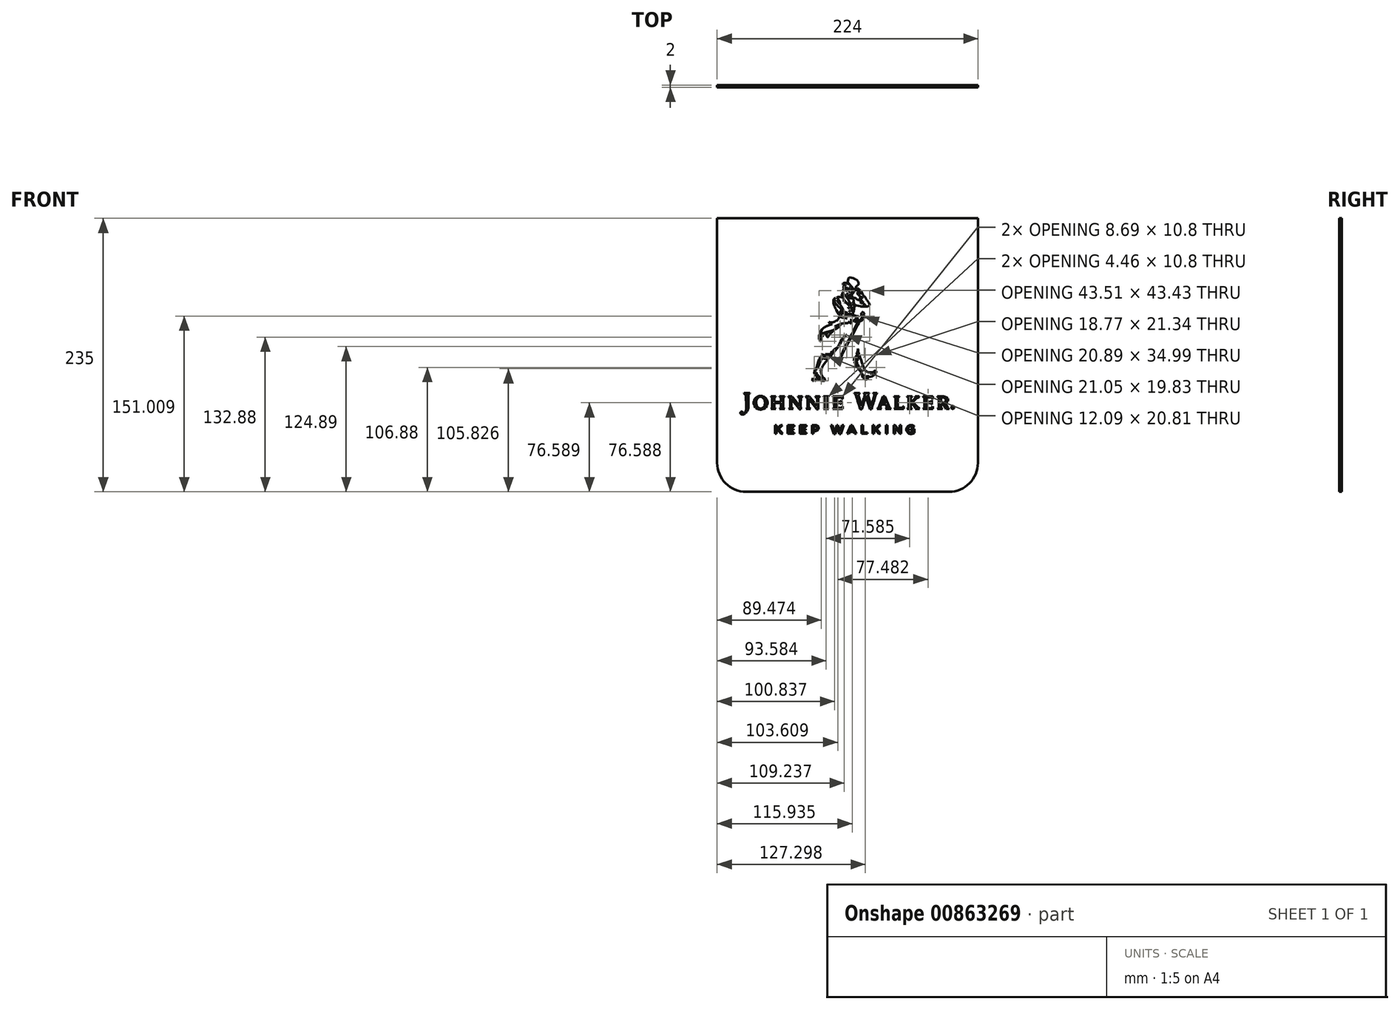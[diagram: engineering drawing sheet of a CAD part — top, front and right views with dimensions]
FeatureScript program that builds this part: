
annotation { "Feature Type Name" : "Feature", "Feature Type Description" : "" }
export const myFeature = defineFeature(function(context is Context, id is Id, definition is map)
    precondition{}
    {
        {
            var Q0;
            Q0=qCreatedBy(makeId("Front.planeOp"),FACE);
            var sketch = newSketch(context, id + "F0", { "sketchPlane" : qUnion([Q0])});
            skLineSegment(sketch, "E0", {"start": v(0.13, 0) * mm, "end": v(-86.87, 0) * mm});
            skLineSegment(sketch, "E1", {"start": v(0.13, 0) * mm, "end": v(87.13, 0) * mm});
            skLineSegment(sketch, "E2", {"start": v(0.13, 235) * mm, "end": v(-111.87, 235) * mm});
            skLineSegment(sketch, "E3", {"start": v(-111.87, 235) * mm, "end": v(-111.87, 25) * mm});
            skLineSegment(sketch, "E4", {"start": v(0.13, 235) * mm, "end": v(112.13, 235) * mm});
            skLineSegment(sketch, "E5", {"start": v(112.13, 235) * mm, "end": v(112.13, 25) * mm});
            skArc(sketch, "E6", {"start": v(-111.87, 25) * mm, "mid": v(-104.54, 7.32) * mm, "end": v(-86.87, 0) * mm});
            skArc(sketch, "E7", {"start": v(87.13, 0) * mm, "mid": v(104.81, 7.32) * mm, "end": v(112.13, 25) * mm});
            skSolve(sketch);
        }
        {
            var Q0;
            Q0=qCreatedBy(makeId("Front.planeOp"),FACE);
            var sketch = newSketch(context, id + "F1", { "sketchPlane" : qUnion([Q0])});
            skLineSegment(sketch, "E8", {"start": v(-58.86, 54.13) * mm, "end": v(-55.76, 57.34) * mm});
            skLineSegment(sketch, "E9", {"start": v(-55.76, 57.34) * mm, "end": v(-57.37, 57.34) * mm});
            skLineSegment(sketch, "E10", {"start": v(-57.37, 57.34) * mm, "end": v(-60.91, 53.59) * mm});
            skLineSegment(sketch, "E11", {"start": v(-60.91, 53.59) * mm, "end": v(-60.91, 57.34) * mm});
            skLineSegment(sketch, "E12", {"start": v(-60.91, 57.34) * mm, "end": v(-62.22, 57.34) * mm});
            skLineSegment(sketch, "E13", {"start": v(-62.22, 57.34) * mm, "end": v(-62.22, 49.88) * mm});
            skLineSegment(sketch, "E14", {"start": v(-62.22, 49.88) * mm, "end": v(-60.91, 49.88) * mm});
            skLineSegment(sketch, "E15", {"start": v(-60.91, 49.88) * mm, "end": v(-60.91, 52.04) * mm});
            skLineSegment(sketch, "E16", {"start": v(-60.91, 52.04) * mm, "end": v(-59.75, 53.24) * mm});
            skLineSegment(sketch, "E17", {"start": v(-59.75, 53.24) * mm, "end": v(-57.2, 49.88) * mm});
            skLineSegment(sketch, "E18", {"start": v(-57.2, 49.88) * mm, "end": v(-55.62, 49.88) * mm});
            skLineSegment(sketch, "E19", {"start": v(-55.62, 49.88) * mm, "end": v(-58.86, 54.13) * mm});
            skLineSegment(sketch, "E20", {"start": v(-45.72, 57.34) * mm, "end": v(-51.25, 57.34) * mm});
            skLineSegment(sketch, "E21", {"start": v(-51.25, 57.34) * mm, "end": v(-51.25, 49.88) * mm});
            skLineSegment(sketch, "E22", {"start": v(-51.25, 49.88) * mm, "end": v(-45.67, 49.88) * mm});
            skLineSegment(sketch, "E23", {"start": v(-45.67, 49.88) * mm, "end": v(-45.67, 51.05) * mm});
            skLineSegment(sketch, "E24", {"start": v(-45.67, 51.05) * mm, "end": v(-49.94, 51.05) * mm});
            skLineSegment(sketch, "E25", {"start": v(-49.94, 51.05) * mm, "end": v(-49.94, 53.06) * mm});
            skLineSegment(sketch, "E26", {"start": v(-49.94, 53.06) * mm, "end": v(-46.2, 53.06) * mm});
            skLineSegment(sketch, "E27", {"start": v(-46.2, 53.06) * mm, "end": v(-46.2, 54.23) * mm});
            skLineSegment(sketch, "E28", {"start": v(-46.2, 54.23) * mm, "end": v(-49.94, 54.23) * mm});
            skLineSegment(sketch, "E29", {"start": v(-49.94, 54.23) * mm, "end": v(-49.94, 56.17) * mm});
            skLineSegment(sketch, "E30", {"start": v(-49.94, 56.17) * mm, "end": v(-45.72, 56.17) * mm});
            skLineSegment(sketch, "E31", {"start": v(-45.72, 56.17) * mm, "end": v(-45.72, 57.34) * mm});
            skLineSegment(sketch, "E32", {"start": v(-35.3, 57.34) * mm, "end": v(-40.82, 57.34) * mm});
            skLineSegment(sketch, "E33", {"start": v(-40.82, 57.34) * mm, "end": v(-40.82, 49.88) * mm});
            skLineSegment(sketch, "E34", {"start": v(-40.82, 49.88) * mm, "end": v(-35.24, 49.88) * mm});
            skLineSegment(sketch, "E35", {"start": v(-35.24, 49.88) * mm, "end": v(-35.24, 51.05) * mm});
            skLineSegment(sketch, "E36", {"start": v(-35.24, 51.05) * mm, "end": v(-39.52, 51.05) * mm});
            skLineSegment(sketch, "E37", {"start": v(-39.52, 51.05) * mm, "end": v(-39.52, 53.06) * mm});
            skLineSegment(sketch, "E38", {"start": v(-39.52, 53.06) * mm, "end": v(-35.77, 53.06) * mm});
            skLineSegment(sketch, "E39", {"start": v(-35.77, 53.06) * mm, "end": v(-35.77, 54.23) * mm});
            skLineSegment(sketch, "E40", {"start": v(-35.77, 54.23) * mm, "end": v(-39.52, 54.23) * mm});
            skLineSegment(sketch, "E41", {"start": v(-39.52, 54.23) * mm, "end": v(-39.52, 56.17) * mm});
            skLineSegment(sketch, "E42", {"start": v(-39.52, 56.17) * mm, "end": v(-35.3, 56.17) * mm});
            skLineSegment(sketch, "E43", {"start": v(-35.3, 56.17) * mm, "end": v(-35.3, 57.34) * mm});
            skLineSegment(sketch, "E44", {"start": v(-24.63, 54.83) * mm, "end": v(-24.63, 55.1) * mm});
            skLineSegment(sketch, "E45", {"start": v(-24.63, 55.1) * mm, "end": v(-24.83, 55.87) * mm});
            skLineSegment(sketch, "E46", {"start": v(-24.83, 55.87) * mm, "end": v(-25.4, 56.66) * mm});
            skLineSegment(sketch, "E47", {"start": v(-25.4, 56.66) * mm, "end": v(-26.28, 57.16) * mm});
            skLineSegment(sketch, "E48", {"start": v(-26.28, 57.16) * mm, "end": v(-27.17, 57.34) * mm});
            skLineSegment(sketch, "E49", {"start": v(-27.17, 57.34) * mm, "end": v(-27.46, 57.34) * mm});
            skLineSegment(sketch, "E50", {"start": v(-27.46, 57.34) * mm, "end": v(-30.4, 57.34) * mm});
            skLineSegment(sketch, "E51", {"start": v(-30.4, 57.34) * mm, "end": v(-30.4, 49.88) * mm});
            skLineSegment(sketch, "E52", {"start": v(-30.4, 49.88) * mm, "end": v(-29.09, 49.88) * mm});
            skLineSegment(sketch, "E53", {"start": v(-29.09, 49.88) * mm, "end": v(-29.09, 52.28) * mm});
            skLineSegment(sketch, "E54", {"start": v(-29.09, 52.28) * mm, "end": v(-27.6, 52.28) * mm});
            skLineSegment(sketch, "E55", {"start": v(-27.6, 52.28) * mm, "end": v(-27.32, 52.28) * mm});
            skLineSegment(sketch, "E56", {"start": v(-27.32, 52.28) * mm, "end": v(-26.45, 52.44) * mm});
            skLineSegment(sketch, "E57", {"start": v(-26.45, 52.44) * mm, "end": v(-25.5, 52.93) * mm});
            skLineSegment(sketch, "E58", {"start": v(-25.5, 52.93) * mm, "end": v(-24.86, 53.73) * mm});
            skLineSegment(sketch, "E59", {"start": v(-24.86, 53.73) * mm, "end": v(-24.63, 54.56) * mm});
            skLineSegment(sketch, "E60", {"start": v(-24.63, 54.56) * mm, "end": v(-24.63, 54.83) * mm});
            skLineSegment(sketch, "E61", {"start": v(-25.96, 54.8) * mm, "end": v(-25.96, 54.67) * mm});
            skLineSegment(sketch, "E62", {"start": v(-25.96, 54.67) * mm, "end": v(-26.07, 54.26) * mm});
            skLineSegment(sketch, "E63", {"start": v(-26.07, 54.26) * mm, "end": v(-26.39, 53.83) * mm});
            skLineSegment(sketch, "E64", {"start": v(-26.39, 53.83) * mm, "end": v(-26.9, 53.56) * mm});
            skLineSegment(sketch, "E65", {"start": v(-26.9, 53.56) * mm, "end": v(-27.4, 53.46) * mm});
            skLineSegment(sketch, "E66", {"start": v(-27.4, 53.46) * mm, "end": v(-27.57, 53.46) * mm});
            skLineSegment(sketch, "E67", {"start": v(-27.57, 53.46) * mm, "end": v(-29.09, 53.46) * mm});
            skLineSegment(sketch, "E68", {"start": v(-29.09, 53.46) * mm, "end": v(-29.09, 56.14) * mm});
            skLineSegment(sketch, "E69", {"start": v(-29.09, 56.14) * mm, "end": v(-27.57, 56.14) * mm});
            skLineSegment(sketch, "E70", {"start": v(-27.57, 56.14) * mm, "end": v(-27.4, 56.14) * mm});
            skLineSegment(sketch, "E71", {"start": v(-27.4, 56.14) * mm, "end": v(-26.9, 56.06) * mm});
            skLineSegment(sketch, "E72", {"start": v(-26.9, 56.06) * mm, "end": v(-26.4, 55.8) * mm});
            skLineSegment(sketch, "E73", {"start": v(-26.4, 55.8) * mm, "end": v(-26.07, 55.39) * mm});
            skLineSegment(sketch, "E74", {"start": v(-26.07, 55.39) * mm, "end": v(-25.96, 54.95) * mm});
            skLineSegment(sketch, "E75", {"start": v(-25.96, 54.95) * mm, "end": v(-25.96, 54.8) * mm});
            skLineSegment(sketch, "E76", {"start": v(-11.08, 51.8) * mm, "end": v(-12.86, 57.34) * mm});
            skLineSegment(sketch, "E77", {"start": v(-12.86, 57.34) * mm, "end": v(-14.27, 57.34) * mm});
            skLineSegment(sketch, "E78", {"start": v(-14.27, 57.34) * mm, "end": v(-11.68, 49.83) * mm});
            skLineSegment(sketch, "E79", {"start": v(-11.68, 49.83) * mm, "end": v(-10.55, 49.83) * mm});
            skLineSegment(sketch, "E80", {"start": v(-10.55, 49.83) * mm, "end": v(-8.71, 55.18) * mm});
            skLineSegment(sketch, "E81", {"start": v(-8.71, 55.18) * mm, "end": v(-6.88, 49.83) * mm});
            skLineSegment(sketch, "E82", {"start": v(-6.88, 49.83) * mm, "end": v(-5.75, 49.83) * mm});
            skLineSegment(sketch, "E83", {"start": v(-5.75, 49.83) * mm, "end": v(-3.15, 57.34) * mm});
            skLineSegment(sketch, "E84", {"start": v(-3.15, 57.34) * mm, "end": v(-4.53, 57.34) * mm});
            skLineSegment(sketch, "E85", {"start": v(-4.53, 57.34) * mm, "end": v(-6.3, 51.8) * mm});
            skLineSegment(sketch, "E86", {"start": v(-6.3, 51.8) * mm, "end": v(-8.14, 57.36) * mm});
            skLineSegment(sketch, "E87", {"start": v(-8.14, 57.36) * mm, "end": v(-9.25, 57.36) * mm});
            skLineSegment(sketch, "E88", {"start": v(-9.25, 57.36) * mm, "end": v(-11.08, 51.8) * mm});
            skLineSegment(sketch, "E89", {"start": v(4.31, 57.39) * mm, "end": v(3.1, 57.39) * mm});
            skLineSegment(sketch, "E90", {"start": v(3.1, 57.39) * mm, "end": v(-0.18, 49.88) * mm});
            skLineSegment(sketch, "E91", {"start": v(-0.18, 49.88) * mm, "end": v(1.16, 49.88) * mm});
            skLineSegment(sketch, "E92", {"start": v(1.16, 49.88) * mm, "end": v(1.93, 51.68) * mm});
            skLineSegment(sketch, "E93", {"start": v(1.93, 51.68) * mm, "end": v(5.46, 51.68) * mm});
            skLineSegment(sketch, "E94", {"start": v(5.46, 51.68) * mm, "end": v(6.2, 49.88) * mm});
            skLineSegment(sketch, "E95", {"start": v(6.2, 49.88) * mm, "end": v(7.6, 49.88) * mm});
            skLineSegment(sketch, "E96", {"start": v(7.6, 49.88) * mm, "end": v(4.31, 57.39) * mm});
            skLineSegment(sketch, "E97", {"start": v(4.97, 52.84) * mm, "end": v(2.4, 52.84) * mm});
            skLineSegment(sketch, "E98", {"start": v(2.4, 52.84) * mm, "end": v(3.69, 55.82) * mm});
            skLineSegment(sketch, "E99", {"start": v(3.69, 55.82) * mm, "end": v(4.97, 52.84) * mm});
            skLineSegment(sketch, "E100", {"start": v(12.05, 49.88) * mm, "end": v(17.28, 49.88) * mm});
            skLineSegment(sketch, "E101", {"start": v(17.28, 49.88) * mm, "end": v(17.28, 51.07) * mm});
            skLineSegment(sketch, "E102", {"start": v(17.28, 51.07) * mm, "end": v(13.36, 51.07) * mm});
            skLineSegment(sketch, "E103", {"start": v(13.36, 51.07) * mm, "end": v(13.36, 57.34) * mm});
            skLineSegment(sketch, "E104", {"start": v(13.36, 57.34) * mm, "end": v(12.05, 57.34) * mm});
            skLineSegment(sketch, "E105", {"start": v(12.05, 57.34) * mm, "end": v(12.05, 49.88) * mm});
            skLineSegment(sketch, "E106", {"start": v(25.13, 54.13) * mm, "end": v(28.23, 57.34) * mm});
            skLineSegment(sketch, "E107", {"start": v(28.23, 57.34) * mm, "end": v(26.63, 57.34) * mm});
            skLineSegment(sketch, "E108", {"start": v(26.63, 57.34) * mm, "end": v(23.08, 53.59) * mm});
            skLineSegment(sketch, "E109", {"start": v(23.08, 53.59) * mm, "end": v(23.08, 57.34) * mm});
            skLineSegment(sketch, "E110", {"start": v(23.08, 57.34) * mm, "end": v(21.77, 57.34) * mm});
            skLineSegment(sketch, "E111", {"start": v(21.77, 57.34) * mm, "end": v(21.77, 49.88) * mm});
            skLineSegment(sketch, "E112", {"start": v(21.77, 49.88) * mm, "end": v(23.08, 49.88) * mm});
            skLineSegment(sketch, "E113", {"start": v(23.08, 49.88) * mm, "end": v(23.08, 52.04) * mm});
            skLineSegment(sketch, "E114", {"start": v(23.08, 52.04) * mm, "end": v(24.24, 53.24) * mm});
            skLineSegment(sketch, "E115", {"start": v(24.24, 53.24) * mm, "end": v(26.79, 49.88) * mm});
            skLineSegment(sketch, "E116", {"start": v(26.79, 49.88) * mm, "end": v(28.37, 49.88) * mm});
            skLineSegment(sketch, "E117", {"start": v(28.37, 49.88) * mm, "end": v(25.13, 54.13) * mm});
            skLineSegment(sketch, "E118", {"start": v(33, 49.88) * mm, "end": v(34.31, 49.88) * mm});
            skLineSegment(sketch, "E119", {"start": v(34.31, 49.88) * mm, "end": v(34.31, 57.34) * mm});
            skLineSegment(sketch, "E120", {"start": v(34.31, 57.34) * mm, "end": v(33, 57.34) * mm});
            skLineSegment(sketch, "E121", {"start": v(33, 57.34) * mm, "end": v(33, 49.88) * mm});
            skLineSegment(sketch, "E122", {"start": v(44.97, 52.18) * mm, "end": v(40.98, 57.34) * mm});
            skLineSegment(sketch, "E123", {"start": v(40.98, 57.34) * mm, "end": v(39.76, 57.34) * mm});
            skLineSegment(sketch, "E124", {"start": v(39.76, 57.34) * mm, "end": v(39.76, 49.88) * mm});
            skLineSegment(sketch, "E125", {"start": v(39.76, 49.88) * mm, "end": v(41.05, 49.88) * mm});
            skLineSegment(sketch, "E126", {"start": v(41.05, 49.88) * mm, "end": v(41.05, 55.18) * mm});
            skLineSegment(sketch, "E127", {"start": v(41.05, 55.18) * mm, "end": v(45.16, 49.88) * mm});
            skLineSegment(sketch, "E128", {"start": v(45.16, 49.88) * mm, "end": v(46.26, 49.88) * mm});
            skLineSegment(sketch, "E129", {"start": v(46.26, 49.88) * mm, "end": v(46.26, 57.34) * mm});
            skLineSegment(sketch, "E130", {"start": v(46.26, 57.34) * mm, "end": v(44.97, 57.34) * mm});
            skLineSegment(sketch, "E131", {"start": v(44.97, 57.34) * mm, "end": v(44.97, 52.18) * mm});
            skLineSegment(sketch, "E132", {"start": v(57.65, 50.91) * mm, "end": v(57.65, 54.05) * mm});
            skLineSegment(sketch, "E133", {"start": v(57.65, 54.05) * mm, "end": v(54.48, 54.05) * mm});
            skLineSegment(sketch, "E134", {"start": v(54.48, 54.05) * mm, "end": v(54.48, 52.9) * mm});
            skLineSegment(sketch, "E135", {"start": v(54.48, 52.9) * mm, "end": v(56.39, 52.9) * mm});
            skLineSegment(sketch, "E136", {"start": v(56.39, 52.9) * mm, "end": v(56.39, 51.51) * mm});
            skLineSegment(sketch, "E137", {"start": v(56.39, 51.51) * mm, "end": v(56.27, 51.43) * mm});
            skLineSegment(sketch, "E138", {"start": v(56.27, 51.43) * mm, "end": v(55.58, 51.1) * mm});
            skLineSegment(sketch, "E139", {"start": v(55.58, 51.1) * mm, "end": v(54.83, 50.95) * mm});
            skLineSegment(sketch, "E140", {"start": v(54.83, 50.95) * mm, "end": v(54.59, 50.95) * mm});
            skLineSegment(sketch, "E141", {"start": v(54.59, 50.95) * mm, "end": v(54.33, 50.95) * mm});
            skLineSegment(sketch, "E142", {"start": v(54.33, 50.95) * mm, "end": v(53.55, 51.15) * mm});
            skLineSegment(sketch, "E143", {"start": v(53.55, 51.15) * mm, "end": v(52.75, 51.7) * mm});
            skLineSegment(sketch, "E144", {"start": v(52.75, 51.7) * mm, "end": v(52.23, 52.55) * mm});
            skLineSegment(sketch, "E145", {"start": v(52.23, 52.55) * mm, "end": v(52.05, 53.35) * mm});
            skLineSegment(sketch, "E146", {"start": v(52.05, 53.35) * mm, "end": v(52.05, 53.62) * mm});
            skLineSegment(sketch, "E147", {"start": v(52.05, 53.62) * mm, "end": v(52.05, 53.88) * mm});
            skLineSegment(sketch, "E148", {"start": v(52.05, 53.88) * mm, "end": v(52.23, 54.64) * mm});
            skLineSegment(sketch, "E149", {"start": v(52.23, 54.64) * mm, "end": v(52.74, 55.49) * mm});
            skLineSegment(sketch, "E150", {"start": v(52.74, 55.49) * mm, "end": v(53.5, 56.05) * mm});
            skLineSegment(sketch, "E151", {"start": v(53.5, 56.05) * mm, "end": v(54.23, 56.26) * mm});
            skLineSegment(sketch, "E152", {"start": v(54.23, 56.26) * mm, "end": v(54.47, 56.26) * mm});
            skLineSegment(sketch, "E153", {"start": v(54.47, 56.26) * mm, "end": v(54.76, 56.26) * mm});
            skLineSegment(sketch, "E154", {"start": v(54.76, 56.26) * mm, "end": v(55.65, 56.05) * mm});
            skLineSegment(sketch, "E155", {"start": v(55.65, 56.05) * mm, "end": v(56.41, 55.59) * mm});
            skLineSegment(sketch, "E156", {"start": v(56.41, 55.59) * mm, "end": v(56.56, 55.46) * mm});
            skLineSegment(sketch, "E157", {"start": v(56.56, 55.46) * mm, "end": v(57.38, 56.46) * mm});
            skLineSegment(sketch, "E158", {"start": v(57.38, 56.46) * mm, "end": v(57.2, 56.62) * mm});
            skLineSegment(sketch, "E159", {"start": v(57.2, 56.62) * mm, "end": v(56.15, 57.2) * mm});
            skLineSegment(sketch, "E160", {"start": v(56.15, 57.2) * mm, "end": v(54.93, 57.47) * mm});
            skLineSegment(sketch, "E161", {"start": v(54.93, 57.47) * mm, "end": v(54.52, 57.47) * mm});
            skLineSegment(sketch, "E162", {"start": v(54.52, 57.47) * mm, "end": v(54.13, 57.47) * mm});
            skLineSegment(sketch, "E163", {"start": v(54.13, 57.47) * mm, "end": v(52.97, 57.16) * mm});
            skLineSegment(sketch, "E164", {"start": v(52.97, 57.16) * mm, "end": v(51.76, 56.32) * mm});
            skLineSegment(sketch, "E165", {"start": v(51.76, 56.32) * mm, "end": v(50.96, 55.09) * mm});
            skLineSegment(sketch, "E166", {"start": v(50.96, 55.09) * mm, "end": v(50.68, 53.97) * mm});
            skLineSegment(sketch, "E167", {"start": v(50.68, 53.97) * mm, "end": v(50.68, 53.6) * mm});
            skLineSegment(sketch, "E168", {"start": v(50.68, 53.6) * mm, "end": v(50.68, 53.22) * mm});
            skLineSegment(sketch, "E169", {"start": v(50.68, 53.22) * mm, "end": v(50.95, 52.08) * mm});
            skLineSegment(sketch, "E170", {"start": v(50.95, 52.08) * mm, "end": v(51.73, 50.86) * mm});
            skLineSegment(sketch, "E171", {"start": v(51.73, 50.86) * mm, "end": v(52.95, 50.05) * mm});
            skLineSegment(sketch, "E172", {"start": v(52.95, 50.05) * mm, "end": v(54.14, 49.76) * mm});
            skLineSegment(sketch, "E173", {"start": v(54.14, 49.76) * mm, "end": v(54.54, 49.76) * mm});
            skLineSegment(sketch, "E174", {"start": v(54.54, 49.76) * mm, "end": v(54.99, 49.76) * mm});
            skLineSegment(sketch, "E175", {"start": v(54.99, 49.76) * mm, "end": v(56.32, 50.1) * mm});
            skLineSegment(sketch, "E176", {"start": v(56.32, 50.1) * mm, "end": v(57.47, 50.76) * mm});
            skLineSegment(sketch, "E177", {"start": v(57.47, 50.76) * mm, "end": v(57.65, 50.91) * mm});
            skLineSegment(sketch, "E178", {"start": v(-27.51, 81.88) * mm, "end": v(-26.05, 80.76) * mm});
            skLineSegment(sketch, "E179", {"start": v(-26.05, 80.76) * mm, "end": v(-26.05, 80.5) * mm});
            skLineSegment(sketch, "E180", {"start": v(-26.05, 80.5) * mm, "end": v(-26, 77.76) * mm});
            skLineSegment(sketch, "E181", {"start": v(-26, 77.76) * mm, "end": v(-26, 77.46) * mm});
            skLineSegment(sketch, "E182", {"start": v(-26, 77.46) * mm, "end": v(-26, 77.16) * mm});
            skLineSegment(sketch, "E183", {"start": v(-26, 77.16) * mm, "end": v(-25.98, 74.54) * mm});
            skLineSegment(sketch, "E184", {"start": v(-25.98, 74.54) * mm, "end": v(-25.98, 73.67) * mm});
            skLineSegment(sketch, "E185", {"start": v(-25.98, 73.67) * mm, "end": v(-26.2, 73.96) * mm});
            skLineSegment(sketch, "E186", {"start": v(-26.2, 73.96) * mm, "end": v(-27.25, 75.3) * mm});
            skLineSegment(sketch, "E187", {"start": v(-27.25, 75.3) * mm, "end": v(-28.21, 76.5) * mm});
            skLineSegment(sketch, "E188", {"start": v(-28.21, 76.5) * mm, "end": v(-28.4, 76.74) * mm});
            skLineSegment(sketch, "E189", {"start": v(-28.4, 76.74) * mm, "end": v(-28.57, 76.96) * mm});
            skLineSegment(sketch, "E190", {"start": v(-28.57, 76.96) * mm, "end": v(-30.17, 78.96) * mm});
            skLineSegment(sketch, "E191", {"start": v(-30.17, 78.96) * mm, "end": v(-30.3, 79.12) * mm});
            skLineSegment(sketch, "E192", {"start": v(-30.3, 79.12) * mm, "end": v(-30.45, 79.3) * mm});
            skLineSegment(sketch, "E193", {"start": v(-30.45, 79.3) * mm, "end": v(-31.63, 80.77) * mm});
            skLineSegment(sketch, "E194", {"start": v(-31.63, 80.77) * mm, "end": v(-31.72, 80.9) * mm});
            skLineSegment(sketch, "E195", {"start": v(-31.72, 80.9) * mm, "end": v(-31.82, 81) * mm});
            skLineSegment(sketch, "E196", {"start": v(-31.82, 81) * mm, "end": v(-32.2, 81.51) * mm});
            skLineSegment(sketch, "E197", {"start": v(-32.2, 81.51) * mm, "end": v(-32.48, 81.93) * mm});
            skLineSegment(sketch, "E198", {"start": v(-32.48, 81.93) * mm, "end": v(-32.52, 82) * mm});
            skLineSegment(sketch, "E199", {"start": v(-32.52, 82) * mm, "end": v(-35.74, 82) * mm});
            skLineSegment(sketch, "E200", {"start": v(-35.74, 82) * mm, "end": v(-35.74, 81.88) * mm});
            skLineSegment(sketch, "E201", {"start": v(-35.74, 81.88) * mm, "end": v(-34.22, 80.8) * mm});
            skLineSegment(sketch, "E202", {"start": v(-34.22, 80.8) * mm, "end": v(-34.2, 79.93) * mm});
            skLineSegment(sketch, "E203", {"start": v(-34.2, 79.93) * mm, "end": v(-34.14, 76.09) * mm});
            skLineSegment(sketch, "E204", {"start": v(-34.14, 76.09) * mm, "end": v(-34.2, 72.88) * mm});
            skLineSegment(sketch, "E205", {"start": v(-34.2, 72.88) * mm, "end": v(-34.22, 72.34) * mm});
            skLineSegment(sketch, "E206", {"start": v(-34.22, 72.34) * mm, "end": v(-35.49, 71.3) * mm});
            skLineSegment(sketch, "E207", {"start": v(-35.49, 71.3) * mm, "end": v(-35.49, 71.15) * mm});
            skLineSegment(sketch, "E208", {"start": v(-35.49, 71.15) * mm, "end": v(-31.79, 71.15) * mm});
            skLineSegment(sketch, "E209", {"start": v(-31.79, 71.15) * mm, "end": v(-31.79, 71.3) * mm});
            skLineSegment(sketch, "E210", {"start": v(-31.79, 71.3) * mm, "end": v(-33.18, 72.34) * mm});
            skLineSegment(sketch, "E211", {"start": v(-33.18, 72.34) * mm, "end": v(-33.18, 72.34) * mm});
            skLineSegment(sketch, "E212", {"start": v(-33.18, 72.34) * mm, "end": v(-33.2, 72.97) * mm});
            skLineSegment(sketch, "E213", {"start": v(-33.2, 72.97) * mm, "end": v(-33.3, 78.1) * mm});
            skLineSegment(sketch, "E214", {"start": v(-33.3, 78.1) * mm, "end": v(-33.3, 79.8) * mm});
            skLineSegment(sketch, "E215", {"start": v(-33.3, 79.8) * mm, "end": v(-26.91, 71.77) * mm});
            skLineSegment(sketch, "E216", {"start": v(-26.91, 71.77) * mm, "end": v(-26.9, 71.74) * mm});
            skLineSegment(sketch, "E217", {"start": v(-26.9, 71.74) * mm, "end": v(-26.65, 71.44) * mm});
            skLineSegment(sketch, "E218", {"start": v(-26.65, 71.44) * mm, "end": v(-26.62, 71.4) * mm});
            skLineSegment(sketch, "E219", {"start": v(-26.62, 71.4) * mm, "end": v(-26.6, 71.38) * mm});
            skLineSegment(sketch, "E220", {"start": v(-26.6, 71.38) * mm, "end": v(-26.47, 71.16) * mm});
            skLineSegment(sketch, "E221", {"start": v(-26.47, 71.16) * mm, "end": v(-26.47, 71.1) * mm});
            skLineSegment(sketch, "E222", {"start": v(-26.47, 71.1) * mm, "end": v(-25, 71.1) * mm});
            skLineSegment(sketch, "E223", {"start": v(-25, 71.1) * mm, "end": v(-25.01, 71.44) * mm});
            skLineSegment(sketch, "E224", {"start": v(-25.01, 71.44) * mm, "end": v(-25.13, 74.54) * mm});
            skLineSegment(sketch, "E225", {"start": v(-25.13, 74.54) * mm, "end": v(-25.13, 75.58) * mm});
            skLineSegment(sketch, "E226", {"start": v(-25.13, 75.58) * mm, "end": v(-25.14, 75.97) * mm});
            skLineSegment(sketch, "E227", {"start": v(-25.14, 75.97) * mm, "end": v(-25.09, 80.3) * mm});
            skLineSegment(sketch, "E228", {"start": v(-25.09, 80.3) * mm, "end": v(-25.07, 80.76) * mm});
            skLineSegment(sketch, "E229", {"start": v(-25.07, 80.76) * mm, "end": v(-23.8, 81.88) * mm});
            skLineSegment(sketch, "E230", {"start": v(-23.8, 81.88) * mm, "end": v(-23.8, 82) * mm});
            skLineSegment(sketch, "E231", {"start": v(-23.8, 82) * mm, "end": v(-27.51, 82) * mm});
            skLineSegment(sketch, "E232", {"start": v(-27.51, 82) * mm, "end": v(-27.51, 81.88) * mm});
            skLineSegment(sketch, "E233", {"start": v(-17.36, 81) * mm, "end": v(-16.11, 81.88) * mm});
            skLineSegment(sketch, "E234", {"start": v(-16.11, 81.88) * mm, "end": v(-16.11, 81.99) * mm});
            skLineSegment(sketch, "E235", {"start": v(-16.11, 81.99) * mm, "end": v(-20.47, 81.99) * mm});
            skLineSegment(sketch, "E236", {"start": v(-20.47, 81.99) * mm, "end": v(-20.47, 81.88) * mm});
            skLineSegment(sketch, "E237", {"start": v(-20.47, 81.88) * mm, "end": v(-19.22, 81) * mm});
            skLineSegment(sketch, "E238", {"start": v(-19.22, 81) * mm, "end": v(-19.22, 80.28) * mm});
            skLineSegment(sketch, "E239", {"start": v(-19.22, 80.28) * mm, "end": v(-19.22, 72.97) * mm});
            skLineSegment(sketch, "E240", {"start": v(-19.22, 72.97) * mm, "end": v(-19.22, 72.23) * mm});
            skLineSegment(sketch, "E241", {"start": v(-19.22, 72.23) * mm, "end": v(-20.51, 71.32) * mm});
            skLineSegment(sketch, "E242", {"start": v(-20.51, 71.32) * mm, "end": v(-20.51, 71.19) * mm});
            skLineSegment(sketch, "E243", {"start": v(-20.51, 71.19) * mm, "end": v(-16.06, 71.19) * mm});
            skLineSegment(sketch, "E244", {"start": v(-16.06, 71.19) * mm, "end": v(-16.06, 71.32) * mm});
            skLineSegment(sketch, "E245", {"start": v(-16.06, 71.32) * mm, "end": v(-17.36, 72.23) * mm});
            skLineSegment(sketch, "E246", {"start": v(-17.36, 72.23) * mm, "end": v(-17.37, 72.93) * mm});
            skLineSegment(sketch, "E247", {"start": v(-17.37, 72.93) * mm, "end": v(-17.37, 80.24) * mm});
            skLineSegment(sketch, "E248", {"start": v(-17.37, 80.24) * mm, "end": v(-17.36, 81) * mm});
            skLineSegment(sketch, "E249", {"start": v(-5.1, 72.11) * mm, "end": v(-5.49, 72.1) * mm});
            skLineSegment(sketch, "E250", {"start": v(-5.49, 72.1) * mm, "end": v(-9.16, 72.1) * mm});
            skLineSegment(sketch, "E251", {"start": v(-9.16, 72.1) * mm, "end": v(-9.51, 72.11) * mm});
            skLineSegment(sketch, "E252", {"start": v(-9.51, 72.11) * mm, "end": v(-9.52, 72.47) * mm});
            skLineSegment(sketch, "E253", {"start": v(-9.52, 72.47) * mm, "end": v(-9.52, 76.02) * mm});
            skLineSegment(sketch, "E254", {"start": v(-9.52, 76.02) * mm, "end": v(-9.51, 76.37) * mm});
            skLineSegment(sketch, "E255", {"start": v(-9.51, 76.37) * mm, "end": v(-9.3, 76.38) * mm});
            skLineSegment(sketch, "E256", {"start": v(-9.3, 76.38) * mm, "end": v(-8.05, 76.4) * mm});
            skLineSegment(sketch, "E257", {"start": v(-8.05, 76.4) * mm, "end": v(-6.6, 76.4) * mm});
            skLineSegment(sketch, "E258", {"start": v(-6.6, 76.4) * mm, "end": v(-6.12, 76.4) * mm});
            skLineSegment(sketch, "E259", {"start": v(-6.12, 76.4) * mm, "end": v(-5.28, 75.17) * mm});
            skLineSegment(sketch, "E260", {"start": v(-5.28, 75.17) * mm, "end": v(-5.16, 75.17) * mm});
            skLineSegment(sketch, "E261", {"start": v(-5.16, 75.17) * mm, "end": v(-5.16, 78.51) * mm});
            skLineSegment(sketch, "E262", {"start": v(-5.16, 78.51) * mm, "end": v(-5.28, 78.51) * mm});
            skLineSegment(sketch, "E263", {"start": v(-5.28, 78.51) * mm, "end": v(-6.12, 77.25) * mm});
            skLineSegment(sketch, "E264", {"start": v(-6.12, 77.25) * mm, "end": v(-6.7, 77.25) * mm});
            skLineSegment(sketch, "E265", {"start": v(-6.7, 77.25) * mm, "end": v(-8.41, 77.27) * mm});
            skLineSegment(sketch, "E266", {"start": v(-8.41, 77.27) * mm, "end": v(-9.45, 77.3) * mm});
            skLineSegment(sketch, "E267", {"start": v(-9.45, 77.3) * mm, "end": v(-9.54, 77.3) * mm});
            skLineSegment(sketch, "E268", {"start": v(-9.54, 77.3) * mm, "end": v(-9.54, 77.45) * mm});
            skLineSegment(sketch, "E269", {"start": v(-9.54, 77.45) * mm, "end": v(-9.58, 78.72) * mm});
            skLineSegment(sketch, "E270", {"start": v(-9.58, 78.72) * mm, "end": v(-9.58, 79.14) * mm});
            skLineSegment(sketch, "E271", {"start": v(-9.58, 79.14) * mm, "end": v(-9.58, 79.62) * mm});
            skLineSegment(sketch, "E272", {"start": v(-9.58, 79.62) * mm, "end": v(-9.56, 80.88) * mm});
            skLineSegment(sketch, "E273", {"start": v(-9.56, 80.88) * mm, "end": v(-9.55, 81.04) * mm});
            skLineSegment(sketch, "E274", {"start": v(-9.55, 81.04) * mm, "end": v(-9.39, 81.06) * mm});
            skLineSegment(sketch, "E275", {"start": v(-9.39, 81.06) * mm, "end": v(-7.92, 81.1) * mm});
            skLineSegment(sketch, "E276", {"start": v(-7.92, 81.1) * mm, "end": v(-7.43, 81.1) * mm});
            skLineSegment(sketch, "E277", {"start": v(-7.43, 81.1) * mm, "end": v(-6.87, 81.1) * mm});
            skLineSegment(sketch, "E278", {"start": v(-6.87, 81.1) * mm, "end": v(-5.6, 81.1) * mm});
            skLineSegment(sketch, "E279", {"start": v(-5.6, 81.1) * mm, "end": v(-5.16, 81.1) * mm});
            skLineSegment(sketch, "E280", {"start": v(-5.16, 81.1) * mm, "end": v(-4.26, 79.85) * mm});
            skLineSegment(sketch, "E281", {"start": v(-4.26, 79.85) * mm, "end": v(-4.14, 79.85) * mm});
            skLineSegment(sketch, "E282", {"start": v(-4.14, 79.85) * mm, "end": v(-4.14, 82) * mm});
            skLineSegment(sketch, "E283", {"start": v(-4.14, 82) * mm, "end": v(-12.6, 82) * mm});
            skLineSegment(sketch, "E284", {"start": v(-12.6, 82) * mm, "end": v(-12.6, 81.88) * mm});
            skLineSegment(sketch, "E285", {"start": v(-12.6, 81.88) * mm, "end": v(-11.37, 81) * mm});
            skLineSegment(sketch, "E286", {"start": v(-11.37, 81) * mm, "end": v(-11.37, 80.37) * mm});
            skLineSegment(sketch, "E287", {"start": v(-11.37, 80.37) * mm, "end": v(-11.35, 76.92) * mm});
            skLineSegment(sketch, "E288", {"start": v(-11.35, 76.92) * mm, "end": v(-11.37, 73.06) * mm});
            skLineSegment(sketch, "E289", {"start": v(-11.37, 73.06) * mm, "end": v(-11.37, 72.23) * mm});
            skLineSegment(sketch, "E290", {"start": v(-11.37, 72.23) * mm, "end": v(-12.6, 71.33) * mm});
            skLineSegment(sketch, "E291", {"start": v(-12.6, 71.33) * mm, "end": v(-12.6, 71.19) * mm});
            skLineSegment(sketch, "E292", {"start": v(-12.6, 71.19) * mm, "end": v(-3.92, 71.19) * mm});
            skLineSegment(sketch, "E293", {"start": v(-3.92, 71.19) * mm, "end": v(-3.92, 73.58) * mm});
            skLineSegment(sketch, "E294", {"start": v(-3.92, 73.58) * mm, "end": v(-4.04, 73.58) * mm});
            skLineSegment(sketch, "E295", {"start": v(-4.04, 73.58) * mm, "end": v(-5.1, 72.11) * mm});
            skLineSegment(sketch, "E296", {"start": v(-42.45, 81.88) * mm, "end": v(-41.02, 80.76) * mm});
            skLineSegment(sketch, "E297", {"start": v(-41.02, 80.76) * mm, "end": v(-41.01, 80.5) * mm});
            skLineSegment(sketch, "E298", {"start": v(-41.01, 80.5) * mm, "end": v(-40.98, 77.76) * mm});
            skLineSegment(sketch, "E299", {"start": v(-40.98, 77.76) * mm, "end": v(-40.97, 77.46) * mm});
            skLineSegment(sketch, "E300", {"start": v(-40.97, 77.46) * mm, "end": v(-40.97, 77.16) * mm});
            skLineSegment(sketch, "E301", {"start": v(-40.97, 77.16) * mm, "end": v(-40.95, 74.54) * mm});
            skLineSegment(sketch, "E302", {"start": v(-40.95, 74.54) * mm, "end": v(-40.95, 73.67) * mm});
            skLineSegment(sketch, "E303", {"start": v(-40.95, 73.67) * mm, "end": v(-41.17, 73.96) * mm});
            skLineSegment(sketch, "E304", {"start": v(-41.17, 73.96) * mm, "end": v(-43.15, 76.5) * mm});
            skLineSegment(sketch, "E305", {"start": v(-43.15, 76.5) * mm, "end": v(-43.33, 76.74) * mm});
            skLineSegment(sketch, "E306", {"start": v(-43.33, 76.74) * mm, "end": v(-43.52, 76.96) * mm});
            skLineSegment(sketch, "E307", {"start": v(-43.52, 76.96) * mm, "end": v(-45.14, 78.96) * mm});
            skLineSegment(sketch, "E308", {"start": v(-45.14, 78.96) * mm, "end": v(-45.28, 79.12) * mm});
            skLineSegment(sketch, "E309", {"start": v(-45.28, 79.12) * mm, "end": v(-45.42, 79.3) * mm});
            skLineSegment(sketch, "E310", {"start": v(-45.42, 79.3) * mm, "end": v(-46.58, 80.77) * mm});
            skLineSegment(sketch, "E311", {"start": v(-46.58, 80.77) * mm, "end": v(-46.67, 80.9) * mm});
            skLineSegment(sketch, "E312", {"start": v(-46.67, 80.9) * mm, "end": v(-46.77, 81) * mm});
            skLineSegment(sketch, "E313", {"start": v(-46.77, 81) * mm, "end": v(-47.15, 81.51) * mm});
            skLineSegment(sketch, "E314", {"start": v(-47.15, 81.51) * mm, "end": v(-47.43, 81.93) * mm});
            skLineSegment(sketch, "E315", {"start": v(-47.43, 81.93) * mm, "end": v(-47.47, 82) * mm});
            skLineSegment(sketch, "E316", {"start": v(-47.47, 82) * mm, "end": v(-50.68, 82) * mm});
            skLineSegment(sketch, "E317", {"start": v(-50.68, 82) * mm, "end": v(-50.68, 81.88) * mm});
            skLineSegment(sketch, "E318", {"start": v(-50.68, 81.88) * mm, "end": v(-49.18, 80.8) * mm});
            skLineSegment(sketch, "E319", {"start": v(-49.18, 80.8) * mm, "end": v(-49.15, 79.93) * mm});
            skLineSegment(sketch, "E320", {"start": v(-49.15, 79.93) * mm, "end": v(-49.1, 76.09) * mm});
            skLineSegment(sketch, "E321", {"start": v(-49.1, 76.09) * mm, "end": v(-49.15, 72.88) * mm});
            skLineSegment(sketch, "E322", {"start": v(-49.15, 72.88) * mm, "end": v(-49.18, 72.34) * mm});
            skLineSegment(sketch, "E323", {"start": v(-49.18, 72.34) * mm, "end": v(-50.43, 71.3) * mm});
            skLineSegment(sketch, "E324", {"start": v(-50.43, 71.3) * mm, "end": v(-50.43, 71.15) * mm});
            skLineSegment(sketch, "E325", {"start": v(-50.43, 71.15) * mm, "end": v(-46.74, 71.15) * mm});
            skLineSegment(sketch, "E326", {"start": v(-46.74, 71.15) * mm, "end": v(-46.74, 71.3) * mm});
            skLineSegment(sketch, "E327", {"start": v(-46.74, 71.3) * mm, "end": v(-48.13, 72.34) * mm});
            skLineSegment(sketch, "E328", {"start": v(-48.13, 72.34) * mm, "end": v(-48.12, 72.34) * mm});
            skLineSegment(sketch, "E329", {"start": v(-48.12, 72.34) * mm, "end": v(-48.15, 72.97) * mm});
            skLineSegment(sketch, "E330", {"start": v(-48.15, 72.97) * mm, "end": v(-48.26, 78.1) * mm});
            skLineSegment(sketch, "E331", {"start": v(-48.26, 78.1) * mm, "end": v(-48.26, 79.8) * mm});
            skLineSegment(sketch, "E332", {"start": v(-48.26, 79.8) * mm, "end": v(-41.86, 71.77) * mm});
            skLineSegment(sketch, "E333", {"start": v(-41.86, 71.77) * mm, "end": v(-41.83, 71.74) * mm});
            skLineSegment(sketch, "E334", {"start": v(-41.83, 71.74) * mm, "end": v(-41.6, 71.44) * mm});
            skLineSegment(sketch, "E335", {"start": v(-41.6, 71.44) * mm, "end": v(-41.57, 71.4) * mm});
            skLineSegment(sketch, "E336", {"start": v(-41.57, 71.4) * mm, "end": v(-41.55, 71.38) * mm});
            skLineSegment(sketch, "E337", {"start": v(-41.55, 71.38) * mm, "end": v(-41.42, 71.16) * mm});
            skLineSegment(sketch, "E338", {"start": v(-41.42, 71.16) * mm, "end": v(-41.42, 71.1) * mm});
            skLineSegment(sketch, "E339", {"start": v(-41.42, 71.1) * mm, "end": v(-39.95, 71.1) * mm});
            skLineSegment(sketch, "E340", {"start": v(-39.95, 71.1) * mm, "end": v(-39.97, 71.44) * mm});
            skLineSegment(sketch, "E341", {"start": v(-39.97, 71.44) * mm, "end": v(-40.1, 74.54) * mm});
            skLineSegment(sketch, "E342", {"start": v(-40.1, 74.54) * mm, "end": v(-40.1, 75.58) * mm});
            skLineSegment(sketch, "E343", {"start": v(-40.1, 75.58) * mm, "end": v(-40.1, 75.97) * mm});
            skLineSegment(sketch, "E344", {"start": v(-40.1, 75.97) * mm, "end": v(-40.04, 80.3) * mm});
            skLineSegment(sketch, "E345", {"start": v(-40.04, 80.3) * mm, "end": v(-40.02, 80.76) * mm});
            skLineSegment(sketch, "E346", {"start": v(-40.02, 80.76) * mm, "end": v(-38.76, 81.88) * mm});
            skLineSegment(sketch, "E347", {"start": v(-38.76, 81.88) * mm, "end": v(-38.76, 82) * mm});
            skLineSegment(sketch, "E348", {"start": v(-38.76, 82) * mm, "end": v(-42.45, 82) * mm});
            skLineSegment(sketch, "E349", {"start": v(-42.45, 82) * mm, "end": v(-42.45, 81.88) * mm});
            skLineSegment(sketch, "E350", {"start": v(22.12, 84.65) * mm, "end": v(22.17, 84.62) * mm});
            skLineSegment(sketch, "E351", {"start": v(22.17, 84.62) * mm, "end": v(22.7, 84.26) * mm});
            skLineSegment(sketch, "E352", {"start": v(22.7, 84.26) * mm, "end": v(22.75, 84.23) * mm});
            skLineSegment(sketch, "E353", {"start": v(22.75, 84.23) * mm, "end": v(22.8, 84.2) * mm});
            skLineSegment(sketch, "E354", {"start": v(22.8, 84.2) * mm, "end": v(23.3, 83.82) * mm});
            skLineSegment(sketch, "E355", {"start": v(23.3, 83.82) * mm, "end": v(23.35, 83.78) * mm});
            skLineSegment(sketch, "E356", {"start": v(23.35, 83.78) * mm, "end": v(23.25, 83.42) * mm});
            skLineSegment(sketch, "E357", {"start": v(23.25, 83.42) * mm, "end": v(22.34, 80.21) * mm});
            skLineSegment(sketch, "E358", {"start": v(22.34, 80.21) * mm, "end": v(22.26, 79.92) * mm});
            skLineSegment(sketch, "E359", {"start": v(22.26, 79.92) * mm, "end": v(22.18, 79.63) * mm});
            skLineSegment(sketch, "E360", {"start": v(22.18, 79.63) * mm, "end": v(21.46, 77.16) * mm});
            skLineSegment(sketch, "E361", {"start": v(21.46, 77.16) * mm, "end": v(21.4, 76.94) * mm});
            skLineSegment(sketch, "E362", {"start": v(21.4, 76.94) * mm, "end": v(21.33, 76.74) * mm});
            skLineSegment(sketch, "E363", {"start": v(21.33, 76.74) * mm, "end": v(20.84, 75.02) * mm});
            skLineSegment(sketch, "E364", {"start": v(20.84, 75.02) * mm, "end": v(20.8, 74.88) * mm});
            skLineSegment(sketch, "E365", {"start": v(20.8, 74.88) * mm, "end": v(20.77, 74.75) * mm});
            skLineSegment(sketch, "E366", {"start": v(20.77, 74.75) * mm, "end": v(20.63, 74.2) * mm});
            skLineSegment(sketch, "E367", {"start": v(20.63, 74.2) * mm, "end": v(20.54, 73.83) * mm});
            skLineSegment(sketch, "E368", {"start": v(20.54, 73.83) * mm, "end": v(20.53, 73.78) * mm});
            skLineSegment(sketch, "E369", {"start": v(20.53, 73.78) * mm, "end": v(17.53, 83.66) * mm});
            skLineSegment(sketch, "E370", {"start": v(17.53, 83.66) * mm, "end": v(17.58, 83.71) * mm});
            skLineSegment(sketch, "E371", {"start": v(17.58, 83.71) * mm, "end": v(18.07, 84.19) * mm});
            skLineSegment(sketch, "E372", {"start": v(18.07, 84.19) * mm, "end": v(18.12, 84.23) * mm});
            skLineSegment(sketch, "E373", {"start": v(18.12, 84.23) * mm, "end": v(18.17, 84.27) * mm});
            skLineSegment(sketch, "E374", {"start": v(18.17, 84.27) * mm, "end": v(18.64, 84.62) * mm});
            skLineSegment(sketch, "E375", {"start": v(18.64, 84.62) * mm, "end": v(18.68, 84.65) * mm});
            skLineSegment(sketch, "E376", {"start": v(18.68, 84.65) * mm, "end": v(18.68, 84.77) * mm});
            skLineSegment(sketch, "E377", {"start": v(18.68, 84.77) * mm, "end": v(13.9, 84.77) * mm});
            skLineSegment(sketch, "E378", {"start": v(13.9, 84.77) * mm, "end": v(13.9, 84.63) * mm});
            skLineSegment(sketch, "E379", {"start": v(13.9, 84.63) * mm, "end": v(15.1, 83.7) * mm});
            skLineSegment(sketch, "E380", {"start": v(15.1, 83.7) * mm, "end": v(15.02, 83.45) * mm});
            skLineSegment(sketch, "E381", {"start": v(15.02, 83.45) * mm, "end": v(14.26, 80.97) * mm});
            skLineSegment(sketch, "E382", {"start": v(14.26, 80.97) * mm, "end": v(14.2, 80.73) * mm});
            skLineSegment(sketch, "E383", {"start": v(14.2, 80.73) * mm, "end": v(14.12, 80.5) * mm});
            skLineSegment(sketch, "E384", {"start": v(14.12, 80.5) * mm, "end": v(13.48, 78.33) * mm});
            skLineSegment(sketch, "E385", {"start": v(13.48, 78.33) * mm, "end": v(13.42, 78.13) * mm});
            skLineSegment(sketch, "E386", {"start": v(13.42, 78.13) * mm, "end": v(13.36, 77.93) * mm});
            skLineSegment(sketch, "E387", {"start": v(13.36, 77.93) * mm, "end": v(12.8, 76.03) * mm});
            skLineSegment(sketch, "E388", {"start": v(12.8, 76.03) * mm, "end": v(12.76, 75.85) * mm});
            skLineSegment(sketch, "E389", {"start": v(12.76, 75.85) * mm, "end": v(12.7, 75.68) * mm});
            skLineSegment(sketch, "E390", {"start": v(12.7, 75.68) * mm, "end": v(12.23, 74) * mm});
            skLineSegment(sketch, "E391", {"start": v(12.23, 74) * mm, "end": v(12.19, 73.83) * mm});
            skLineSegment(sketch, "E392", {"start": v(12.19, 73.83) * mm, "end": v(9.36, 83.69) * mm});
            skLineSegment(sketch, "E393", {"start": v(9.36, 83.69) * mm, "end": v(10.52, 84.65) * mm});
            skLineSegment(sketch, "E394", {"start": v(10.52, 84.65) * mm, "end": v(10.52, 84.77) * mm});
            skLineSegment(sketch, "E395", {"start": v(10.52, 84.77) * mm, "end": v(5.92, 84.77) * mm});
            skLineSegment(sketch, "E396", {"start": v(5.92, 84.77) * mm, "end": v(5.92, 84.65) * mm});
            skLineSegment(sketch, "E397", {"start": v(5.92, 84.65) * mm, "end": v(5.97, 84.61) * mm});
            skLineSegment(sketch, "E398", {"start": v(5.97, 84.61) * mm, "end": v(6.39, 84.27) * mm});
            skLineSegment(sketch, "E399", {"start": v(6.39, 84.27) * mm, "end": v(6.42, 84.24) * mm});
            skLineSegment(sketch, "E400", {"start": v(6.42, 84.24) * mm, "end": v(6.45, 84.22) * mm});
            skLineSegment(sketch, "E401", {"start": v(6.45, 84.22) * mm, "end": v(6.73, 84) * mm});
            skLineSegment(sketch, "E402", {"start": v(6.73, 84) * mm, "end": v(6.75, 83.97) * mm});
            skLineSegment(sketch, "E403", {"start": v(6.75, 83.97) * mm, "end": v(6.77, 83.95) * mm});
            skLineSegment(sketch, "E404", {"start": v(6.77, 83.95) * mm, "end": v(6.94, 83.77) * mm});
            skLineSegment(sketch, "E405", {"start": v(6.94, 83.77) * mm, "end": v(6.95, 83.76) * mm});
            skLineSegment(sketch, "E406", {"start": v(6.95, 83.76) * mm, "end": v(6.96, 83.74) * mm});
            skLineSegment(sketch, "E407", {"start": v(6.96, 83.74) * mm, "end": v(7.06, 83.55) * mm});
            skLineSegment(sketch, "E408", {"start": v(7.06, 83.55) * mm, "end": v(7.06, 83.53) * mm});
            skLineSegment(sketch, "E409", {"start": v(7.06, 83.53) * mm, "end": v(7.1, 83.41) * mm});
            skLineSegment(sketch, "E410", {"start": v(7.1, 83.41) * mm, "end": v(7.33, 82.68) * mm});
            skLineSegment(sketch, "E411", {"start": v(7.33, 82.68) * mm, "end": v(7.63, 81.76) * mm});
            skLineSegment(sketch, "E412", {"start": v(7.63, 81.76) * mm, "end": v(7.7, 81.55) * mm});
            skLineSegment(sketch, "E413", {"start": v(7.7, 81.55) * mm, "end": v(7.77, 81.33) * mm});
            skLineSegment(sketch, "E414", {"start": v(7.77, 81.33) * mm, "end": v(8.57, 78.85) * mm});
            skLineSegment(sketch, "E415", {"start": v(8.57, 78.85) * mm, "end": v(8.66, 78.57) * mm});
            skLineSegment(sketch, "E416", {"start": v(8.66, 78.57) * mm, "end": v(8.75, 78.3) * mm});
            skLineSegment(sketch, "E417", {"start": v(8.75, 78.3) * mm, "end": v(9.73, 75.3) * mm});
            skLineSegment(sketch, "E418", {"start": v(9.73, 75.3) * mm, "end": v(9.84, 74.97) * mm});
            skLineSegment(sketch, "E419", {"start": v(9.84, 74.97) * mm, "end": v(9.94, 74.65) * mm});
            skLineSegment(sketch, "E420", {"start": v(9.94, 74.65) * mm, "end": v(10.97, 71.27) * mm});
            skLineSegment(sketch, "E421", {"start": v(10.97, 71.27) * mm, "end": v(11.08, 70.91) * mm});
            skLineSegment(sketch, "E422", {"start": v(11.08, 70.91) * mm, "end": v(12.6, 70.91) * mm});
            skLineSegment(sketch, "E423", {"start": v(12.6, 70.91) * mm, "end": v(12.59, 70.93) * mm});
            skLineSegment(sketch, "E424", {"start": v(12.59, 70.93) * mm, "end": v(12.57, 71.03) * mm});
            skLineSegment(sketch, "E425", {"start": v(12.57, 71.03) * mm, "end": v(12.57, 71.06) * mm});
            skLineSegment(sketch, "E426", {"start": v(12.57, 71.06) * mm, "end": v(12.57, 71.13) * mm});
            skLineSegment(sketch, "E427", {"start": v(12.57, 71.13) * mm, "end": v(12.6, 71.31) * mm});
            skLineSegment(sketch, "E428", {"start": v(12.6, 71.31) * mm, "end": v(12.6, 71.33) * mm});
            skLineSegment(sketch, "E429", {"start": v(12.6, 71.33) * mm, "end": v(12.6, 71.35) * mm});
            skLineSegment(sketch, "E430", {"start": v(12.6, 71.35) * mm, "end": v(12.66, 71.59) * mm});
            skLineSegment(sketch, "E431", {"start": v(12.66, 71.59) * mm, "end": v(12.67, 71.6) * mm});
            skLineSegment(sketch, "E432", {"start": v(12.67, 71.6) * mm, "end": v(12.68, 71.63) * mm});
            skLineSegment(sketch, "E433", {"start": v(12.68, 71.63) * mm, "end": v(12.75, 71.84) * mm});
            skLineSegment(sketch, "E434", {"start": v(12.75, 71.84) * mm, "end": v(12.76, 71.86) * mm});
            skLineSegment(sketch, "E435", {"start": v(12.76, 71.86) * mm, "end": v(12.79, 71.98) * mm});
            skLineSegment(sketch, "E436", {"start": v(12.79, 71.98) * mm, "end": v(13.13, 73.27) * mm});
            skLineSegment(sketch, "E437", {"start": v(13.13, 73.27) * mm, "end": v(13.17, 73.4) * mm});
            skLineSegment(sketch, "E438", {"start": v(13.17, 73.4) * mm, "end": v(13.2, 73.55) * mm});
            skLineSegment(sketch, "E439", {"start": v(13.2, 73.55) * mm, "end": v(13.6, 75.01) * mm});
            skLineSegment(sketch, "E440", {"start": v(13.6, 75.01) * mm, "end": v(13.65, 75.16) * mm});
            skLineSegment(sketch, "E441", {"start": v(13.65, 75.16) * mm, "end": v(13.69, 75.31) * mm});
            skLineSegment(sketch, "E442", {"start": v(13.69, 75.31) * mm, "end": v(14.13, 76.88) * mm});
            skLineSegment(sketch, "E443", {"start": v(14.13, 76.88) * mm, "end": v(14.17, 77.04) * mm});
            skLineSegment(sketch, "E444", {"start": v(14.17, 77.04) * mm, "end": v(14.22, 77.2) * mm});
            skLineSegment(sketch, "E445", {"start": v(14.22, 77.2) * mm, "end": v(14.67, 78.78) * mm});
            skLineSegment(sketch, "E446", {"start": v(14.67, 78.78) * mm, "end": v(14.72, 78.94) * mm});
            skLineSegment(sketch, "E447", {"start": v(14.72, 78.94) * mm, "end": v(14.76, 79.1) * mm});
            skLineSegment(sketch, "E448", {"start": v(14.76, 79.1) * mm, "end": v(15.2, 80.59) * mm});
            skLineSegment(sketch, "E449", {"start": v(15.2, 80.59) * mm, "end": v(15.24, 80.73) * mm});
            skLineSegment(sketch, "E450", {"start": v(15.24, 80.73) * mm, "end": v(15.28, 80.89) * mm});
            skLineSegment(sketch, "E451", {"start": v(15.28, 80.89) * mm, "end": v(15.69, 82.25) * mm});
            skLineSegment(sketch, "E452", {"start": v(15.69, 82.25) * mm, "end": v(15.72, 82.37) * mm});
            skLineSegment(sketch, "E453", {"start": v(15.72, 82.37) * mm, "end": v(19.31, 70.91) * mm});
            skLineSegment(sketch, "E454", {"start": v(19.31, 70.91) * mm, "end": v(20.76, 70.91) * mm});
            skLineSegment(sketch, "E455", {"start": v(20.76, 70.91) * mm, "end": v(20.78, 70.97) * mm});
            skLineSegment(sketch, "E456", {"start": v(20.78, 70.97) * mm, "end": v(20.9, 71.44) * mm});
            skLineSegment(sketch, "E457", {"start": v(20.9, 71.44) * mm, "end": v(21.08, 72.13) * mm});
            skLineSegment(sketch, "E458", {"start": v(21.08, 72.13) * mm, "end": v(21.13, 72.3) * mm});
            skLineSegment(sketch, "E459", {"start": v(21.13, 72.3) * mm, "end": v(21.17, 72.47) * mm});
            skLineSegment(sketch, "E460", {"start": v(21.17, 72.47) * mm, "end": v(21.46, 73.45) * mm});
            skLineSegment(sketch, "E461", {"start": v(21.46, 73.45) * mm, "end": v(21.81, 74.64) * mm});
            skLineSegment(sketch, "E462", {"start": v(21.81, 74.64) * mm, "end": v(21.9, 74.9) * mm});
            skLineSegment(sketch, "E463", {"start": v(21.9, 74.9) * mm, "end": v(21.98, 75.17) * mm});
            skLineSegment(sketch, "E464", {"start": v(21.98, 75.17) * mm, "end": v(22.42, 76.65) * mm});
            skLineSegment(sketch, "E465", {"start": v(22.42, 76.65) * mm, "end": v(22.93, 78.32) * mm});
            skLineSegment(sketch, "E466", {"start": v(22.93, 78.32) * mm, "end": v(23.04, 78.68) * mm});
            skLineSegment(sketch, "E467", {"start": v(23.04, 78.68) * mm, "end": v(23.15, 79.04) * mm});
            skLineSegment(sketch, "E468", {"start": v(23.15, 79.04) * mm, "end": v(23.73, 81.02) * mm});
            skLineSegment(sketch, "E469", {"start": v(23.73, 81.02) * mm, "end": v(24.36, 83.17) * mm});
            skLineSegment(sketch, "E470", {"start": v(24.36, 83.17) * mm, "end": v(24.5, 83.62) * mm});
            skLineSegment(sketch, "E471", {"start": v(24.5, 83.62) * mm, "end": v(24.57, 83.7) * mm});
            skLineSegment(sketch, "E472", {"start": v(24.57, 83.7) * mm, "end": v(25.2, 84.28) * mm});
            skLineSegment(sketch, "E473", {"start": v(25.2, 84.28) * mm, "end": v(25.25, 84.32) * mm});
            skLineSegment(sketch, "E474", {"start": v(25.25, 84.32) * mm, "end": v(25.3, 84.36) * mm});
            skLineSegment(sketch, "E475", {"start": v(25.3, 84.36) * mm, "end": v(25.62, 84.66) * mm});
            skLineSegment(sketch, "E476", {"start": v(25.62, 84.66) * mm, "end": v(25.64, 84.67) * mm});
            skLineSegment(sketch, "E477", {"start": v(25.64, 84.67) * mm, "end": v(25.64, 84.77) * mm});
            skLineSegment(sketch, "E478", {"start": v(25.64, 84.77) * mm, "end": v(22.12, 84.77) * mm});
            skLineSegment(sketch, "E479", {"start": v(22.12, 84.77) * mm, "end": v(22.12, 84.65) * mm});
            skLineSegment(sketch, "E480", {"start": v(-88.79, 84.72) * mm, "end": v(-87.13, 83.69) * mm});
            skLineSegment(sketch, "E481", {"start": v(-87.13, 83.69) * mm, "end": v(-87.02, 72.08) * mm});
            skLineSegment(sketch, "E482", {"start": v(-87.02, 72.08) * mm, "end": v(-87.02, 71.77) * mm});
            skLineSegment(sketch, "E483", {"start": v(-87.02, 71.77) * mm, "end": v(-87.04, 70.93) * mm});
            skLineSegment(sketch, "E484", {"start": v(-87.04, 70.93) * mm, "end": v(-87.04, 70.84) * mm});
            skLineSegment(sketch, "E485", {"start": v(-87.04, 70.84) * mm, "end": v(-87.05, 70.76) * mm});
            skLineSegment(sketch, "E486", {"start": v(-87.05, 70.76) * mm, "end": v(-87.13, 69.94) * mm});
            skLineSegment(sketch, "E487", {"start": v(-87.13, 69.94) * mm, "end": v(-87.14, 69.87) * mm});
            skLineSegment(sketch, "E488", {"start": v(-87.14, 69.87) * mm, "end": v(-87.16, 69.8) * mm});
            skLineSegment(sketch, "E489", {"start": v(-87.16, 69.8) * mm, "end": v(-87.38, 69.1) * mm});
            skLineSegment(sketch, "E490", {"start": v(-87.38, 69.1) * mm, "end": v(-87.4, 69.04) * mm});
            skLineSegment(sketch, "E491", {"start": v(-87.4, 69.04) * mm, "end": v(-87.44, 68.98) * mm});
            skLineSegment(sketch, "E492", {"start": v(-87.44, 68.98) * mm, "end": v(-87.85, 68.36) * mm});
            skLineSegment(sketch, "E493", {"start": v(-87.85, 68.36) * mm, "end": v(-87.9, 68.3) * mm});
            skLineSegment(sketch, "E494", {"start": v(-87.9, 68.3) * mm, "end": v(-87.96, 68.23) * mm});
            skLineSegment(sketch, "E495", {"start": v(-87.96, 68.23) * mm, "end": v(-88.74, 67.61) * mm});
            skLineSegment(sketch, "E496", {"start": v(-88.74, 67.61) * mm, "end": v(-88.83, 67.57) * mm});
            skLineSegment(sketch, "E497", {"start": v(-88.83, 67.57) * mm, "end": v(-88.92, 67.52) * mm});
            skLineSegment(sketch, "E498", {"start": v(-88.92, 67.52) * mm, "end": v(-89.9, 67.32) * mm});
            skLineSegment(sketch, "E499", {"start": v(-89.9, 67.32) * mm, "end": v(-90, 67.32) * mm});
            skLineSegment(sketch, "E500", {"start": v(-90, 67.32) * mm, "end": v(-90, 67.33) * mm});
            skLineSegment(sketch, "E501", {"start": v(-90, 67.33) * mm, "end": v(-89.9, 67.48) * mm});
            skLineSegment(sketch, "E502", {"start": v(-89.9, 67.48) * mm, "end": v(-89.89, 67.5) * mm});
            skLineSegment(sketch, "E503", {"start": v(-89.89, 67.5) * mm, "end": v(-89.88, 67.5) * mm});
            skLineSegment(sketch, "E504", {"start": v(-89.88, 67.5) * mm, "end": v(-89.8, 67.68) * mm});
            skLineSegment(sketch, "E505", {"start": v(-89.8, 67.68) * mm, "end": v(-89.8, 67.7) * mm});
            skLineSegment(sketch, "E506", {"start": v(-89.8, 67.7) * mm, "end": v(-89.8, 67.72) * mm});
            skLineSegment(sketch, "E507", {"start": v(-89.8, 67.72) * mm, "end": v(-89.77, 67.93) * mm});
            skLineSegment(sketch, "E508", {"start": v(-89.77, 67.93) * mm, "end": v(-89.77, 68) * mm});
            skLineSegment(sketch, "E509", {"start": v(-89.77, 68) * mm, "end": v(-89.77, 68.08) * mm});
            skLineSegment(sketch, "E510", {"start": v(-89.77, 68.08) * mm, "end": v(-89.83, 68.3) * mm});
            skLineSegment(sketch, "E511", {"start": v(-89.83, 68.3) * mm, "end": v(-89.85, 68.32) * mm});
            skLineSegment(sketch, "E512", {"start": v(-89.85, 68.32) * mm, "end": v(-89.86, 68.35) * mm});
            skLineSegment(sketch, "E513", {"start": v(-89.86, 68.35) * mm, "end": v(-90.04, 68.63) * mm});
            skLineSegment(sketch, "E514", {"start": v(-90.04, 68.63) * mm, "end": v(-90.06, 68.66) * mm});
            skLineSegment(sketch, "E515", {"start": v(-90.06, 68.66) * mm, "end": v(-90.1, 68.68) * mm});
            skLineSegment(sketch, "E516", {"start": v(-90.1, 68.68) * mm, "end": v(-90.37, 68.86) * mm});
            skLineSegment(sketch, "E517", {"start": v(-90.37, 68.86) * mm, "end": v(-90.4, 68.87) * mm});
            skLineSegment(sketch, "E518", {"start": v(-90.4, 68.87) * mm, "end": v(-90.43, 68.89) * mm});
            skLineSegment(sketch, "E519", {"start": v(-90.43, 68.89) * mm, "end": v(-90.7, 68.97) * mm});
            skLineSegment(sketch, "E520", {"start": v(-90.7, 68.97) * mm, "end": v(-90.8, 68.97) * mm});
            skLineSegment(sketch, "E521", {"start": v(-90.8, 68.97) * mm, "end": v(-90.9, 68.97) * mm});
            skLineSegment(sketch, "E522", {"start": v(-90.9, 68.97) * mm, "end": v(-91.17, 68.9) * mm});
            skLineSegment(sketch, "E523", {"start": v(-91.17, 68.9) * mm, "end": v(-91.2, 68.88) * mm});
            skLineSegment(sketch, "E524", {"start": v(-91.2, 68.88) * mm, "end": v(-91.24, 68.87) * mm});
            skLineSegment(sketch, "E525", {"start": v(-91.24, 68.87) * mm, "end": v(-91.52, 68.68) * mm});
            skLineSegment(sketch, "E526", {"start": v(-91.52, 68.68) * mm, "end": v(-91.55, 68.66) * mm});
            skLineSegment(sketch, "E527", {"start": v(-91.55, 68.66) * mm, "end": v(-91.57, 68.64) * mm});
            skLineSegment(sketch, "E528", {"start": v(-91.57, 68.64) * mm, "end": v(-91.77, 68.34) * mm});
            skLineSegment(sketch, "E529", {"start": v(-91.77, 68.34) * mm, "end": v(-91.79, 68.3) * mm});
            skLineSegment(sketch, "E530", {"start": v(-91.79, 68.3) * mm, "end": v(-91.8, 68.28) * mm});
            skLineSegment(sketch, "E531", {"start": v(-91.8, 68.28) * mm, "end": v(-91.9, 67.98) * mm});
            skLineSegment(sketch, "E532", {"start": v(-91.9, 67.98) * mm, "end": v(-91.9, 67.87) * mm});
            skLineSegment(sketch, "E533", {"start": v(-91.9, 67.87) * mm, "end": v(-91.9, 67.72) * mm});
            skLineSegment(sketch, "E534", {"start": v(-91.9, 67.72) * mm, "end": v(-91.74, 67.3) * mm});
            skLineSegment(sketch, "E535", {"start": v(-91.74, 67.3) * mm, "end": v(-91.71, 67.26) * mm});
            skLineSegment(sketch, "E536", {"start": v(-91.71, 67.26) * mm, "end": v(-91.69, 67.2) * mm});
            skLineSegment(sketch, "E537", {"start": v(-91.69, 67.2) * mm, "end": v(-91.32, 66.86) * mm});
            skLineSegment(sketch, "E538", {"start": v(-91.32, 66.86) * mm, "end": v(-91.28, 66.83) * mm});
            skLineSegment(sketch, "E539", {"start": v(-91.28, 66.83) * mm, "end": v(-91.23, 66.8) * mm});
            skLineSegment(sketch, "E540", {"start": v(-91.23, 66.8) * mm, "end": v(-90.75, 66.6) * mm});
            skLineSegment(sketch, "E541", {"start": v(-90.75, 66.6) * mm, "end": v(-90.7, 66.59) * mm});
            skLineSegment(sketch, "E542", {"start": v(-90.7, 66.59) * mm, "end": v(-90.64, 66.57) * mm});
            skLineSegment(sketch, "E543", {"start": v(-90.64, 66.57) * mm, "end": v(-90.22, 66.5) * mm});
            skLineSegment(sketch, "E544", {"start": v(-90.22, 66.5) * mm, "end": v(-90.08, 66.5) * mm});
            skLineSegment(sketch, "E545", {"start": v(-90.08, 66.5) * mm, "end": v(-89.78, 66.5) * mm});
            skLineSegment(sketch, "E546", {"start": v(-89.78, 66.5) * mm, "end": v(-88.96, 66.67) * mm});
            skLineSegment(sketch, "E547", {"start": v(-88.96, 66.67) * mm, "end": v(-88.87, 66.7) * mm});
            skLineSegment(sketch, "E548", {"start": v(-88.87, 66.7) * mm, "end": v(-88.77, 66.74) * mm});
            skLineSegment(sketch, "E549", {"start": v(-88.77, 66.74) * mm, "end": v(-87.88, 67.2) * mm});
            skLineSegment(sketch, "E550", {"start": v(-87.88, 67.2) * mm, "end": v(-87.8, 67.26) * mm});
            skLineSegment(sketch, "E551", {"start": v(-87.8, 67.26) * mm, "end": v(-87.7, 67.32) * mm});
            skLineSegment(sketch, "E552", {"start": v(-87.7, 67.32) * mm, "end": v(-86.93, 68.03) * mm});
            skLineSegment(sketch, "E553", {"start": v(-86.93, 68.03) * mm, "end": v(-86.86, 68.11) * mm});
            skLineSegment(sketch, "E554", {"start": v(-86.86, 68.11) * mm, "end": v(-86.79, 68.2) * mm});
            skLineSegment(sketch, "E555", {"start": v(-86.79, 68.2) * mm, "end": v(-86.18, 69.13) * mm});
            skLineSegment(sketch, "E556", {"start": v(-86.18, 69.13) * mm, "end": v(-86.13, 69.23) * mm});
            skLineSegment(sketch, "E557", {"start": v(-86.13, 69.23) * mm, "end": v(-86.08, 69.32) * mm});
            skLineSegment(sketch, "E558", {"start": v(-86.08, 69.32) * mm, "end": v(-85.66, 70.15) * mm});
            skLineSegment(sketch, "E559", {"start": v(-85.66, 70.15) * mm, "end": v(-85.62, 70.23) * mm});
            skLineSegment(sketch, "E560", {"start": v(-85.62, 70.23) * mm, "end": v(-85.58, 70.31) * mm});
            skLineSegment(sketch, "E561", {"start": v(-85.58, 70.31) * mm, "end": v(-85.25, 71.18) * mm});
            skLineSegment(sketch, "E562", {"start": v(-85.25, 71.18) * mm, "end": v(-85.23, 71.28) * mm});
            skLineSegment(sketch, "E563", {"start": v(-85.23, 71.28) * mm, "end": v(-85.2, 71.38) * mm});
            skLineSegment(sketch, "E564", {"start": v(-85.2, 71.38) * mm, "end": v(-85, 72.38) * mm});
            skLineSegment(sketch, "E565", {"start": v(-85, 72.38) * mm, "end": v(-84.98, 72.48) * mm});
            skLineSegment(sketch, "E566", {"start": v(-84.98, 72.48) * mm, "end": v(-84.96, 72.6) * mm});
            skLineSegment(sketch, "E567", {"start": v(-84.96, 72.6) * mm, "end": v(-84.9, 73.85) * mm});
            skLineSegment(sketch, "E568", {"start": v(-84.9, 73.85) * mm, "end": v(-84.91, 73.99) * mm});
            skLineSegment(sketch, "E569", {"start": v(-84.91, 73.99) * mm, "end": v(-84.91, 74.14) * mm});
            skLineSegment(sketch, "E570", {"start": v(-84.91, 74.14) * mm, "end": v(-84.94, 75.64) * mm});
            skLineSegment(sketch, "E571", {"start": v(-84.94, 75.64) * mm, "end": v(-84.95, 75.8) * mm});
            skLineSegment(sketch, "E572", {"start": v(-84.95, 75.8) * mm, "end": v(-84.95, 75.96) * mm});
            skLineSegment(sketch, "E573", {"start": v(-84.95, 75.96) * mm, "end": v(-84.97, 77.71) * mm});
            skLineSegment(sketch, "E574", {"start": v(-84.97, 77.71) * mm, "end": v(-84.98, 77.9) * mm});
            skLineSegment(sketch, "E575", {"start": v(-84.98, 77.9) * mm, "end": v(-84.98, 78.1) * mm});
            skLineSegment(sketch, "E576", {"start": v(-84.98, 78.1) * mm, "end": v(-85.01, 80.26) * mm});
            skLineSegment(sketch, "E577", {"start": v(-85.01, 80.26) * mm, "end": v(-85.01, 80.5) * mm});
            skLineSegment(sketch, "E578", {"start": v(-85.01, 80.5) * mm, "end": v(-85.02, 80.74) * mm});
            skLineSegment(sketch, "E579", {"start": v(-85.02, 80.74) * mm, "end": v(-85.03, 83.05) * mm});
            skLineSegment(sketch, "E580", {"start": v(-85.03, 83.05) * mm, "end": v(-85.03, 83.82) * mm});
            skLineSegment(sketch, "E581", {"start": v(-85.03, 83.82) * mm, "end": v(-83.65, 84.72) * mm});
            skLineSegment(sketch, "E582", {"start": v(-83.65, 84.72) * mm, "end": v(-83.65, 84.84) * mm});
            skLineSegment(sketch, "E583", {"start": v(-83.65, 84.84) * mm, "end": v(-88.79, 84.84) * mm});
            skLineSegment(sketch, "E584", {"start": v(-88.79, 84.84) * mm, "end": v(-88.79, 84.72) * mm});
            skLineSegment(sketch, "E585", {"start": v(-69.46, 79.59) * mm, "end": v(-69.53, 79.7) * mm});
            skLineSegment(sketch, "E586", {"start": v(-69.53, 79.7) * mm, "end": v(-70.34, 80.67) * mm});
            skLineSegment(sketch, "E587", {"start": v(-70.34, 80.67) * mm, "end": v(-70.43, 80.75) * mm});
            skLineSegment(sketch, "E588", {"start": v(-70.43, 80.75) * mm, "end": v(-70.52, 80.85) * mm});
            skLineSegment(sketch, "E589", {"start": v(-70.52, 80.85) * mm, "end": v(-71.51, 81.62) * mm});
            skLineSegment(sketch, "E590", {"start": v(-71.51, 81.62) * mm, "end": v(-71.62, 81.68) * mm});
            skLineSegment(sketch, "E591", {"start": v(-71.62, 81.68) * mm, "end": v(-71.73, 81.75) * mm});
            skLineSegment(sketch, "E592", {"start": v(-71.73, 81.75) * mm, "end": v(-72.85, 82.22) * mm});
            skLineSegment(sketch, "E593", {"start": v(-72.85, 82.22) * mm, "end": v(-72.97, 82.25) * mm});
            skLineSegment(sketch, "E594", {"start": v(-72.97, 82.25) * mm, "end": v(-73.09, 82.29) * mm});
            skLineSegment(sketch, "E595", {"start": v(-73.09, 82.29) * mm, "end": v(-74.08, 82.45) * mm});
            skLineSegment(sketch, "E596", {"start": v(-74.08, 82.45) * mm, "end": v(-74.4, 82.45) * mm});
            skLineSegment(sketch, "E597", {"start": v(-74.4, 82.45) * mm, "end": v(-74.72, 82.45) * mm});
            skLineSegment(sketch, "E598", {"start": v(-74.72, 82.45) * mm, "end": v(-75.66, 82.34) * mm});
            skLineSegment(sketch, "E599", {"start": v(-75.66, 82.34) * mm, "end": v(-76.63, 82.07) * mm});
            skLineSegment(sketch, "E600", {"start": v(-76.63, 82.07) * mm, "end": v(-76.8, 82) * mm});
            skLineSegment(sketch, "E601", {"start": v(-76.8, 82) * mm, "end": v(-77, 81.92) * mm});
            skLineSegment(sketch, "E602", {"start": v(-77, 81.92) * mm, "end": v(-78.58, 80.87) * mm});
            skLineSegment(sketch, "E603", {"start": v(-78.58, 80.87) * mm, "end": v(-78.71, 80.73) * mm});
            skLineSegment(sketch, "E604", {"start": v(-78.71, 80.73) * mm, "end": v(-78.85, 80.6) * mm});
            skLineSegment(sketch, "E605", {"start": v(-78.85, 80.6) * mm, "end": v(-79.45, 79.87) * mm});
            skLineSegment(sketch, "E606", {"start": v(-79.45, 79.87) * mm, "end": v(-79.92, 79.05) * mm});
            skLineSegment(sketch, "E607", {"start": v(-79.92, 79.05) * mm, "end": v(-80, 78.87) * mm});
            skLineSegment(sketch, "E608", {"start": v(-80, 78.87) * mm, "end": v(-80.07, 78.7) * mm});
            skLineSegment(sketch, "E609", {"start": v(-80.07, 78.7) * mm, "end": v(-80.45, 77.1) * mm});
            skLineSegment(sketch, "E610", {"start": v(-80.45, 77.1) * mm, "end": v(-80.45, 76.58) * mm});
            skLineSegment(sketch, "E611", {"start": v(-80.45, 76.58) * mm, "end": v(-80.45, 76.02) * mm});
            skLineSegment(sketch, "E612", {"start": v(-80.45, 76.02) * mm, "end": v(-80.06, 74.5) * mm});
            skLineSegment(sketch, "E613", {"start": v(-80.06, 74.5) * mm, "end": v(-79.98, 74.33) * mm});
            skLineSegment(sketch, "E614", {"start": v(-79.98, 74.33) * mm, "end": v(-79.9, 74.15) * mm});
            skLineSegment(sketch, "E615", {"start": v(-79.9, 74.15) * mm, "end": v(-78.83, 72.62) * mm});
            skLineSegment(sketch, "E616", {"start": v(-78.83, 72.62) * mm, "end": v(-78.7, 72.48) * mm});
            skLineSegment(sketch, "E617", {"start": v(-78.7, 72.48) * mm, "end": v(-78.56, 72.35) * mm});
            skLineSegment(sketch, "E618", {"start": v(-78.56, 72.35) * mm, "end": v(-76.98, 71.28) * mm});
            skLineSegment(sketch, "E619", {"start": v(-76.98, 71.28) * mm, "end": v(-76.8, 71.2) * mm});
            skLineSegment(sketch, "E620", {"start": v(-76.8, 71.2) * mm, "end": v(-76.62, 71.11) * mm});
            skLineSegment(sketch, "E621", {"start": v(-76.62, 71.11) * mm, "end": v(-75.68, 70.85) * mm});
            skLineSegment(sketch, "E622", {"start": v(-75.68, 70.85) * mm, "end": v(-74.77, 70.76) * mm});
            skLineSegment(sketch, "E623", {"start": v(-74.77, 70.76) * mm, "end": v(-74.47, 70.76) * mm});
            skLineSegment(sketch, "E624", {"start": v(-74.47, 70.76) * mm, "end": v(-74.17, 70.76) * mm});
            skLineSegment(sketch, "E625", {"start": v(-74.17, 70.76) * mm, "end": v(-73.27, 70.85) * mm});
            skLineSegment(sketch, "E626", {"start": v(-73.27, 70.85) * mm, "end": v(-72.33, 71.12) * mm});
            skLineSegment(sketch, "E627", {"start": v(-72.33, 71.12) * mm, "end": v(-72.15, 71.22) * mm});
            skLineSegment(sketch, "E628", {"start": v(-72.15, 71.22) * mm, "end": v(-71.97, 71.3) * mm});
            skLineSegment(sketch, "E629", {"start": v(-71.97, 71.3) * mm, "end": v(-70.43, 72.36) * mm});
            skLineSegment(sketch, "E630", {"start": v(-70.43, 72.36) * mm, "end": v(-70.3, 72.5) * mm});
            skLineSegment(sketch, "E631", {"start": v(-70.3, 72.5) * mm, "end": v(-70.17, 72.64) * mm});
            skLineSegment(sketch, "E632", {"start": v(-70.17, 72.64) * mm, "end": v(-69.13, 74.18) * mm});
            skLineSegment(sketch, "E633", {"start": v(-69.13, 74.18) * mm, "end": v(-69.05, 74.35) * mm});
            skLineSegment(sketch, "E634", {"start": v(-69.05, 74.35) * mm, "end": v(-68.98, 74.53) * mm});
            skLineSegment(sketch, "E635", {"start": v(-68.98, 74.53) * mm, "end": v(-68.61, 76.07) * mm});
            skLineSegment(sketch, "E636", {"start": v(-68.61, 76.07) * mm, "end": v(-68.61, 76.58) * mm});
            skLineSegment(sketch, "E637", {"start": v(-68.61, 76.58) * mm, "end": v(-68.61, 76.98) * mm});
            skLineSegment(sketch, "E638", {"start": v(-68.61, 76.98) * mm, "end": v(-68.8, 78.06) * mm});
            skLineSegment(sketch, "E639", {"start": v(-68.8, 78.06) * mm, "end": v(-68.83, 78.19) * mm});
            skLineSegment(sketch, "E640", {"start": v(-68.83, 78.19) * mm, "end": v(-68.87, 78.31) * mm});
            skLineSegment(sketch, "E641", {"start": v(-68.87, 78.31) * mm, "end": v(-69.4, 79.49) * mm});
            skLineSegment(sketch, "E642", {"start": v(-69.4, 79.49) * mm, "end": v(-69.46, 79.59) * mm});
            skLineSegment(sketch, "E643", {"start": v(-71.06, 74.4) * mm, "end": v(-71.12, 74.24) * mm});
            skLineSegment(sketch, "E644", {"start": v(-71.12, 74.24) * mm, "end": v(-71.82, 72.94) * mm});
            skLineSegment(sketch, "E645", {"start": v(-71.82, 72.94) * mm, "end": v(-71.9, 72.83) * mm});
            skLineSegment(sketch, "E646", {"start": v(-71.9, 72.83) * mm, "end": v(-72, 72.73) * mm});
            skLineSegment(sketch, "E647", {"start": v(-72, 72.73) * mm, "end": v(-73, 71.9) * mm});
            skLineSegment(sketch, "E648", {"start": v(-73, 71.9) * mm, "end": v(-73.11, 71.83) * mm});
            skLineSegment(sketch, "E649", {"start": v(-73.11, 71.83) * mm, "end": v(-73.22, 71.78) * mm});
            skLineSegment(sketch, "E650", {"start": v(-73.22, 71.78) * mm, "end": v(-74.2, 71.52) * mm});
            skLineSegment(sketch, "E651", {"start": v(-74.2, 71.52) * mm, "end": v(-74.51, 71.52) * mm});
            skLineSegment(sketch, "E652", {"start": v(-74.51, 71.52) * mm, "end": v(-74.89, 71.52) * mm});
            skLineSegment(sketch, "E653", {"start": v(-74.89, 71.52) * mm, "end": v(-75.9, 71.8) * mm});
            skLineSegment(sketch, "E654", {"start": v(-75.9, 71.8) * mm, "end": v(-76.01, 71.86) * mm});
            skLineSegment(sketch, "E655", {"start": v(-76.01, 71.86) * mm, "end": v(-76.13, 71.92) * mm});
            skLineSegment(sketch, "E656", {"start": v(-76.13, 71.92) * mm, "end": v(-77.17, 72.76) * mm});
            skLineSegment(sketch, "E657", {"start": v(-77.17, 72.76) * mm, "end": v(-77.26, 72.87) * mm});
            skLineSegment(sketch, "E658", {"start": v(-77.26, 72.87) * mm, "end": v(-77.35, 72.97) * mm});
            skLineSegment(sketch, "E659", {"start": v(-77.35, 72.97) * mm, "end": v(-78.07, 74.3) * mm});
            skLineSegment(sketch, "E660", {"start": v(-78.07, 74.3) * mm, "end": v(-78.12, 74.46) * mm});
            skLineSegment(sketch, "E661", {"start": v(-78.12, 74.46) * mm, "end": v(-78.17, 74.62) * mm});
            skLineSegment(sketch, "E662", {"start": v(-78.17, 74.62) * mm, "end": v(-78.43, 76.09) * mm});
            skLineSegment(sketch, "E663", {"start": v(-78.43, 76.09) * mm, "end": v(-78.43, 76.58) * mm});
            skLineSegment(sketch, "E664", {"start": v(-78.43, 76.58) * mm, "end": v(-78.43, 77.08) * mm});
            skLineSegment(sketch, "E665", {"start": v(-78.43, 77.08) * mm, "end": v(-78.22, 78.43) * mm});
            skLineSegment(sketch, "E666", {"start": v(-78.22, 78.43) * mm, "end": v(-78.17, 78.59) * mm});
            skLineSegment(sketch, "E667", {"start": v(-78.17, 78.59) * mm, "end": v(-78.13, 78.74) * mm});
            skLineSegment(sketch, "E668", {"start": v(-78.13, 78.74) * mm, "end": v(-77.5, 80.05) * mm});
            skLineSegment(sketch, "E669", {"start": v(-77.5, 80.05) * mm, "end": v(-77.42, 80.16) * mm});
            skLineSegment(sketch, "E670", {"start": v(-77.42, 80.16) * mm, "end": v(-77.34, 80.27) * mm});
            skLineSegment(sketch, "E671", {"start": v(-77.34, 80.27) * mm, "end": v(-76.33, 81.17) * mm});
            skLineSegment(sketch, "E672", {"start": v(-76.33, 81.17) * mm, "end": v(-76.22, 81.23) * mm});
            skLineSegment(sketch, "E673", {"start": v(-76.22, 81.23) * mm, "end": v(-76.1, 81.3) * mm});
            skLineSegment(sketch, "E674", {"start": v(-76.1, 81.3) * mm, "end": v(-74.98, 81.62) * mm});
            skLineSegment(sketch, "E675", {"start": v(-74.98, 81.62) * mm, "end": v(-74.6, 81.62) * mm});
            skLineSegment(sketch, "E676", {"start": v(-74.6, 81.62) * mm, "end": v(-74.2, 81.62) * mm});
            skLineSegment(sketch, "E677", {"start": v(-74.2, 81.62) * mm, "end": v(-73.1, 81.3) * mm});
            skLineSegment(sketch, "E678", {"start": v(-73.1, 81.3) * mm, "end": v(-72.98, 81.23) * mm});
            skLineSegment(sketch, "E679", {"start": v(-72.98, 81.23) * mm, "end": v(-72.86, 81.17) * mm});
            skLineSegment(sketch, "E680", {"start": v(-72.86, 81.17) * mm, "end": v(-71.85, 80.28) * mm});
            skLineSegment(sketch, "E681", {"start": v(-71.85, 80.28) * mm, "end": v(-71.76, 80.17) * mm});
            skLineSegment(sketch, "E682", {"start": v(-71.76, 80.17) * mm, "end": v(-71.68, 80.06) * mm});
            skLineSegment(sketch, "E683", {"start": v(-71.68, 80.06) * mm, "end": v(-71.05, 78.74) * mm});
            skLineSegment(sketch, "E684", {"start": v(-71.05, 78.74) * mm, "end": v(-71, 78.59) * mm});
            skLineSegment(sketch, "E685", {"start": v(-71, 78.59) * mm, "end": v(-70.96, 78.44) * mm});
            skLineSegment(sketch, "E686", {"start": v(-70.96, 78.44) * mm, "end": v(-70.74, 77.04) * mm});
            skLineSegment(sketch, "E687", {"start": v(-70.74, 77.04) * mm, "end": v(-70.74, 76.58) * mm});
            skLineSegment(sketch, "E688", {"start": v(-70.74, 76.58) * mm, "end": v(-70.74, 76.03) * mm});
            skLineSegment(sketch, "E689", {"start": v(-70.74, 76.03) * mm, "end": v(-71, 74.56) * mm});
            skLineSegment(sketch, "E690", {"start": v(-71, 74.56) * mm, "end": v(-71.06, 74.4) * mm});
            skLineSegment(sketch, "E691", {"start": v(-58.23, 81.88) * mm, "end": v(-56.98, 81) * mm});
            skLineSegment(sketch, "E692", {"start": v(-56.98, 81) * mm, "end": v(-56.98, 77.31) * mm});
            skLineSegment(sketch, "E693", {"start": v(-56.98, 77.31) * mm, "end": v(-57.47, 77.3) * mm});
            skLineSegment(sketch, "E694", {"start": v(-57.47, 77.3) * mm, "end": v(-62.24, 77.3) * mm});
            skLineSegment(sketch, "E695", {"start": v(-62.24, 77.3) * mm, "end": v(-62.72, 77.31) * mm});
            skLineSegment(sketch, "E696", {"start": v(-62.72, 77.31) * mm, "end": v(-62.72, 81) * mm});
            skLineSegment(sketch, "E697", {"start": v(-62.72, 81) * mm, "end": v(-61.47, 81.88) * mm});
            skLineSegment(sketch, "E698", {"start": v(-61.47, 81.88) * mm, "end": v(-61.47, 82) * mm});
            skLineSegment(sketch, "E699", {"start": v(-61.47, 82) * mm, "end": v(-65.79, 82) * mm});
            skLineSegment(sketch, "E700", {"start": v(-65.79, 82) * mm, "end": v(-65.79, 81.88) * mm});
            skLineSegment(sketch, "E701", {"start": v(-65.79, 81.88) * mm, "end": v(-64.58, 81) * mm});
            skLineSegment(sketch, "E702", {"start": v(-64.58, 81) * mm, "end": v(-64.58, 72.23) * mm});
            skLineSegment(sketch, "E703", {"start": v(-64.58, 72.23) * mm, "end": v(-65.79, 71.32) * mm});
            skLineSegment(sketch, "E704", {"start": v(-65.79, 71.32) * mm, "end": v(-65.79, 71.19) * mm});
            skLineSegment(sketch, "E705", {"start": v(-65.79, 71.19) * mm, "end": v(-61.47, 71.19) * mm});
            skLineSegment(sketch, "E706", {"start": v(-61.47, 71.19) * mm, "end": v(-61.47, 71.32) * mm});
            skLineSegment(sketch, "E707", {"start": v(-61.47, 71.32) * mm, "end": v(-62.72, 72.23) * mm});
            skLineSegment(sketch, "E708", {"start": v(-62.72, 72.23) * mm, "end": v(-62.72, 76.43) * mm});
            skLineSegment(sketch, "E709", {"start": v(-62.72, 76.43) * mm, "end": v(-62.24, 76.44) * mm});
            skLineSegment(sketch, "E710", {"start": v(-62.24, 76.44) * mm, "end": v(-57.47, 76.44) * mm});
            skLineSegment(sketch, "E711", {"start": v(-57.47, 76.44) * mm, "end": v(-56.98, 76.43) * mm});
            skLineSegment(sketch, "E712", {"start": v(-56.98, 76.43) * mm, "end": v(-56.98, 72.23) * mm});
            skLineSegment(sketch, "E713", {"start": v(-56.98, 72.23) * mm, "end": v(-58.23, 71.32) * mm});
            skLineSegment(sketch, "E714", {"start": v(-58.23, 71.32) * mm, "end": v(-58.23, 71.19) * mm});
            skLineSegment(sketch, "E715", {"start": v(-58.23, 71.19) * mm, "end": v(-53.91, 71.19) * mm});
            skLineSegment(sketch, "E716", {"start": v(-53.91, 71.19) * mm, "end": v(-53.91, 71.32) * mm});
            skLineSegment(sketch, "E717", {"start": v(-53.91, 71.32) * mm, "end": v(-55.13, 72.23) * mm});
            skLineSegment(sketch, "E718", {"start": v(-55.13, 72.23) * mm, "end": v(-55.14, 72.91) * mm});
            skLineSegment(sketch, "E719", {"start": v(-55.14, 72.91) * mm, "end": v(-55.14, 80.22) * mm});
            skLineSegment(sketch, "E720", {"start": v(-55.14, 80.22) * mm, "end": v(-55.13, 81) * mm});
            skLineSegment(sketch, "E721", {"start": v(-55.13, 81) * mm, "end": v(-53.91, 81.88) * mm});
            skLineSegment(sketch, "E722", {"start": v(-53.91, 81.88) * mm, "end": v(-53.91, 82) * mm});
            skLineSegment(sketch, "E723", {"start": v(-53.91, 82) * mm, "end": v(-58.23, 82) * mm});
            skLineSegment(sketch, "E724", {"start": v(-58.23, 82) * mm, "end": v(-58.23, 81.88) * mm});
            skLineSegment(sketch, "E725", {"start": v(32.2, 82.16) * mm, "end": v(30.65, 82.16) * mm});
            skLineSegment(sketch, "E726", {"start": v(30.65, 82.16) * mm, "end": v(26.9, 72.3) * mm});
            skLineSegment(sketch, "E727", {"start": v(26.9, 72.3) * mm, "end": v(25.64, 71.26) * mm});
            skLineSegment(sketch, "E728", {"start": v(25.64, 71.26) * mm, "end": v(25.64, 71.12) * mm});
            skLineSegment(sketch, "E729", {"start": v(25.64, 71.12) * mm, "end": v(29.3, 71.12) * mm});
            skLineSegment(sketch, "E730", {"start": v(29.3, 71.12) * mm, "end": v(29.3, 71.26) * mm});
            skLineSegment(sketch, "E731", {"start": v(29.3, 71.26) * mm, "end": v(27.92, 72.3) * mm});
            skLineSegment(sketch, "E732", {"start": v(27.92, 72.3) * mm, "end": v(28.96, 75.15) * mm});
            skLineSegment(sketch, "E733", {"start": v(28.96, 75.15) * mm, "end": v(29.32, 75.16) * mm});
            skLineSegment(sketch, "E734", {"start": v(29.32, 75.16) * mm, "end": v(32.7, 75.16) * mm});
            skLineSegment(sketch, "E735", {"start": v(32.7, 75.16) * mm, "end": v(33.02, 75.15) * mm});
            skLineSegment(sketch, "E736", {"start": v(33.02, 75.15) * mm, "end": v(34.14, 72.3) * mm});
            skLineSegment(sketch, "E737", {"start": v(34.14, 72.3) * mm, "end": v(32.75, 71.26) * mm});
            skLineSegment(sketch, "E738", {"start": v(32.75, 71.26) * mm, "end": v(32.75, 71.12) * mm});
            skLineSegment(sketch, "E739", {"start": v(32.75, 71.12) * mm, "end": v(37.5, 71.12) * mm});
            skLineSegment(sketch, "E740", {"start": v(37.5, 71.12) * mm, "end": v(37.5, 71.26) * mm});
            skLineSegment(sketch, "E741", {"start": v(37.5, 71.26) * mm, "end": v(36.25, 72.34) * mm});
            skLineSegment(sketch, "E742", {"start": v(36.25, 72.34) * mm, "end": v(32.2, 82.16) * mm});
            skLineSegment(sketch, "E743", {"start": v(29.28, 75.96) * mm, "end": v(30.94, 80.54) * mm});
            skLineSegment(sketch, "E744", {"start": v(30.94, 80.54) * mm, "end": v(32.71, 75.96) * mm});
            skLineSegment(sketch, "E745", {"start": v(32.71, 75.96) * mm, "end": v(29.28, 75.96) * mm});
            skLineSegment(sketch, "E746", {"start": v(72.4, 72.05) * mm, "end": v(72, 72.03) * mm});
            skLineSegment(sketch, "E747", {"start": v(72, 72.03) * mm, "end": v(68.31, 72.03) * mm});
            skLineSegment(sketch, "E748", {"start": v(68.31, 72.03) * mm, "end": v(67.97, 72.05) * mm});
            skLineSegment(sketch, "E749", {"start": v(67.97, 72.05) * mm, "end": v(67.96, 72.4) * mm});
            skLineSegment(sketch, "E750", {"start": v(67.96, 72.4) * mm, "end": v(67.96, 75.95) * mm});
            skLineSegment(sketch, "E751", {"start": v(67.96, 75.95) * mm, "end": v(67.97, 76.3) * mm});
            skLineSegment(sketch, "E752", {"start": v(67.97, 76.3) * mm, "end": v(68.17, 76.3) * mm});
            skLineSegment(sketch, "E753", {"start": v(68.17, 76.3) * mm, "end": v(69.41, 76.33) * mm});
            skLineSegment(sketch, "E754", {"start": v(69.41, 76.33) * mm, "end": v(70.89, 76.34) * mm});
            skLineSegment(sketch, "E755", {"start": v(70.89, 76.34) * mm, "end": v(71.38, 76.34) * mm});
            skLineSegment(sketch, "E756", {"start": v(71.38, 76.34) * mm, "end": v(72.22, 75.1) * mm});
            skLineSegment(sketch, "E757", {"start": v(72.22, 75.1) * mm, "end": v(72.34, 75.1) * mm});
            skLineSegment(sketch, "E758", {"start": v(72.34, 75.1) * mm, "end": v(72.34, 78.44) * mm});
            skLineSegment(sketch, "E759", {"start": v(72.34, 78.44) * mm, "end": v(72.22, 78.44) * mm});
            skLineSegment(sketch, "E760", {"start": v(72.22, 78.44) * mm, "end": v(71.38, 77.19) * mm});
            skLineSegment(sketch, "E761", {"start": v(71.38, 77.19) * mm, "end": v(70.8, 77.19) * mm});
            skLineSegment(sketch, "E762", {"start": v(70.8, 77.19) * mm, "end": v(69.07, 77.2) * mm});
            skLineSegment(sketch, "E763", {"start": v(69.07, 77.2) * mm, "end": v(68.03, 77.22) * mm});
            skLineSegment(sketch, "E764", {"start": v(68.03, 77.22) * mm, "end": v(67.94, 77.23) * mm});
            skLineSegment(sketch, "E765", {"start": v(67.94, 77.23) * mm, "end": v(67.94, 77.38) * mm});
            skLineSegment(sketch, "E766", {"start": v(67.94, 77.38) * mm, "end": v(67.91, 78.65) * mm});
            skLineSegment(sketch, "E767", {"start": v(67.91, 78.65) * mm, "end": v(67.91, 79.07) * mm});
            skLineSegment(sketch, "E768", {"start": v(67.91, 79.07) * mm, "end": v(67.9, 79.23) * mm});
            skLineSegment(sketch, "E769", {"start": v(67.9, 79.23) * mm, "end": v(67.92, 80.81) * mm});
            skLineSegment(sketch, "E770", {"start": v(67.92, 80.81) * mm, "end": v(67.93, 80.98) * mm});
            skLineSegment(sketch, "E771", {"start": v(67.93, 80.98) * mm, "end": v(68.1, 81) * mm});
            skLineSegment(sketch, "E772", {"start": v(68.1, 81) * mm, "end": v(69.54, 81.04) * mm});
            skLineSegment(sketch, "E773", {"start": v(69.54, 81.04) * mm, "end": v(70.03, 81.04) * mm});
            skLineSegment(sketch, "E774", {"start": v(70.03, 81.04) * mm, "end": v(70.6, 81.04) * mm});
            skLineSegment(sketch, "E775", {"start": v(70.6, 81.04) * mm, "end": v(71.9, 81.03) * mm});
            skLineSegment(sketch, "E776", {"start": v(71.9, 81.03) * mm, "end": v(72.34, 81.03) * mm});
            skLineSegment(sketch, "E777", {"start": v(72.34, 81.03) * mm, "end": v(73.23, 79.78) * mm});
            skLineSegment(sketch, "E778", {"start": v(73.23, 79.78) * mm, "end": v(73.34, 79.78) * mm});
            skLineSegment(sketch, "E779", {"start": v(73.34, 79.78) * mm, "end": v(73.34, 81.92) * mm});
            skLineSegment(sketch, "E780", {"start": v(73.34, 81.92) * mm, "end": v(64.87, 81.92) * mm});
            skLineSegment(sketch, "E781", {"start": v(64.87, 81.92) * mm, "end": v(64.87, 81.81) * mm});
            skLineSegment(sketch, "E782", {"start": v(64.87, 81.81) * mm, "end": v(66.1, 80.93) * mm});
            skLineSegment(sketch, "E783", {"start": v(66.1, 80.93) * mm, "end": v(66.1, 80.3) * mm});
            skLineSegment(sketch, "E784", {"start": v(66.1, 80.3) * mm, "end": v(66.13, 76.86) * mm});
            skLineSegment(sketch, "E785", {"start": v(66.13, 76.86) * mm, "end": v(66.1, 73) * mm});
            skLineSegment(sketch, "E786", {"start": v(66.1, 73) * mm, "end": v(66.1, 72.16) * mm});
            skLineSegment(sketch, "E787", {"start": v(66.1, 72.16) * mm, "end": v(64.87, 71.26) * mm});
            skLineSegment(sketch, "E788", {"start": v(64.87, 71.26) * mm, "end": v(64.87, 71.12) * mm});
            skLineSegment(sketch, "E789", {"start": v(64.87, 71.12) * mm, "end": v(73.57, 71.12) * mm});
            skLineSegment(sketch, "E790", {"start": v(73.57, 71.12) * mm, "end": v(73.57, 73.52) * mm});
            skLineSegment(sketch, "E791", {"start": v(73.57, 73.52) * mm, "end": v(73.44, 73.52) * mm});
            skLineSegment(sketch, "E792", {"start": v(73.44, 73.52) * mm, "end": v(72.4, 72.05) * mm});
            skLineSegment(sketch, "E793", {"start": v(87.18, 71.44) * mm, "end": v(87.16, 71.46) * mm});
            skLineSegment(sketch, "E794", {"start": v(87.16, 71.46) * mm, "end": v(86.89, 71.73) * mm});
            skLineSegment(sketch, "E795", {"start": v(86.89, 71.73) * mm, "end": v(86.86, 71.75) * mm});
            skLineSegment(sketch, "E796", {"start": v(86.86, 71.75) * mm, "end": v(86.83, 71.79) * mm});
            skLineSegment(sketch, "E797", {"start": v(86.83, 71.79) * mm, "end": v(86.56, 72.15) * mm});
            skLineSegment(sketch, "E798", {"start": v(86.56, 72.15) * mm, "end": v(86.54, 72.18) * mm});
            skLineSegment(sketch, "E799", {"start": v(86.54, 72.18) * mm, "end": v(86.5, 72.2) * mm});
            skLineSegment(sketch, "E800", {"start": v(86.5, 72.2) * mm, "end": v(86.29, 72.48) * mm});
            skLineSegment(sketch, "E801", {"start": v(86.29, 72.48) * mm, "end": v(86.27, 72.5) * mm});
            skLineSegment(sketch, "E802", {"start": v(86.27, 72.5) * mm, "end": v(84.57, 75.15) * mm});
            skLineSegment(sketch, "E803", {"start": v(84.57, 75.15) * mm, "end": v(84.52, 75.23) * mm});
            skLineSegment(sketch, "E804", {"start": v(84.52, 75.23) * mm, "end": v(84, 75.83) * mm});
            skLineSegment(sketch, "E805", {"start": v(84, 75.83) * mm, "end": v(83.94, 75.88) * mm});
            skLineSegment(sketch, "E806", {"start": v(83.94, 75.88) * mm, "end": v(83.88, 75.92) * mm});
            skLineSegment(sketch, "E807", {"start": v(83.88, 75.92) * mm, "end": v(83.12, 76.17) * mm});
            skLineSegment(sketch, "E808", {"start": v(83.12, 76.17) * mm, "end": v(83.03, 76.18) * mm});
            skLineSegment(sketch, "E809", {"start": v(83.03, 76.18) * mm, "end": v(83.15, 76.18) * mm});
            skLineSegment(sketch, "E810", {"start": v(83.15, 76.18) * mm, "end": v(84.33, 76.4) * mm});
            skLineSegment(sketch, "E811", {"start": v(84.33, 76.4) * mm, "end": v(84.44, 76.43) * mm});
            skLineSegment(sketch, "E812", {"start": v(84.44, 76.43) * mm, "end": v(84.55, 76.47) * mm});
            skLineSegment(sketch, "E813", {"start": v(84.55, 76.47) * mm, "end": v(85.48, 76.96) * mm});
            skLineSegment(sketch, "E814", {"start": v(85.48, 76.96) * mm, "end": v(85.56, 77.02) * mm});
            skLineSegment(sketch, "E815", {"start": v(85.56, 77.02) * mm, "end": v(85.64, 77.08) * mm});
            skLineSegment(sketch, "E816", {"start": v(85.64, 77.08) * mm, "end": v(86.25, 77.8) * mm});
            skLineSegment(sketch, "E817", {"start": v(86.25, 77.8) * mm, "end": v(86.3, 77.88) * mm});
            skLineSegment(sketch, "E818", {"start": v(86.3, 77.88) * mm, "end": v(86.34, 77.97) * mm});
            skLineSegment(sketch, "E819", {"start": v(86.34, 77.97) * mm, "end": v(86.57, 78.74) * mm});
            skLineSegment(sketch, "E820", {"start": v(86.57, 78.74) * mm, "end": v(86.57, 79) * mm});
            skLineSegment(sketch, "E821", {"start": v(86.57, 79) * mm, "end": v(86.57, 79.29) * mm});
            skLineSegment(sketch, "E822", {"start": v(86.57, 79.29) * mm, "end": v(86.3, 80.07) * mm});
            skLineSegment(sketch, "E823", {"start": v(86.3, 80.07) * mm, "end": v(86.26, 80.16) * mm});
            skLineSegment(sketch, "E824", {"start": v(86.26, 80.16) * mm, "end": v(86.2, 80.25) * mm});
            skLineSegment(sketch, "E825", {"start": v(86.2, 80.25) * mm, "end": v(85.48, 81.04) * mm});
            skLineSegment(sketch, "E826", {"start": v(85.48, 81.04) * mm, "end": v(85.4, 81.1) * mm});
            skLineSegment(sketch, "E827", {"start": v(85.4, 81.1) * mm, "end": v(85.3, 81.18) * mm});
            skLineSegment(sketch, "E828", {"start": v(85.3, 81.18) * mm, "end": v(84.17, 81.68) * mm});
            skLineSegment(sketch, "E829", {"start": v(84.17, 81.68) * mm, "end": v(84.04, 81.71) * mm});
            skLineSegment(sketch, "E830", {"start": v(84.04, 81.71) * mm, "end": v(83.9, 81.75) * mm});
            skLineSegment(sketch, "E831", {"start": v(83.9, 81.75) * mm, "end": v(82.7, 81.92) * mm});
            skLineSegment(sketch, "E832", {"start": v(82.7, 81.92) * mm, "end": v(82.29, 81.92) * mm});
            skLineSegment(sketch, "E833", {"start": v(82.29, 81.92) * mm, "end": v(77.26, 81.92) * mm});
            skLineSegment(sketch, "E834", {"start": v(77.26, 81.92) * mm, "end": v(77.26, 81.81) * mm});
            skLineSegment(sketch, "E835", {"start": v(77.26, 81.81) * mm, "end": v(78.48, 80.9) * mm});
            skLineSegment(sketch, "E836", {"start": v(78.48, 80.9) * mm, "end": v(78.48, 72.16) * mm});
            skLineSegment(sketch, "E837", {"start": v(78.48, 72.16) * mm, "end": v(77.19, 71.26) * mm});
            skLineSegment(sketch, "E838", {"start": v(77.19, 71.26) * mm, "end": v(77.19, 71.12) * mm});
            skLineSegment(sketch, "E839", {"start": v(77.19, 71.12) * mm, "end": v(81.6, 71.12) * mm});
            skLineSegment(sketch, "E840", {"start": v(81.6, 71.12) * mm, "end": v(81.6, 71.26) * mm});
            skLineSegment(sketch, "E841", {"start": v(81.6, 71.26) * mm, "end": v(80.4, 72.1) * mm});
            skLineSegment(sketch, "E842", {"start": v(80.4, 72.1) * mm, "end": v(80.35, 75.81) * mm});
            skLineSegment(sketch, "E843", {"start": v(80.35, 75.81) * mm, "end": v(80.41, 75.82) * mm});
            skLineSegment(sketch, "E844", {"start": v(80.41, 75.82) * mm, "end": v(80.9, 75.85) * mm});
            skLineSegment(sketch, "E845", {"start": v(80.9, 75.85) * mm, "end": v(81.06, 75.85) * mm});
            skLineSegment(sketch, "E846", {"start": v(81.06, 75.85) * mm, "end": v(81.52, 75.85) * mm});
            skLineSegment(sketch, "E847", {"start": v(81.52, 75.85) * mm, "end": v(81.66, 75.85) * mm});
            skLineSegment(sketch, "E848", {"start": v(81.66, 75.85) * mm, "end": v(82.03, 75.77) * mm});
            skLineSegment(sketch, "E849", {"start": v(82.03, 75.77) * mm, "end": v(82.06, 75.75) * mm});
            skLineSegment(sketch, "E850", {"start": v(82.06, 75.75) * mm, "end": v(82.09, 75.74) * mm});
            skLineSegment(sketch, "E851", {"start": v(82.09, 75.74) * mm, "end": v(82.4, 75.43) * mm});
            skLineSegment(sketch, "E852", {"start": v(82.4, 75.43) * mm, "end": v(82.43, 75.38) * mm});
            skLineSegment(sketch, "E853", {"start": v(82.43, 75.38) * mm, "end": v(84.96, 71.12) * mm});
            skLineSegment(sketch, "E854", {"start": v(84.96, 71.12) * mm, "end": v(87.42, 71.12) * mm});
            skLineSegment(sketch, "E855", {"start": v(87.42, 71.12) * mm, "end": v(87.42, 71.26) * mm});
            skLineSegment(sketch, "E856", {"start": v(87.42, 71.26) * mm, "end": v(87.4, 71.27) * mm});
            skLineSegment(sketch, "E857", {"start": v(87.4, 71.27) * mm, "end": v(87.2, 71.41) * mm});
            skLineSegment(sketch, "E858", {"start": v(87.2, 71.41) * mm, "end": v(87.18, 71.44) * mm});
            skLineSegment(sketch, "E859", {"start": v(81.58, 76.6) * mm, "end": v(81, 76.6) * mm});
            skLineSegment(sketch, "E860", {"start": v(81, 76.6) * mm, "end": v(80.97, 76.6) * mm});
            skLineSegment(sketch, "E861", {"start": v(80.97, 76.6) * mm, "end": v(80.73, 76.6) * mm});
            skLineSegment(sketch, "E862", {"start": v(80.73, 76.6) * mm, "end": v(80.66, 76.6) * mm});
            skLineSegment(sketch, "E863", {"start": v(80.66, 76.6) * mm, "end": v(80.58, 76.6) * mm});
            skLineSegment(sketch, "E864", {"start": v(80.58, 76.6) * mm, "end": v(80.38, 76.62) * mm});
            skLineSegment(sketch, "E865", {"start": v(80.38, 76.62) * mm, "end": v(80.36, 76.62) * mm});
            skLineSegment(sketch, "E866", {"start": v(80.36, 76.62) * mm, "end": v(80.38, 81.07) * mm});
            skLineSegment(sketch, "E867", {"start": v(80.38, 81.07) * mm, "end": v(80.5, 81.07) * mm});
            skLineSegment(sketch, "E868", {"start": v(80.5, 81.07) * mm, "end": v(80.82, 81.1) * mm});
            skLineSegment(sketch, "E869", {"start": v(80.82, 81.1) * mm, "end": v(80.86, 81.1) * mm});
            skLineSegment(sketch, "E870", {"start": v(80.86, 81.1) * mm, "end": v(80.9, 81.1) * mm});
            skLineSegment(sketch, "E871", {"start": v(80.9, 81.1) * mm, "end": v(81.32, 81.1) * mm});
            skLineSegment(sketch, "E872", {"start": v(81.32, 81.1) * mm, "end": v(81.37, 81.1) * mm});
            skLineSegment(sketch, "E873", {"start": v(81.37, 81.1) * mm, "end": v(81.4, 81.11) * mm});
            skLineSegment(sketch, "E874", {"start": v(81.4, 81.11) * mm, "end": v(81.69, 81.13) * mm});
            skLineSegment(sketch, "E875", {"start": v(81.69, 81.13) * mm, "end": v(81.78, 81.13) * mm});
            skLineSegment(sketch, "E876", {"start": v(81.78, 81.13) * mm, "end": v(82.06, 81.13) * mm});
            skLineSegment(sketch, "E877", {"start": v(82.06, 81.13) * mm, "end": v(82.15, 81.13) * mm});
            skLineSegment(sketch, "E878", {"start": v(82.15, 81.13) * mm, "end": v(82.97, 80.98) * mm});
            skLineSegment(sketch, "E879", {"start": v(82.97, 80.98) * mm, "end": v(83.04, 80.96) * mm});
            skLineSegment(sketch, "E880", {"start": v(83.04, 80.96) * mm, "end": v(83.12, 80.93) * mm});
            skLineSegment(sketch, "E881", {"start": v(83.12, 80.93) * mm, "end": v(83.75, 80.51) * mm});
            skLineSegment(sketch, "E882", {"start": v(83.75, 80.51) * mm, "end": v(83.8, 80.46) * mm});
            skLineSegment(sketch, "E883", {"start": v(83.8, 80.46) * mm, "end": v(83.85, 80.41) * mm});
            skLineSegment(sketch, "E884", {"start": v(83.85, 80.41) * mm, "end": v(84.24, 79.84) * mm});
            skLineSegment(sketch, "E885", {"start": v(84.24, 79.84) * mm, "end": v(84.27, 79.78) * mm});
            skLineSegment(sketch, "E886", {"start": v(84.27, 79.78) * mm, "end": v(84.3, 79.71) * mm});
            skLineSegment(sketch, "E887", {"start": v(84.3, 79.71) * mm, "end": v(84.43, 79.14) * mm});
            skLineSegment(sketch, "E888", {"start": v(84.43, 79.14) * mm, "end": v(84.43, 78.94) * mm});
            skLineSegment(sketch, "E889", {"start": v(84.43, 78.94) * mm, "end": v(84.43, 78.7) * mm});
            skLineSegment(sketch, "E890", {"start": v(84.43, 78.7) * mm, "end": v(84.25, 77.94) * mm});
            skLineSegment(sketch, "E891", {"start": v(84.25, 77.94) * mm, "end": v(83.82, 77.3) * mm});
            skLineSegment(sketch, "E892", {"start": v(83.82, 77.3) * mm, "end": v(83.7, 77.2) * mm});
            skLineSegment(sketch, "E893", {"start": v(83.7, 77.2) * mm, "end": v(83.57, 77.1) * mm});
            skLineSegment(sketch, "E894", {"start": v(83.57, 77.1) * mm, "end": v(82.8, 76.75) * mm});
            skLineSegment(sketch, "E895", {"start": v(82.8, 76.75) * mm, "end": v(81.88, 76.6) * mm});
            skLineSegment(sketch, "E896", {"start": v(81.88, 76.6) * mm, "end": v(81.58, 76.6) * mm});
            skLineSegment(sketch, "E897", {"start": v(56.22, 77.38) * mm, "end": v(56.46, 77.6) * mm});
            skLineSegment(sketch, "E898", {"start": v(56.46, 77.6) * mm, "end": v(57.53, 78.61) * mm});
            skLineSegment(sketch, "E899", {"start": v(57.53, 78.61) * mm, "end": v(58.46, 79.48) * mm});
            skLineSegment(sketch, "E900", {"start": v(58.46, 79.48) * mm, "end": v(58.63, 79.63) * mm});
            skLineSegment(sketch, "E901", {"start": v(58.63, 79.63) * mm, "end": v(58.8, 79.78) * mm});
            skLineSegment(sketch, "E902", {"start": v(58.8, 79.78) * mm, "end": v(59.5, 80.4) * mm});
            skLineSegment(sketch, "E903", {"start": v(59.5, 80.4) * mm, "end": v(60.03, 80.88) * mm});
            skLineSegment(sketch, "E904", {"start": v(60.03, 80.88) * mm, "end": v(60.12, 80.96) * mm});
            skLineSegment(sketch, "E905", {"start": v(60.12, 80.96) * mm, "end": v(61.75, 81.81) * mm});
            skLineSegment(sketch, "E906", {"start": v(61.75, 81.81) * mm, "end": v(61.75, 81.92) * mm});
            skLineSegment(sketch, "E907", {"start": v(61.75, 81.92) * mm, "end": v(58.12, 81.92) * mm});
            skLineSegment(sketch, "E908", {"start": v(58.12, 81.92) * mm, "end": v(58.12, 81.81) * mm});
            skLineSegment(sketch, "E909", {"start": v(58.12, 81.81) * mm, "end": v(58.67, 80.97) * mm});
            skLineSegment(sketch, "E910", {"start": v(58.67, 80.97) * mm, "end": v(58.58, 80.87) * mm});
            skLineSegment(sketch, "E911", {"start": v(58.58, 80.87) * mm, "end": v(57.61, 79.9) * mm});
            skLineSegment(sketch, "E912", {"start": v(57.61, 79.9) * mm, "end": v(57.52, 79.8) * mm});
            skLineSegment(sketch, "E913", {"start": v(57.52, 79.8) * mm, "end": v(57.42, 79.71) * mm});
            skLineSegment(sketch, "E914", {"start": v(57.42, 79.71) * mm, "end": v(56.45, 78.8) * mm});
            skLineSegment(sketch, "E915", {"start": v(56.45, 78.8) * mm, "end": v(56.35, 78.72) * mm});
            skLineSegment(sketch, "E916", {"start": v(56.35, 78.72) * mm, "end": v(56.26, 78.63) * mm});
            skLineSegment(sketch, "E917", {"start": v(56.26, 78.63) * mm, "end": v(55.35, 77.79) * mm});
            skLineSegment(sketch, "E918", {"start": v(55.35, 77.79) * mm, "end": v(55.26, 77.7) * mm});
            skLineSegment(sketch, "E919", {"start": v(55.26, 77.7) * mm, "end": v(55.17, 77.63) * mm});
            skLineSegment(sketch, "E920", {"start": v(55.17, 77.63) * mm, "end": v(54.33, 76.9) * mm});
            skLineSegment(sketch, "E921", {"start": v(54.33, 76.9) * mm, "end": v(54.24, 76.84) * mm});
            skLineSegment(sketch, "E922", {"start": v(54.24, 76.84) * mm, "end": v(54.56, 76.52) * mm});
            skLineSegment(sketch, "E923", {"start": v(54.56, 76.52) * mm, "end": v(56.26, 74.72) * mm});
            skLineSegment(sketch, "E924", {"start": v(56.26, 74.72) * mm, "end": v(58.17, 72.59) * mm});
            skLineSegment(sketch, "E925", {"start": v(58.17, 72.59) * mm, "end": v(58.59, 72.1) * mm});
            skLineSegment(sketch, "E926", {"start": v(58.59, 72.1) * mm, "end": v(58.12, 71.26) * mm});
            skLineSegment(sketch, "E927", {"start": v(58.12, 71.26) * mm, "end": v(58.12, 71.12) * mm});
            skLineSegment(sketch, "E928", {"start": v(58.12, 71.12) * mm, "end": v(62.05, 71.12) * mm});
            skLineSegment(sketch, "E929", {"start": v(62.05, 71.12) * mm, "end": v(62.05, 71.26) * mm});
            skLineSegment(sketch, "E930", {"start": v(62.05, 71.26) * mm, "end": v(61.2, 72.1) * mm});
            skLineSegment(sketch, "E931", {"start": v(61.2, 72.1) * mm, "end": v(60.8, 72.53) * mm});
            skLineSegment(sketch, "E932", {"start": v(60.8, 72.53) * mm, "end": v(59.59, 73.79) * mm});
            skLineSegment(sketch, "E933", {"start": v(59.59, 73.79) * mm, "end": v(58.22, 75.22) * mm});
            skLineSegment(sketch, "E934", {"start": v(58.22, 75.22) * mm, "end": v(57.1, 76.42) * mm});
            skLineSegment(sketch, "E935", {"start": v(57.1, 76.42) * mm, "end": v(56.44, 77.14) * mm});
            skLineSegment(sketch, "E936", {"start": v(56.44, 77.14) * mm, "end": v(56.22, 77.38) * mm});
            skLineSegment(sketch, "E937", {"start": v(54.24, 80.93) * mm, "end": v(55.5, 81.81) * mm});
            skLineSegment(sketch, "E938", {"start": v(55.5, 81.81) * mm, "end": v(55.5, 81.92) * mm});
            skLineSegment(sketch, "E939", {"start": v(55.5, 81.92) * mm, "end": v(51.12, 81.92) * mm});
            skLineSegment(sketch, "E940", {"start": v(51.12, 81.92) * mm, "end": v(51.12, 81.81) * mm});
            skLineSegment(sketch, "E941", {"start": v(51.12, 81.81) * mm, "end": v(52.36, 80.93) * mm});
            skLineSegment(sketch, "E942", {"start": v(52.36, 80.93) * mm, "end": v(52.36, 80.2) * mm});
            skLineSegment(sketch, "E943", {"start": v(52.36, 80.2) * mm, "end": v(52.36, 72.9) * mm});
            skLineSegment(sketch, "E944", {"start": v(52.36, 72.9) * mm, "end": v(52.36, 72.16) * mm});
            skLineSegment(sketch, "E945", {"start": v(52.36, 72.16) * mm, "end": v(51.07, 71.26) * mm});
            skLineSegment(sketch, "E946", {"start": v(51.07, 71.26) * mm, "end": v(51.07, 71.12) * mm});
            skLineSegment(sketch, "E947", {"start": v(51.07, 71.12) * mm, "end": v(55.53, 71.12) * mm});
            skLineSegment(sketch, "E948", {"start": v(55.53, 71.12) * mm, "end": v(55.53, 71.26) * mm});
            skLineSegment(sketch, "E949", {"start": v(55.53, 71.26) * mm, "end": v(54.24, 72.16) * mm});
            skLineSegment(sketch, "E950", {"start": v(54.24, 72.16) * mm, "end": v(54.24, 72.9) * mm});
            skLineSegment(sketch, "E951", {"start": v(54.24, 72.9) * mm, "end": v(54.24, 80.21) * mm});
            skLineSegment(sketch, "E952", {"start": v(54.24, 80.21) * mm, "end": v(54.24, 80.93) * mm});
            skLineSegment(sketch, "E953", {"start": v(47.18, 72.1) * mm, "end": v(45.04, 72.1) * mm});
            skLineSegment(sketch, "E954", {"start": v(45.04, 72.1) * mm, "end": v(44.57, 72.1) * mm});
            skLineSegment(sketch, "E955", {"start": v(44.57, 72.1) * mm, "end": v(43.54, 72.1) * mm});
            skLineSegment(sketch, "E956", {"start": v(43.54, 72.1) * mm, "end": v(43.2, 72.1) * mm});
            skLineSegment(sketch, "E957", {"start": v(43.2, 72.1) * mm, "end": v(43.18, 72.85) * mm});
            skLineSegment(sketch, "E958", {"start": v(43.18, 72.85) * mm, "end": v(43.18, 80.2) * mm});
            skLineSegment(sketch, "E959", {"start": v(43.18, 80.2) * mm, "end": v(43.2, 80.93) * mm});
            skLineSegment(sketch, "E960", {"start": v(43.2, 80.93) * mm, "end": v(44.56, 81.8) * mm});
            skLineSegment(sketch, "E961", {"start": v(44.56, 81.8) * mm, "end": v(44.56, 81.91) * mm});
            skLineSegment(sketch, "E962", {"start": v(44.56, 81.91) * mm, "end": v(40.06, 81.91) * mm});
            skLineSegment(sketch, "E963", {"start": v(40.06, 81.91) * mm, "end": v(40.06, 81.8) * mm});
            skLineSegment(sketch, "E964", {"start": v(40.06, 81.8) * mm, "end": v(41.3, 80.93) * mm});
            skLineSegment(sketch, "E965", {"start": v(41.3, 80.93) * mm, "end": v(41.3, 80.2) * mm});
            skLineSegment(sketch, "E966", {"start": v(41.3, 80.2) * mm, "end": v(41.3, 72.9) * mm});
            skLineSegment(sketch, "E967", {"start": v(41.3, 72.9) * mm, "end": v(41.3, 72.16) * mm});
            skLineSegment(sketch, "E968", {"start": v(41.3, 72.16) * mm, "end": v(40.06, 71.26) * mm});
            skLineSegment(sketch, "E969", {"start": v(40.06, 71.26) * mm, "end": v(40.06, 71.12) * mm});
            skLineSegment(sketch, "E970", {"start": v(40.06, 71.12) * mm, "end": v(48.34, 71.12) * mm});
            skLineSegment(sketch, "E971", {"start": v(48.34, 71.12) * mm, "end": v(48.34, 73.53) * mm});
            skLineSegment(sketch, "E972", {"start": v(48.34, 73.53) * mm, "end": v(48.19, 73.53) * mm});
            skLineSegment(sketch, "E973", {"start": v(48.19, 73.53) * mm, "end": v(47.18, 72.1) * mm});
            skLineSegment(sketch, "E974", {"start": v(91.9, 72.54) * mm, "end": v(91.9, 72.68) * mm});
            skLineSegment(sketch, "E975", {"start": v(91.9, 72.68) * mm, "end": v(91.78, 73.1) * mm});
            skLineSegment(sketch, "E976", {"start": v(91.78, 73.1) * mm, "end": v(91.48, 73.54) * mm});
            skLineSegment(sketch, "E977", {"start": v(91.48, 73.54) * mm, "end": v(91.03, 73.85) * mm});
            skLineSegment(sketch, "E978", {"start": v(91.03, 73.85) * mm, "end": v(90.6, 73.96) * mm});
            skLineSegment(sketch, "E979", {"start": v(90.6, 73.96) * mm, "end": v(90.47, 73.96) * mm});
            skLineSegment(sketch, "E980", {"start": v(90.47, 73.96) * mm, "end": v(90.33, 73.96) * mm});
            skLineSegment(sketch, "E981", {"start": v(90.33, 73.96) * mm, "end": v(89.9, 73.85) * mm});
            skLineSegment(sketch, "E982", {"start": v(89.9, 73.85) * mm, "end": v(89.46, 73.54) * mm});
            skLineSegment(sketch, "E983", {"start": v(89.46, 73.54) * mm, "end": v(89.15, 73.09) * mm});
            skLineSegment(sketch, "E984", {"start": v(89.15, 73.09) * mm, "end": v(89.04, 72.67) * mm});
            skLineSegment(sketch, "E985", {"start": v(89.04, 72.67) * mm, "end": v(89.04, 72.53) * mm});
            skLineSegment(sketch, "E986", {"start": v(89.04, 72.53) * mm, "end": v(89.04, 72.4) * mm});
            skLineSegment(sketch, "E987", {"start": v(89.04, 72.4) * mm, "end": v(89.15, 71.98) * mm});
            skLineSegment(sketch, "E988", {"start": v(89.15, 71.98) * mm, "end": v(89.45, 71.53) * mm});
            skLineSegment(sketch, "E989", {"start": v(89.45, 71.53) * mm, "end": v(89.9, 71.22) * mm});
            skLineSegment(sketch, "E990", {"start": v(89.9, 71.22) * mm, "end": v(90.32, 71.11) * mm});
            skLineSegment(sketch, "E991", {"start": v(90.32, 71.11) * mm, "end": v(90.46, 71.11) * mm});
            skLineSegment(sketch, "E992", {"start": v(90.46, 71.11) * mm, "end": v(90.6, 71.11) * mm});
            skLineSegment(sketch, "E993", {"start": v(90.6, 71.11) * mm, "end": v(91.02, 71.23) * mm});
            skLineSegment(sketch, "E994", {"start": v(91.02, 71.23) * mm, "end": v(91.48, 71.54) * mm});
            skLineSegment(sketch, "E995", {"start": v(91.48, 71.54) * mm, "end": v(91.78, 71.99) * mm});
            skLineSegment(sketch, "E996", {"start": v(91.78, 71.99) * mm, "end": v(91.9, 72.4) * mm});
            skLineSegment(sketch, "E997", {"start": v(91.9, 72.4) * mm, "end": v(91.9, 72.54) * mm});
            skLineSegment(sketch, "E998", {"start": v(91.73, 72.54) * mm, "end": v(91.73, 72.42) * mm});
            skLineSegment(sketch, "E999", {"start": v(91.73, 72.42) * mm, "end": v(91.63, 72.05) * mm});
            skLineSegment(sketch, "E1000", {"start": v(91.63, 72.05) * mm, "end": v(91.36, 71.64) * mm});
            skLineSegment(sketch, "E1001", {"start": v(91.36, 71.64) * mm, "end": v(90.96, 71.37) * mm});
            skLineSegment(sketch, "E1002", {"start": v(90.96, 71.37) * mm, "end": v(90.59, 71.27) * mm});
            skLineSegment(sketch, "E1003", {"start": v(90.59, 71.27) * mm, "end": v(90.46, 71.27) * mm});
            skLineSegment(sketch, "E1004", {"start": v(90.46, 71.27) * mm, "end": v(90.34, 71.27) * mm});
            skLineSegment(sketch, "E1005", {"start": v(90.34, 71.27) * mm, "end": v(89.96, 71.37) * mm});
            skLineSegment(sketch, "E1006", {"start": v(89.96, 71.37) * mm, "end": v(89.57, 71.64) * mm});
            skLineSegment(sketch, "E1007", {"start": v(89.57, 71.64) * mm, "end": v(89.3, 72.04) * mm});
            skLineSegment(sketch, "E1008", {"start": v(89.3, 72.04) * mm, "end": v(89.2, 72.41) * mm});
            skLineSegment(sketch, "E1009", {"start": v(89.2, 72.41) * mm, "end": v(89.2, 72.53) * mm});
            skLineSegment(sketch, "E1010", {"start": v(89.2, 72.53) * mm, "end": v(89.2, 72.66) * mm});
            skLineSegment(sketch, "E1011", {"start": v(89.2, 72.66) * mm, "end": v(89.3, 73.03) * mm});
            skLineSegment(sketch, "E1012", {"start": v(89.3, 73.03) * mm, "end": v(89.57, 73.43) * mm});
            skLineSegment(sketch, "E1013", {"start": v(89.57, 73.43) * mm, "end": v(89.97, 73.7) * mm});
            skLineSegment(sketch, "E1014", {"start": v(89.97, 73.7) * mm, "end": v(90.34, 73.8) * mm});
            skLineSegment(sketch, "E1015", {"start": v(90.34, 73.8) * mm, "end": v(90.47, 73.8) * mm});
            skLineSegment(sketch, "E1016", {"start": v(90.47, 73.8) * mm, "end": v(90.6, 73.8) * mm});
            skLineSegment(sketch, "E1017", {"start": v(90.6, 73.8) * mm, "end": v(90.97, 73.7) * mm});
            skLineSegment(sketch, "E1018", {"start": v(90.97, 73.7) * mm, "end": v(91.37, 73.44) * mm});
            skLineSegment(sketch, "E1019", {"start": v(91.37, 73.44) * mm, "end": v(91.63, 73.04) * mm});
            skLineSegment(sketch, "E1020", {"start": v(91.63, 73.04) * mm, "end": v(91.73, 72.67) * mm});
            skLineSegment(sketch, "E1021", {"start": v(91.73, 72.67) * mm, "end": v(91.73, 72.54) * mm});
            skLineSegment(sketch, "E1022", {"start": v(91.15, 72.84) * mm, "end": v(91.15, 72.93) * mm});
            skLineSegment(sketch, "E1023", {"start": v(91.15, 72.93) * mm, "end": v(90.99, 73.2) * mm});
            skLineSegment(sketch, "E1024", {"start": v(90.99, 73.2) * mm, "end": v(90.66, 73.34) * mm});
            skLineSegment(sketch, "E1025", {"start": v(90.66, 73.34) * mm, "end": v(90.55, 73.34) * mm});
            skLineSegment(sketch, "E1026", {"start": v(90.55, 73.34) * mm, "end": v(89.88, 73.34) * mm});
            skLineSegment(sketch, "E1027", {"start": v(89.88, 73.34) * mm, "end": v(89.88, 71.82) * mm});
            skLineSegment(sketch, "E1028", {"start": v(89.88, 71.82) * mm, "end": v(90.21, 71.82) * mm});
            skLineSegment(sketch, "E1029", {"start": v(90.21, 71.82) * mm, "end": v(90.21, 72.3) * mm});
            skLineSegment(sketch, "E1030", {"start": v(90.21, 72.3) * mm, "end": v(90.48, 72.3) * mm});
            skLineSegment(sketch, "E1031", {"start": v(90.48, 72.3) * mm, "end": v(90.8, 71.82) * mm});
            skLineSegment(sketch, "E1032", {"start": v(90.8, 71.82) * mm, "end": v(91.2, 71.82) * mm});
            skLineSegment(sketch, "E1033", {"start": v(91.2, 71.82) * mm, "end": v(90.82, 72.36) * mm});
            skLineSegment(sketch, "E1034", {"start": v(90.82, 72.36) * mm, "end": v(90.87, 72.38) * mm});
            skLineSegment(sketch, "E1035", {"start": v(90.87, 72.38) * mm, "end": v(91.15, 72.72) * mm});
            skLineSegment(sketch, "E1036", {"start": v(91.15, 72.72) * mm, "end": v(91.15, 72.84) * mm});
            skLineSegment(sketch, "E1037", {"start": v(90.8, 72.82) * mm, "end": v(90.8, 72.76) * mm});
            skLineSegment(sketch, "E1038", {"start": v(90.8, 72.76) * mm, "end": v(90.61, 72.6) * mm});
            skLineSegment(sketch, "E1039", {"start": v(90.61, 72.6) * mm, "end": v(90.55, 72.6) * mm});
            skLineSegment(sketch, "E1040", {"start": v(90.55, 72.6) * mm, "end": v(90.21, 72.6) * mm});
            skLineSegment(sketch, "E1041", {"start": v(90.21, 72.6) * mm, "end": v(90.21, 73.04) * mm});
            skLineSegment(sketch, "E1042", {"start": v(90.21, 73.04) * mm, "end": v(90.54, 73.04) * mm});
            skLineSegment(sketch, "E1043", {"start": v(90.54, 73.04) * mm, "end": v(90.6, 73.04) * mm});
            skLineSegment(sketch, "E1044", {"start": v(90.6, 73.04) * mm, "end": v(90.8, 72.87) * mm});
            skLineSegment(sketch, "E1045", {"start": v(90.8, 72.87) * mm, "end": v(90.8, 72.82) * mm});
            skLineSegment(sketch, "E1046", {"start": v(62.65, 51.28) * mm, "end": v(62.65, 51.41) * mm});
            skLineSegment(sketch, "E1047", {"start": v(62.65, 51.41) * mm, "end": v(62.54, 51.83) * mm});
            skLineSegment(sketch, "E1048", {"start": v(62.54, 51.83) * mm, "end": v(62.24, 52.28) * mm});
            skLineSegment(sketch, "E1049", {"start": v(62.24, 52.28) * mm, "end": v(61.78, 52.58) * mm});
            skLineSegment(sketch, "E1050", {"start": v(61.78, 52.58) * mm, "end": v(61.36, 52.7) * mm});
            skLineSegment(sketch, "E1051", {"start": v(61.36, 52.7) * mm, "end": v(61.23, 52.7) * mm});
            skLineSegment(sketch, "E1052", {"start": v(61.23, 52.7) * mm, "end": v(61.08, 52.7) * mm});
            skLineSegment(sketch, "E1053", {"start": v(61.08, 52.7) * mm, "end": v(60.66, 52.58) * mm});
            skLineSegment(sketch, "E1054", {"start": v(60.66, 52.58) * mm, "end": v(60.21, 52.27) * mm});
            skLineSegment(sketch, "E1055", {"start": v(60.21, 52.27) * mm, "end": v(59.9, 51.82) * mm});
            skLineSegment(sketch, "E1056", {"start": v(59.9, 51.82) * mm, "end": v(59.8, 51.4) * mm});
            skLineSegment(sketch, "E1057", {"start": v(59.8, 51.4) * mm, "end": v(59.8, 51.27) * mm});
            skLineSegment(sketch, "E1058", {"start": v(59.8, 51.27) * mm, "end": v(59.8, 51.13) * mm});
            skLineSegment(sketch, "E1059", {"start": v(59.8, 51.13) * mm, "end": v(59.9, 50.72) * mm});
            skLineSegment(sketch, "E1060", {"start": v(59.9, 50.72) * mm, "end": v(60.2, 50.27) * mm});
            skLineSegment(sketch, "E1061", {"start": v(60.2, 50.27) * mm, "end": v(60.66, 49.96) * mm});
            skLineSegment(sketch, "E1062", {"start": v(60.66, 49.96) * mm, "end": v(61.08, 49.85) * mm});
            skLineSegment(sketch, "E1063", {"start": v(61.08, 49.85) * mm, "end": v(61.22, 49.85) * mm});
            skLineSegment(sketch, "E1064", {"start": v(61.22, 49.85) * mm, "end": v(61.36, 49.85) * mm});
            skLineSegment(sketch, "E1065", {"start": v(61.36, 49.85) * mm, "end": v(61.78, 49.96) * mm});
            skLineSegment(sketch, "E1066", {"start": v(61.78, 49.96) * mm, "end": v(62.23, 50.27) * mm});
            skLineSegment(sketch, "E1067", {"start": v(62.23, 50.27) * mm, "end": v(62.54, 50.72) * mm});
            skLineSegment(sketch, "E1068", {"start": v(62.54, 50.72) * mm, "end": v(62.65, 51.14) * mm});
            skLineSegment(sketch, "E1069", {"start": v(62.65, 51.14) * mm, "end": v(62.65, 51.28) * mm});
            skLineSegment(sketch, "E1070", {"start": v(62.48, 51.28) * mm, "end": v(62.48, 51.15) * mm});
            skLineSegment(sketch, "E1071", {"start": v(62.48, 51.15) * mm, "end": v(62.38, 50.78) * mm});
            skLineSegment(sketch, "E1072", {"start": v(62.38, 50.78) * mm, "end": v(62.12, 50.38) * mm});
            skLineSegment(sketch, "E1073", {"start": v(62.12, 50.38) * mm, "end": v(61.72, 50.1) * mm});
            skLineSegment(sketch, "E1074", {"start": v(61.72, 50.1) * mm, "end": v(61.34, 50) * mm});
            skLineSegment(sketch, "E1075", {"start": v(61.34, 50) * mm, "end": v(61.22, 50) * mm});
            skLineSegment(sketch, "E1076", {"start": v(61.22, 50) * mm, "end": v(61.1, 50) * mm});
            skLineSegment(sketch, "E1077", {"start": v(61.1, 50) * mm, "end": v(60.72, 50.1) * mm});
            skLineSegment(sketch, "E1078", {"start": v(60.72, 50.1) * mm, "end": v(60.32, 50.37) * mm});
            skLineSegment(sketch, "E1079", {"start": v(60.32, 50.37) * mm, "end": v(60.06, 50.78) * mm});
            skLineSegment(sketch, "E1080", {"start": v(60.06, 50.78) * mm, "end": v(59.96, 51.15) * mm});
            skLineSegment(sketch, "E1081", {"start": v(59.96, 51.15) * mm, "end": v(59.96, 51.27) * mm});
            skLineSegment(sketch, "E1082", {"start": v(59.96, 51.27) * mm, "end": v(59.96, 51.4) * mm});
            skLineSegment(sketch, "E1083", {"start": v(59.96, 51.4) * mm, "end": v(60.06, 51.76) * mm});
            skLineSegment(sketch, "E1084", {"start": v(60.06, 51.76) * mm, "end": v(60.32, 52.17) * mm});
            skLineSegment(sketch, "E1085", {"start": v(60.32, 52.17) * mm, "end": v(60.72, 52.44) * mm});
            skLineSegment(sketch, "E1086", {"start": v(60.72, 52.44) * mm, "end": v(61.1, 52.54) * mm});
            skLineSegment(sketch, "E1087", {"start": v(61.1, 52.54) * mm, "end": v(61.23, 52.54) * mm});
            skLineSegment(sketch, "E1088", {"start": v(61.23, 52.54) * mm, "end": v(61.35, 52.54) * mm});
            skLineSegment(sketch, "E1089", {"start": v(61.35, 52.54) * mm, "end": v(61.72, 52.44) * mm});
            skLineSegment(sketch, "E1090", {"start": v(61.72, 52.44) * mm, "end": v(62.12, 52.17) * mm});
            skLineSegment(sketch, "E1091", {"start": v(62.12, 52.17) * mm, "end": v(62.38, 51.77) * mm});
            skLineSegment(sketch, "E1092", {"start": v(62.38, 51.77) * mm, "end": v(62.48, 51.4) * mm});
            skLineSegment(sketch, "E1093", {"start": v(62.48, 51.4) * mm, "end": v(62.48, 51.28) * mm});
            skLineSegment(sketch, "E1094", {"start": v(61.9, 51.57) * mm, "end": v(61.9, 51.66) * mm});
            skLineSegment(sketch, "E1095", {"start": v(61.9, 51.66) * mm, "end": v(61.74, 51.94) * mm});
            skLineSegment(sketch, "E1096", {"start": v(61.74, 51.94) * mm, "end": v(61.42, 52.07) * mm});
            skLineSegment(sketch, "E1097", {"start": v(61.42, 52.07) * mm, "end": v(61.3, 52.07) * mm});
            skLineSegment(sketch, "E1098", {"start": v(61.3, 52.07) * mm, "end": v(60.64, 52.07) * mm});
            skLineSegment(sketch, "E1099", {"start": v(60.64, 52.07) * mm, "end": v(60.64, 50.56) * mm});
            skLineSegment(sketch, "E1100", {"start": v(60.64, 50.56) * mm, "end": v(60.97, 50.56) * mm});
            skLineSegment(sketch, "E1101", {"start": v(60.97, 50.56) * mm, "end": v(60.97, 51.04) * mm});
            skLineSegment(sketch, "E1102", {"start": v(60.97, 51.04) * mm, "end": v(61.23, 51.04) * mm});
            skLineSegment(sketch, "E1103", {"start": v(61.23, 51.04) * mm, "end": v(61.56, 50.56) * mm});
            skLineSegment(sketch, "E1104", {"start": v(61.56, 50.56) * mm, "end": v(61.95, 50.56) * mm});
            skLineSegment(sketch, "E1105", {"start": v(61.95, 50.56) * mm, "end": v(61.58, 51.1) * mm});
            skLineSegment(sketch, "E1106", {"start": v(61.58, 51.1) * mm, "end": v(61.62, 51.12) * mm});
            skLineSegment(sketch, "E1107", {"start": v(61.62, 51.12) * mm, "end": v(61.9, 51.46) * mm});
            skLineSegment(sketch, "E1108", {"start": v(61.9, 51.46) * mm, "end": v(61.9, 51.57) * mm});
            skLineSegment(sketch, "E1109", {"start": v(61.56, 51.55) * mm, "end": v(61.56, 51.5) * mm});
            skLineSegment(sketch, "E1110", {"start": v(61.56, 51.5) * mm, "end": v(61.37, 51.33) * mm});
            skLineSegment(sketch, "E1111", {"start": v(61.37, 51.33) * mm, "end": v(61.3, 51.33) * mm});
            skLineSegment(sketch, "E1112", {"start": v(61.3, 51.33) * mm, "end": v(60.97, 51.33) * mm});
            skLineSegment(sketch, "E1113", {"start": v(60.97, 51.33) * mm, "end": v(60.97, 51.78) * mm});
            skLineSegment(sketch, "E1114", {"start": v(60.97, 51.78) * mm, "end": v(61.3, 51.78) * mm});
            skLineSegment(sketch, "E1115", {"start": v(61.3, 51.78) * mm, "end": v(61.36, 51.78) * mm});
            skLineSegment(sketch, "E1116", {"start": v(61.36, 51.78) * mm, "end": v(61.56, 51.6) * mm});
            skLineSegment(sketch, "E1117", {"start": v(61.56, 51.6) * mm, "end": v(61.56, 51.55) * mm});
            skLineSegment(sketch, "E1118", {"start": v(-29.92, 96.85) * mm, "end": v(-29.92, 95.42) * mm});
            skLineSegment(sketch, "E1119", {"start": v(-29.92, 95.42) * mm, "end": v(-30.18, 95.42) * mm});
            skLineSegment(sketch, "E1120", {"start": v(-30.18, 95.42) * mm, "end": v(-30.18, 96.85) * mm});
            skLineSegment(sketch, "E1121", {"start": v(-30.18, 96.85) * mm, "end": v(-30.8, 96.85) * mm});
            skLineSegment(sketch, "E1122", {"start": v(-30.8, 96.85) * mm, "end": v(-30.8, 97.06) * mm});
            skLineSegment(sketch, "E1123", {"start": v(-30.8, 97.06) * mm, "end": v(-29.31, 97.06) * mm});
            skLineSegment(sketch, "E1124", {"start": v(-29.31, 97.06) * mm, "end": v(-29.31, 96.85) * mm});
            skLineSegment(sketch, "E1125", {"start": v(-29.31, 96.85) * mm, "end": v(-29.92, 96.85) * mm});
            skLineSegment(sketch, "E1126", {"start": v(-27.42, 95.42) * mm, "end": v(-27.42, 96.58) * mm});
            skLineSegment(sketch, "E1127", {"start": v(-27.42, 96.58) * mm, "end": v(-28.07, 95.6) * mm});
            skLineSegment(sketch, "E1128", {"start": v(-28.07, 95.6) * mm, "end": v(-28.72, 96.58) * mm});
            skLineSegment(sketch, "E1129", {"start": v(-28.72, 96.58) * mm, "end": v(-28.72, 95.42) * mm});
            skLineSegment(sketch, "E1130", {"start": v(-28.72, 95.42) * mm, "end": v(-29, 95.42) * mm});
            skLineSegment(sketch, "E1131", {"start": v(-29, 95.42) * mm, "end": v(-29, 97.06) * mm});
            skLineSegment(sketch, "E1132", {"start": v(-29, 97.06) * mm, "end": v(-28.72, 97.06) * mm});
            skLineSegment(sketch, "E1133", {"start": v(-28.72, 97.06) * mm, "end": v(-28.07, 96.05) * mm});
            skLineSegment(sketch, "E1134", {"start": v(-28.07, 96.05) * mm, "end": v(-27.42, 97.06) * mm});
            skLineSegment(sketch, "E1135", {"start": v(-27.42, 97.06) * mm, "end": v(-27.16, 97.06) * mm});
            skLineSegment(sketch, "E1136", {"start": v(-27.16, 97.06) * mm, "end": v(-27.16, 95.42) * mm});
            skLineSegment(sketch, "E1137", {"start": v(-27.16, 95.42) * mm, "end": v(-27.42, 95.42) * mm});
            skLineSegment(sketch, "E1138", {"start": v(8.48, 149.61) * mm, "end": v(8.42, 149.6) * mm});
            skLineSegment(sketch, "E1139", {"start": v(8.42, 149.6) * mm, "end": v(8.17, 149.45) * mm});
            skLineSegment(sketch, "E1140", {"start": v(8.17, 149.45) * mm, "end": v(8.09, 149.28) * mm});
            skLineSegment(sketch, "E1141", {"start": v(8.09, 149.28) * mm, "end": v(8.1, 149.24) * mm});
            skLineSegment(sketch, "E1142", {"start": v(8.1, 149.24) * mm, "end": v(8.13, 149.21) * mm});
            skLineSegment(sketch, "E1143", {"start": v(8.13, 149.21) * mm, "end": v(8.37, 149.16) * mm});
            skLineSegment(sketch, "E1144", {"start": v(8.37, 149.16) * mm, "end": v(8.8, 149.28) * mm});
            skLineSegment(sketch, "E1145", {"start": v(8.8, 149.28) * mm, "end": v(8.91, 149.33) * mm});
            skLineSegment(sketch, "E1146", {"start": v(8.91, 149.33) * mm, "end": v(9.03, 149.39) * mm});
            skLineSegment(sketch, "E1147", {"start": v(9.03, 149.39) * mm, "end": v(9.4, 149.63) * mm});
            skLineSegment(sketch, "E1148", {"start": v(9.4, 149.63) * mm, "end": v(9.38, 149.76) * mm});
            skLineSegment(sketch, "E1149", {"start": v(9.38, 149.76) * mm, "end": v(9.37, 149.76) * mm});
            skLineSegment(sketch, "E1150", {"start": v(9.37, 149.76) * mm, "end": v(9.02, 149.72) * mm});
            skLineSegment(sketch, "E1151", {"start": v(9.02, 149.72) * mm, "end": v(8.54, 149.64) * mm});
            skLineSegment(sketch, "E1152", {"start": v(8.54, 149.64) * mm, "end": v(8.48, 149.61) * mm});
            skLineSegment(sketch, "E1153", {"start": v(-14.67, 137.43) * mm, "end": v(-15, 137.37) * mm});
            skLineSegment(sketch, "E1154", {"start": v(-15, 137.37) * mm, "end": v(-16.1, 137.19) * mm});
            skLineSegment(sketch, "E1155", {"start": v(-16.1, 137.19) * mm, "end": v(-16.62, 137.05) * mm});
            skLineSegment(sketch, "E1156", {"start": v(-16.62, 137.05) * mm, "end": v(-16.65, 137.02) * mm});
            skLineSegment(sketch, "E1157", {"start": v(-16.65, 137.02) * mm, "end": v(-16.84, 136.86) * mm});
            skLineSegment(sketch, "E1158", {"start": v(-16.84, 136.86) * mm, "end": v(-17.31, 136.3) * mm});
            skLineSegment(sketch, "E1159", {"start": v(-17.31, 136.3) * mm, "end": v(-17.71, 135.62) * mm});
            skLineSegment(sketch, "E1160", {"start": v(-17.71, 135.62) * mm, "end": v(-17.88, 134.98) * mm});
            skLineSegment(sketch, "E1161", {"start": v(-17.88, 134.98) * mm, "end": v(-17.88, 134.39) * mm});
            skLineSegment(sketch, "E1162", {"start": v(-17.88, 134.39) * mm, "end": v(-17.74, 133.87) * mm});
            skLineSegment(sketch, "E1163", {"start": v(-17.74, 133.87) * mm, "end": v(-17.52, 133.43) * mm});
            skLineSegment(sketch, "E1164", {"start": v(-17.52, 133.43) * mm, "end": v(-17.24, 133.08) * mm});
            skLineSegment(sketch, "E1165", {"start": v(-17.24, 133.08) * mm, "end": v(-17.04, 132.9) * mm});
            skLineSegment(sketch, "E1166", {"start": v(-17.04, 132.9) * mm, "end": v(-16.97, 132.85) * mm});
            skLineSegment(sketch, "E1167", {"start": v(-16.97, 132.85) * mm, "end": v(-16.94, 132.83) * mm});
            skLineSegment(sketch, "E1168", {"start": v(-16.94, 132.83) * mm, "end": v(-16.83, 132.78) * mm});
            skLineSegment(sketch, "E1169", {"start": v(-16.83, 132.78) * mm, "end": v(-16.74, 132.8) * mm});
            skLineSegment(sketch, "E1170", {"start": v(-16.74, 132.8) * mm, "end": v(-16.66, 132.93) * mm});
            skLineSegment(sketch, "E1171", {"start": v(-16.66, 132.93) * mm, "end": v(-16.55, 133.17) * mm});
            skLineSegment(sketch, "E1172", {"start": v(-16.55, 133.17) * mm, "end": v(-16.36, 133.54) * mm});
            skLineSegment(sketch, "E1173", {"start": v(-16.36, 133.54) * mm, "end": v(-16.05, 134.07) * mm});
            skLineSegment(sketch, "E1174", {"start": v(-16.05, 134.07) * mm, "end": v(-15.58, 134.77) * mm});
            skLineSegment(sketch, "E1175", {"start": v(-15.58, 134.77) * mm, "end": v(-15.08, 135.44) * mm});
            skLineSegment(sketch, "E1176", {"start": v(-15.08, 135.44) * mm, "end": v(-14.9, 135.66) * mm});
            skLineSegment(sketch, "E1177", {"start": v(-14.9, 135.66) * mm, "end": v(-14.76, 135.84) * mm});
            skLineSegment(sketch, "E1178", {"start": v(-14.76, 135.84) * mm, "end": v(-14.24, 136.34) * mm});
            skLineSegment(sketch, "E1179", {"start": v(-14.24, 136.34) * mm, "end": v(-13.47, 136.98) * mm});
            skLineSegment(sketch, "E1180", {"start": v(-13.47, 136.98) * mm, "end": v(-12.77, 137.49) * mm});
            skLineSegment(sketch, "E1181", {"start": v(-12.77, 137.49) * mm, "end": v(-12.43, 137.73) * mm});
            skLineSegment(sketch, "E1182", {"start": v(-12.43, 137.73) * mm, "end": v(-12.36, 137.8) * mm});
            skLineSegment(sketch, "E1183", {"start": v(-12.36, 137.8) * mm, "end": v(-12.49, 137.83) * mm});
            skLineSegment(sketch, "E1184", {"start": v(-12.49, 137.83) * mm, "end": v(-13.03, 137.74) * mm});
            skLineSegment(sketch, "E1185", {"start": v(-13.03, 137.74) * mm, "end": v(-13.82, 137.59) * mm});
            skLineSegment(sketch, "E1186", {"start": v(-13.82, 137.59) * mm, "end": v(-14.46, 137.46) * mm});
            skLineSegment(sketch, "E1187", {"start": v(-14.46, 137.46) * mm, "end": v(-14.67, 137.43) * mm});
            skLineSegment(sketch, "E1188", {"start": v(4.13, 162.5) * mm, "end": v(4.16, 162.42) * mm});
            skLineSegment(sketch, "E1189", {"start": v(4.16, 162.42) * mm, "end": v(4.26, 162.14) * mm});
            skLineSegment(sketch, "E1190", {"start": v(4.26, 162.14) * mm, "end": v(4.3, 162.04) * mm});
            skLineSegment(sketch, "E1191", {"start": v(4.3, 162.04) * mm, "end": v(4.37, 162.02) * mm});
            skLineSegment(sketch, "E1192", {"start": v(4.37, 162.02) * mm, "end": v(4.53, 162.03) * mm});
            skLineSegment(sketch, "E1193", {"start": v(4.53, 162.03) * mm, "end": v(4.7, 162.13) * mm});
            skLineSegment(sketch, "E1194", {"start": v(4.7, 162.13) * mm, "end": v(4.8, 162.33) * mm});
            skLineSegment(sketch, "E1195", {"start": v(4.8, 162.33) * mm, "end": v(4.82, 162.4) * mm});
            skLineSegment(sketch, "E1196", {"start": v(4.82, 162.4) * mm, "end": v(4.83, 162.46) * mm});
            skLineSegment(sketch, "E1197", {"start": v(4.83, 162.46) * mm, "end": v(4.73, 162.68) * mm});
            skLineSegment(sketch, "E1198", {"start": v(4.73, 162.68) * mm, "end": v(4.46, 162.77) * mm});
            skLineSegment(sketch, "E1199", {"start": v(4.46, 162.77) * mm, "end": v(4.2, 162.7) * mm});
            skLineSegment(sketch, "E1200", {"start": v(4.2, 162.7) * mm, "end": v(4.12, 162.54) * mm});
            skLineSegment(sketch, "E1201", {"start": v(4.12, 162.54) * mm, "end": v(4.13, 162.5) * mm});
            skLineSegment(sketch, "E1202", {"start": v(5.21, 160.85) * mm, "end": v(5.22, 160.9) * mm});
            skLineSegment(sketch, "E1203", {"start": v(5.22, 160.9) * mm, "end": v(5.11, 161.1) * mm});
            skLineSegment(sketch, "E1204", {"start": v(5.11, 161.1) * mm, "end": v(4.88, 161.14) * mm});
            skLineSegment(sketch, "E1205", {"start": v(4.88, 161.14) * mm, "end": v(4.66, 161.05) * mm});
            skLineSegment(sketch, "E1206", {"start": v(4.66, 161.05) * mm, "end": v(4.6, 160.89) * mm});
            skLineSegment(sketch, "E1207", {"start": v(4.6, 160.89) * mm, "end": v(4.63, 160.85) * mm});
            skLineSegment(sketch, "E1208", {"start": v(4.63, 160.85) * mm, "end": v(4.66, 160.78) * mm});
            skLineSegment(sketch, "E1209", {"start": v(4.66, 160.78) * mm, "end": v(4.71, 160.46) * mm});
            skLineSegment(sketch, "E1210", {"start": v(4.71, 160.46) * mm, "end": v(4.7, 160.28) * mm});
            skLineSegment(sketch, "E1211", {"start": v(4.7, 160.28) * mm, "end": v(4.95, 160.38) * mm});
            skLineSegment(sketch, "E1212", {"start": v(4.95, 160.38) * mm, "end": v(5.2, 160.73) * mm});
            skLineSegment(sketch, "E1213", {"start": v(5.2, 160.73) * mm, "end": v(5.21, 160.85) * mm});
            skLineSegment(sketch, "E1214", {"start": v(11.64, 146.86) * mm, "end": v(11.73, 146.92) * mm});
            skLineSegment(sketch, "E1215", {"start": v(11.73, 146.92) * mm, "end": v(12.08, 147.1) * mm});
            skLineSegment(sketch, "E1216", {"start": v(12.08, 147.1) * mm, "end": v(12.34, 147.25) * mm});
            skLineSegment(sketch, "E1217", {"start": v(12.34, 147.25) * mm, "end": v(12.4, 147.3) * mm});
            skLineSegment(sketch, "E1218", {"start": v(12.4, 147.3) * mm, "end": v(12.44, 147.31) * mm});
            skLineSegment(sketch, "E1219", {"start": v(12.44, 147.31) * mm, "end": v(12.63, 147.52) * mm});
            skLineSegment(sketch, "E1220", {"start": v(12.63, 147.52) * mm, "end": v(12.72, 147.75) * mm});
            skLineSegment(sketch, "E1221", {"start": v(12.72, 147.75) * mm, "end": v(12.72, 147.8) * mm});
            skLineSegment(sketch, "E1222", {"start": v(12.72, 147.8) * mm, "end": v(12.71, 147.84) * mm});
            skLineSegment(sketch, "E1223", {"start": v(12.71, 147.84) * mm, "end": v(12.78, 147.97) * mm});
            skLineSegment(sketch, "E1224", {"start": v(12.78, 147.97) * mm, "end": v(12.98, 148.07) * mm});
            skLineSegment(sketch, "E1225", {"start": v(12.98, 148.07) * mm, "end": v(13.04, 148.1) * mm});
            skLineSegment(sketch, "E1226", {"start": v(13.04, 148.1) * mm, "end": v(13.1, 148.12) * mm});
            skLineSegment(sketch, "E1227", {"start": v(13.1, 148.12) * mm, "end": v(13.28, 148.26) * mm});
            skLineSegment(sketch, "E1228", {"start": v(13.28, 148.26) * mm, "end": v(13.38, 148.43) * mm});
            skLineSegment(sketch, "E1229", {"start": v(13.38, 148.43) * mm, "end": v(13.4, 148.48) * mm});
            skLineSegment(sketch, "E1230", {"start": v(13.4, 148.48) * mm, "end": v(13.41, 148.52) * mm});
            skLineSegment(sketch, "E1231", {"start": v(13.41, 148.52) * mm, "end": v(13.52, 148.8) * mm});
            skLineSegment(sketch, "E1232", {"start": v(13.52, 148.8) * mm, "end": v(13.59, 148.88) * mm});
            skLineSegment(sketch, "E1233", {"start": v(13.59, 148.88) * mm, "end": v(13.8, 148.98) * mm});
            skLineSegment(sketch, "E1234", {"start": v(13.8, 148.98) * mm, "end": v(13.87, 149) * mm});
            skLineSegment(sketch, "E1235", {"start": v(13.87, 149) * mm, "end": v(13.94, 149) * mm});
            skLineSegment(sketch, "E1236", {"start": v(13.94, 149) * mm, "end": v(14.3, 149.12) * mm});
            skLineSegment(sketch, "E1237", {"start": v(14.3, 149.12) * mm, "end": v(14.5, 149.4) * mm});
            skLineSegment(sketch, "E1238", {"start": v(14.5, 149.4) * mm, "end": v(14.5, 149.5) * mm});
            skLineSegment(sketch, "E1239", {"start": v(14.5, 149.5) * mm, "end": v(14.5, 149.58) * mm});
            skLineSegment(sketch, "E1240", {"start": v(14.5, 149.58) * mm, "end": v(14.44, 149.85) * mm});
            skLineSegment(sketch, "E1241", {"start": v(14.44, 149.85) * mm, "end": v(14.38, 150.06) * mm});
            skLineSegment(sketch, "E1242", {"start": v(14.38, 150.06) * mm, "end": v(14.37, 150.08) * mm});
            skLineSegment(sketch, "E1243", {"start": v(14.37, 150.08) * mm, "end": v(14.35, 150.08) * mm});
            skLineSegment(sketch, "E1244", {"start": v(14.35, 150.08) * mm, "end": v(14.33, 150.06) * mm});
            skLineSegment(sketch, "E1245", {"start": v(14.33, 150.06) * mm, "end": v(14.15, 149.93) * mm});
            skLineSegment(sketch, "E1246", {"start": v(14.15, 149.93) * mm, "end": v(13.84, 149.9) * mm});
            skLineSegment(sketch, "E1247", {"start": v(13.84, 149.9) * mm, "end": v(13.76, 149.93) * mm});
            skLineSegment(sketch, "E1248", {"start": v(13.76, 149.93) * mm, "end": v(13.64, 149.97) * mm});
            skLineSegment(sketch, "E1249", {"start": v(13.64, 149.97) * mm, "end": v(13.2, 150.17) * mm});
            skLineSegment(sketch, "E1250", {"start": v(13.2, 150.17) * mm, "end": v(12.9, 150.31) * mm});
            skLineSegment(sketch, "E1251", {"start": v(12.9, 150.31) * mm, "end": v(12.85, 150.33) * mm});
            skLineSegment(sketch, "E1252", {"start": v(12.85, 150.33) * mm, "end": v(12.78, 150.35) * mm});
            skLineSegment(sketch, "E1253", {"start": v(12.78, 150.35) * mm, "end": v(12.51, 150.38) * mm});
            skLineSegment(sketch, "E1254", {"start": v(12.51, 150.38) * mm, "end": v(12.43, 150.2) * mm});
            skLineSegment(sketch, "E1255", {"start": v(12.43, 150.2) * mm, "end": v(12.45, 150.17) * mm});
            skLineSegment(sketch, "E1256", {"start": v(12.45, 150.17) * mm, "end": v(12.48, 150.1) * mm});
            skLineSegment(sketch, "E1257", {"start": v(12.48, 150.1) * mm, "end": v(12.55, 149.88) * mm});
            skLineSegment(sketch, "E1258", {"start": v(12.55, 149.88) * mm, "end": v(12.5, 149.69) * mm});
            skLineSegment(sketch, "E1259", {"start": v(12.5, 149.69) * mm, "end": v(12.46, 149.65) * mm});
            skLineSegment(sketch, "E1260", {"start": v(12.46, 149.65) * mm, "end": v(12.43, 149.64) * mm});
            skLineSegment(sketch, "E1261", {"start": v(12.43, 149.64) * mm, "end": v(12.22, 149.5) * mm});
            skLineSegment(sketch, "E1262", {"start": v(12.22, 149.5) * mm, "end": v(12.2, 149.5) * mm});
            skLineSegment(sketch, "E1263", {"start": v(12.2, 149.5) * mm, "end": v(12.13, 149.46) * mm});
            skLineSegment(sketch, "E1264", {"start": v(12.13, 149.46) * mm, "end": v(11.9, 149.26) * mm});
            skLineSegment(sketch, "E1265", {"start": v(11.9, 149.26) * mm, "end": v(11.86, 149.07) * mm});
            skLineSegment(sketch, "E1266", {"start": v(11.86, 149.07) * mm, "end": v(11.86, 149.04) * mm});
            skLineSegment(sketch, "E1267", {"start": v(11.86, 149.04) * mm, "end": v(11.87, 149.02) * mm});
            skLineSegment(sketch, "E1268", {"start": v(11.87, 149.02) * mm, "end": v(11.87, 148.83) * mm});
            skLineSegment(sketch, "E1269", {"start": v(11.87, 148.83) * mm, "end": v(11.8, 148.65) * mm});
            skLineSegment(sketch, "E1270", {"start": v(11.8, 148.65) * mm, "end": v(11.75, 148.62) * mm});
            skLineSegment(sketch, "E1271", {"start": v(11.75, 148.62) * mm, "end": v(11.7, 148.58) * mm});
            skLineSegment(sketch, "E1272", {"start": v(11.7, 148.58) * mm, "end": v(11.42, 148.19) * mm});
            skLineSegment(sketch, "E1273", {"start": v(11.42, 148.19) * mm, "end": v(11.42, 148.14) * mm});
            skLineSegment(sketch, "E1274", {"start": v(11.42, 148.14) * mm, "end": v(11.43, 148.1) * mm});
            skLineSegment(sketch, "E1275", {"start": v(11.43, 148.1) * mm, "end": v(11.22, 147.76) * mm});
            skLineSegment(sketch, "E1276", {"start": v(11.22, 147.76) * mm, "end": v(11.18, 147.73) * mm});
            skLineSegment(sketch, "E1277", {"start": v(11.18, 147.73) * mm, "end": v(11.13, 147.7) * mm});
            skLineSegment(sketch, "E1278", {"start": v(11.13, 147.7) * mm, "end": v(10.8, 147.58) * mm});
            skLineSegment(sketch, "E1279", {"start": v(10.8, 147.58) * mm, "end": v(10.2, 147.52) * mm});
            skLineSegment(sketch, "E1280", {"start": v(10.2, 147.52) * mm, "end": v(10.03, 147.5) * mm});
            skLineSegment(sketch, "E1281", {"start": v(10.03, 147.5) * mm, "end": v(9.85, 147.48) * mm});
            skLineSegment(sketch, "E1282", {"start": v(9.85, 147.48) * mm, "end": v(9.27, 147.52) * mm});
            skLineSegment(sketch, "E1283", {"start": v(9.27, 147.52) * mm, "end": v(8.9, 147.64) * mm});
            skLineSegment(sketch, "E1284", {"start": v(8.9, 147.64) * mm, "end": v(8.84, 147.66) * mm});
            skLineSegment(sketch, "E1285", {"start": v(8.84, 147.66) * mm, "end": v(8.77, 147.68) * mm});
            skLineSegment(sketch, "E1286", {"start": v(8.77, 147.68) * mm, "end": v(8.5, 147.64) * mm});
            skLineSegment(sketch, "E1287", {"start": v(8.5, 147.64) * mm, "end": v(8.37, 147.47) * mm});
            skLineSegment(sketch, "E1288", {"start": v(8.37, 147.47) * mm, "end": v(8.37, 147.41) * mm});
            skLineSegment(sketch, "E1289", {"start": v(8.37, 147.41) * mm, "end": v(8.36, 147.37) * mm});
            skLineSegment(sketch, "E1290", {"start": v(8.36, 147.37) * mm, "end": v(8.38, 147.21) * mm});
            skLineSegment(sketch, "E1291", {"start": v(8.38, 147.21) * mm, "end": v(8.52, 147.14) * mm});
            skLineSegment(sketch, "E1292", {"start": v(8.52, 147.14) * mm, "end": v(8.57, 147.13) * mm});
            skLineSegment(sketch, "E1293", {"start": v(8.57, 147.13) * mm, "end": v(8.61, 147.13) * mm});
            skLineSegment(sketch, "E1294", {"start": v(8.61, 147.13) * mm, "end": v(8.73, 147.03) * mm});
            skLineSegment(sketch, "E1295", {"start": v(8.73, 147.03) * mm, "end": v(8.59, 146.91) * mm});
            skLineSegment(sketch, "E1296", {"start": v(8.59, 146.91) * mm, "end": v(8.54, 146.9) * mm});
            skLineSegment(sketch, "E1297", {"start": v(8.54, 146.9) * mm, "end": v(8.52, 146.9) * mm});
            skLineSegment(sketch, "E1298", {"start": v(8.52, 146.9) * mm, "end": v(8.47, 146.82) * mm});
            skLineSegment(sketch, "E1299", {"start": v(8.47, 146.82) * mm, "end": v(8.6, 146.7) * mm});
            skLineSegment(sketch, "E1300", {"start": v(8.6, 146.7) * mm, "end": v(8.82, 146.58) * mm});
            skLineSegment(sketch, "E1301", {"start": v(8.82, 146.58) * mm, "end": v(8.98, 146.51) * mm});
            skLineSegment(sketch, "E1302", {"start": v(8.98, 146.51) * mm, "end": v(9.04, 146.5) * mm});
            skLineSegment(sketch, "E1303", {"start": v(9.04, 146.5) * mm, "end": v(9.05, 146.5) * mm});
            skLineSegment(sketch, "E1304", {"start": v(9.05, 146.5) * mm, "end": v(9.12, 146.47) * mm});
            skLineSegment(sketch, "E1305", {"start": v(9.12, 146.47) * mm, "end": v(9.15, 146.47) * mm});
            skLineSegment(sketch, "E1306", {"start": v(9.15, 146.47) * mm, "end": v(9.06, 146.28) * mm});
            skLineSegment(sketch, "E1307", {"start": v(9.06, 146.28) * mm, "end": v(8.78, 145.72) * mm});
            skLineSegment(sketch, "E1308", {"start": v(8.78, 145.72) * mm, "end": v(8.15, 144.44) * mm});
            skLineSegment(sketch, "E1309", {"start": v(8.15, 144.44) * mm, "end": v(7.29, 142.72) * mm});
            skLineSegment(sketch, "E1310", {"start": v(7.29, 142.72) * mm, "end": v(6.24, 140.64) * mm});
            skLineSegment(sketch, "E1311", {"start": v(6.24, 140.64) * mm, "end": v(5.05, 138.26) * mm});
            skLineSegment(sketch, "E1312", {"start": v(5.05, 138.26) * mm, "end": v(3.75, 135.68) * mm});
            skLineSegment(sketch, "E1313", {"start": v(3.75, 135.68) * mm, "end": v(2.38, 132.97) * mm});
            skLineSegment(sketch, "E1314", {"start": v(2.38, 132.97) * mm, "end": v(0.99, 130.2) * mm});
            skLineSegment(sketch, "E1315", {"start": v(0.99, 130.2) * mm, "end": v(-0.4, 127.46) * mm});
            skLineSegment(sketch, "E1316", {"start": v(-0.4, 127.46) * mm, "end": v(-1.72, 124.83) * mm});
            skLineSegment(sketch, "E1317", {"start": v(-1.72, 124.83) * mm, "end": v(-2.96, 122.37) * mm});
            skLineSegment(sketch, "E1318", {"start": v(-2.96, 122.37) * mm, "end": v(-4.06, 120.18) * mm});
            skLineSegment(sketch, "E1319", {"start": v(-4.06, 120.18) * mm, "end": v(-5, 118.33) * mm});
            skLineSegment(sketch, "E1320", {"start": v(-5, 118.33) * mm, "end": v(-5.72, 116.89) * mm});
            skLineSegment(sketch, "E1321", {"start": v(-5.72, 116.89) * mm, "end": v(-6.2, 115.95) * mm});
            skLineSegment(sketch, "E1322", {"start": v(-6.2, 115.95) * mm, "end": v(-6.34, 115.65) * mm});
            skLineSegment(sketch, "E1323", {"start": v(-6.34, 115.65) * mm, "end": v(-6.37, 115.58) * mm});
            skLineSegment(sketch, "E1324", {"start": v(-6.37, 115.58) * mm, "end": v(-6.38, 115.56) * mm});
            skLineSegment(sketch, "E1325", {"start": v(-6.38, 115.56) * mm, "end": v(-6.31, 115.4) * mm});
            skLineSegment(sketch, "E1326", {"start": v(-6.31, 115.4) * mm, "end": v(-6.3, 115.4) * mm});
            skLineSegment(sketch, "E1327", {"start": v(-6.3, 115.4) * mm, "end": v(-6.28, 115.38) * mm});
            skLineSegment(sketch, "E1328", {"start": v(-6.28, 115.38) * mm, "end": v(-6.08, 115.4) * mm});
            skLineSegment(sketch, "E1329", {"start": v(-6.08, 115.4) * mm, "end": v(-6.07, 115.42) * mm});
            skLineSegment(sketch, "E1330", {"start": v(-6.07, 115.42) * mm, "end": v(-6.04, 115.47) * mm});
            skLineSegment(sketch, "E1331", {"start": v(-6.04, 115.47) * mm, "end": v(-5.86, 115.8) * mm});
            skLineSegment(sketch, "E1332", {"start": v(-5.86, 115.8) * mm, "end": v(-5.32, 116.81) * mm});
            skLineSegment(sketch, "E1333", {"start": v(-5.32, 116.81) * mm, "end": v(-4.49, 118.37) * mm});
            skLineSegment(sketch, "E1334", {"start": v(-4.49, 118.37) * mm, "end": v(-3.42, 120.37) * mm});
            skLineSegment(sketch, "E1335", {"start": v(-3.42, 120.37) * mm, "end": v(-2.16, 122.74) * mm});
            skLineSegment(sketch, "E1336", {"start": v(-2.16, 122.74) * mm, "end": v(-0.75, 125.37) * mm});
            skLineSegment(sketch, "E1337", {"start": v(-0.75, 125.37) * mm, "end": v(0.75, 128.18) * mm});
            skLineSegment(sketch, "E1338", {"start": v(0.75, 128.18) * mm, "end": v(2.3, 131.08) * mm});
            skLineSegment(sketch, "E1339", {"start": v(2.3, 131.08) * mm, "end": v(3.83, 133.98) * mm});
            skLineSegment(sketch, "E1340", {"start": v(3.83, 133.98) * mm, "end": v(5.33, 136.79) * mm});
            skLineSegment(sketch, "E1341", {"start": v(5.33, 136.79) * mm, "end": v(6.72, 139.41) * mm});
            skLineSegment(sketch, "E1342", {"start": v(6.72, 139.41) * mm, "end": v(7.97, 141.76) * mm});
            skLineSegment(sketch, "E1343", {"start": v(7.97, 141.76) * mm, "end": v(9.03, 143.75) * mm});
            skLineSegment(sketch, "E1344", {"start": v(9.03, 143.75) * mm, "end": v(9.84, 145.28) * mm});
            skLineSegment(sketch, "E1345", {"start": v(9.84, 145.28) * mm, "end": v(10.37, 146.26) * mm});
            skLineSegment(sketch, "E1346", {"start": v(10.37, 146.26) * mm, "end": v(10.55, 146.6) * mm});
            skLineSegment(sketch, "E1347", {"start": v(10.55, 146.6) * mm, "end": v(10.65, 146.62) * mm});
            skLineSegment(sketch, "E1348", {"start": v(10.65, 146.62) * mm, "end": v(11.17, 146.7) * mm});
            skLineSegment(sketch, "E1349", {"start": v(11.17, 146.7) * mm, "end": v(11.59, 146.83) * mm});
            skLineSegment(sketch, "E1350", {"start": v(11.59, 146.83) * mm, "end": v(11.64, 146.86) * mm});
            skLineSegment(sketch, "E1351", {"start": v(12.5, 151.39) * mm, "end": v(12.58, 151.39) * mm});
            skLineSegment(sketch, "E1352", {"start": v(12.58, 151.39) * mm, "end": v(12.82, 151.32) * mm});
            skLineSegment(sketch, "E1353", {"start": v(12.82, 151.32) * mm, "end": v(13, 151.25) * mm});
            skLineSegment(sketch, "E1354", {"start": v(13, 151.25) * mm, "end": v(13.24, 151.7) * mm});
            skLineSegment(sketch, "E1355", {"start": v(13.24, 151.7) * mm, "end": v(13.37, 151.71) * mm});
            skLineSegment(sketch, "E1356", {"start": v(13.37, 151.71) * mm, "end": v(13.73, 151.83) * mm});
            skLineSegment(sketch, "E1357", {"start": v(13.73, 151.83) * mm, "end": v(14.12, 152.11) * mm});
            skLineSegment(sketch, "E1358", {"start": v(14.12, 152.11) * mm, "end": v(14.37, 152.52) * mm});
            skLineSegment(sketch, "E1359", {"start": v(14.37, 152.52) * mm, "end": v(14.47, 152.88) * mm});
            skLineSegment(sketch, "E1360", {"start": v(14.47, 152.88) * mm, "end": v(14.47, 153) * mm});
            skLineSegment(sketch, "E1361", {"start": v(14.47, 153) * mm, "end": v(14.47, 153.13) * mm});
            skLineSegment(sketch, "E1362", {"start": v(14.47, 153.13) * mm, "end": v(14.36, 153.52) * mm});
            skLineSegment(sketch, "E1363", {"start": v(14.36, 153.52) * mm, "end": v(14.08, 153.94) * mm});
            skLineSegment(sketch, "E1364", {"start": v(14.08, 153.94) * mm, "end": v(13.66, 154.22) * mm});
            skLineSegment(sketch, "E1365", {"start": v(13.66, 154.22) * mm, "end": v(13.28, 154.32) * mm});
            skLineSegment(sketch, "E1366", {"start": v(13.28, 154.32) * mm, "end": v(13.15, 154.32) * mm});
            skLineSegment(sketch, "E1367", {"start": v(13.15, 154.32) * mm, "end": v(12.95, 154.32) * mm});
            skLineSegment(sketch, "E1368", {"start": v(12.95, 154.32) * mm, "end": v(12.42, 154.1) * mm});
            skLineSegment(sketch, "E1369", {"start": v(12.42, 154.1) * mm, "end": v(12.36, 154.05) * mm});
            skLineSegment(sketch, "E1370", {"start": v(12.36, 154.05) * mm, "end": v(12.4, 154.05) * mm});
            skLineSegment(sketch, "E1371", {"start": v(12.4, 154.05) * mm, "end": v(12.42, 154.05) * mm});
            skLineSegment(sketch, "E1372", {"start": v(12.42, 154.05) * mm, "end": v(12.46, 154.06) * mm});
            skLineSegment(sketch, "E1373", {"start": v(12.46, 154.06) * mm, "end": v(12.77, 154.1) * mm});
            skLineSegment(sketch, "E1374", {"start": v(12.77, 154.1) * mm, "end": v(12.8, 154.08) * mm});
            skLineSegment(sketch, "E1375", {"start": v(12.8, 154.08) * mm, "end": v(12.81, 154.05) * mm});
            skLineSegment(sketch, "E1376", {"start": v(12.81, 154.05) * mm, "end": v(12.83, 154.03) * mm});
            skLineSegment(sketch, "E1377", {"start": v(12.83, 154.03) * mm, "end": v(12.78, 153.89) * mm});
            skLineSegment(sketch, "E1378", {"start": v(12.78, 153.89) * mm, "end": v(12.66, 153.66) * mm});
            skLineSegment(sketch, "E1379", {"start": v(12.66, 153.66) * mm, "end": v(12.66, 153.6) * mm});
            skLineSegment(sketch, "E1380", {"start": v(12.66, 153.6) * mm, "end": v(12.65, 153.57) * mm});
            skLineSegment(sketch, "E1381", {"start": v(12.65, 153.57) * mm, "end": v(12.54, 153.37) * mm});
            skLineSegment(sketch, "E1382", {"start": v(12.54, 153.37) * mm, "end": v(12.52, 153.36) * mm});
            skLineSegment(sketch, "E1383", {"start": v(12.52, 153.36) * mm, "end": v(12.49, 153.35) * mm});
            skLineSegment(sketch, "E1384", {"start": v(12.49, 153.35) * mm, "end": v(12.22, 153.4) * mm});
            skLineSegment(sketch, "E1385", {"start": v(12.22, 153.4) * mm, "end": v(12.2, 153.42) * mm});
            skLineSegment(sketch, "E1386", {"start": v(12.2, 153.42) * mm, "end": v(12.19, 153.44) * mm});
            skLineSegment(sketch, "E1387", {"start": v(12.19, 153.44) * mm, "end": v(12.09, 153.62) * mm});
            skLineSegment(sketch, "E1388", {"start": v(12.09, 153.62) * mm, "end": v(12.09, 153.68) * mm});
            skLineSegment(sketch, "E1389", {"start": v(12.09, 153.68) * mm, "end": v(12.09, 153.69) * mm});
            skLineSegment(sketch, "E1390", {"start": v(12.09, 153.69) * mm, "end": v(12.03, 153.69) * mm});
            skLineSegment(sketch, "E1391", {"start": v(12.03, 153.69) * mm, "end": v(12.03, 153.68) * mm});
            skLineSegment(sketch, "E1392", {"start": v(12.03, 153.68) * mm, "end": v(12, 153.64) * mm});
            skLineSegment(sketch, "E1393", {"start": v(12, 153.64) * mm, "end": v(11.84, 153.16) * mm});
            skLineSegment(sketch, "E1394", {"start": v(11.84, 153.16) * mm, "end": v(11.84, 153) * mm});
            skLineSegment(sketch, "E1395", {"start": v(11.84, 153) * mm, "end": v(11.84, 152.84) * mm});
            skLineSegment(sketch, "E1396", {"start": v(11.84, 152.84) * mm, "end": v(12.01, 152.38) * mm});
            skLineSegment(sketch, "E1397", {"start": v(12.01, 152.38) * mm, "end": v(12.05, 152.33) * mm});
            skLineSegment(sketch, "E1398", {"start": v(12.05, 152.33) * mm, "end": v(12, 152.22) * mm});
            skLineSegment(sketch, "E1399", {"start": v(12, 152.22) * mm, "end": v(11.74, 151.63) * mm});
            skLineSegment(sketch, "E1400", {"start": v(11.74, 151.63) * mm, "end": v(11.55, 151.18) * mm});
            skLineSegment(sketch, "E1401", {"start": v(11.55, 151.18) * mm, "end": v(11.55, 151.15) * mm});
            skLineSegment(sketch, "E1402", {"start": v(11.55, 151.15) * mm, "end": v(11.54, 151.14) * mm});
            skLineSegment(sketch, "E1403", {"start": v(11.54, 151.14) * mm, "end": v(11.6, 151.1) * mm});
            skLineSegment(sketch, "E1404", {"start": v(11.6, 151.1) * mm, "end": v(11.82, 151.2) * mm});
            skLineSegment(sketch, "E1405", {"start": v(11.82, 151.2) * mm, "end": v(12.14, 151.32) * mm});
            skLineSegment(sketch, "E1406", {"start": v(12.14, 151.32) * mm, "end": v(12.4, 151.39) * mm});
            skLineSegment(sketch, "E1407", {"start": v(12.4, 151.39) * mm, "end": v(12.5, 151.39) * mm});
            skLineSegment(sketch, "E1408", {"start": v(24.4, 103.83) * mm, "end": v(24.33, 103.83) * mm});
            skLineSegment(sketch, "E1409", {"start": v(24.33, 103.83) * mm, "end": v(24.11, 103.7) * mm});
            skLineSegment(sketch, "E1410", {"start": v(24.11, 103.7) * mm, "end": v(24.02, 103.77) * mm});
            skLineSegment(sketch, "E1411", {"start": v(24.02, 103.77) * mm, "end": v(23.75, 103.88) * mm});
            skLineSegment(sketch, "E1412", {"start": v(23.75, 103.88) * mm, "end": v(23.36, 103.92) * mm});
            skLineSegment(sketch, "E1413", {"start": v(23.36, 103.92) * mm, "end": v(22.98, 103.83) * mm});
            skLineSegment(sketch, "E1414", {"start": v(22.98, 103.83) * mm, "end": v(22.87, 103.77) * mm});
            skLineSegment(sketch, "E1415", {"start": v(22.87, 103.77) * mm, "end": v(22.84, 103.74) * mm});
            skLineSegment(sketch, "E1416", {"start": v(22.84, 103.74) * mm, "end": v(22.67, 103.51) * mm});
            skLineSegment(sketch, "E1417", {"start": v(22.67, 103.51) * mm, "end": v(22.53, 103.17) * mm});
            skLineSegment(sketch, "E1418", {"start": v(22.53, 103.17) * mm, "end": v(22.51, 103.08) * mm});
            skLineSegment(sketch, "E1419", {"start": v(22.51, 103.08) * mm, "end": v(22.5, 102.98) * mm});
            skLineSegment(sketch, "E1420", {"start": v(22.5, 102.98) * mm, "end": v(22.42, 102.5) * mm});
            skLineSegment(sketch, "E1421", {"start": v(22.42, 102.5) * mm, "end": v(22.33, 102.17) * mm});
            skLineSegment(sketch, "E1422", {"start": v(22.33, 102.17) * mm, "end": v(22.3, 102.15) * mm});
            skLineSegment(sketch, "E1423", {"start": v(22.3, 102.15) * mm, "end": v(22.29, 102.14) * mm});
            skLineSegment(sketch, "E1424", {"start": v(22.29, 102.14) * mm, "end": v(22.09, 102.13) * mm});
            skLineSegment(sketch, "E1425", {"start": v(22.09, 102.13) * mm, "end": v(22.06, 102.14) * mm});
            skLineSegment(sketch, "E1426", {"start": v(22.06, 102.14) * mm, "end": v(21.97, 102.17) * mm});
            skLineSegment(sketch, "E1427", {"start": v(21.97, 102.17) * mm, "end": v(21.7, 102.27) * mm});
            skLineSegment(sketch, "E1428", {"start": v(21.7, 102.27) * mm, "end": v(21.46, 102.12) * mm});
            skLineSegment(sketch, "E1429", {"start": v(21.46, 102.12) * mm, "end": v(21.39, 102.06) * mm});
            skLineSegment(sketch, "E1430", {"start": v(21.39, 102.06) * mm, "end": v(21.3, 102) * mm});
            skLineSegment(sketch, "E1431", {"start": v(21.3, 102) * mm, "end": v(21, 101.87) * mm});
            skLineSegment(sketch, "E1432", {"start": v(21, 101.87) * mm, "end": v(20.42, 101.72) * mm});
            skLineSegment(sketch, "E1433", {"start": v(20.42, 101.72) * mm, "end": v(19.82, 101.72) * mm});
            skLineSegment(sketch, "E1434", {"start": v(19.82, 101.72) * mm, "end": v(19.43, 101.84) * mm});
            skLineSegment(sketch, "E1435", {"start": v(19.43, 101.84) * mm, "end": v(19.34, 101.93) * mm});
            skLineSegment(sketch, "E1436", {"start": v(19.34, 101.93) * mm, "end": v(19.34, 101.96) * mm});
            skLineSegment(sketch, "E1437", {"start": v(19.34, 101.96) * mm, "end": v(19.38, 101.96) * mm});
            skLineSegment(sketch, "E1438", {"start": v(19.38, 101.96) * mm, "end": v(19.59, 101.94) * mm});
            skLineSegment(sketch, "E1439", {"start": v(19.59, 101.94) * mm, "end": v(20.03, 101.96) * mm});
            skLineSegment(sketch, "E1440", {"start": v(20.03, 101.96) * mm, "end": v(20.59, 102.14) * mm});
            skLineSegment(sketch, "E1441", {"start": v(20.59, 102.14) * mm, "end": v(21.04, 102.42) * mm});
            skLineSegment(sketch, "E1442", {"start": v(21.04, 102.42) * mm, "end": v(21.17, 102.54) * mm});
            skLineSegment(sketch, "E1443", {"start": v(21.17, 102.54) * mm, "end": v(21.2, 102.56) * mm});
            skLineSegment(sketch, "E1444", {"start": v(21.2, 102.56) * mm, "end": v(21.43, 102.76) * mm});
            skLineSegment(sketch, "E1445", {"start": v(21.43, 102.76) * mm, "end": v(21.45, 102.78) * mm});
            skLineSegment(sketch, "E1446", {"start": v(21.45, 102.78) * mm, "end": v(21.46, 102.78) * mm});
            skLineSegment(sketch, "E1447", {"start": v(21.46, 102.78) * mm, "end": v(21.44, 102.81) * mm});
            skLineSegment(sketch, "E1448", {"start": v(21.44, 102.81) * mm, "end": v(21.43, 102.81) * mm});
            skLineSegment(sketch, "E1449", {"start": v(21.43, 102.81) * mm, "end": v(21.4, 102.8) * mm});
            skLineSegment(sketch, "E1450", {"start": v(21.4, 102.8) * mm, "end": v(21.1, 102.7) * mm});
            skLineSegment(sketch, "E1451", {"start": v(21.1, 102.7) * mm, "end": v(21.07, 102.68) * mm});
            skLineSegment(sketch, "E1452", {"start": v(21.07, 102.68) * mm, "end": v(20.81, 102.6) * mm});
            skLineSegment(sketch, "E1453", {"start": v(20.81, 102.6) * mm, "end": v(19.36, 102.56) * mm});
            skLineSegment(sketch, "E1454", {"start": v(19.36, 102.56) * mm, "end": v(17.66, 102.86) * mm});
            skLineSegment(sketch, "E1455", {"start": v(17.66, 102.86) * mm, "end": v(17.28, 102.95) * mm});
            skLineSegment(sketch, "E1456", {"start": v(17.28, 102.95) * mm, "end": v(17.2, 102.97) * mm});
            skLineSegment(sketch, "E1457", {"start": v(17.2, 102.97) * mm, "end": v(16.47, 103.28) * mm});
            skLineSegment(sketch, "E1458", {"start": v(16.47, 103.28) * mm, "end": v(16.4, 103.32) * mm});
            skLineSegment(sketch, "E1459", {"start": v(16.4, 103.32) * mm, "end": v(16.4, 103.36) * mm});
            skLineSegment(sketch, "E1460", {"start": v(16.4, 103.36) * mm, "end": v(16.28, 103.7) * mm});
            skLineSegment(sketch, "E1461", {"start": v(16.28, 103.7) * mm, "end": v(16.23, 103.74) * mm});
            skLineSegment(sketch, "E1462", {"start": v(16.23, 103.74) * mm, "end": v(16.2, 103.76) * mm});
            skLineSegment(sketch, "E1463", {"start": v(16.2, 103.76) * mm, "end": v(15.73, 103.89) * mm});
            skLineSegment(sketch, "E1464", {"start": v(15.73, 103.89) * mm, "end": v(15.68, 103.9) * mm});
            skLineSegment(sketch, "E1465", {"start": v(15.68, 103.9) * mm, "end": v(15.64, 103.92) * mm});
            skLineSegment(sketch, "E1466", {"start": v(15.64, 103.92) * mm, "end": v(15.3, 104.36) * mm});
            skLineSegment(sketch, "E1467", {"start": v(15.3, 104.36) * mm, "end": v(15.26, 104.4) * mm});
            skLineSegment(sketch, "E1468", {"start": v(15.26, 104.4) * mm, "end": v(15.14, 104.64) * mm});
            skLineSegment(sketch, "E1469", {"start": v(15.14, 104.64) * mm, "end": v(14.2, 106.6) * mm});
            skLineSegment(sketch, "E1470", {"start": v(14.2, 106.6) * mm, "end": v(13, 109.45) * mm});
            skLineSegment(sketch, "E1471", {"start": v(13, 109.45) * mm, "end": v(12.74, 110.12) * mm});
            skLineSegment(sketch, "E1472", {"start": v(12.74, 110.12) * mm, "end": v(12.55, 110.63) * mm});
            skLineSegment(sketch, "E1473", {"start": v(12.55, 110.63) * mm, "end": v(12.02, 112.18) * mm});
            skLineSegment(sketch, "E1474", {"start": v(12.02, 112.18) * mm, "end": v(11.44, 114.01) * mm});
            skLineSegment(sketch, "E1475", {"start": v(11.44, 114.01) * mm, "end": v(11, 115.5) * mm});
            skLineSegment(sketch, "E1476", {"start": v(11, 115.5) * mm, "end": v(10.8, 116.27) * mm});
            skLineSegment(sketch, "E1477", {"start": v(10.8, 116.27) * mm, "end": v(10.74, 116.52) * mm});
            skLineSegment(sketch, "E1478", {"start": v(10.74, 116.52) * mm, "end": v(10.67, 116.8) * mm});
            skLineSegment(sketch, "E1479", {"start": v(10.67, 116.8) * mm, "end": v(10.65, 116.84) * mm});
            skLineSegment(sketch, "E1480", {"start": v(10.65, 116.84) * mm, "end": v(10.65, 116.86) * mm});
            skLineSegment(sketch, "E1481", {"start": v(10.65, 116.86) * mm, "end": v(10.62, 116.95) * mm});
            skLineSegment(sketch, "E1482", {"start": v(10.62, 116.95) * mm, "end": v(10.62, 116.94) * mm});
            skLineSegment(sketch, "E1483", {"start": v(10.62, 116.94) * mm, "end": v(10.61, 117) * mm});
            skLineSegment(sketch, "E1484", {"start": v(10.61, 117) * mm, "end": v(10.49, 117.44) * mm});
            skLineSegment(sketch, "E1485", {"start": v(10.49, 117.44) * mm, "end": v(10.47, 117.48) * mm});
            skLineSegment(sketch, "E1486", {"start": v(10.47, 117.48) * mm, "end": v(10.47, 117.49) * mm});
            skLineSegment(sketch, "E1487", {"start": v(10.47, 117.49) * mm, "end": v(10.46, 117.54) * mm});
            skLineSegment(sketch, "E1488", {"start": v(10.46, 117.54) * mm, "end": v(10.45, 117.55) * mm});
            skLineSegment(sketch, "E1489", {"start": v(10.45, 117.55) * mm, "end": v(10.37, 117.52) * mm});
            skLineSegment(sketch, "E1490", {"start": v(10.37, 117.52) * mm, "end": v(10.3, 117.24) * mm});
            skLineSegment(sketch, "E1491", {"start": v(10.3, 117.24) * mm, "end": v(10.27, 116.82) * mm});
            skLineSegment(sketch, "E1492", {"start": v(10.27, 116.82) * mm, "end": v(10.27, 116.47) * mm});
            skLineSegment(sketch, "E1493", {"start": v(10.27, 116.47) * mm, "end": v(10.29, 116.36) * mm});
            skLineSegment(sketch, "E1494", {"start": v(10.29, 116.36) * mm, "end": v(10.24, 116.3) * mm});
            skLineSegment(sketch, "E1495", {"start": v(10.24, 116.3) * mm, "end": v(9.84, 115.5) * mm});
            skLineSegment(sketch, "E1496", {"start": v(9.84, 115.5) * mm, "end": v(9.8, 115.4) * mm});
            skLineSegment(sketch, "E1497", {"start": v(9.8, 115.4) * mm, "end": v(9.7, 115.16) * mm});
            skLineSegment(sketch, "E1498", {"start": v(9.7, 115.16) * mm, "end": v(9.26, 114.05) * mm});
            skLineSegment(sketch, "E1499", {"start": v(9.26, 114.05) * mm, "end": v(8.68, 113.13) * mm});
            skLineSegment(sketch, "E1500", {"start": v(8.68, 113.13) * mm, "end": v(8.5, 113) * mm});
            skLineSegment(sketch, "E1501", {"start": v(8.5, 113) * mm, "end": v(8.36, 112.9) * mm});
            skLineSegment(sketch, "E1502", {"start": v(8.36, 112.9) * mm, "end": v(7.83, 112.55) * mm});
            skLineSegment(sketch, "E1503", {"start": v(7.83, 112.55) * mm, "end": v(7.53, 112.37) * mm});
            skLineSegment(sketch, "E1504", {"start": v(7.53, 112.37) * mm, "end": v(7.51, 112.35) * mm});
            skLineSegment(sketch, "E1505", {"start": v(7.51, 112.35) * mm, "end": v(7.5, 112.34) * mm});
            skLineSegment(sketch, "E1506", {"start": v(7.5, 112.34) * mm, "end": v(7.51, 112.25) * mm});
            skLineSegment(sketch, "E1507", {"start": v(7.51, 112.25) * mm, "end": v(7.63, 112.2) * mm});
            skLineSegment(sketch, "E1508", {"start": v(7.63, 112.2) * mm, "end": v(7.66, 112.18) * mm});
            skLineSegment(sketch, "E1509", {"start": v(7.66, 112.18) * mm, "end": v(7.68, 112.18) * mm});
            skLineSegment(sketch, "E1510", {"start": v(7.68, 112.18) * mm, "end": v(7.84, 112.06) * mm});
            skLineSegment(sketch, "E1511", {"start": v(7.84, 112.06) * mm, "end": v(7.85, 112.04) * mm});
            skLineSegment(sketch, "E1512", {"start": v(7.85, 112.04) * mm, "end": v(7.87, 112) * mm});
            skLineSegment(sketch, "E1513", {"start": v(7.87, 112) * mm, "end": v(8.06, 111.61) * mm});
            skLineSegment(sketch, "E1514", {"start": v(8.06, 111.61) * mm, "end": v(8.07, 111.58) * mm});
            skLineSegment(sketch, "E1515", {"start": v(8.07, 111.58) * mm, "end": v(8.08, 111.56) * mm});
            skLineSegment(sketch, "E1516", {"start": v(8.08, 111.56) * mm, "end": v(8.12, 111.44) * mm});
            skLineSegment(sketch, "E1517", {"start": v(8.12, 111.44) * mm, "end": v(8.12, 111.42) * mm});
            skLineSegment(sketch, "E1518", {"start": v(8.12, 111.42) * mm, "end": v(8.21, 111.18) * mm});
            skLineSegment(sketch, "E1519", {"start": v(8.21, 111.18) * mm, "end": v(8.48, 110.46) * mm});
            skLineSegment(sketch, "E1520", {"start": v(8.48, 110.46) * mm, "end": v(8.97, 109.22) * mm});
            skLineSegment(sketch, "E1521", {"start": v(8.97, 109.22) * mm, "end": v(9.65, 107.8) * mm});
            skLineSegment(sketch, "E1522", {"start": v(9.65, 107.8) * mm, "end": v(10.3, 106.62) * mm});
            skLineSegment(sketch, "E1523", {"start": v(10.3, 106.62) * mm, "end": v(10.55, 106.25) * mm});
            skLineSegment(sketch, "E1524", {"start": v(10.55, 106.25) * mm, "end": v(10.7, 106) * mm});
            skLineSegment(sketch, "E1525", {"start": v(10.7, 106) * mm, "end": v(11.18, 105.3) * mm});
            skLineSegment(sketch, "E1526", {"start": v(11.18, 105.3) * mm, "end": v(11.72, 104.46) * mm});
            skLineSegment(sketch, "E1527", {"start": v(11.72, 104.46) * mm, "end": v(12.03, 103.95) * mm});
            skLineSegment(sketch, "E1528", {"start": v(12.03, 103.95) * mm, "end": v(11.95, 103.95) * mm});
            skLineSegment(sketch, "E1529", {"start": v(11.95, 103.95) * mm, "end": v(11.94, 103.97) * mm});
            skLineSegment(sketch, "E1530", {"start": v(11.94, 103.97) * mm, "end": v(11.74, 104.15) * mm});
            skLineSegment(sketch, "E1531", {"start": v(11.74, 104.15) * mm, "end": v(11.17, 104.74) * mm});
            skLineSegment(sketch, "E1532", {"start": v(11.17, 104.74) * mm, "end": v(10.37, 105.64) * mm});
            skLineSegment(sketch, "E1533", {"start": v(10.37, 105.64) * mm, "end": v(9.62, 106.56) * mm});
            skLineSegment(sketch, "E1534", {"start": v(9.62, 106.56) * mm, "end": v(9.16, 107.18) * mm});
            skLineSegment(sketch, "E1535", {"start": v(9.16, 107.18) * mm, "end": v(9.02, 107.39) * mm});
            skLineSegment(sketch, "E1536", {"start": v(9.02, 107.39) * mm, "end": v(8.93, 107.53) * mm});
            skLineSegment(sketch, "E1537", {"start": v(8.93, 107.53) * mm, "end": v(8.46, 108.4) * mm});
            skLineSegment(sketch, "E1538", {"start": v(8.46, 108.4) * mm, "end": v(8, 109.42) * mm});
            skLineSegment(sketch, "E1539", {"start": v(8, 109.42) * mm, "end": v(7.93, 109.62) * mm});
            skLineSegment(sketch, "E1540", {"start": v(7.93, 109.62) * mm, "end": v(7.85, 109.78) * mm});
            skLineSegment(sketch, "E1541", {"start": v(7.85, 109.78) * mm, "end": v(7.55, 110.59) * mm});
            skLineSegment(sketch, "E1542", {"start": v(7.55, 110.59) * mm, "end": v(7.36, 111.24) * mm});
            skLineSegment(sketch, "E1543", {"start": v(7.36, 111.24) * mm, "end": v(7.34, 111.32) * mm});
            skLineSegment(sketch, "E1544", {"start": v(7.34, 111.32) * mm, "end": v(7.34, 111.34) * mm});
            skLineSegment(sketch, "E1545", {"start": v(7.34, 111.34) * mm, "end": v(7.33, 111.4) * mm});
            skLineSegment(sketch, "E1546", {"start": v(7.33, 111.4) * mm, "end": v(7.32, 111.43) * mm});
            skLineSegment(sketch, "E1547", {"start": v(7.32, 111.43) * mm, "end": v(7.2, 111.68) * mm});
            skLineSegment(sketch, "E1548", {"start": v(7.2, 111.68) * mm, "end": v(7.2, 111.7) * mm});
            skLineSegment(sketch, "E1549", {"start": v(7.2, 111.7) * mm, "end": v(7.15, 111.77) * mm});
            skLineSegment(sketch, "E1550", {"start": v(7.15, 111.77) * mm, "end": v(6.92, 111.97) * mm});
            skLineSegment(sketch, "E1551", {"start": v(6.92, 111.97) * mm, "end": v(6.68, 112) * mm});
            skLineSegment(sketch, "E1552", {"start": v(6.68, 112) * mm, "end": v(6.64, 111.98) * mm});
            skLineSegment(sketch, "E1553", {"start": v(6.64, 111.98) * mm, "end": v(6.6, 111.96) * mm});
            skLineSegment(sketch, "E1554", {"start": v(6.6, 111.96) * mm, "end": v(6.29, 111.78) * mm});
            skLineSegment(sketch, "E1555", {"start": v(6.29, 111.78) * mm, "end": v(6.04, 111.66) * mm});
            skLineSegment(sketch, "E1556", {"start": v(6.04, 111.66) * mm, "end": v(6.13, 111.38) * mm});
            skLineSegment(sketch, "E1557", {"start": v(6.13, 111.38) * mm, "end": v(6.43, 110.6) * mm});
            skLineSegment(sketch, "E1558", {"start": v(6.43, 110.6) * mm, "end": v(7, 109.4) * mm});
            skLineSegment(sketch, "E1559", {"start": v(7, 109.4) * mm, "end": v(7.64, 108.26) * mm});
            skLineSegment(sketch, "E1560", {"start": v(7.64, 108.26) * mm, "end": v(7.88, 107.89) * mm});
            skLineSegment(sketch, "E1561", {"start": v(7.88, 107.89) * mm, "end": v(8.11, 107.53) * mm});
            skLineSegment(sketch, "E1562", {"start": v(8.11, 107.53) * mm, "end": v(8.83, 106.48) * mm});
            skLineSegment(sketch, "E1563", {"start": v(8.83, 106.48) * mm, "end": v(9.6, 105.46) * mm});
            skLineSegment(sketch, "E1564", {"start": v(9.6, 105.46) * mm, "end": v(10.27, 104.65) * mm});
            skLineSegment(sketch, "E1565", {"start": v(10.27, 104.65) * mm, "end": v(10.76, 104.08) * mm});
            skLineSegment(sketch, "E1566", {"start": v(10.76, 104.08) * mm, "end": v(10.92, 103.88) * mm});
            skLineSegment(sketch, "E1567", {"start": v(10.92, 103.88) * mm, "end": v(10.94, 103.85) * mm});
            skLineSegment(sketch, "E1568", {"start": v(10.94, 103.85) * mm, "end": v(11.17, 103.56) * mm});
            skLineSegment(sketch, "E1569", {"start": v(11.17, 103.56) * mm, "end": v(11.19, 103.53) * mm});
            skLineSegment(sketch, "E1570", {"start": v(11.19, 103.53) * mm, "end": v(11.23, 103.48) * mm});
            skLineSegment(sketch, "E1571", {"start": v(11.23, 103.48) * mm, "end": v(11.54, 103) * mm});
            skLineSegment(sketch, "E1572", {"start": v(11.54, 103) * mm, "end": v(11.58, 102.95) * mm});
            skLineSegment(sketch, "E1573", {"start": v(11.58, 102.95) * mm, "end": v(11.57, 102.9) * mm});
            skLineSegment(sketch, "E1574", {"start": v(11.57, 102.9) * mm, "end": v(11.59, 102.6) * mm});
            skLineSegment(sketch, "E1575", {"start": v(11.59, 102.6) * mm, "end": v(11.7, 102.28) * mm});
            skLineSegment(sketch, "E1576", {"start": v(11.7, 102.28) * mm, "end": v(11.73, 102.23) * mm});
            skLineSegment(sketch, "E1577", {"start": v(11.73, 102.23) * mm, "end": v(11.75, 102.21) * mm});
            skLineSegment(sketch, "E1578", {"start": v(11.75, 102.21) * mm, "end": v(11.91, 102.11) * mm});
            skLineSegment(sketch, "E1579", {"start": v(11.91, 102.11) * mm, "end": v(11.94, 102.1) * mm});
            skLineSegment(sketch, "E1580", {"start": v(11.94, 102.1) * mm, "end": v(11.96, 102.1) * mm});
            skLineSegment(sketch, "E1581", {"start": v(11.96, 102.1) * mm, "end": v(12.05, 102.08) * mm});
            skLineSegment(sketch, "E1582", {"start": v(12.05, 102.08) * mm, "end": v(12.18, 102.01) * mm});
            skLineSegment(sketch, "E1583", {"start": v(12.18, 102.01) * mm, "end": v(12.27, 101.86) * mm});
            skLineSegment(sketch, "E1584", {"start": v(12.27, 101.86) * mm, "end": v(12.25, 101.64) * mm});
            skLineSegment(sketch, "E1585", {"start": v(12.25, 101.64) * mm, "end": v(12.23, 101.58) * mm});
            skLineSegment(sketch, "E1586", {"start": v(12.23, 101.58) * mm, "end": v(12.21, 101.56) * mm});
            skLineSegment(sketch, "E1587", {"start": v(12.21, 101.56) * mm, "end": v(12.11, 101.38) * mm});
            skLineSegment(sketch, "E1588", {"start": v(12.11, 101.38) * mm, "end": v(12.1, 101.36) * mm});
            skLineSegment(sketch, "E1589", {"start": v(12.1, 101.36) * mm, "end": v(12.09, 101.32) * mm});
            skLineSegment(sketch, "E1590", {"start": v(12.09, 101.32) * mm, "end": v(12.1, 100.98) * mm});
            skLineSegment(sketch, "E1591", {"start": v(12.1, 100.98) * mm, "end": v(12.12, 100.95) * mm});
            skLineSegment(sketch, "E1592", {"start": v(12.12, 100.95) * mm, "end": v(12.15, 100.88) * mm});
            skLineSegment(sketch, "E1593", {"start": v(12.15, 100.88) * mm, "end": v(12.35, 100.63) * mm});
            skLineSegment(sketch, "E1594", {"start": v(12.35, 100.63) * mm, "end": v(12.53, 100.43) * mm});
            skLineSegment(sketch, "E1595", {"start": v(12.53, 100.43) * mm, "end": v(12.54, 100.4) * mm});
            skLineSegment(sketch, "E1596", {"start": v(12.54, 100.4) * mm, "end": v(12.56, 100.35) * mm});
            skLineSegment(sketch, "E1597", {"start": v(12.56, 100.35) * mm, "end": v(12.63, 100.05) * mm});
            skLineSegment(sketch, "E1598", {"start": v(12.63, 100.05) * mm, "end": v(12.75, 99.58) * mm});
            skLineSegment(sketch, "E1599", {"start": v(12.75, 99.58) * mm, "end": v(12.8, 99.45) * mm});
            skLineSegment(sketch, "E1600", {"start": v(12.8, 99.45) * mm, "end": v(12.8, 99.41) * mm});
            skLineSegment(sketch, "E1601", {"start": v(12.8, 99.41) * mm, "end": v(12.91, 99.14) * mm});
            skLineSegment(sketch, "E1602", {"start": v(12.91, 99.14) * mm, "end": v(12.92, 99.11) * mm});
            skLineSegment(sketch, "E1603", {"start": v(12.92, 99.11) * mm, "end": v(12.94, 99.07) * mm});
            skLineSegment(sketch, "E1604", {"start": v(12.94, 99.07) * mm, "end": v(13.12, 98.64) * mm});
            skLineSegment(sketch, "E1605", {"start": v(13.12, 98.64) * mm, "end": v(13.14, 98.6) * mm});
            skLineSegment(sketch, "E1606", {"start": v(13.14, 98.6) * mm, "end": v(13.23, 98.44) * mm});
            skLineSegment(sketch, "E1607", {"start": v(13.23, 98.44) * mm, "end": v(13.54, 98) * mm});
            skLineSegment(sketch, "E1608", {"start": v(13.54, 98) * mm, "end": v(13.97, 97.5) * mm});
            skLineSegment(sketch, "E1609", {"start": v(13.97, 97.5) * mm, "end": v(14.31, 97.14) * mm});
            skLineSegment(sketch, "E1610", {"start": v(14.31, 97.14) * mm, "end": v(14.46, 97.02) * mm});
            skLineSegment(sketch, "E1611", {"start": v(14.46, 97.02) * mm, "end": v(15.23, 96.21) * mm});
            skLineSegment(sketch, "E1612", {"start": v(15.23, 96.21) * mm, "end": v(15.58, 96.31) * mm});
            skLineSegment(sketch, "E1613", {"start": v(15.58, 96.31) * mm, "end": v(16.34, 96.63) * mm});
            skLineSegment(sketch, "E1614", {"start": v(16.34, 96.63) * mm, "end": v(16.55, 96.73) * mm});
            skLineSegment(sketch, "E1615", {"start": v(16.55, 96.73) * mm, "end": v(16.76, 96.83) * mm});
            skLineSegment(sketch, "E1616", {"start": v(16.76, 96.83) * mm, "end": v(17.46, 97.26) * mm});
            skLineSegment(sketch, "E1617", {"start": v(17.46, 97.26) * mm, "end": v(17.74, 97.47) * mm});
            skLineSegment(sketch, "E1618", {"start": v(17.74, 97.47) * mm, "end": v(17.57, 98.36) * mm});
            skLineSegment(sketch, "E1619", {"start": v(17.57, 98.36) * mm, "end": v(18.1, 98.57) * mm});
            skLineSegment(sketch, "E1620", {"start": v(18.1, 98.57) * mm, "end": v(18.23, 98.62) * mm});
            skLineSegment(sketch, "E1621", {"start": v(18.23, 98.62) * mm, "end": v(18.76, 98.76) * mm});
            skLineSegment(sketch, "E1622", {"start": v(18.76, 98.76) * mm, "end": v(19.77, 99) * mm});
            skLineSegment(sketch, "E1623", {"start": v(19.77, 99) * mm, "end": v(20.91, 99.34) * mm});
            skLineSegment(sketch, "E1624", {"start": v(20.91, 99.34) * mm, "end": v(21.7, 99.64) * mm});
            skLineSegment(sketch, "E1625", {"start": v(21.7, 99.64) * mm, "end": v(21.94, 99.78) * mm});
            skLineSegment(sketch, "E1626", {"start": v(21.94, 99.78) * mm, "end": v(22.2, 99.91) * mm});
            skLineSegment(sketch, "E1627", {"start": v(22.2, 99.91) * mm, "end": v(22.87, 100.48) * mm});
            skLineSegment(sketch, "E1628", {"start": v(22.87, 100.48) * mm, "end": v(23.74, 101.47) * mm});
            skLineSegment(sketch, "E1629", {"start": v(23.74, 101.47) * mm, "end": v(24.44, 102.52) * mm});
            skLineSegment(sketch, "E1630", {"start": v(24.44, 102.52) * mm, "end": v(24.75, 103.18) * mm});
            skLineSegment(sketch, "E1631", {"start": v(24.75, 103.18) * mm, "end": v(24.8, 103.4) * mm});
            skLineSegment(sketch, "E1632", {"start": v(24.8, 103.4) * mm, "end": v(24.81, 103.46) * mm});
            skLineSegment(sketch, "E1633", {"start": v(24.81, 103.46) * mm, "end": v(24.65, 103.7) * mm});
            skLineSegment(sketch, "E1634", {"start": v(24.65, 103.7) * mm, "end": v(24.42, 103.82) * mm});
            skLineSegment(sketch, "E1635", {"start": v(24.42, 103.82) * mm, "end": v(24.4, 103.83) * mm});
            skLineSegment(sketch, "E1636", {"start": v(13.89, 99.19) * mm, "end": v(13.85, 99.16) * mm});
            skLineSegment(sketch, "E1637", {"start": v(13.85, 99.16) * mm, "end": v(13.55, 99.19) * mm});
            skLineSegment(sketch, "E1638", {"start": v(13.55, 99.19) * mm, "end": v(13.2, 99.5) * mm});
            skLineSegment(sketch, "E1639", {"start": v(13.2, 99.5) * mm, "end": v(13.14, 99.61) * mm});
            skLineSegment(sketch, "E1640", {"start": v(13.14, 99.61) * mm, "end": v(13.12, 99.67) * mm});
            skLineSegment(sketch, "E1641", {"start": v(13.12, 99.67) * mm, "end": v(12.97, 100.35) * mm});
            skLineSegment(sketch, "E1642", {"start": v(12.97, 100.35) * mm, "end": v(12.96, 100.41) * mm});
            skLineSegment(sketch, "E1643", {"start": v(12.96, 100.41) * mm, "end": v(12.95, 100.47) * mm});
            skLineSegment(sketch, "E1644", {"start": v(12.95, 100.47) * mm, "end": v(13.17, 100.7) * mm});
            skLineSegment(sketch, "E1645", {"start": v(13.17, 100.7) * mm, "end": v(13.54, 100.74) * mm});
            skLineSegment(sketch, "E1646", {"start": v(13.54, 100.74) * mm, "end": v(13.6, 100.7) * mm});
            skLineSegment(sketch, "E1647", {"start": v(13.6, 100.7) * mm, "end": v(13.67, 100.67) * mm});
            skLineSegment(sketch, "E1648", {"start": v(13.67, 100.67) * mm, "end": v(13.8, 100.35) * mm});
            skLineSegment(sketch, "E1649", {"start": v(13.8, 100.35) * mm, "end": v(13.78, 100.1) * mm});
            skLineSegment(sketch, "E1650", {"start": v(13.78, 100.1) * mm, "end": v(13.78, 100) * mm});
            skLineSegment(sketch, "E1651", {"start": v(13.78, 100) * mm, "end": v(13.8, 99.65) * mm});
            skLineSegment(sketch, "E1652", {"start": v(13.8, 99.65) * mm, "end": v(13.87, 99.4) * mm});
            skLineSegment(sketch, "E1653", {"start": v(13.87, 99.4) * mm, "end": v(13.92, 99.26) * mm});
            skLineSegment(sketch, "E1654", {"start": v(13.92, 99.26) * mm, "end": v(13.9, 99.2) * mm});
            skLineSegment(sketch, "E1655", {"start": v(13.9, 99.2) * mm, "end": v(13.89, 99.19) * mm});
            skLineSegment(sketch, "E1656", {"start": v(18, 99.3) * mm, "end": v(17.92, 99.28) * mm});
            skLineSegment(sketch, "E1657", {"start": v(17.92, 99.28) * mm, "end": v(17.41, 99.12) * mm});
            skLineSegment(sketch, "E1658", {"start": v(17.41, 99.12) * mm, "end": v(16.88, 98.98) * mm});
            skLineSegment(sketch, "E1659", {"start": v(16.88, 98.98) * mm, "end": v(16.8, 98.96) * mm});
            skLineSegment(sketch, "E1660", {"start": v(16.8, 98.96) * mm, "end": v(16.7, 98.94) * mm});
            skLineSegment(sketch, "E1661", {"start": v(16.7, 98.94) * mm, "end": v(16.4, 98.86) * mm});
            skLineSegment(sketch, "E1662", {"start": v(16.4, 98.86) * mm, "end": v(16.16, 98.76) * mm});
            skLineSegment(sketch, "E1663", {"start": v(16.16, 98.76) * mm, "end": v(15.92, 98.6) * mm});
            skLineSegment(sketch, "E1664", {"start": v(15.92, 98.6) * mm, "end": v(15.66, 98.43) * mm});
            skLineSegment(sketch, "E1665", {"start": v(15.66, 98.43) * mm, "end": v(15.57, 98.37) * mm});
            skLineSegment(sketch, "E1666", {"start": v(15.57, 98.37) * mm, "end": v(15.5, 98.33) * mm});
            skLineSegment(sketch, "E1667", {"start": v(15.5, 98.33) * mm, "end": v(15.26, 98.3) * mm});
            skLineSegment(sketch, "E1668", {"start": v(15.26, 98.3) * mm, "end": v(15.2, 98.48) * mm});
            skLineSegment(sketch, "E1669", {"start": v(15.2, 98.48) * mm, "end": v(15.29, 98.78) * mm});
            skLineSegment(sketch, "E1670", {"start": v(15.29, 98.78) * mm, "end": v(15.42, 98.98) * mm});
            skLineSegment(sketch, "E1671", {"start": v(15.42, 98.98) * mm, "end": v(15.47, 99.03) * mm});
            skLineSegment(sketch, "E1672", {"start": v(15.47, 99.03) * mm, "end": v(15.54, 99.1) * mm});
            skLineSegment(sketch, "E1673", {"start": v(15.54, 99.1) * mm, "end": v(16.2, 99.28) * mm});
            skLineSegment(sketch, "E1674", {"start": v(16.2, 99.28) * mm, "end": v(16.91, 99.33) * mm});
            skLineSegment(sketch, "E1675", {"start": v(16.91, 99.33) * mm, "end": v(17.15, 99.33) * mm});
            skLineSegment(sketch, "E1676", {"start": v(17.15, 99.33) * mm, "end": v(17.32, 99.33) * mm});
            skLineSegment(sketch, "E1677", {"start": v(17.32, 99.33) * mm, "end": v(17.82, 99.46) * mm});
            skLineSegment(sketch, "E1678", {"start": v(17.82, 99.46) * mm, "end": v(18.18, 99.6) * mm});
            skLineSegment(sketch, "E1679", {"start": v(18.18, 99.6) * mm, "end": v(18.22, 99.6) * mm});
            skLineSegment(sketch, "E1680", {"start": v(18.22, 99.6) * mm, "end": v(18.22, 99.6) * mm});
            skLineSegment(sketch, "E1681", {"start": v(18.22, 99.6) * mm, "end": v(18.24, 99.51) * mm});
            skLineSegment(sketch, "E1682", {"start": v(18.24, 99.51) * mm, "end": v(18.07, 99.34) * mm});
            skLineSegment(sketch, "E1683", {"start": v(18.07, 99.34) * mm, "end": v(18, 99.3) * mm});
            skLineSegment(sketch, "E1684", {"start": v(14.18, 150.58) * mm, "end": v(14.2, 150.56) * mm});
            skLineSegment(sketch, "E1685", {"start": v(14.2, 150.56) * mm, "end": v(14.38, 150.38) * mm});
            skLineSegment(sketch, "E1686", {"start": v(14.38, 150.38) * mm, "end": v(14.39, 150.36) * mm});
            skLineSegment(sketch, "E1687", {"start": v(14.39, 150.36) * mm, "end": v(14.44, 150.38) * mm});
            skLineSegment(sketch, "E1688", {"start": v(14.44, 150.38) * mm, "end": v(14.77, 150.7) * mm});
            skLineSegment(sketch, "E1689", {"start": v(14.77, 150.7) * mm, "end": v(14.78, 150.76) * mm});
            skLineSegment(sketch, "E1690", {"start": v(14.78, 150.76) * mm, "end": v(14.8, 150.81) * mm});
            skLineSegment(sketch, "E1691", {"start": v(14.8, 150.81) * mm, "end": v(14.67, 151.02) * mm});
            skLineSegment(sketch, "E1692", {"start": v(14.67, 151.02) * mm, "end": v(14.33, 151.15) * mm});
            skLineSegment(sketch, "E1693", {"start": v(14.33, 151.15) * mm, "end": v(14.24, 151.16) * mm});
            skLineSegment(sketch, "E1694", {"start": v(14.24, 151.16) * mm, "end": v(14.13, 151.17) * mm});
            skLineSegment(sketch, "E1695", {"start": v(14.13, 151.17) * mm, "end": v(13.68, 151.26) * mm});
            skLineSegment(sketch, "E1696", {"start": v(13.68, 151.26) * mm, "end": v(13.43, 151.32) * mm});
            skLineSegment(sketch, "E1697", {"start": v(13.43, 151.32) * mm, "end": v(13.33, 151.32) * mm});
            skLineSegment(sketch, "E1698", {"start": v(13.33, 151.32) * mm, "end": v(13.06, 151.24) * mm});
            skLineSegment(sketch, "E1699", {"start": v(13.06, 151.24) * mm, "end": v(13.04, 151.22) * mm});
            skLineSegment(sketch, "E1700", {"start": v(13.04, 151.22) * mm, "end": v(13.11, 151.18) * mm});
            skLineSegment(sketch, "E1701", {"start": v(13.11, 151.18) * mm, "end": v(13.14, 151.18) * mm});
            skLineSegment(sketch, "E1702", {"start": v(13.14, 151.18) * mm, "end": v(13.17, 151.17) * mm});
            skLineSegment(sketch, "E1703", {"start": v(13.17, 151.17) * mm, "end": v(13.64, 150.92) * mm});
            skLineSegment(sketch, "E1704", {"start": v(13.64, 150.92) * mm, "end": v(14.14, 150.62) * mm});
            skLineSegment(sketch, "E1705", {"start": v(14.14, 150.62) * mm, "end": v(14.18, 150.58) * mm});
            skLineSegment(sketch, "E1706", {"start": v(3.02, 167.78) * mm, "end": v(3, 167.8) * mm});
            skLineSegment(sketch, "E1707", {"start": v(3, 167.8) * mm, "end": v(2.8, 167.91) * mm});
            skLineSegment(sketch, "E1708", {"start": v(2.8, 167.91) * mm, "end": v(2.78, 167.92) * mm});
            skLineSegment(sketch, "E1709", {"start": v(2.78, 167.92) * mm, "end": v(2.77, 167.93) * mm});
            skLineSegment(sketch, "E1710", {"start": v(2.77, 167.93) * mm, "end": v(2.74, 167.94) * mm});
            skLineSegment(sketch, "E1711", {"start": v(2.74, 167.94) * mm, "end": v(2.68, 167.96) * mm});
            skLineSegment(sketch, "E1712", {"start": v(2.68, 167.96) * mm, "end": v(2.39, 167.9) * mm});
            skLineSegment(sketch, "E1713", {"start": v(2.39, 167.9) * mm, "end": v(2.06, 167.95) * mm});
            skLineSegment(sketch, "E1714", {"start": v(2.06, 167.95) * mm, "end": v(2, 168.02) * mm});
            skLineSegment(sketch, "E1715", {"start": v(2, 168.02) * mm, "end": v(1.89, 168.13) * mm});
            skLineSegment(sketch, "E1716", {"start": v(1.89, 168.13) * mm, "end": v(1.54, 168.45) * mm});
            skLineSegment(sketch, "E1717", {"start": v(1.54, 168.45) * mm, "end": v(1.1, 168.75) * mm});
            skLineSegment(sketch, "E1718", {"start": v(1.1, 168.75) * mm, "end": v(0.77, 168.86) * mm});
            skLineSegment(sketch, "E1719", {"start": v(0.77, 168.86) * mm, "end": v(0.62, 168.77) * mm});
            skLineSegment(sketch, "E1720", {"start": v(0.62, 168.77) * mm, "end": v(0.62, 168.73) * mm});
            skLineSegment(sketch, "E1721", {"start": v(0.62, 168.73) * mm, "end": v(0.6, 168.64) * mm});
            skLineSegment(sketch, "E1722", {"start": v(0.6, 168.64) * mm, "end": v(0.57, 167.67) * mm});
            skLineSegment(sketch, "E1723", {"start": v(0.57, 167.67) * mm, "end": v(0.6, 167.57) * mm});
            skLineSegment(sketch, "E1724", {"start": v(0.6, 167.57) * mm, "end": v(0.63, 167.4) * mm});
            skLineSegment(sketch, "E1725", {"start": v(0.63, 167.4) * mm, "end": v(0.8, 166.8) * mm});
            skLineSegment(sketch, "E1726", {"start": v(0.8, 166.8) * mm, "end": v(0.9, 166.55) * mm});
            skLineSegment(sketch, "E1727", {"start": v(0.9, 166.55) * mm, "end": v(0.98, 166.43) * mm});
            skLineSegment(sketch, "E1728", {"start": v(0.98, 166.43) * mm, "end": v(1.25, 166.4) * mm});
            skLineSegment(sketch, "E1729", {"start": v(1.25, 166.4) * mm, "end": v(1.32, 166.44) * mm});
            skLineSegment(sketch, "E1730", {"start": v(1.32, 166.44) * mm, "end": v(1.4, 166.47) * mm});
            skLineSegment(sketch, "E1731", {"start": v(1.4, 166.47) * mm, "end": v(1.76, 166.6) * mm});
            skLineSegment(sketch, "E1732", {"start": v(1.76, 166.6) * mm, "end": v(2.01, 166.64) * mm});
            skLineSegment(sketch, "E1733", {"start": v(2.01, 166.64) * mm, "end": v(2.03, 166.65) * mm});
            skLineSegment(sketch, "E1734", {"start": v(2.03, 166.65) * mm, "end": v(2.05, 166.65) * mm});
            skLineSegment(sketch, "E1735", {"start": v(2.05, 166.65) * mm, "end": v(2.28, 166.44) * mm});
            skLineSegment(sketch, "E1736", {"start": v(2.28, 166.44) * mm, "end": v(2.32, 166.41) * mm});
            skLineSegment(sketch, "E1737", {"start": v(2.32, 166.41) * mm, "end": v(2.37, 166.37) * mm});
            skLineSegment(sketch, "E1738", {"start": v(2.37, 166.37) * mm, "end": v(2.65, 166.27) * mm});
            skLineSegment(sketch, "E1739", {"start": v(2.65, 166.27) * mm, "end": v(2.88, 166.28) * mm});
            skLineSegment(sketch, "E1740", {"start": v(2.88, 166.28) * mm, "end": v(2.92, 166.3) * mm});
            skLineSegment(sketch, "E1741", {"start": v(2.92, 166.3) * mm, "end": v(2.95, 166.3) * mm});
            skLineSegment(sketch, "E1742", {"start": v(2.95, 166.3) * mm, "end": v(3.1, 166.43) * mm});
            skLineSegment(sketch, "E1743", {"start": v(3.1, 166.43) * mm, "end": v(3.21, 166.5) * mm});
            skLineSegment(sketch, "E1744", {"start": v(3.21, 166.5) * mm, "end": v(3.22, 166.5) * mm});
            skLineSegment(sketch, "E1745", {"start": v(3.22, 166.5) * mm, "end": v(3.3, 166.46) * mm});
            skLineSegment(sketch, "E1746", {"start": v(3.3, 166.46) * mm, "end": v(3.53, 166.32) * mm});
            skLineSegment(sketch, "E1747", {"start": v(3.53, 166.32) * mm, "end": v(3.87, 166.13) * mm});
            skLineSegment(sketch, "E1748", {"start": v(3.87, 166.13) * mm, "end": v(4.1, 166.1) * mm});
            skLineSegment(sketch, "E1749", {"start": v(4.1, 166.1) * mm, "end": v(4.12, 166.3) * mm});
            skLineSegment(sketch, "E1750", {"start": v(4.12, 166.3) * mm, "end": v(4.1, 166.36) * mm});
            skLineSegment(sketch, "E1751", {"start": v(4.1, 166.36) * mm, "end": v(4.09, 166.39) * mm});
            skLineSegment(sketch, "E1752", {"start": v(4.09, 166.39) * mm, "end": v(4.02, 166.57) * mm});
            skLineSegment(sketch, "E1753", {"start": v(4.02, 166.57) * mm, "end": v(3.94, 166.96) * mm});
            skLineSegment(sketch, "E1754", {"start": v(3.94, 166.96) * mm, "end": v(3.95, 167.46) * mm});
            skLineSegment(sketch, "E1755", {"start": v(3.95, 167.46) * mm, "end": v(4.07, 167.87) * mm});
            skLineSegment(sketch, "E1756", {"start": v(4.07, 167.87) * mm, "end": v(4.15, 167.98) * mm});
            skLineSegment(sketch, "E1757", {"start": v(4.15, 167.98) * mm, "end": v(4.18, 168.03) * mm});
            skLineSegment(sketch, "E1758", {"start": v(4.18, 168.03) * mm, "end": v(4.28, 168.25) * mm});
            skLineSegment(sketch, "E1759", {"start": v(4.28, 168.25) * mm, "end": v(4.25, 168.4) * mm});
            skLineSegment(sketch, "E1760", {"start": v(4.25, 168.4) * mm, "end": v(4.23, 168.4) * mm});
            skLineSegment(sketch, "E1761", {"start": v(4.23, 168.4) * mm, "end": v(4.21, 168.41) * mm});
            skLineSegment(sketch, "E1762", {"start": v(4.21, 168.41) * mm, "end": v(3.98, 168.37) * mm});
            skLineSegment(sketch, "E1763", {"start": v(3.98, 168.37) * mm, "end": v(3.67, 168.27) * mm});
            skLineSegment(sketch, "E1764", {"start": v(3.67, 168.27) * mm, "end": v(3.62, 168.25) * mm});
            skLineSegment(sketch, "E1765", {"start": v(3.62, 168.25) * mm, "end": v(3.57, 168.24) * mm});
            skLineSegment(sketch, "E1766", {"start": v(3.57, 168.24) * mm, "end": v(3.35, 168.1) * mm});
            skLineSegment(sketch, "E1767", {"start": v(3.35, 168.1) * mm, "end": v(3.18, 167.98) * mm});
            skLineSegment(sketch, "E1768", {"start": v(3.18, 167.98) * mm, "end": v(3.17, 167.96) * mm});
            skLineSegment(sketch, "E1769", {"start": v(3.17, 167.96) * mm, "end": v(3.17, 167.94) * mm});
            skLineSegment(sketch, "E1770", {"start": v(3.17, 167.94) * mm, "end": v(3.15, 167.94) * mm});
            skLineSegment(sketch, "E1771", {"start": v(3.15, 167.94) * mm, "end": v(3.14, 167.93) * mm});
            skLineSegment(sketch, "E1772", {"start": v(3.14, 167.93) * mm, "end": v(3.15, 167.77) * mm});
            skLineSegment(sketch, "E1773", {"start": v(3.15, 167.77) * mm, "end": v(3.17, 167.75) * mm});
            skLineSegment(sketch, "E1774", {"start": v(3.17, 167.75) * mm, "end": v(3.17, 167.74) * mm});
            skLineSegment(sketch, "E1775", {"start": v(3.17, 167.74) * mm, "end": v(3.12, 167.7) * mm});
            skLineSegment(sketch, "E1776", {"start": v(3.12, 167.7) * mm, "end": v(3.03, 167.76) * mm});
            skLineSegment(sketch, "E1777", {"start": v(3.03, 167.76) * mm, "end": v(3.02, 167.78) * mm});
            skLineSegment(sketch, "E1778", {"start": v(1.73, 171.75) * mm, "end": v(1.78, 171.78) * mm});
            skLineSegment(sketch, "E1779", {"start": v(1.78, 171.78) * mm, "end": v(2, 171.87) * mm});
            skLineSegment(sketch, "E1780", {"start": v(2, 171.87) * mm, "end": v(2.05, 171.94) * mm});
            skLineSegment(sketch, "E1781", {"start": v(2.05, 171.94) * mm, "end": v(1.87, 171.97) * mm});
            skLineSegment(sketch, "E1782", {"start": v(1.87, 171.97) * mm, "end": v(1.6, 171.93) * mm});
            skLineSegment(sketch, "E1783", {"start": v(1.6, 171.93) * mm, "end": v(1.57, 171.9) * mm});
            skLineSegment(sketch, "E1784", {"start": v(1.57, 171.9) * mm, "end": v(1.52, 171.88) * mm});
            skLineSegment(sketch, "E1785", {"start": v(1.52, 171.88) * mm, "end": v(1.43, 171.67) * mm});
            skLineSegment(sketch, "E1786", {"start": v(1.43, 171.67) * mm, "end": v(1.47, 171.51) * mm});
            skLineSegment(sketch, "E1787", {"start": v(1.47, 171.51) * mm, "end": v(1.48, 171.51) * mm});
            skLineSegment(sketch, "E1788", {"start": v(1.48, 171.51) * mm, "end": v(1.5, 171.5) * mm});
            skLineSegment(sketch, "E1789", {"start": v(1.5, 171.5) * mm, "end": v(1.56, 171.57) * mm});
            skLineSegment(sketch, "E1790", {"start": v(1.56, 171.57) * mm, "end": v(1.69, 171.72) * mm});
            skLineSegment(sketch, "E1791", {"start": v(1.69, 171.72) * mm, "end": v(1.73, 171.75) * mm});
            skLineSegment(sketch, "E1792", {"start": v(-0.06, 170.37) * mm, "end": v(-0.08, 170.38) * mm});
            skLineSegment(sketch, "E1793", {"start": v(-0.08, 170.38) * mm, "end": v(-0.26, 170.3) * mm});
            skLineSegment(sketch, "E1794", {"start": v(-0.26, 170.3) * mm, "end": v(-0.56, 170.1) * mm});
            skLineSegment(sketch, "E1795", {"start": v(-0.56, 170.1) * mm, "end": v(-0.75, 169.92) * mm});
            skLineSegment(sketch, "E1796", {"start": v(-0.75, 169.92) * mm, "end": v(-0.62, 169.84) * mm});
            skLineSegment(sketch, "E1797", {"start": v(-0.62, 169.84) * mm, "end": v(-0.58, 169.84) * mm});
            skLineSegment(sketch, "E1798", {"start": v(-0.58, 169.84) * mm, "end": v(-0.55, 169.84) * mm});
            skLineSegment(sketch, "E1799", {"start": v(-0.55, 169.84) * mm, "end": v(-0.5, 169.84) * mm});
            skLineSegment(sketch, "E1800", {"start": v(-0.5, 169.84) * mm, "end": v(0.11, 169.94) * mm});
            skLineSegment(sketch, "E1801", {"start": v(0.11, 169.94) * mm, "end": v(0.17, 169.95) * mm});
            skLineSegment(sketch, "E1802", {"start": v(0.17, 169.95) * mm, "end": v(0.18, 169.95) * mm});
            skLineSegment(sketch, "E1803", {"start": v(0.18, 169.95) * mm, "end": v(0.28, 170.07) * mm});
            skLineSegment(sketch, "E1804", {"start": v(0.28, 170.07) * mm, "end": v(0.28, 170.07) * mm});
            skLineSegment(sketch, "E1805", {"start": v(0.28, 170.07) * mm, "end": v(0.13, 170.22) * mm});
            skLineSegment(sketch, "E1806", {"start": v(0.13, 170.22) * mm, "end": v(-0.01, 170.37) * mm});
            skLineSegment(sketch, "E1807", {"start": v(-0.01, 170.37) * mm, "end": v(-0.06, 170.37) * mm});
            skLineSegment(sketch, "E1808", {"start": v(8.76, 116.52) * mm, "end": v(8.84, 116.73) * mm});
            skLineSegment(sketch, "E1809", {"start": v(8.84, 116.73) * mm, "end": v(9.1, 117.35) * mm});
            skLineSegment(sketch, "E1810", {"start": v(9.1, 117.35) * mm, "end": v(9.45, 117.97) * mm});
            skLineSegment(sketch, "E1811", {"start": v(9.45, 117.97) * mm, "end": v(9.73, 118.38) * mm});
            skLineSegment(sketch, "E1812", {"start": v(9.73, 118.38) * mm, "end": v(9.87, 118.57) * mm});
            skLineSegment(sketch, "E1813", {"start": v(9.87, 118.57) * mm, "end": v(9.9, 118.61) * mm});
            skLineSegment(sketch, "E1814", {"start": v(9.9, 118.61) * mm, "end": v(9.93, 118.64) * mm});
            skLineSegment(sketch, "E1815", {"start": v(9.93, 118.64) * mm, "end": v(9.87, 119.04) * mm});
            skLineSegment(sketch, "E1816", {"start": v(9.87, 119.04) * mm, "end": v(9.7, 119.51) * mm});
            skLineSegment(sketch, "E1817", {"start": v(9.7, 119.51) * mm, "end": v(9.67, 119.58) * mm});
            skLineSegment(sketch, "E1818", {"start": v(9.67, 119.58) * mm, "end": v(9.66, 119.6) * mm});
            skLineSegment(sketch, "E1819", {"start": v(9.66, 119.6) * mm, "end": v(9.62, 119.68) * mm});
            skLineSegment(sketch, "E1820", {"start": v(9.62, 119.68) * mm, "end": v(9.61, 119.68) * mm});
            skLineSegment(sketch, "E1821", {"start": v(9.61, 119.68) * mm, "end": v(9.45, 119.7) * mm});
            skLineSegment(sketch, "E1822", {"start": v(9.45, 119.7) * mm, "end": v(9.43, 119.7) * mm});
            skLineSegment(sketch, "E1823", {"start": v(9.43, 119.7) * mm, "end": v(9.25, 119.75) * mm});
            skLineSegment(sketch, "E1824", {"start": v(9.25, 119.75) * mm, "end": v(9.24, 119.77) * mm});
            skLineSegment(sketch, "E1825", {"start": v(9.24, 119.77) * mm, "end": v(9.27, 119.86) * mm});
            skLineSegment(sketch, "E1826", {"start": v(9.27, 119.86) * mm, "end": v(9.42, 120.67) * mm});
            skLineSegment(sketch, "E1827", {"start": v(9.42, 120.67) * mm, "end": v(9.43, 120.74) * mm});
            skLineSegment(sketch, "E1828", {"start": v(9.43, 120.74) * mm, "end": v(9.44, 120.82) * mm});
            skLineSegment(sketch, "E1829", {"start": v(9.44, 120.82) * mm, "end": v(9.43, 121.44) * mm});
            skLineSegment(sketch, "E1830", {"start": v(9.43, 121.44) * mm, "end": v(9.3, 122.2) * mm});
            skLineSegment(sketch, "E1831", {"start": v(9.3, 122.2) * mm, "end": v(9.26, 122.36) * mm});
            skLineSegment(sketch, "E1832", {"start": v(9.26, 122.36) * mm, "end": v(9.23, 122.47) * mm});
            skLineSegment(sketch, "E1833", {"start": v(9.23, 122.47) * mm, "end": v(9.1, 122.81) * mm});
            skLineSegment(sketch, "E1834", {"start": v(9.1, 122.81) * mm, "end": v(8.97, 122.97) * mm});
            skLineSegment(sketch, "E1835", {"start": v(8.97, 122.97) * mm, "end": v(8.94, 122.99) * mm});
            skLineSegment(sketch, "E1836", {"start": v(8.94, 122.99) * mm, "end": v(8.91, 122.85) * mm});
            skLineSegment(sketch, "E1837", {"start": v(8.91, 122.85) * mm, "end": v(8.97, 122.46) * mm});
            skLineSegment(sketch, "E1838", {"start": v(8.97, 122.46) * mm, "end": v(8.97, 122.33) * mm});
            skLineSegment(sketch, "E1839", {"start": v(8.97, 122.33) * mm, "end": v(8.98, 122.22) * mm});
            skLineSegment(sketch, "E1840", {"start": v(8.98, 122.22) * mm, "end": v(8.94, 121.56) * mm});
            skLineSegment(sketch, "E1841", {"start": v(8.94, 121.56) * mm, "end": v(8.74, 120.85) * mm});
            skLineSegment(sketch, "E1842", {"start": v(8.74, 120.85) * mm, "end": v(8.68, 120.72) * mm});
            skLineSegment(sketch, "E1843", {"start": v(8.68, 120.72) * mm, "end": v(8.6, 120.58) * mm});
            skLineSegment(sketch, "E1844", {"start": v(8.6, 120.58) * mm, "end": v(8.24, 119.95) * mm});
            skLineSegment(sketch, "E1845", {"start": v(8.24, 119.95) * mm, "end": v(7.97, 119.44) * mm});
            skLineSegment(sketch, "E1846", {"start": v(7.97, 119.44) * mm, "end": v(7.94, 119.36) * mm});
            skLineSegment(sketch, "E1847", {"start": v(7.94, 119.36) * mm, "end": v(7.91, 119.28) * mm});
            skLineSegment(sketch, "E1848", {"start": v(7.91, 119.28) * mm, "end": v(7.9, 118.95) * mm});
            skLineSegment(sketch, "E1849", {"start": v(7.9, 118.95) * mm, "end": v(8.07, 118.74) * mm});
            skLineSegment(sketch, "E1850", {"start": v(8.07, 118.74) * mm, "end": v(8.13, 118.72) * mm});
            skLineSegment(sketch, "E1851", {"start": v(8.13, 118.72) * mm, "end": v(8.14, 118.72) * mm});
            skLineSegment(sketch, "E1852", {"start": v(8.14, 118.72) * mm, "end": v(8.2, 118.72) * mm});
            skLineSegment(sketch, "E1853", {"start": v(8.2, 118.72) * mm, "end": v(8.33, 118.58) * mm});
            skLineSegment(sketch, "E1854", {"start": v(8.33, 118.58) * mm, "end": v(8.34, 118.53) * mm});
            skLineSegment(sketch, "E1855", {"start": v(8.34, 118.53) * mm, "end": v(8.35, 118.47) * mm});
            skLineSegment(sketch, "E1856", {"start": v(8.35, 118.47) * mm, "end": v(8.34, 118.25) * mm});
            skLineSegment(sketch, "E1857", {"start": v(8.34, 118.25) * mm, "end": v(8.22, 117.84) * mm});
            skLineSegment(sketch, "E1858", {"start": v(8.22, 117.84) * mm, "end": v(7.9, 117.24) * mm});
            skLineSegment(sketch, "E1859", {"start": v(7.9, 117.24) * mm, "end": v(7.46, 116.63) * mm});
            skLineSegment(sketch, "E1860", {"start": v(7.46, 116.63) * mm, "end": v(7.3, 116.44) * mm});
            skLineSegment(sketch, "E1861", {"start": v(7.3, 116.44) * mm, "end": v(7.23, 116.36) * mm});
            skLineSegment(sketch, "E1862", {"start": v(7.23, 116.36) * mm, "end": v(6.71, 115.87) * mm});
            skLineSegment(sketch, "E1863", {"start": v(6.71, 115.87) * mm, "end": v(6.05, 115.34) * mm});
            skLineSegment(sketch, "E1864", {"start": v(6.05, 115.34) * mm, "end": v(5.91, 115.24) * mm});
            skLineSegment(sketch, "E1865", {"start": v(5.91, 115.24) * mm, "end": v(5.92, 115.2) * mm});
            skLineSegment(sketch, "E1866", {"start": v(5.92, 115.2) * mm, "end": v(5.94, 114.74) * mm});
            skLineSegment(sketch, "E1867", {"start": v(5.94, 114.74) * mm, "end": v(5.93, 114.68) * mm});
            skLineSegment(sketch, "E1868", {"start": v(5.93, 114.68) * mm, "end": v(5.93, 114.62) * mm});
            skLineSegment(sketch, "E1869", {"start": v(5.93, 114.62) * mm, "end": v(5.83, 114.25) * mm});
            skLineSegment(sketch, "E1870", {"start": v(5.83, 114.25) * mm, "end": v(5.7, 114) * mm});
            skLineSegment(sketch, "E1871", {"start": v(5.7, 114) * mm, "end": v(5.7, 113.98) * mm});
            skLineSegment(sketch, "E1872", {"start": v(5.7, 113.98) * mm, "end": v(5.68, 113.97) * mm});
            skLineSegment(sketch, "E1873", {"start": v(5.68, 113.97) * mm, "end": v(5.54, 113.88) * mm});
            skLineSegment(sketch, "E1874", {"start": v(5.54, 113.88) * mm, "end": v(5.52, 113.88) * mm});
            skLineSegment(sketch, "E1875", {"start": v(5.52, 113.88) * mm, "end": v(5.45, 113.83) * mm});
            skLineSegment(sketch, "E1876", {"start": v(5.45, 113.83) * mm, "end": v(5.31, 113.58) * mm});
            skLineSegment(sketch, "E1877", {"start": v(5.31, 113.58) * mm, "end": v(5.33, 113.24) * mm});
            skLineSegment(sketch, "E1878", {"start": v(5.33, 113.24) * mm, "end": v(5.45, 112.96) * mm});
            skLineSegment(sketch, "E1879", {"start": v(5.45, 112.96) * mm, "end": v(5.52, 112.84) * mm});
            skLineSegment(sketch, "E1880", {"start": v(5.52, 112.84) * mm, "end": v(5.6, 112.9) * mm});
            skLineSegment(sketch, "E1881", {"start": v(5.6, 112.9) * mm, "end": v(5.88, 113.06) * mm});
            skLineSegment(sketch, "E1882", {"start": v(5.88, 113.06) * mm, "end": v(6.41, 113.4) * mm});
            skLineSegment(sketch, "E1883", {"start": v(6.41, 113.4) * mm, "end": v(7.03, 113.79) * mm});
            skLineSegment(sketch, "E1884", {"start": v(7.03, 113.79) * mm, "end": v(7.24, 113.92) * mm});
            skLineSegment(sketch, "E1885", {"start": v(7.24, 113.92) * mm, "end": v(7.4, 114.03) * mm});
            skLineSegment(sketch, "E1886", {"start": v(7.4, 114.03) * mm, "end": v(7.84, 114.47) * mm});
            skLineSegment(sketch, "E1887", {"start": v(7.84, 114.47) * mm, "end": v(8.26, 115.14) * mm});
            skLineSegment(sketch, "E1888", {"start": v(8.26, 115.14) * mm, "end": v(8.54, 115.85) * mm});
            skLineSegment(sketch, "E1889", {"start": v(8.54, 115.85) * mm, "end": v(8.7, 116.35) * mm});
            skLineSegment(sketch, "E1890", {"start": v(8.7, 116.35) * mm, "end": v(8.76, 116.52) * mm});
            skLineSegment(sketch, "E1891", {"start": v(-2.16, 133.25) * mm, "end": v(-2.03, 133.4) * mm});
            skLineSegment(sketch, "E1892", {"start": v(-2.03, 133.4) * mm, "end": v(-1.33, 134.07) * mm});
            skLineSegment(sketch, "E1893", {"start": v(-1.33, 134.07) * mm, "end": v(-0.73, 134.58) * mm});
            skLineSegment(sketch, "E1894", {"start": v(-0.73, 134.58) * mm, "end": v(-0.65, 134.63) * mm});
            skLineSegment(sketch, "E1895", {"start": v(-0.65, 134.63) * mm, "end": v(-0.6, 134.66) * mm});
            skLineSegment(sketch, "E1896", {"start": v(-0.6, 134.66) * mm, "end": v(-0.5, 134.8) * mm});
            skLineSegment(sketch, "E1897", {"start": v(-0.5, 134.8) * mm, "end": v(-0.75, 134.78) * mm});
            skLineSegment(sketch, "E1898", {"start": v(-0.75, 134.78) * mm, "end": v(-1.34, 134.5) * mm});
            skLineSegment(sketch, "E1899", {"start": v(-1.34, 134.5) * mm, "end": v(-2.06, 134.07) * mm});
            skLineSegment(sketch, "E1900", {"start": v(-2.06, 134.07) * mm, "end": v(-2.3, 133.91) * mm});
            skLineSegment(sketch, "E1901", {"start": v(-2.3, 133.91) * mm, "end": v(-2.41, 133.83) * mm});
            skLineSegment(sketch, "E1902", {"start": v(-2.41, 133.83) * mm, "end": v(-3.1, 133.26) * mm});
            skLineSegment(sketch, "E1903", {"start": v(-3.1, 133.26) * mm, "end": v(-3.9, 132.38) * mm});
            skLineSegment(sketch, "E1904", {"start": v(-3.9, 132.38) * mm, "end": v(-4.06, 132.13) * mm});
            skLineSegment(sketch, "E1905", {"start": v(-4.06, 132.13) * mm, "end": v(-4.32, 131.77) * mm});
            skLineSegment(sketch, "E1906", {"start": v(-4.32, 131.77) * mm, "end": v(-5.04, 130.65) * mm});
            skLineSegment(sketch, "E1907", {"start": v(-5.04, 130.65) * mm, "end": v(-5.92, 129.09) * mm});
            skLineSegment(sketch, "E1908", {"start": v(-5.92, 129.09) * mm, "end": v(-6.65, 127.67) * mm});
            skLineSegment(sketch, "E1909", {"start": v(-6.65, 127.67) * mm, "end": v(-7.03, 126.89) * mm});
            skLineSegment(sketch, "E1910", {"start": v(-7.03, 126.89) * mm, "end": v(-7.16, 126.63) * mm});
            skLineSegment(sketch, "E1911", {"start": v(-7.16, 126.63) * mm, "end": v(-7.26, 126.42) * mm});
            skLineSegment(sketch, "E1912", {"start": v(-7.26, 126.42) * mm, "end": v(-7.96, 125.25) * mm});
            skLineSegment(sketch, "E1913", {"start": v(-7.96, 125.25) * mm, "end": v(-8.85, 124.14) * mm});
            skLineSegment(sketch, "E1914", {"start": v(-8.85, 124.14) * mm, "end": v(-9.05, 123.96) * mm});
            skLineSegment(sketch, "E1915", {"start": v(-9.05, 123.96) * mm, "end": v(-9.28, 123.76) * mm});
            skLineSegment(sketch, "E1916", {"start": v(-9.28, 123.76) * mm, "end": v(-10.38, 123.07) * mm});
            skLineSegment(sketch, "E1917", {"start": v(-10.38, 123.07) * mm, "end": v(-11.29, 122.54) * mm});
            skLineSegment(sketch, "E1918", {"start": v(-11.29, 122.54) * mm, "end": v(-11.42, 122.43) * mm});
            skLineSegment(sketch, "E1919", {"start": v(-11.42, 122.43) * mm, "end": v(-11.43, 122.41) * mm});
            skLineSegment(sketch, "E1920", {"start": v(-11.43, 122.41) * mm, "end": v(-11.58, 122.27) * mm});
            skLineSegment(sketch, "E1921", {"start": v(-11.58, 122.27) * mm, "end": v(-11.6, 122.26) * mm});
            skLineSegment(sketch, "E1922", {"start": v(-11.6, 122.26) * mm, "end": v(-11.6, 122.25) * mm});
            skLineSegment(sketch, "E1923", {"start": v(-11.6, 122.25) * mm, "end": v(-11.74, 122.08) * mm});
            skLineSegment(sketch, "E1924", {"start": v(-11.74, 122.08) * mm, "end": v(-11.76, 122.06) * mm});
            skLineSegment(sketch, "E1925", {"start": v(-11.76, 122.06) * mm, "end": v(-11.77, 122.04) * mm});
            skLineSegment(sketch, "E1926", {"start": v(-11.77, 122.04) * mm, "end": v(-11.83, 121.86) * mm});
            skLineSegment(sketch, "E1927", {"start": v(-11.83, 121.86) * mm, "end": v(-11.85, 121.66) * mm});
            skLineSegment(sketch, "E1928", {"start": v(-11.85, 121.66) * mm, "end": v(-11.84, 121.62) * mm});
            skLineSegment(sketch, "E1929", {"start": v(-11.84, 121.62) * mm, "end": v(-11.84, 121.56) * mm});
            skLineSegment(sketch, "E1930", {"start": v(-11.84, 121.56) * mm, "end": v(-11.85, 121.23) * mm});
            skLineSegment(sketch, "E1931", {"start": v(-11.85, 121.23) * mm, "end": v(-11.98, 120.9) * mm});
            skLineSegment(sketch, "E1932", {"start": v(-11.98, 120.9) * mm, "end": v(-12.03, 120.84) * mm});
            skLineSegment(sketch, "E1933", {"start": v(-12.03, 120.84) * mm, "end": v(-12.05, 120.8) * mm});
            skLineSegment(sketch, "E1934", {"start": v(-12.05, 120.8) * mm, "end": v(-12.34, 120.6) * mm});
            skLineSegment(sketch, "E1935", {"start": v(-12.34, 120.6) * mm, "end": v(-12.9, 120.33) * mm});
            skLineSegment(sketch, "E1936", {"start": v(-12.9, 120.33) * mm, "end": v(-13.05, 120.27) * mm});
            skLineSegment(sketch, "E1937", {"start": v(-13.05, 120.27) * mm, "end": v(-13.09, 120.27) * mm});
            skLineSegment(sketch, "E1938", {"start": v(-13.09, 120.27) * mm, "end": v(-13.18, 120.25) * mm});
            skLineSegment(sketch, "E1939", {"start": v(-13.18, 120.25) * mm, "end": v(-13.2, 120.24) * mm});
            skLineSegment(sketch, "E1940", {"start": v(-13.2, 120.24) * mm, "end": v(-13.22, 120.23) * mm});
            skLineSegment(sketch, "E1941", {"start": v(-13.22, 120.23) * mm, "end": v(-13.46, 120.17) * mm});
            skLineSegment(sketch, "E1942", {"start": v(-13.46, 120.17) * mm, "end": v(-13.67, 120.1) * mm});
            skLineSegment(sketch, "E1943", {"start": v(-13.67, 120.1) * mm, "end": v(-13.68, 120.1) * mm});
            skLineSegment(sketch, "E1944", {"start": v(-13.68, 120.1) * mm, "end": v(-13.78, 120.09) * mm});
            skLineSegment(sketch, "E1945", {"start": v(-13.78, 120.09) * mm, "end": v(-14.12, 119.94) * mm});
            skLineSegment(sketch, "E1946", {"start": v(-14.12, 119.94) * mm, "end": v(-14.04, 119.7) * mm});
            skLineSegment(sketch, "E1947", {"start": v(-14.04, 119.7) * mm, "end": v(-14, 119.68) * mm});
            skLineSegment(sketch, "E1948", {"start": v(-14, 119.68) * mm, "end": v(-13.96, 119.66) * mm});
            skLineSegment(sketch, "E1949", {"start": v(-13.96, 119.66) * mm, "end": v(-13.64, 119.53) * mm});
            skLineSegment(sketch, "E1950", {"start": v(-13.64, 119.53) * mm, "end": v(-13.59, 119.52) * mm});
            skLineSegment(sketch, "E1951", {"start": v(-13.59, 119.52) * mm, "end": v(-13.5, 119.5) * mm});
            skLineSegment(sketch, "E1952", {"start": v(-13.5, 119.5) * mm, "end": v(-13.26, 119.39) * mm});
            skLineSegment(sketch, "E1953", {"start": v(-13.26, 119.39) * mm, "end": v(-13.18, 119.27) * mm});
            skLineSegment(sketch, "E1954", {"start": v(-13.18, 119.27) * mm, "end": v(-13.18, 119.23) * mm});
            skLineSegment(sketch, "E1955", {"start": v(-13.18, 119.23) * mm, "end": v(-13.18, 119.14) * mm});
            skLineSegment(sketch, "E1956", {"start": v(-13.18, 119.14) * mm, "end": v(-13.4, 118.88) * mm});
            skLineSegment(sketch, "E1957", {"start": v(-13.4, 118.88) * mm, "end": v(-14, 118.53) * mm});
            skLineSegment(sketch, "E1958", {"start": v(-14, 118.53) * mm, "end": v(-14.2, 118.46) * mm});
            skLineSegment(sketch, "E1959", {"start": v(-14.2, 118.46) * mm, "end": v(-14.46, 118.38) * mm});
            skLineSegment(sketch, "E1960", {"start": v(-14.46, 118.38) * mm, "end": v(-15.25, 118.24) * mm});
            skLineSegment(sketch, "E1961", {"start": v(-15.25, 118.24) * mm, "end": v(-16.27, 118.14) * mm});
            skLineSegment(sketch, "E1962", {"start": v(-16.27, 118.14) * mm, "end": v(-17.05, 118.12) * mm});
            skLineSegment(sketch, "E1963", {"start": v(-17.05, 118.12) * mm, "end": v(-17.36, 118.12) * mm});
            skLineSegment(sketch, "E1964", {"start": v(-17.36, 118.12) * mm, "end": v(-17.59, 118.13) * mm});
            skLineSegment(sketch, "E1965", {"start": v(-17.59, 118.13) * mm, "end": v(-18.4, 118.17) * mm});
            skLineSegment(sketch, "E1966", {"start": v(-18.4, 118.17) * mm, "end": v(-18.83, 118.15) * mm});
            skLineSegment(sketch, "E1967", {"start": v(-18.83, 118.15) * mm, "end": v(-18.87, 118.13) * mm});
            skLineSegment(sketch, "E1968", {"start": v(-18.87, 118.13) * mm, "end": v(-18.89, 118.12) * mm});
            skLineSegment(sketch, "E1969", {"start": v(-18.89, 118.12) * mm, "end": v(-18.88, 117.97) * mm});
            skLineSegment(sketch, "E1970", {"start": v(-18.88, 117.97) * mm, "end": v(-18.52, 117.77) * mm});
            skLineSegment(sketch, "E1971", {"start": v(-18.52, 117.77) * mm, "end": v(-18.39, 117.73) * mm});
            skLineSegment(sketch, "E1972", {"start": v(-18.39, 117.73) * mm, "end": v(-18.3, 117.7) * mm});
            skLineSegment(sketch, "E1973", {"start": v(-18.3, 117.7) * mm, "end": v(-17.68, 117.56) * mm});
            skLineSegment(sketch, "E1974", {"start": v(-17.68, 117.56) * mm, "end": v(-17.03, 117.4) * mm});
            skLineSegment(sketch, "E1975", {"start": v(-17.03, 117.4) * mm, "end": v(-16.93, 117.37) * mm});
            skLineSegment(sketch, "E1976", {"start": v(-16.93, 117.37) * mm, "end": v(-16.9, 117.35) * mm});
            skLineSegment(sketch, "E1977", {"start": v(-16.9, 117.35) * mm, "end": v(-16.82, 117.2) * mm});
            skLineSegment(sketch, "E1978", {"start": v(-16.82, 117.2) * mm, "end": v(-17, 117.09) * mm});
            skLineSegment(sketch, "E1979", {"start": v(-17, 117.09) * mm, "end": v(-17.06, 117.08) * mm});
            skLineSegment(sketch, "E1980", {"start": v(-17.06, 117.08) * mm, "end": v(-17.17, 117.06) * mm});
            skLineSegment(sketch, "E1981", {"start": v(-17.17, 117.06) * mm, "end": v(-17.52, 117.04) * mm});
            skLineSegment(sketch, "E1982", {"start": v(-17.52, 117.04) * mm, "end": v(-18.17, 117.05) * mm});
            skLineSegment(sketch, "E1983", {"start": v(-18.17, 117.05) * mm, "end": v(-18.87, 117.12) * mm});
            skLineSegment(sketch, "E1984", {"start": v(-18.87, 117.12) * mm, "end": v(-19.35, 117.21) * mm});
            skLineSegment(sketch, "E1985", {"start": v(-19.35, 117.21) * mm, "end": v(-19.5, 117.26) * mm});
            skLineSegment(sketch, "E1986", {"start": v(-19.5, 117.26) * mm, "end": v(-19.66, 117.31) * mm});
            skLineSegment(sketch, "E1987", {"start": v(-19.66, 117.31) * mm, "end": v(-19.88, 117.4) * mm});
            skLineSegment(sketch, "E1988", {"start": v(-19.88, 117.4) * mm, "end": v(-19.91, 117.41) * mm});
            skLineSegment(sketch, "E1989", {"start": v(-19.91, 117.41) * mm, "end": v(-20.01, 117.47) * mm});
            skLineSegment(sketch, "E1990", {"start": v(-20.01, 117.47) * mm, "end": v(-20.43, 117.78) * mm});
            skLineSegment(sketch, "E1991", {"start": v(-20.43, 117.78) * mm, "end": v(-20.71, 118.1) * mm});
            skLineSegment(sketch, "E1992", {"start": v(-20.71, 118.1) * mm, "end": v(-20.75, 118.15) * mm});
            skLineSegment(sketch, "E1993", {"start": v(-20.75, 118.15) * mm, "end": v(-20.77, 118.18) * mm});
            skLineSegment(sketch, "E1994", {"start": v(-20.77, 118.18) * mm, "end": v(-20.84, 118.41) * mm});
            skLineSegment(sketch, "E1995", {"start": v(-20.84, 118.41) * mm, "end": v(-20.93, 118.6) * mm});
            skLineSegment(sketch, "E1996", {"start": v(-20.93, 118.6) * mm, "end": v(-20.95, 118.61) * mm});
            skLineSegment(sketch, "E1997", {"start": v(-20.95, 118.61) * mm, "end": v(-21.56, 117.78) * mm});
            skLineSegment(sketch, "E1998", {"start": v(-21.56, 117.78) * mm, "end": v(-21.55, 117.59) * mm});
            skLineSegment(sketch, "E1999", {"start": v(-21.55, 117.59) * mm, "end": v(-21.32, 117.11) * mm});
            skLineSegment(sketch, "E2000", {"start": v(-21.32, 117.11) * mm, "end": v(-21.21, 116.97) * mm});
            skLineSegment(sketch, "E2001", {"start": v(-21.21, 116.97) * mm, "end": v(-21.2, 116.99) * mm});
            skLineSegment(sketch, "E2002", {"start": v(-21.2, 116.99) * mm, "end": v(-21.1, 117.25) * mm});
            skLineSegment(sketch, "E2003", {"start": v(-21.1, 117.25) * mm, "end": v(-21.07, 117.27) * mm});
            skLineSegment(sketch, "E2004", {"start": v(-21.07, 117.27) * mm, "end": v(-21.06, 117.31) * mm});
            skLineSegment(sketch, "E2005", {"start": v(-21.06, 117.31) * mm, "end": v(-20.91, 117.44) * mm});
            skLineSegment(sketch, "E2006", {"start": v(-20.91, 117.44) * mm, "end": v(-20.74, 117.39) * mm});
            skLineSegment(sketch, "E2007", {"start": v(-20.74, 117.39) * mm, "end": v(-20.71, 117.35) * mm});
            skLineSegment(sketch, "E2008", {"start": v(-20.71, 117.35) * mm, "end": v(-20.69, 117.31) * mm});
            skLineSegment(sketch, "E2009", {"start": v(-20.69, 117.31) * mm, "end": v(-20.66, 116.86) * mm});
            skLineSegment(sketch, "E2010", {"start": v(-20.66, 116.86) * mm, "end": v(-20.68, 116.82) * mm});
            skLineSegment(sketch, "E2011", {"start": v(-20.68, 116.82) * mm, "end": v(-20.7, 116.8) * mm});
            skLineSegment(sketch, "E2012", {"start": v(-20.7, 116.8) * mm, "end": v(-20.76, 116.62) * mm});
            skLineSegment(sketch, "E2013", {"start": v(-20.76, 116.62) * mm, "end": v(-20.76, 116.57) * mm});
            skLineSegment(sketch, "E2014", {"start": v(-20.76, 116.57) * mm, "end": v(-20.75, 116.52) * mm});
            skLineSegment(sketch, "E2015", {"start": v(-20.75, 116.52) * mm, "end": v(-20.67, 116.46) * mm});
            skLineSegment(sketch, "E2016", {"start": v(-20.67, 116.46) * mm, "end": v(-20.17, 116.17) * mm});
            skLineSegment(sketch, "E2017", {"start": v(-20.17, 116.17) * mm, "end": v(-19.48, 115.93) * mm});
            skLineSegment(sketch, "E2018", {"start": v(-19.48, 115.93) * mm, "end": v(-19.31, 115.9) * mm});
            skLineSegment(sketch, "E2019", {"start": v(-19.31, 115.9) * mm, "end": v(-19.01, 115.84) * mm});
            skLineSegment(sketch, "E2020", {"start": v(-19.01, 115.84) * mm, "end": v(-18.1, 115.76) * mm});
            skLineSegment(sketch, "E2021", {"start": v(-18.1, 115.76) * mm, "end": v(-17.17, 115.78) * mm});
            skLineSegment(sketch, "E2022", {"start": v(-17.17, 115.78) * mm, "end": v(-16.5, 115.88) * mm});
            skLineSegment(sketch, "E2023", {"start": v(-16.5, 115.88) * mm, "end": v(-16.2, 115.94) * mm});
            skLineSegment(sketch, "E2024", {"start": v(-16.2, 115.94) * mm, "end": v(-16.12, 115.95) * mm});
            skLineSegment(sketch, "E2025", {"start": v(-16.12, 115.95) * mm, "end": v(-16.1, 115.97) * mm});
            skLineSegment(sketch, "E2026", {"start": v(-16.1, 115.97) * mm, "end": v(-15.82, 116.01) * mm});
            skLineSegment(sketch, "E2027", {"start": v(-15.82, 116.01) * mm, "end": v(-15.58, 116.01) * mm});
            skLineSegment(sketch, "E2028", {"start": v(-15.58, 116.01) * mm, "end": v(-15.57, 116) * mm});
            skLineSegment(sketch, "E2029", {"start": v(-15.57, 116) * mm, "end": v(-15.57, 115.97) * mm});
            skLineSegment(sketch, "E2030", {"start": v(-15.57, 115.97) * mm, "end": v(-15.68, 115.57) * mm});
            skLineSegment(sketch, "E2031", {"start": v(-15.68, 115.57) * mm, "end": v(-15.7, 115.53) * mm});
            skLineSegment(sketch, "E2032", {"start": v(-15.7, 115.53) * mm, "end": v(-15.71, 115.48) * mm});
            skLineSegment(sketch, "E2033", {"start": v(-15.71, 115.48) * mm, "end": v(-15.87, 115.15) * mm});
            skLineSegment(sketch, "E2034", {"start": v(-15.87, 115.15) * mm, "end": v(-15.88, 115.12) * mm});
            skLineSegment(sketch, "E2035", {"start": v(-15.88, 115.12) * mm, "end": v(-15.89, 115.09) * mm});
            skLineSegment(sketch, "E2036", {"start": v(-15.89, 115.09) * mm, "end": v(-15.88, 115) * mm});
            skLineSegment(sketch, "E2037", {"start": v(-15.88, 115) * mm, "end": v(-15.84, 114.98) * mm});
            skLineSegment(sketch, "E2038", {"start": v(-15.84, 114.98) * mm, "end": v(-15.8, 115) * mm});
            skLineSegment(sketch, "E2039", {"start": v(-15.8, 115) * mm, "end": v(-15.42, 115.31) * mm});
            skLineSegment(sketch, "E2040", {"start": v(-15.42, 115.31) * mm, "end": v(-15.38, 115.35) * mm});
            skLineSegment(sketch, "E2041", {"start": v(-15.38, 115.35) * mm, "end": v(-15.34, 115.4) * mm});
            skLineSegment(sketch, "E2042", {"start": v(-15.34, 115.4) * mm, "end": v(-14.98, 115.72) * mm});
            skLineSegment(sketch, "E2043", {"start": v(-14.98, 115.72) * mm, "end": v(-14.63, 116.04) * mm});
            skLineSegment(sketch, "E2044", {"start": v(-14.63, 116.04) * mm, "end": v(-14.6, 116.07) * mm});
            skLineSegment(sketch, "E2045", {"start": v(-14.6, 116.07) * mm, "end": v(-14.5, 116.17) * mm});
            skLineSegment(sketch, "E2046", {"start": v(-14.5, 116.17) * mm, "end": v(-14.12, 116.55) * mm});
            skLineSegment(sketch, "E2047", {"start": v(-14.12, 116.55) * mm, "end": v(-13.98, 116.82) * mm});
            skLineSegment(sketch, "E2048", {"start": v(-13.98, 116.82) * mm, "end": v(-14, 116.86) * mm});
            skLineSegment(sketch, "E2049", {"start": v(-14, 116.86) * mm, "end": v(-14, 116.87) * mm});
            skLineSegment(sketch, "E2050", {"start": v(-14, 116.87) * mm, "end": v(-14.05, 117.11) * mm});
            skLineSegment(sketch, "E2051", {"start": v(-14.05, 117.11) * mm, "end": v(-14.05, 117.2) * mm});
            skLineSegment(sketch, "E2052", {"start": v(-14.05, 117.2) * mm, "end": v(-14.06, 117.26) * mm});
            skLineSegment(sketch, "E2053", {"start": v(-14.06, 117.26) * mm, "end": v(-13.94, 117.61) * mm});
            skLineSegment(sketch, "E2054", {"start": v(-13.94, 117.61) * mm, "end": v(-13.59, 117.98) * mm});
            skLineSegment(sketch, "E2055", {"start": v(-13.59, 117.98) * mm, "end": v(-13.48, 118.07) * mm});
            skLineSegment(sketch, "E2056", {"start": v(-13.48, 118.07) * mm, "end": v(-13.37, 118.15) * mm});
            skLineSegment(sketch, "E2057", {"start": v(-13.37, 118.15) * mm, "end": v(-12.8, 118.46) * mm});
            skLineSegment(sketch, "E2058", {"start": v(-12.8, 118.46) * mm, "end": v(-12.25, 118.83) * mm});
            skLineSegment(sketch, "E2059", {"start": v(-12.25, 118.83) * mm, "end": v(-12.15, 118.94) * mm});
            skLineSegment(sketch, "E2060", {"start": v(-12.15, 118.94) * mm, "end": v(-12.04, 119.04) * mm});
            skLineSegment(sketch, "E2061", {"start": v(-12.04, 119.04) * mm, "end": v(-11.88, 119.61) * mm});
            skLineSegment(sketch, "E2062", {"start": v(-11.88, 119.61) * mm, "end": v(-11.75, 120.17) * mm});
            skLineSegment(sketch, "E2063", {"start": v(-11.75, 120.17) * mm, "end": v(-11.66, 120.27) * mm});
            skLineSegment(sketch, "E2064", {"start": v(-11.66, 120.27) * mm, "end": v(-11.56, 120.38) * mm});
            skLineSegment(sketch, "E2065", {"start": v(-11.56, 120.38) * mm, "end": v(-11, 120.78) * mm});
            skLineSegment(sketch, "E2066", {"start": v(-11, 120.78) * mm, "end": v(-10.5, 121.11) * mm});
            skLineSegment(sketch, "E2067", {"start": v(-10.5, 121.11) * mm, "end": v(-10.45, 121.19) * mm});
            skLineSegment(sketch, "E2068", {"start": v(-10.45, 121.19) * mm, "end": v(-10.37, 121.3) * mm});
            skLineSegment(sketch, "E2069", {"start": v(-10.37, 121.3) * mm, "end": v(-10.12, 121.72) * mm});
            skLineSegment(sketch, "E2070", {"start": v(-10.12, 121.72) * mm, "end": v(-9.87, 122.18) * mm});
            skLineSegment(sketch, "E2071", {"start": v(-9.87, 122.18) * mm, "end": v(-9.8, 122.3) * mm});
            skLineSegment(sketch, "E2072", {"start": v(-9.8, 122.3) * mm, "end": v(-9.73, 122.4) * mm});
            skLineSegment(sketch, "E2073", {"start": v(-9.73, 122.4) * mm, "end": v(-9.48, 122.72) * mm});
            skLineSegment(sketch, "E2074", {"start": v(-9.48, 122.72) * mm, "end": v(-8.96, 123.3) * mm});
            skLineSegment(sketch, "E2075", {"start": v(-8.96, 123.3) * mm, "end": v(-8.37, 123.92) * mm});
            skLineSegment(sketch, "E2076", {"start": v(-8.37, 123.92) * mm, "end": v(-7.96, 124.34) * mm});
            skLineSegment(sketch, "E2077", {"start": v(-7.96, 124.34) * mm, "end": v(-7.82, 124.48) * mm});
            skLineSegment(sketch, "E2078", {"start": v(-7.82, 124.48) * mm, "end": v(-7.62, 124.71) * mm});
            skLineSegment(sketch, "E2079", {"start": v(-7.62, 124.71) * mm, "end": v(-7.06, 125.46) * mm});
            skLineSegment(sketch, "E2080", {"start": v(-7.06, 125.46) * mm, "end": v(-6.46, 126.46) * mm});
            skLineSegment(sketch, "E2081", {"start": v(-6.46, 126.46) * mm, "end": v(-5.88, 127.55) * mm});
            skLineSegment(sketch, "E2082", {"start": v(-5.88, 127.55) * mm, "end": v(-5.37, 128.5) * mm});
            skLineSegment(sketch, "E2083", {"start": v(-5.37, 128.5) * mm, "end": v(-5.2, 128.8) * mm});
            skLineSegment(sketch, "E2084", {"start": v(-5.2, 128.8) * mm, "end": v(-4.9, 129.3) * mm});
            skLineSegment(sketch, "E2085", {"start": v(-4.9, 129.3) * mm, "end": v(-3.57, 131.42) * mm});
            skLineSegment(sketch, "E2086", {"start": v(-3.57, 131.42) * mm, "end": v(-2.38, 133.02) * mm});
            skLineSegment(sketch, "E2087", {"start": v(-2.38, 133.02) * mm, "end": v(-2.16, 133.25) * mm});
            skLineSegment(sketch, "E2088", {"start": v(-16.65, 114.53) * mm, "end": v(-16.96, 114.5) * mm});
            skLineSegment(sketch, "E2089", {"start": v(-16.96, 114.5) * mm, "end": v(-17.73, 114.46) * mm});
            skLineSegment(sketch, "E2090", {"start": v(-17.73, 114.46) * mm, "end": v(-18.69, 114.45) * mm});
            skLineSegment(sketch, "E2091", {"start": v(-18.69, 114.45) * mm, "end": v(-19.37, 114.48) * mm});
            skLineSegment(sketch, "E2092", {"start": v(-19.37, 114.48) * mm, "end": v(-19.59, 114.51) * mm});
            skLineSegment(sketch, "E2093", {"start": v(-19.59, 114.51) * mm, "end": v(-19.78, 114.55) * mm});
            skLineSegment(sketch, "E2094", {"start": v(-19.78, 114.55) * mm, "end": v(-20.63, 114.75) * mm});
            skLineSegment(sketch, "E2095", {"start": v(-20.63, 114.75) * mm, "end": v(-21.18, 114.94) * mm});
            skLineSegment(sketch, "E2096", {"start": v(-21.18, 114.94) * mm, "end": v(-21.22, 114.96) * mm});
            skLineSegment(sketch, "E2097", {"start": v(-21.22, 114.96) * mm, "end": v(-21.28, 114.98) * mm});
            skLineSegment(sketch, "E2098", {"start": v(-21.28, 114.98) * mm, "end": v(-21.48, 115.03) * mm});
            skLineSegment(sketch, "E2099", {"start": v(-21.48, 115.03) * mm, "end": v(-21.68, 114.86) * mm});
            skLineSegment(sketch, "E2100", {"start": v(-21.68, 114.86) * mm, "end": v(-21.7, 114.79) * mm});
            skLineSegment(sketch, "E2101", {"start": v(-21.7, 114.79) * mm, "end": v(-21.76, 114.7) * mm});
            skLineSegment(sketch, "E2102", {"start": v(-21.76, 114.7) * mm, "end": v(-22.03, 114.21) * mm});
            skLineSegment(sketch, "E2103", {"start": v(-22.03, 114.21) * mm, "end": v(-22.57, 113.24) * mm});
            skLineSegment(sketch, "E2104", {"start": v(-22.57, 113.24) * mm, "end": v(-23.15, 112.16) * mm});
            skLineSegment(sketch, "E2105", {"start": v(-23.15, 112.16) * mm, "end": v(-23.5, 111.48) * mm});
            skLineSegment(sketch, "E2106", {"start": v(-23.5, 111.48) * mm, "end": v(-23.6, 111.24) * mm});
            skLineSegment(sketch, "E2107", {"start": v(-23.6, 111.24) * mm, "end": v(-23.68, 111.02) * mm});
            skLineSegment(sketch, "E2108", {"start": v(-23.68, 111.02) * mm, "end": v(-23.95, 110.36) * mm});
            skLineSegment(sketch, "E2109", {"start": v(-23.95, 110.36) * mm, "end": v(-24.35, 109.34) * mm});
            skLineSegment(sketch, "E2110", {"start": v(-24.35, 109.34) * mm, "end": v(-24.7, 108.4) * mm});
            skLineSegment(sketch, "E2111", {"start": v(-24.7, 108.4) * mm, "end": v(-24.87, 107.88) * mm});
            skLineSegment(sketch, "E2112", {"start": v(-24.87, 107.88) * mm, "end": v(-24.91, 107.72) * mm});
            skLineSegment(sketch, "E2113", {"start": v(-24.91, 107.72) * mm, "end": v(-24.95, 107.6) * mm});
            skLineSegment(sketch, "E2114", {"start": v(-24.95, 107.6) * mm, "end": v(-25.06, 107.21) * mm});
            skLineSegment(sketch, "E2115", {"start": v(-25.06, 107.21) * mm, "end": v(-25.2, 106.87) * mm});
            skLineSegment(sketch, "E2116", {"start": v(-25.2, 106.87) * mm, "end": v(-25.29, 106.98) * mm});
            skLineSegment(sketch, "E2117", {"start": v(-25.29, 106.98) * mm, "end": v(-25.26, 107.63) * mm});
            skLineSegment(sketch, "E2118", {"start": v(-25.26, 107.63) * mm, "end": v(-25.23, 107.84) * mm});
            skLineSegment(sketch, "E2119", {"start": v(-25.23, 107.84) * mm, "end": v(-25.2, 108.22) * mm});
            skLineSegment(sketch, "E2120", {"start": v(-25.2, 108.22) * mm, "end": v(-24.92, 109.33) * mm});
            skLineSegment(sketch, "E2121", {"start": v(-24.92, 109.33) * mm, "end": v(-24.4, 110.94) * mm});
            skLineSegment(sketch, "E2122", {"start": v(-24.4, 110.94) * mm, "end": v(-23.85, 112.34) * mm});
            skLineSegment(sketch, "E2123", {"start": v(-23.85, 112.34) * mm, "end": v(-23.56, 113.05) * mm});
            skLineSegment(sketch, "E2124", {"start": v(-23.56, 113.05) * mm, "end": v(-23.48, 113.2) * mm});
            skLineSegment(sketch, "E2125", {"start": v(-23.48, 113.2) * mm, "end": v(-23.39, 113.41) * mm});
            skLineSegment(sketch, "E2126", {"start": v(-23.39, 113.41) * mm, "end": v(-23.07, 114.01) * mm});
            skLineSegment(sketch, "E2127", {"start": v(-23.07, 114.01) * mm, "end": v(-22.72, 114.57) * mm});
            skLineSegment(sketch, "E2128", {"start": v(-22.72, 114.57) * mm, "end": v(-22.43, 114.98) * mm});
            skLineSegment(sketch, "E2129", {"start": v(-22.43, 114.98) * mm, "end": v(-22.26, 115.24) * mm});
            skLineSegment(sketch, "E2130", {"start": v(-22.26, 115.24) * mm, "end": v(-22.21, 115.32) * mm});
            skLineSegment(sketch, "E2131", {"start": v(-22.21, 115.32) * mm, "end": v(-22.2, 115.35) * mm});
            skLineSegment(sketch, "E2132", {"start": v(-22.2, 115.35) * mm, "end": v(-22.34, 115.56) * mm});
            skLineSegment(sketch, "E2133", {"start": v(-22.34, 115.56) * mm, "end": v(-22.55, 115.72) * mm});
            skLineSegment(sketch, "E2134", {"start": v(-22.55, 115.72) * mm, "end": v(-22.57, 115.74) * mm});
            skLineSegment(sketch, "E2135", {"start": v(-22.57, 115.74) * mm, "end": v(-22.58, 115.75) * mm});
            skLineSegment(sketch, "E2136", {"start": v(-22.58, 115.75) * mm, "end": v(-22.79, 115.96) * mm});
            skLineSegment(sketch, "E2137", {"start": v(-22.79, 115.96) * mm, "end": v(-22.8, 116) * mm});
            skLineSegment(sketch, "E2138", {"start": v(-22.8, 116) * mm, "end": v(-22.83, 116.03) * mm});
            skLineSegment(sketch, "E2139", {"start": v(-22.83, 116.03) * mm, "end": v(-22.89, 116.23) * mm});
            skLineSegment(sketch, "E2140", {"start": v(-22.89, 116.23) * mm, "end": v(-22.99, 116.22) * mm});
            skLineSegment(sketch, "E2141", {"start": v(-22.99, 116.22) * mm, "end": v(-23, 116.2) * mm});
            skLineSegment(sketch, "E2142", {"start": v(-23, 116.2) * mm, "end": v(-23.1, 116.07) * mm});
            skLineSegment(sketch, "E2143", {"start": v(-23.1, 116.07) * mm, "end": v(-23.4, 115.63) * mm});
            skLineSegment(sketch, "E2144", {"start": v(-23.4, 115.63) * mm, "end": v(-23.86, 114.84) * mm});
            skLineSegment(sketch, "E2145", {"start": v(-23.86, 114.84) * mm, "end": v(-24.33, 113.92) * mm});
            skLineSegment(sketch, "E2146", {"start": v(-24.33, 113.92) * mm, "end": v(-24.65, 113.2) * mm});
            skLineSegment(sketch, "E2147", {"start": v(-24.65, 113.2) * mm, "end": v(-24.74, 112.95) * mm});
            skLineSegment(sketch, "E2148", {"start": v(-24.74, 112.95) * mm, "end": v(-24.82, 112.73) * mm});
            skLineSegment(sketch, "E2149", {"start": v(-24.82, 112.73) * mm, "end": v(-25.04, 112.03) * mm});
            skLineSegment(sketch, "E2150", {"start": v(-25.04, 112.03) * mm, "end": v(-25.4, 110.86) * mm});
            skLineSegment(sketch, "E2151", {"start": v(-25.4, 110.86) * mm, "end": v(-25.73, 109.64) * mm});
            skLineSegment(sketch, "E2152", {"start": v(-25.73, 109.64) * mm, "end": v(-25.93, 108.88) * mm});
            skLineSegment(sketch, "E2153", {"start": v(-25.93, 108.88) * mm, "end": v(-25.99, 108.63) * mm});
            skLineSegment(sketch, "E2154", {"start": v(-25.99, 108.63) * mm, "end": v(-26.03, 108.43) * mm});
            skLineSegment(sketch, "E2155", {"start": v(-26.03, 108.43) * mm, "end": v(-26.23, 107.62) * mm});
            skLineSegment(sketch, "E2156", {"start": v(-26.23, 107.62) * mm, "end": v(-26.42, 107.02) * mm});
            skLineSegment(sketch, "E2157", {"start": v(-26.42, 107.02) * mm, "end": v(-26.45, 106.92) * mm});
            skLineSegment(sketch, "E2158", {"start": v(-26.45, 106.92) * mm, "end": v(-26.48, 106.86) * mm});
            skLineSegment(sketch, "E2159", {"start": v(-26.48, 106.86) * mm, "end": v(-26.78, 106.29) * mm});
            skLineSegment(sketch, "E2160", {"start": v(-26.78, 106.29) * mm, "end": v(-26.8, 106.25) * mm});
            skLineSegment(sketch, "E2161", {"start": v(-26.8, 106.25) * mm, "end": v(-26.82, 106.24) * mm});
            skLineSegment(sketch, "E2162", {"start": v(-26.82, 106.24) * mm, "end": v(-27.1, 105.99) * mm});
            skLineSegment(sketch, "E2163", {"start": v(-27.1, 105.99) * mm, "end": v(-27.12, 105.96) * mm});
            skLineSegment(sketch, "E2164", {"start": v(-27.12, 105.96) * mm, "end": v(-27.13, 105.96) * mm});
            skLineSegment(sketch, "E2165", {"start": v(-27.13, 105.96) * mm, "end": v(-27.17, 105.94) * mm});
            skLineSegment(sketch, "E2166", {"start": v(-27.17, 105.94) * mm, "end": v(-27.09, 105.95) * mm});
            skLineSegment(sketch, "E2167", {"start": v(-27.09, 105.95) * mm, "end": v(-26.73, 105.94) * mm});
            skLineSegment(sketch, "E2168", {"start": v(-26.73, 105.94) * mm, "end": v(-26.5, 105.86) * mm});
            skLineSegment(sketch, "E2169", {"start": v(-26.5, 105.86) * mm, "end": v(-26.48, 105.84) * mm});
            skLineSegment(sketch, "E2170", {"start": v(-26.48, 105.84) * mm, "end": v(-26.45, 105.8) * mm});
            skLineSegment(sketch, "E2171", {"start": v(-26.45, 105.8) * mm, "end": v(-26.37, 105.63) * mm});
            skLineSegment(sketch, "E2172", {"start": v(-26.37, 105.63) * mm, "end": v(-26.57, 105.39) * mm});
            skLineSegment(sketch, "E2173", {"start": v(-26.57, 105.39) * mm, "end": v(-26.65, 105.34) * mm});
            skLineSegment(sketch, "E2174", {"start": v(-26.65, 105.34) * mm, "end": v(-26.7, 105.3) * mm});
            skLineSegment(sketch, "E2175", {"start": v(-26.7, 105.3) * mm, "end": v(-27.24, 104.73) * mm});
            skLineSegment(sketch, "E2176", {"start": v(-27.24, 104.73) * mm, "end": v(-27.3, 104.66) * mm});
            skLineSegment(sketch, "E2177", {"start": v(-27.3, 104.66) * mm, "end": v(-27.35, 104.6) * mm});
            skLineSegment(sketch, "E2178", {"start": v(-27.35, 104.6) * mm, "end": v(-27.66, 104.6) * mm});
            skLineSegment(sketch, "E2179", {"start": v(-27.66, 104.6) * mm, "end": v(-27.9, 104.85) * mm});
            skLineSegment(sketch, "E2180", {"start": v(-27.9, 104.85) * mm, "end": v(-27.92, 104.93) * mm});
            skLineSegment(sketch, "E2181", {"start": v(-27.92, 104.93) * mm, "end": v(-27.92, 104.94) * mm});
            skLineSegment(sketch, "E2182", {"start": v(-27.92, 104.94) * mm, "end": v(-27.95, 104.95) * mm});
            skLineSegment(sketch, "E2183", {"start": v(-27.95, 104.95) * mm, "end": v(-28, 104.82) * mm});
            skLineSegment(sketch, "E2184", {"start": v(-28, 104.82) * mm, "end": v(-28.13, 104.4) * mm});
            skLineSegment(sketch, "E2185", {"start": v(-28.13, 104.4) * mm, "end": v(-28.2, 103.98) * mm});
            skLineSegment(sketch, "E2186", {"start": v(-28.2, 103.98) * mm, "end": v(-28.2, 103.72) * mm});
            skLineSegment(sketch, "E2187", {"start": v(-28.2, 103.72) * mm, "end": v(-28.2, 103.63) * mm});
            skLineSegment(sketch, "E2188", {"start": v(-28.2, 103.63) * mm, "end": v(-28.25, 103.46) * mm});
            skLineSegment(sketch, "E2189", {"start": v(-28.25, 103.46) * mm, "end": v(-28.31, 103.32) * mm});
            skLineSegment(sketch, "E2190", {"start": v(-28.31, 103.32) * mm, "end": v(-28.41, 102.92) * mm});
            skLineSegment(sketch, "E2191", {"start": v(-28.41, 102.92) * mm, "end": v(-28.44, 102.35) * mm});
            skLineSegment(sketch, "E2192", {"start": v(-28.44, 102.35) * mm, "end": v(-28.35, 101.82) * mm});
            skLineSegment(sketch, "E2193", {"start": v(-28.35, 101.82) * mm, "end": v(-28.29, 101.66) * mm});
            skLineSegment(sketch, "E2194", {"start": v(-28.29, 101.66) * mm, "end": v(-28.23, 101.5) * mm});
            skLineSegment(sketch, "E2195", {"start": v(-28.23, 101.5) * mm, "end": v(-27.9, 100.83) * mm});
            skLineSegment(sketch, "E2196", {"start": v(-27.9, 100.83) * mm, "end": v(-27.7, 100.47) * mm});
            skLineSegment(sketch, "E2197", {"start": v(-27.7, 100.47) * mm, "end": v(-26.9, 100.48) * mm});
            skLineSegment(sketch, "E2198", {"start": v(-26.9, 100.48) * mm, "end": v(-26.82, 100.28) * mm});
            skLineSegment(sketch, "E2199", {"start": v(-26.82, 100.28) * mm, "end": v(-26.6, 99.73) * mm});
            skLineSegment(sketch, "E2200", {"start": v(-26.6, 99.73) * mm, "end": v(-26.3, 98.96) * mm});
            skLineSegment(sketch, "E2201", {"start": v(-26.3, 98.96) * mm, "end": v(-26, 98.3) * mm});
            skLineSegment(sketch, "E2202", {"start": v(-26, 98.3) * mm, "end": v(-25.91, 98.09) * mm});
            skLineSegment(sketch, "E2203", {"start": v(-25.91, 98.09) * mm, "end": v(-25.83, 97.9) * mm});
            skLineSegment(sketch, "E2204", {"start": v(-25.83, 97.9) * mm, "end": v(-25.52, 97.34) * mm});
            skLineSegment(sketch, "E2205", {"start": v(-25.52, 97.34) * mm, "end": v(-25.08, 96.8) * mm});
            skLineSegment(sketch, "E2206", {"start": v(-25.08, 96.8) * mm, "end": v(-24.5, 96.4) * mm});
            skLineSegment(sketch, "E2207", {"start": v(-24.5, 96.4) * mm, "end": v(-23.89, 96.11) * mm});
            skLineSegment(sketch, "E2208", {"start": v(-23.89, 96.11) * mm, "end": v(-23.68, 96.03) * mm});
            skLineSegment(sketch, "E2209", {"start": v(-23.68, 96.03) * mm, "end": v(-23.44, 95.93) * mm});
            skLineSegment(sketch, "E2210", {"start": v(-23.44, 95.93) * mm, "end": v(-22.7, 95.7) * mm});
            skLineSegment(sketch, "E2211", {"start": v(-22.7, 95.7) * mm, "end": v(-21.8, 95.52) * mm});
            skLineSegment(sketch, "E2212", {"start": v(-21.8, 95.52) * mm, "end": v(-21.01, 95.43) * mm});
            skLineSegment(sketch, "E2213", {"start": v(-21.01, 95.43) * mm, "end": v(-20.56, 95.42) * mm});
            skLineSegment(sketch, "E2214", {"start": v(-20.56, 95.42) * mm, "end": v(-20.41, 95.43) * mm});
            skLineSegment(sketch, "E2215", {"start": v(-20.41, 95.43) * mm, "end": v(-20.24, 95.43) * mm});
            skLineSegment(sketch, "E2216", {"start": v(-20.24, 95.43) * mm, "end": v(-19.67, 95.5) * mm});
            skLineSegment(sketch, "E2217", {"start": v(-19.67, 95.5) * mm, "end": v(-19.42, 95.62) * mm});
            skLineSegment(sketch, "E2218", {"start": v(-19.42, 95.62) * mm, "end": v(-19.4, 95.65) * mm});
            skLineSegment(sketch, "E2219", {"start": v(-19.4, 95.65) * mm, "end": v(-19.35, 95.75) * mm});
            skLineSegment(sketch, "E2220", {"start": v(-19.35, 95.75) * mm, "end": v(-19.36, 96.1) * mm});
            skLineSegment(sketch, "E2221", {"start": v(-19.36, 96.1) * mm, "end": v(-19.48, 96.21) * mm});
            skLineSegment(sketch, "E2222", {"start": v(-19.48, 96.21) * mm, "end": v(-19.43, 96.3) * mm});
            skLineSegment(sketch, "E2223", {"start": v(-19.43, 96.3) * mm, "end": v(-19.37, 96.55) * mm});
            skLineSegment(sketch, "E2224", {"start": v(-19.37, 96.55) * mm, "end": v(-19.4, 96.91) * mm});
            skLineSegment(sketch, "E2225", {"start": v(-19.4, 96.91) * mm, "end": v(-19.54, 97.24) * mm});
            skLineSegment(sketch, "E2226", {"start": v(-19.54, 97.24) * mm, "end": v(-19.61, 97.33) * mm});
            skLineSegment(sketch, "E2227", {"start": v(-19.61, 97.33) * mm, "end": v(-19.7, 97.43) * mm});
            skLineSegment(sketch, "E2228", {"start": v(-19.7, 97.43) * mm, "end": v(-20, 97.68) * mm});
            skLineSegment(sketch, "E2229", {"start": v(-20, 97.68) * mm, "end": v(-20.53, 98.05) * mm});
            skLineSegment(sketch, "E2230", {"start": v(-20.53, 98.05) * mm, "end": v(-21, 98.35) * mm});
            skLineSegment(sketch, "E2231", {"start": v(-21, 98.35) * mm, "end": v(-21.2, 98.47) * mm});
            skLineSegment(sketch, "E2232", {"start": v(-21.2, 98.47) * mm, "end": v(-21.32, 98.64) * mm});
            skLineSegment(sketch, "E2233", {"start": v(-21.32, 98.64) * mm, "end": v(-21.61, 99.1) * mm});
            skLineSegment(sketch, "E2234", {"start": v(-21.61, 99.1) * mm, "end": v(-21.96, 99.75) * mm});
            skLineSegment(sketch, "E2235", {"start": v(-21.96, 99.75) * mm, "end": v(-22.2, 100.33) * mm});
            skLineSegment(sketch, "E2236", {"start": v(-22.2, 100.33) * mm, "end": v(-22.25, 100.53) * mm});
            skLineSegment(sketch, "E2237", {"start": v(-22.25, 100.53) * mm, "end": v(-22.34, 100.85) * mm});
            skLineSegment(sketch, "E2238", {"start": v(-22.34, 100.85) * mm, "end": v(-22.6, 102.08) * mm});
            skLineSegment(sketch, "E2239", {"start": v(-22.6, 102.08) * mm, "end": v(-22.67, 103.1) * mm});
            skLineSegment(sketch, "E2240", {"start": v(-22.67, 103.1) * mm, "end": v(-22.66, 103.3) * mm});
            skLineSegment(sketch, "E2241", {"start": v(-22.66, 103.3) * mm, "end": v(-22.62, 103.33) * mm});
            skLineSegment(sketch, "E2242", {"start": v(-22.62, 103.33) * mm, "end": v(-22.55, 103.36) * mm});
            skLineSegment(sketch, "E2243", {"start": v(-22.55, 103.36) * mm, "end": v(-22.3, 103.58) * mm});
            skLineSegment(sketch, "E2244", {"start": v(-22.3, 103.58) * mm, "end": v(-22.24, 103.9) * mm});
            skLineSegment(sketch, "E2245", {"start": v(-22.24, 103.9) * mm, "end": v(-22.25, 103.95) * mm});
            skLineSegment(sketch, "E2246", {"start": v(-22.25, 103.95) * mm, "end": v(-22.26, 103.97) * mm});
            skLineSegment(sketch, "E2247", {"start": v(-22.26, 103.97) * mm, "end": v(-22.38, 104.2) * mm});
            skLineSegment(sketch, "E2248", {"start": v(-22.38, 104.2) * mm, "end": v(-22.4, 104.23) * mm});
            skLineSegment(sketch, "E2249", {"start": v(-22.4, 104.23) * mm, "end": v(-22.4, 104.23) * mm});
            skLineSegment(sketch, "E2250", {"start": v(-22.4, 104.23) * mm, "end": v(-22.42, 104.23) * mm});
            skLineSegment(sketch, "E2251", {"start": v(-22.42, 104.23) * mm, "end": v(-22.42, 104.17) * mm});
            skLineSegment(sketch, "E2252", {"start": v(-22.42, 104.17) * mm, "end": v(-22.55, 104) * mm});
            skLineSegment(sketch, "E2253", {"start": v(-22.55, 104) * mm, "end": v(-22.58, 103.99) * mm});
            skLineSegment(sketch, "E2254", {"start": v(-22.58, 103.99) * mm, "end": v(-22.63, 103.96) * mm});
            skLineSegment(sketch, "E2255", {"start": v(-22.63, 103.96) * mm, "end": v(-22.85, 104.04) * mm});
            skLineSegment(sketch, "E2256", {"start": v(-22.85, 104.04) * mm, "end": v(-23.03, 104.22) * mm});
            skLineSegment(sketch, "E2257", {"start": v(-23.03, 104.22) * mm, "end": v(-23.1, 104.23) * mm});
            skLineSegment(sketch, "E2258", {"start": v(-23.1, 104.23) * mm, "end": v(-23.18, 104.24) * mm});
            skLineSegment(sketch, "E2259", {"start": v(-23.18, 104.24) * mm, "end": v(-23.42, 104.38) * mm});
            skLineSegment(sketch, "E2260", {"start": v(-23.42, 104.38) * mm, "end": v(-23.35, 104.57) * mm});
            skLineSegment(sketch, "E2261", {"start": v(-23.35, 104.57) * mm, "end": v(-23.3, 104.6) * mm});
            skLineSegment(sketch, "E2262", {"start": v(-23.3, 104.6) * mm, "end": v(-23.29, 104.6) * mm});
            skLineSegment(sketch, "E2263", {"start": v(-23.29, 104.6) * mm, "end": v(-23.12, 104.68) * mm});
            skLineSegment(sketch, "E2264", {"start": v(-23.12, 104.68) * mm, "end": v(-22.83, 104.67) * mm});
            skLineSegment(sketch, "E2265", {"start": v(-22.83, 104.67) * mm, "end": v(-22.76, 104.63) * mm});
            skLineSegment(sketch, "E2266", {"start": v(-22.76, 104.63) * mm, "end": v(-22.74, 104.63) * mm});
            skLineSegment(sketch, "E2267", {"start": v(-22.74, 104.63) * mm, "end": v(-22.57, 104.52) * mm});
            skLineSegment(sketch, "E2268", {"start": v(-22.57, 104.52) * mm, "end": v(-22.55, 104.5) * mm});
            skLineSegment(sketch, "E2269", {"start": v(-22.55, 104.5) * mm, "end": v(-22.53, 104.52) * mm});
            skLineSegment(sketch, "E2270", {"start": v(-22.53, 104.52) * mm, "end": v(-22.53, 104.57) * mm});
            skLineSegment(sketch, "E2271", {"start": v(-22.53, 104.57) * mm, "end": v(-22.52, 104.65) * mm});
            skLineSegment(sketch, "E2272", {"start": v(-22.52, 104.65) * mm, "end": v(-22.48, 104.88) * mm});
            skLineSegment(sketch, "E2273", {"start": v(-22.48, 104.88) * mm, "end": v(-22.39, 105.28) * mm});
            skLineSegment(sketch, "E2274", {"start": v(-22.39, 105.28) * mm, "end": v(-22.22, 105.83) * mm});
            skLineSegment(sketch, "E2275", {"start": v(-22.22, 105.83) * mm, "end": v(-22, 106.4) * mm});
            skLineSegment(sketch, "E2276", {"start": v(-22, 106.4) * mm, "end": v(-21.92, 106.57) * mm});
            skLineSegment(sketch, "E2277", {"start": v(-21.92, 106.57) * mm, "end": v(-21.75, 106.98) * mm});
            skLineSegment(sketch, "E2278", {"start": v(-21.75, 106.98) * mm, "end": v(-21.08, 108.13) * mm});
            skLineSegment(sketch, "E2279", {"start": v(-21.08, 108.13) * mm, "end": v(-19.9, 109.9) * mm});
            skLineSegment(sketch, "E2280", {"start": v(-19.9, 109.9) * mm, "end": v(-18.76, 111.48) * mm});
            skLineSegment(sketch, "E2281", {"start": v(-18.76, 111.48) * mm, "end": v(-18.15, 112.3) * mm});
            skLineSegment(sketch, "E2282", {"start": v(-18.15, 112.3) * mm, "end": v(-18, 112.49) * mm});
            skLineSegment(sketch, "E2283", {"start": v(-18, 112.49) * mm, "end": v(-17.78, 112.75) * mm});
            skLineSegment(sketch, "E2284", {"start": v(-17.78, 112.75) * mm, "end": v(-17, 113.66) * mm});
            skLineSegment(sketch, "E2285", {"start": v(-17, 113.66) * mm, "end": v(-16.54, 114.16) * mm});
            skLineSegment(sketch, "E2286", {"start": v(-16.54, 114.16) * mm, "end": v(-16.5, 114.21) * mm});
            skLineSegment(sketch, "E2287", {"start": v(-16.5, 114.21) * mm, "end": v(-16.46, 114.26) * mm});
            skLineSegment(sketch, "E2288", {"start": v(-16.46, 114.26) * mm, "end": v(-16.35, 114.42) * mm});
            skLineSegment(sketch, "E2289", {"start": v(-16.35, 114.42) * mm, "end": v(-16.58, 114.52) * mm});
            skLineSegment(sketch, "E2290", {"start": v(-16.58, 114.52) * mm, "end": v(-16.65, 114.53) * mm});
            skLineSegment(sketch, "E2291", {"start": v(-25.36, 99.46) * mm, "end": v(-25.39, 99.43) * mm});
            skLineSegment(sketch, "E2292", {"start": v(-25.39, 99.43) * mm, "end": v(-25.57, 99.43) * mm});
            skLineSegment(sketch, "E2293", {"start": v(-25.57, 99.43) * mm, "end": v(-25.77, 99.7) * mm});
            skLineSegment(sketch, "E2294", {"start": v(-25.77, 99.7) * mm, "end": v(-25.95, 100.1) * mm});
            skLineSegment(sketch, "E2295", {"start": v(-25.95, 100.1) * mm, "end": v(-26.06, 100.4) * mm});
            skLineSegment(sketch, "E2296", {"start": v(-26.06, 100.4) * mm, "end": v(-26.1, 100.5) * mm});
            skLineSegment(sketch, "E2297", {"start": v(-26.1, 100.5) * mm, "end": v(-26.14, 100.6) * mm});
            skLineSegment(sketch, "E2298", {"start": v(-26.14, 100.6) * mm, "end": v(-26.54, 101.25) * mm});
            skLineSegment(sketch, "E2299", {"start": v(-26.54, 101.25) * mm, "end": v(-26.87, 101.95) * mm});
            skLineSegment(sketch, "E2300", {"start": v(-26.87, 101.95) * mm, "end": v(-26.87, 102.1) * mm});
            skLineSegment(sketch, "E2301", {"start": v(-26.87, 102.1) * mm, "end": v(-26.87, 102.23) * mm});
            skLineSegment(sketch, "E2302", {"start": v(-26.87, 102.23) * mm, "end": v(-26.8, 102.63) * mm});
            skLineSegment(sketch, "E2303", {"start": v(-26.8, 102.63) * mm, "end": v(-26.75, 102.74) * mm});
            skLineSegment(sketch, "E2304", {"start": v(-26.75, 102.74) * mm, "end": v(-26.72, 102.77) * mm});
            skLineSegment(sketch, "E2305", {"start": v(-26.72, 102.77) * mm, "end": v(-26.59, 102.8) * mm});
            skLineSegment(sketch, "E2306", {"start": v(-26.59, 102.8) * mm, "end": v(-26.5, 102.66) * mm});
            skLineSegment(sketch, "E2307", {"start": v(-26.5, 102.66) * mm, "end": v(-26.47, 102.39) * mm});
            skLineSegment(sketch, "E2308", {"start": v(-26.47, 102.39) * mm, "end": v(-26.45, 102.14) * mm});
            skLineSegment(sketch, "E2309", {"start": v(-26.45, 102.14) * mm, "end": v(-26.44, 102.06) * mm});
            skLineSegment(sketch, "E2310", {"start": v(-26.44, 102.06) * mm, "end": v(-26.44, 101.95) * mm});
            skLineSegment(sketch, "E2311", {"start": v(-26.44, 101.95) * mm, "end": v(-26.16, 101.51) * mm});
            skLineSegment(sketch, "E2312", {"start": v(-26.16, 101.51) * mm, "end": v(-25.7, 101.02) * mm});
            skLineSegment(sketch, "E2313", {"start": v(-25.7, 101.02) * mm, "end": v(-25.6, 100.88) * mm});
            skLineSegment(sketch, "E2314", {"start": v(-25.6, 100.88) * mm, "end": v(-25.5, 100.75) * mm});
            skLineSegment(sketch, "E2315", {"start": v(-25.5, 100.75) * mm, "end": v(-25.2, 100.1) * mm});
            skLineSegment(sketch, "E2316", {"start": v(-25.2, 100.1) * mm, "end": v(-25.28, 99.55) * mm});
            skLineSegment(sketch, "E2317", {"start": v(-25.28, 99.55) * mm, "end": v(-25.36, 99.46) * mm});
            skLineSegment(sketch, "E2318", {"start": v(-22.85, 97.8) * mm, "end": v(-22.83, 97.77) * mm});
            skLineSegment(sketch, "E2319", {"start": v(-22.83, 97.77) * mm, "end": v(-22.45, 97.38) * mm});
            skLineSegment(sketch, "E2320", {"start": v(-22.45, 97.38) * mm, "end": v(-22.4, 97.34) * mm});
            skLineSegment(sketch, "E2321", {"start": v(-22.4, 97.34) * mm, "end": v(-22.36, 97.32) * mm});
            skLineSegment(sketch, "E2322", {"start": v(-22.36, 97.32) * mm, "end": v(-21.98, 97.17) * mm});
            skLineSegment(sketch, "E2323", {"start": v(-21.98, 97.17) * mm, "end": v(-21.95, 97.16) * mm});
            skLineSegment(sketch, "E2324", {"start": v(-21.95, 97.16) * mm, "end": v(-21.94, 97.16) * mm});
            skLineSegment(sketch, "E2325", {"start": v(-21.94, 97.16) * mm, "end": v(-21.91, 97.1) * mm});
            skLineSegment(sketch, "E2326", {"start": v(-21.91, 97.1) * mm, "end": v(-21.92, 97.09) * mm});
            skLineSegment(sketch, "E2327", {"start": v(-21.92, 97.09) * mm, "end": v(-21.93, 97.08) * mm});
            skLineSegment(sketch, "E2328", {"start": v(-21.93, 97.08) * mm, "end": v(-22.06, 97.05) * mm});
            skLineSegment(sketch, "E2329", {"start": v(-22.06, 97.05) * mm, "end": v(-22.2, 97.05) * mm});
            skLineSegment(sketch, "E2330", {"start": v(-22.2, 97.05) * mm, "end": v(-22.57, 97.16) * mm});
            skLineSegment(sketch, "E2331", {"start": v(-22.57, 97.16) * mm, "end": v(-22.62, 97.2) * mm});
            skLineSegment(sketch, "E2332", {"start": v(-22.62, 97.2) * mm, "end": v(-22.7, 97.24) * mm});
            skLineSegment(sketch, "E2333", {"start": v(-22.7, 97.24) * mm, "end": v(-23.17, 97.42) * mm});
            skLineSegment(sketch, "E2334", {"start": v(-23.17, 97.42) * mm, "end": v(-23.65, 97.62) * mm});
            skLineSegment(sketch, "E2335", {"start": v(-23.65, 97.62) * mm, "end": v(-23.73, 97.68) * mm});
            skLineSegment(sketch, "E2336", {"start": v(-23.73, 97.68) * mm, "end": v(-23.77, 97.71) * mm});
            skLineSegment(sketch, "E2337", {"start": v(-23.77, 97.71) * mm, "end": v(-23.85, 97.86) * mm});
            skLineSegment(sketch, "E2338", {"start": v(-23.85, 97.86) * mm, "end": v(-23.77, 98) * mm});
            skLineSegment(sketch, "E2339", {"start": v(-23.77, 98) * mm, "end": v(-23.57, 98.12) * mm});
            skLineSegment(sketch, "E2340", {"start": v(-23.57, 98.12) * mm, "end": v(-23.39, 98.16) * mm});
            skLineSegment(sketch, "E2341", {"start": v(-23.39, 98.16) * mm, "end": v(-23.33, 98.16) * mm});
            skLineSegment(sketch, "E2342", {"start": v(-23.33, 98.16) * mm, "end": v(-23.24, 98.16) * mm});
            skLineSegment(sketch, "E2343", {"start": v(-23.24, 98.16) * mm, "end": v(-22.97, 97.98) * mm});
            skLineSegment(sketch, "E2344", {"start": v(-22.97, 97.98) * mm, "end": v(-22.85, 97.8) * mm});
            skLineSegment(sketch, "E2345", {"start": v(-23.89, 98.43) * mm, "end": v(-23.97, 98.43) * mm});
            skLineSegment(sketch, "E2346", {"start": v(-23.97, 98.43) * mm, "end": v(-24.2, 98.3) * mm});
            skLineSegment(sketch, "E2347", {"start": v(-24.2, 98.3) * mm, "end": v(-24.41, 98.18) * mm});
            skLineSegment(sketch, "E2348", {"start": v(-24.41, 98.18) * mm, "end": v(-24.48, 98.18) * mm});
            skLineSegment(sketch, "E2349", {"start": v(-24.48, 98.18) * mm, "end": v(-24.5, 98.18) * mm});
            skLineSegment(sketch, "E2350", {"start": v(-24.5, 98.18) * mm, "end": v(-24.6, 98.28) * mm});
            skLineSegment(sketch, "E2351", {"start": v(-24.6, 98.28) * mm, "end": v(-24.43, 98.54) * mm});
            skLineSegment(sketch, "E2352", {"start": v(-24.43, 98.54) * mm, "end": v(-24.36, 98.6) * mm});
            skLineSegment(sketch, "E2353", {"start": v(-24.36, 98.6) * mm, "end": v(-24.28, 98.68) * mm});
            skLineSegment(sketch, "E2354", {"start": v(-24.28, 98.68) * mm, "end": v(-23.82, 98.82) * mm});
            skLineSegment(sketch, "E2355", {"start": v(-23.82, 98.82) * mm, "end": v(-23.5, 98.79) * mm});
            skLineSegment(sketch, "E2356", {"start": v(-23.5, 98.79) * mm, "end": v(-23.48, 98.78) * mm});
            skLineSegment(sketch, "E2357", {"start": v(-23.48, 98.78) * mm, "end": v(-23.43, 98.77) * mm});
            skLineSegment(sketch, "E2358", {"start": v(-23.43, 98.77) * mm, "end": v(-23.28, 98.7) * mm});
            skLineSegment(sketch, "E2359", {"start": v(-23.28, 98.7) * mm, "end": v(-23.32, 98.57) * mm});
            skLineSegment(sketch, "E2360", {"start": v(-23.32, 98.57) * mm, "end": v(-23.54, 98.47) * mm});
            skLineSegment(sketch, "E2361", {"start": v(-23.54, 98.47) * mm, "end": v(-23.8, 98.43) * mm});
            skLineSegment(sketch, "E2362", {"start": v(-23.8, 98.43) * mm, "end": v(-23.89, 98.43) * mm});
            skLineSegment(sketch, "E2363", {"start": v(-24.39, 132.21) * mm, "end": v(-24.39, 131.91) * mm});
            skLineSegment(sketch, "E2364", {"start": v(-24.39, 131.91) * mm, "end": v(-24.23, 131.02) * mm});
            skLineSegment(sketch, "E2365", {"start": v(-24.23, 131.02) * mm, "end": v(-23.88, 130.14) * mm});
            skLineSegment(sketch, "E2366", {"start": v(-23.88, 130.14) * mm, "end": v(-23.5, 129.57) * mm});
            skLineSegment(sketch, "E2367", {"start": v(-23.5, 129.57) * mm, "end": v(-23.3, 129.35) * mm});
            skLineSegment(sketch, "E2368", {"start": v(-23.3, 129.35) * mm, "end": v(-23.27, 129.31) * mm});
            skLineSegment(sketch, "E2369", {"start": v(-23.27, 129.31) * mm, "end": v(-23.25, 129.3) * mm});
            skLineSegment(sketch, "E2370", {"start": v(-23.25, 129.3) * mm, "end": v(-23.16, 129.3) * mm});
            skLineSegment(sketch, "E2371", {"start": v(-23.16, 129.3) * mm, "end": v(-23.16, 129.6) * mm});
            skLineSegment(sketch, "E2372", {"start": v(-23.16, 129.6) * mm, "end": v(-23.16, 130.2) * mm});
            skLineSegment(sketch, "E2373", {"start": v(-23.16, 130.2) * mm, "end": v(-23, 131.08) * mm});
            skLineSegment(sketch, "E2374", {"start": v(-23, 131.08) * mm, "end": v(-22.53, 132.2) * mm});
            skLineSegment(sketch, "E2375", {"start": v(-22.53, 132.2) * mm, "end": v(-21.63, 133.53) * mm});
            skLineSegment(sketch, "E2376", {"start": v(-21.63, 133.53) * mm, "end": v(-20.16, 135.06) * mm});
            skLineSegment(sketch, "E2377", {"start": v(-20.16, 135.06) * mm, "end": v(-18.54, 136.35) * mm});
            skLineSegment(sketch, "E2378", {"start": v(-18.54, 136.35) * mm, "end": v(-17.97, 136.74) * mm});
            skLineSegment(sketch, "E2379", {"start": v(-17.97, 136.74) * mm, "end": v(-18.02, 136.75) * mm});
            skLineSegment(sketch, "E2380", {"start": v(-18.02, 136.75) * mm, "end": v(-18.03, 136.75) * mm});
            skLineSegment(sketch, "E2381", {"start": v(-18.03, 136.75) * mm, "end": v(-18.07, 136.75) * mm});
            skLineSegment(sketch, "E2382", {"start": v(-18.07, 136.75) * mm, "end": v(-18.16, 136.74) * mm});
            skLineSegment(sketch, "E2383", {"start": v(-18.16, 136.74) * mm, "end": v(-18.18, 136.74) * mm});
            skLineSegment(sketch, "E2384", {"start": v(-18.18, 136.74) * mm, "end": v(-18.45, 136.68) * mm});
            skLineSegment(sketch, "E2385", {"start": v(-18.45, 136.68) * mm, "end": v(-19.9, 136.29) * mm});
            skLineSegment(sketch, "E2386", {"start": v(-19.9, 136.29) * mm, "end": v(-21.27, 135.77) * mm});
            skLineSegment(sketch, "E2387", {"start": v(-21.27, 135.77) * mm, "end": v(-21.5, 135.64) * mm});
            skLineSegment(sketch, "E2388", {"start": v(-21.5, 135.64) * mm, "end": v(-21.57, 135.61) * mm});
            skLineSegment(sketch, "E2389", {"start": v(-21.57, 135.61) * mm, "end": v(-22.1, 135.3) * mm});
            skLineSegment(sketch, "E2390", {"start": v(-22.1, 135.3) * mm, "end": v(-22.14, 135.26) * mm});
            skLineSegment(sketch, "E2391", {"start": v(-22.14, 135.26) * mm, "end": v(-22.35, 135.13) * mm});
            skLineSegment(sketch, "E2392", {"start": v(-22.35, 135.13) * mm, "end": v(-23, 134.55) * mm});
            skLineSegment(sketch, "E2393", {"start": v(-23, 134.55) * mm, "end": v(-23.28, 134.08) * mm});
            skLineSegment(sketch, "E2394", {"start": v(-23.28, 134.08) * mm, "end": v(-23.32, 134) * mm});
            skLineSegment(sketch, "E2395", {"start": v(-23.32, 134) * mm, "end": v(-23.34, 133.98) * mm});
            skLineSegment(sketch, "E2396", {"start": v(-23.34, 133.98) * mm, "end": v(-23.34, 133.97) * mm});
            skLineSegment(sketch, "E2397", {"start": v(-23.34, 133.97) * mm, "end": v(-23.38, 133.89) * mm});
            skLineSegment(sketch, "E2398", {"start": v(-23.38, 133.89) * mm, "end": v(-23.46, 133.62) * mm});
            skLineSegment(sketch, "E2399", {"start": v(-23.46, 133.62) * mm, "end": v(-23.54, 133.3) * mm});
            skLineSegment(sketch, "E2400", {"start": v(-23.54, 133.3) * mm, "end": v(-23.6, 133.15) * mm});
            skLineSegment(sketch, "E2401", {"start": v(-23.6, 133.15) * mm, "end": v(-23.63, 133.32) * mm});
            skLineSegment(sketch, "E2402", {"start": v(-23.63, 133.32) * mm, "end": v(-23.64, 133.37) * mm});
            skLineSegment(sketch, "E2403", {"start": v(-23.64, 133.37) * mm, "end": v(-23.64, 133.47) * mm});
            skLineSegment(sketch, "E2404", {"start": v(-23.64, 133.47) * mm, "end": v(-23.6, 133.73) * mm});
            skLineSegment(sketch, "E2405", {"start": v(-23.6, 133.73) * mm, "end": v(-23.6, 133.76) * mm});
            skLineSegment(sketch, "E2406", {"start": v(-23.6, 133.76) * mm, "end": v(-23.6, 133.87) * mm});
            skLineSegment(sketch, "E2407", {"start": v(-23.6, 133.87) * mm, "end": v(-23.53, 134.15) * mm});
            skLineSegment(sketch, "E2408", {"start": v(-23.53, 134.15) * mm, "end": v(-23.52, 134.18) * mm});
            skLineSegment(sketch, "E2409", {"start": v(-23.52, 134.18) * mm, "end": v(-23.52, 134.2) * mm});
            skLineSegment(sketch, "E2410", {"start": v(-23.52, 134.2) * mm, "end": v(-23.43, 134.38) * mm});
            skLineSegment(sketch, "E2411", {"start": v(-23.43, 134.38) * mm, "end": v(-23.42, 134.4) * mm});
            skLineSegment(sketch, "E2412", {"start": v(-23.42, 134.4) * mm, "end": v(-23.4, 134.45) * mm});
            skLineSegment(sketch, "E2413", {"start": v(-23.4, 134.45) * mm, "end": v(-23.1, 134.95) * mm});
            skLineSegment(sketch, "E2414", {"start": v(-23.1, 134.95) * mm, "end": v(-23.07, 135) * mm});
            skLineSegment(sketch, "E2415", {"start": v(-23.07, 135) * mm, "end": v(-23, 135.1) * mm});
            skLineSegment(sketch, "E2416", {"start": v(-23, 135.1) * mm, "end": v(-21.9, 136) * mm});
            skLineSegment(sketch, "E2417", {"start": v(-21.9, 136) * mm, "end": v(-21.75, 136.09) * mm});
            skLineSegment(sketch, "E2418", {"start": v(-21.75, 136.09) * mm, "end": v(-21.33, 136.32) * mm});
            skLineSegment(sketch, "E2419", {"start": v(-21.33, 136.32) * mm, "end": v(-19.99, 136.83) * mm});
            skLineSegment(sketch, "E2420", {"start": v(-19.99, 136.83) * mm, "end": v(-18, 137.32) * mm});
            skLineSegment(sketch, "E2421", {"start": v(-18, 137.32) * mm, "end": v(-15.56, 137.86) * mm});
            skLineSegment(sketch, "E2422", {"start": v(-15.56, 137.86) * mm, "end": v(-13.22, 138.47) * mm});
            skLineSegment(sketch, "E2423", {"start": v(-13.22, 138.47) * mm, "end": v(-12.45, 138.71) * mm});
            skLineSegment(sketch, "E2424", {"start": v(-12.45, 138.71) * mm, "end": v(-12.2, 138.82) * mm});
            skLineSegment(sketch, "E2425", {"start": v(-12.2, 138.82) * mm, "end": v(-9.45, 140.11) * mm});
            skLineSegment(sketch, "E2426", {"start": v(-9.45, 140.11) * mm, "end": v(-9.17, 140.27) * mm});
            skLineSegment(sketch, "E2427", {"start": v(-9.17, 140.27) * mm, "end": v(-8.8, 140.49) * mm});
            skLineSegment(sketch, "E2428", {"start": v(-8.8, 140.49) * mm, "end": v(-7.77, 141.24) * mm});
            skLineSegment(sketch, "E2429", {"start": v(-7.77, 141.24) * mm, "end": v(-6.83, 142.15) * mm});
            skLineSegment(sketch, "E2430", {"start": v(-6.83, 142.15) * mm, "end": v(-6.13, 143) * mm});
            skLineSegment(sketch, "E2431", {"start": v(-6.13, 143) * mm, "end": v(-5.62, 143.58) * mm});
            skLineSegment(sketch, "E2432", {"start": v(-5.62, 143.58) * mm, "end": v(-5.43, 143.75) * mm});
            skLineSegment(sketch, "E2433", {"start": v(-5.43, 143.75) * mm, "end": v(-5.7, 143.65) * mm});
            skLineSegment(sketch, "E2434", {"start": v(-5.7, 143.65) * mm, "end": v(-6.5, 143.34) * mm});
            skLineSegment(sketch, "E2435", {"start": v(-6.5, 143.34) * mm, "end": v(-7.26, 143.03) * mm});
            skLineSegment(sketch, "E2436", {"start": v(-7.26, 143.03) * mm, "end": v(-7.84, 142.79) * mm});
            skLineSegment(sketch, "E2437", {"start": v(-7.84, 142.79) * mm, "end": v(-8.25, 142.63) * mm});
            skLineSegment(sketch, "E2438", {"start": v(-8.25, 142.63) * mm, "end": v(-8.39, 142.58) * mm});
            skLineSegment(sketch, "E2439", {"start": v(-8.39, 142.58) * mm, "end": v(-8.54, 142.53) * mm});
            skLineSegment(sketch, "E2440", {"start": v(-8.54, 142.53) * mm, "end": v(-9, 142.4) * mm});
            skLineSegment(sketch, "E2441", {"start": v(-9, 142.4) * mm, "end": v(-9.6, 142.23) * mm});
            skLineSegment(sketch, "E2442", {"start": v(-9.6, 142.23) * mm, "end": v(-10.19, 142.09) * mm});
            skLineSegment(sketch, "E2443", {"start": v(-10.19, 142.09) * mm, "end": v(-10.67, 142) * mm});
            skLineSegment(sketch, "E2444", {"start": v(-10.67, 142) * mm, "end": v(-11.02, 141.95) * mm});
            skLineSegment(sketch, "E2445", {"start": v(-11.02, 141.95) * mm, "end": v(-11.16, 141.97) * mm});
            skLineSegment(sketch, "E2446", {"start": v(-11.16, 141.97) * mm, "end": v(-11.06, 142.06) * mm});
            skLineSegment(sketch, "E2447", {"start": v(-11.06, 142.06) * mm, "end": v(-10.76, 142.19) * mm});
            skLineSegment(sketch, "E2448", {"start": v(-10.76, 142.19) * mm, "end": v(-10.65, 142.22) * mm});
            skLineSegment(sketch, "E2449", {"start": v(-10.65, 142.22) * mm, "end": v(-10.36, 142.33) * mm});
            skLineSegment(sketch, "E2450", {"start": v(-10.36, 142.33) * mm, "end": v(-9.49, 142.7) * mm});
            skLineSegment(sketch, "E2451", {"start": v(-9.49, 142.7) * mm, "end": v(-8.15, 143.3) * mm});
            skLineSegment(sketch, "E2452", {"start": v(-8.15, 143.3) * mm, "end": v(-6.48, 143.97) * mm});
            skLineSegment(sketch, "E2453", {"start": v(-6.48, 143.97) * mm, "end": v(-4.84, 144.5) * mm});
            skLineSegment(sketch, "E2454", {"start": v(-4.84, 144.5) * mm, "end": v(-4.3, 144.65) * mm});
            skLineSegment(sketch, "E2455", {"start": v(-4.3, 144.65) * mm, "end": v(-4.25, 144.67) * mm});
            skLineSegment(sketch, "E2456", {"start": v(-4.25, 144.67) * mm, "end": v(-3.83, 144.76) * mm});
            skLineSegment(sketch, "E2457", {"start": v(-3.83, 144.76) * mm, "end": v(-3.79, 144.77) * mm});
            skLineSegment(sketch, "E2458", {"start": v(-3.79, 144.77) * mm, "end": v(-3.76, 144.78) * mm});
            skLineSegment(sketch, "E2459", {"start": v(-3.76, 144.78) * mm, "end": v(-3.45, 144.84) * mm});
            skLineSegment(sketch, "E2460", {"start": v(-3.45, 144.84) * mm, "end": v(-3.42, 144.85) * mm});
            skLineSegment(sketch, "E2461", {"start": v(-3.42, 144.85) * mm, "end": v(-3.24, 144.88) * mm});
            skLineSegment(sketch, "E2462", {"start": v(-3.24, 144.88) * mm, "end": v(-1.9, 145.04) * mm});
            skLineSegment(sketch, "E2463", {"start": v(-1.9, 145.04) * mm, "end": v(-1.46, 145.04) * mm});
            skLineSegment(sketch, "E2464", {"start": v(-1.46, 145.04) * mm, "end": v(-1.16, 145.05) * mm});
            skLineSegment(sketch, "E2465", {"start": v(-1.16, 145.05) * mm, "end": v(-0.08, 144.97) * mm});
            skLineSegment(sketch, "E2466", {"start": v(-0.08, 144.97) * mm, "end": v(0.41, 144.88) * mm});
            skLineSegment(sketch, "E2467", {"start": v(0.41, 144.88) * mm, "end": v(0.52, 145) * mm});
            skLineSegment(sketch, "E2468", {"start": v(0.52, 145) * mm, "end": v(0.8, 145.28) * mm});
            skLineSegment(sketch, "E2469", {"start": v(0.8, 145.28) * mm, "end": v(1.14, 145.69) * mm});
            skLineSegment(sketch, "E2470", {"start": v(1.14, 145.69) * mm, "end": v(1.4, 146.04) * mm});
            skLineSegment(sketch, "E2471", {"start": v(1.4, 146.04) * mm, "end": v(1.48, 146.16) * mm});
            skLineSegment(sketch, "E2472", {"start": v(1.48, 146.16) * mm, "end": v(1.5, 146.19) * mm});
            skLineSegment(sketch, "E2473", {"start": v(1.5, 146.19) * mm, "end": v(1.62, 146.42) * mm});
            skLineSegment(sketch, "E2474", {"start": v(1.62, 146.42) * mm, "end": v(1.63, 146.44) * mm});
            skLineSegment(sketch, "E2475", {"start": v(1.63, 146.44) * mm, "end": v(1.64, 146.45) * mm});
            skLineSegment(sketch, "E2476", {"start": v(1.64, 146.45) * mm, "end": v(1.72, 146.58) * mm});
            skLineSegment(sketch, "E2477", {"start": v(1.72, 146.58) * mm, "end": v(1.73, 146.59) * mm});
            skLineSegment(sketch, "E2478", {"start": v(1.73, 146.59) * mm, "end": v(1.75, 146.54) * mm});
            skLineSegment(sketch, "E2479", {"start": v(1.75, 146.54) * mm, "end": v(1.75, 146.53) * mm});
            skLineSegment(sketch, "E2480", {"start": v(1.75, 146.53) * mm, "end": v(1.81, 146.4) * mm});
            skLineSegment(sketch, "E2481", {"start": v(1.81, 146.4) * mm, "end": v(2.03, 145.95) * mm});
            skLineSegment(sketch, "E2482", {"start": v(2.03, 145.95) * mm, "end": v(2.43, 145.2) * mm});
            skLineSegment(sketch, "E2483", {"start": v(2.43, 145.2) * mm, "end": v(2.86, 144.64) * mm});
            skLineSegment(sketch, "E2484", {"start": v(2.86, 144.64) * mm, "end": v(3.18, 144.51) * mm});
            skLineSegment(sketch, "E2485", {"start": v(3.18, 144.51) * mm, "end": v(3.22, 144.55) * mm});
            skLineSegment(sketch, "E2486", {"start": v(3.22, 144.55) * mm, "end": v(3.28, 144.6) * mm});
            skLineSegment(sketch, "E2487", {"start": v(3.28, 144.6) * mm, "end": v(3.4, 144.93) * mm});
            skLineSegment(sketch, "E2488", {"start": v(3.4, 144.93) * mm, "end": v(3.55, 145.62) * mm});
            skLineSegment(sketch, "E2489", {"start": v(3.55, 145.62) * mm, "end": v(3.7, 146.42) * mm});
            skLineSegment(sketch, "E2490", {"start": v(3.7, 146.42) * mm, "end": v(3.77, 146.94) * mm});
            skLineSegment(sketch, "E2491", {"start": v(3.77, 146.94) * mm, "end": v(3.8, 147.11) * mm});
            skLineSegment(sketch, "E2492", {"start": v(3.8, 147.11) * mm, "end": v(3.65, 147.18) * mm});
            skLineSegment(sketch, "E2493", {"start": v(3.65, 147.18) * mm, "end": v(2.93, 147.52) * mm});
            skLineSegment(sketch, "E2494", {"start": v(2.93, 147.52) * mm, "end": v(2.47, 147.74) * mm});
            skLineSegment(sketch, "E2495", {"start": v(2.47, 147.74) * mm, "end": v(2.45, 147.75) * mm});
            skLineSegment(sketch, "E2496", {"start": v(2.45, 147.75) * mm, "end": v(2.47, 147.77) * mm});
            skLineSegment(sketch, "E2497", {"start": v(2.47, 147.77) * mm, "end": v(2.56, 147.73) * mm});
            skLineSegment(sketch, "E2498", {"start": v(2.56, 147.73) * mm, "end": v(2.58, 147.73) * mm});
            skLineSegment(sketch, "E2499", {"start": v(2.58, 147.73) * mm, "end": v(2.62, 147.72) * mm});
            skLineSegment(sketch, "E2500", {"start": v(2.62, 147.72) * mm, "end": v(2.93, 147.67) * mm});
            skLineSegment(sketch, "E2501", {"start": v(2.93, 147.67) * mm, "end": v(3.25, 147.76) * mm});
            skLineSegment(sketch, "E2502", {"start": v(3.25, 147.76) * mm, "end": v(3.3, 147.81) * mm});
            skLineSegment(sketch, "E2503", {"start": v(3.3, 147.81) * mm, "end": v(3.32, 147.83) * mm});
            skLineSegment(sketch, "E2504", {"start": v(3.32, 147.83) * mm, "end": v(3.5, 147.98) * mm});
            skLineSegment(sketch, "E2505", {"start": v(3.5, 147.98) * mm, "end": v(3.52, 147.99) * mm});
            skLineSegment(sketch, "E2506", {"start": v(3.52, 147.99) * mm, "end": v(3.54, 148) * mm});
            skLineSegment(sketch, "E2507", {"start": v(3.54, 148) * mm, "end": v(3.8, 147.9) * mm});
            skLineSegment(sketch, "E2508", {"start": v(3.8, 147.9) * mm, "end": v(3.82, 147.86) * mm});
            skLineSegment(sketch, "E2509", {"start": v(3.82, 147.86) * mm, "end": v(3.83, 147.84) * mm});
            skLineSegment(sketch, "E2510", {"start": v(3.83, 147.84) * mm, "end": v(3.94, 147.63) * mm});
            skLineSegment(sketch, "E2511", {"start": v(3.94, 147.63) * mm, "end": v(3.95, 147.6) * mm});
            skLineSegment(sketch, "E2512", {"start": v(3.95, 147.6) * mm, "end": v(3.95, 147.57) * mm});
            skLineSegment(sketch, "E2513", {"start": v(3.95, 147.57) * mm, "end": v(4.08, 147.3) * mm});
            skLineSegment(sketch, "E2514", {"start": v(4.08, 147.3) * mm, "end": v(4.1, 147.28) * mm});
            skLineSegment(sketch, "E2515", {"start": v(4.1, 147.28) * mm, "end": v(4.13, 147.23) * mm});
            skLineSegment(sketch, "E2516", {"start": v(4.13, 147.23) * mm, "end": v(4.27, 147.1) * mm});
            skLineSegment(sketch, "E2517", {"start": v(4.27, 147.1) * mm, "end": v(4.45, 147) * mm});
            skLineSegment(sketch, "E2518", {"start": v(4.45, 147) * mm, "end": v(4.76, 146.9) * mm});
            skLineSegment(sketch, "E2519", {"start": v(4.76, 146.9) * mm, "end": v(5.16, 146.74) * mm});
            skLineSegment(sketch, "E2520", {"start": v(5.16, 146.74) * mm, "end": v(5.3, 146.69) * mm});
            skLineSegment(sketch, "E2521", {"start": v(5.3, 146.69) * mm, "end": v(5.32, 146.69) * mm});
            skLineSegment(sketch, "E2522", {"start": v(5.32, 146.69) * mm, "end": v(5.4, 146.65) * mm});
            skLineSegment(sketch, "E2523", {"start": v(5.4, 146.65) * mm, "end": v(5.4, 146.65) * mm});
            skLineSegment(sketch, "E2524", {"start": v(5.4, 146.65) * mm, "end": v(5.42, 146.64) * mm});
            skLineSegment(sketch, "E2525", {"start": v(5.42, 146.64) * mm, "end": v(5.47, 146.6) * mm});
            skLineSegment(sketch, "E2526", {"start": v(5.47, 146.6) * mm, "end": v(5.43, 146.69) * mm});
            skLineSegment(sketch, "E2527", {"start": v(5.43, 146.69) * mm, "end": v(5.41, 146.7) * mm});
            skLineSegment(sketch, "E2528", {"start": v(5.41, 146.7) * mm, "end": v(5.2, 147) * mm});
            skLineSegment(sketch, "E2529", {"start": v(5.2, 147) * mm, "end": v(5.17, 147.03) * mm});
            skLineSegment(sketch, "E2530", {"start": v(5.17, 147.03) * mm, "end": v(5.13, 147.1) * mm});
            skLineSegment(sketch, "E2531", {"start": v(5.13, 147.1) * mm, "end": v(5.08, 147.34) * mm});
            skLineSegment(sketch, "E2532", {"start": v(5.08, 147.34) * mm, "end": v(5.26, 147.46) * mm});
            skLineSegment(sketch, "E2533", {"start": v(5.26, 147.46) * mm, "end": v(5.56, 147.44) * mm});
            skLineSegment(sketch, "E2534", {"start": v(5.56, 147.44) * mm, "end": v(5.8, 147.35) * mm});
            skLineSegment(sketch, "E2535", {"start": v(5.8, 147.35) * mm, "end": v(5.86, 147.3) * mm});
            skLineSegment(sketch, "E2536", {"start": v(5.86, 147.3) * mm, "end": v(5.96, 147.22) * mm});
            skLineSegment(sketch, "E2537", {"start": v(5.96, 147.22) * mm, "end": v(6.15, 146.84) * mm});
            skLineSegment(sketch, "E2538", {"start": v(6.15, 146.84) * mm, "end": v(6.06, 146.53) * mm});
            skLineSegment(sketch, "E2539", {"start": v(6.06, 146.53) * mm, "end": v(6.04, 146.45) * mm});
            skLineSegment(sketch, "E2540", {"start": v(6.04, 146.45) * mm, "end": v(6.04, 146.44) * mm});
            skLineSegment(sketch, "E2541", {"start": v(6.04, 146.44) * mm, "end": v(6.05, 146.41) * mm});
            skLineSegment(sketch, "E2542", {"start": v(6.05, 146.41) * mm, "end": v(6.06, 146.41) * mm});
            skLineSegment(sketch, "E2543", {"start": v(6.06, 146.41) * mm, "end": v(6.17, 146.38) * mm});
            skLineSegment(sketch, "E2544", {"start": v(6.17, 146.38) * mm, "end": v(6.65, 146.28) * mm});
            skLineSegment(sketch, "E2545", {"start": v(6.65, 146.28) * mm, "end": v(7, 146.23) * mm});
            skLineSegment(sketch, "E2546", {"start": v(7, 146.23) * mm, "end": v(7.06, 146.22) * mm});
            skLineSegment(sketch, "E2547", {"start": v(7.06, 146.22) * mm, "end": v(7.17, 146.2) * mm});
            skLineSegment(sketch, "E2548", {"start": v(7.17, 146.2) * mm, "end": v(7.54, 146.33) * mm});
            skLineSegment(sketch, "E2549", {"start": v(7.54, 146.33) * mm, "end": v(7.7, 146.57) * mm});
            skLineSegment(sketch, "E2550", {"start": v(7.7, 146.57) * mm, "end": v(7.72, 146.6) * mm});
            skLineSegment(sketch, "E2551", {"start": v(7.72, 146.6) * mm, "end": v(7.74, 146.65) * mm});
            skLineSegment(sketch, "E2552", {"start": v(7.74, 146.65) * mm, "end": v(7.69, 146.82) * mm});
            skLineSegment(sketch, "E2553", {"start": v(7.69, 146.82) * mm, "end": v(7.47, 146.96) * mm});
            skLineSegment(sketch, "E2554", {"start": v(7.47, 146.96) * mm, "end": v(7.19, 147.18) * mm});
            skLineSegment(sketch, "E2555", {"start": v(7.19, 147.18) * mm, "end": v(7.01, 147.54) * mm});
            skLineSegment(sketch, "E2556", {"start": v(7.01, 147.54) * mm, "end": v(7, 147.66) * mm});
            skLineSegment(sketch, "E2557", {"start": v(7, 147.66) * mm, "end": v(6.97, 147.82) * mm});
            skLineSegment(sketch, "E2558", {"start": v(6.97, 147.82) * mm, "end": v(7, 148.33) * mm});
            skLineSegment(sketch, "E2559", {"start": v(7, 148.33) * mm, "end": v(7.19, 148.93) * mm});
            skLineSegment(sketch, "E2560", {"start": v(7.19, 148.93) * mm, "end": v(7.5, 149.43) * mm});
            skLineSegment(sketch, "E2561", {"start": v(7.5, 149.43) * mm, "end": v(7.74, 149.72) * mm});
            skLineSegment(sketch, "E2562", {"start": v(7.74, 149.72) * mm, "end": v(7.84, 149.8) * mm});
            skLineSegment(sketch, "E2563", {"start": v(7.84, 149.8) * mm, "end": v(7.88, 149.84) * mm});
            skLineSegment(sketch, "E2564", {"start": v(7.88, 149.84) * mm, "end": v(8.52, 150.24) * mm});
            skLineSegment(sketch, "E2565", {"start": v(8.52, 150.24) * mm, "end": v(8.59, 150.27) * mm});
            skLineSegment(sketch, "E2566", {"start": v(8.59, 150.27) * mm, "end": v(8.63, 150.3) * mm});
            skLineSegment(sketch, "E2567", {"start": v(8.63, 150.3) * mm, "end": v(8.97, 150.47) * mm});
            skLineSegment(sketch, "E2568", {"start": v(8.97, 150.47) * mm, "end": v(9, 150.49) * mm});
            skLineSegment(sketch, "E2569", {"start": v(9, 150.49) * mm, "end": v(9.02, 150.5) * mm});
            skLineSegment(sketch, "E2570", {"start": v(9.02, 150.5) * mm, "end": v(9.33, 150.67) * mm});
            skLineSegment(sketch, "E2571", {"start": v(9.33, 150.67) * mm, "end": v(9.35, 150.68) * mm});
            skLineSegment(sketch, "E2572", {"start": v(9.35, 150.68) * mm, "end": v(9.38, 150.7) * mm});
            skLineSegment(sketch, "E2573", {"start": v(9.38, 150.7) * mm, "end": v(9.6, 150.85) * mm});
            skLineSegment(sketch, "E2574", {"start": v(9.6, 150.85) * mm, "end": v(9.62, 150.88) * mm});
            skLineSegment(sketch, "E2575", {"start": v(9.62, 150.88) * mm, "end": v(9.63, 150.9) * mm});
            skLineSegment(sketch, "E2576", {"start": v(9.63, 150.9) * mm, "end": v(9.64, 151.06) * mm});
            skLineSegment(sketch, "E2577", {"start": v(9.64, 151.06) * mm, "end": v(9.63, 151.07) * mm});
            skLineSegment(sketch, "E2578", {"start": v(9.63, 151.07) * mm, "end": v(9.62, 151.07) * mm});
            skLineSegment(sketch, "E2579", {"start": v(9.62, 151.07) * mm, "end": v(9.47, 151.07) * mm});
            skLineSegment(sketch, "E2580", {"start": v(9.47, 151.07) * mm, "end": v(9.45, 151.07) * mm});
            skLineSegment(sketch, "E2581", {"start": v(9.45, 151.07) * mm, "end": v(9.4, 151.06) * mm});
            skLineSegment(sketch, "E2582", {"start": v(9.4, 151.06) * mm, "end": v(8.73, 151.04) * mm});
            skLineSegment(sketch, "E2583", {"start": v(8.73, 151.04) * mm, "end": v(8.65, 151.05) * mm});
            skLineSegment(sketch, "E2584", {"start": v(8.65, 151.05) * mm, "end": v(8.42, 151.05) * mm});
            skLineSegment(sketch, "E2585", {"start": v(8.42, 151.05) * mm, "end": v(7.82, 151.11) * mm});
            skLineSegment(sketch, "E2586", {"start": v(7.82, 151.11) * mm, "end": v(7.74, 151.12) * mm});
            skLineSegment(sketch, "E2587", {"start": v(7.74, 151.12) * mm, "end": v(7.7, 151.12) * mm});
            skLineSegment(sketch, "E2588", {"start": v(7.7, 151.12) * mm, "end": v(7.3, 151.17) * mm});
            skLineSegment(sketch, "E2589", {"start": v(7.3, 151.17) * mm, "end": v(7.27, 151.18) * mm});
            skLineSegment(sketch, "E2590", {"start": v(7.27, 151.18) * mm, "end": v(7.22, 151.19) * mm});
            skLineSegment(sketch, "E2591", {"start": v(7.22, 151.19) * mm, "end": v(6.7, 151.27) * mm});
            skLineSegment(sketch, "E2592", {"start": v(6.7, 151.27) * mm, "end": v(6.64, 151.28) * mm});
            skLineSegment(sketch, "E2593", {"start": v(6.64, 151.28) * mm, "end": v(6.46, 151.32) * mm});
            skLineSegment(sketch, "E2594", {"start": v(6.46, 151.32) * mm, "end": v(5.76, 151.49) * mm});
            skLineSegment(sketch, "E2595", {"start": v(5.76, 151.49) * mm, "end": v(5, 151.7) * mm});
            skLineSegment(sketch, "E2596", {"start": v(5, 151.7) * mm, "end": v(4.8, 151.75) * mm});
            skLineSegment(sketch, "E2597", {"start": v(4.8, 151.75) * mm, "end": v(4.71, 151.75) * mm});
            skLineSegment(sketch, "E2598", {"start": v(4.71, 151.75) * mm, "end": v(4.5, 151.82) * mm});
            skLineSegment(sketch, "E2599", {"start": v(4.5, 151.82) * mm, "end": v(4.48, 151.82) * mm});
            skLineSegment(sketch, "E2600", {"start": v(4.48, 151.82) * mm, "end": v(4.36, 151.86) * mm});
            skLineSegment(sketch, "E2601", {"start": v(4.36, 151.86) * mm, "end": v(4.1, 151.95) * mm});
            skLineSegment(sketch, "E2602", {"start": v(4.1, 151.95) * mm, "end": v(3.79, 152.04) * mm});
            skLineSegment(sketch, "E2603", {"start": v(3.79, 152.04) * mm, "end": v(3.62, 152.08) * mm});
            skLineSegment(sketch, "E2604", {"start": v(3.62, 152.08) * mm, "end": v(3.58, 152.1) * mm});
            skLineSegment(sketch, "E2605", {"start": v(3.58, 152.1) * mm, "end": v(3.47, 152.12) * mm});
            skLineSegment(sketch, "E2606", {"start": v(3.47, 152.12) * mm, "end": v(2.47, 152.27) * mm});
            skLineSegment(sketch, "E2607", {"start": v(2.47, 152.27) * mm, "end": v(2.36, 152.27) * mm});
            skLineSegment(sketch, "E2608", {"start": v(2.36, 152.27) * mm, "end": v(2.28, 152.27) * mm});
            skLineSegment(sketch, "E2609", {"start": v(2.28, 152.27) * mm, "end": v(1.6, 152.24) * mm});
            skLineSegment(sketch, "E2610", {"start": v(1.6, 152.24) * mm, "end": v(1.55, 152.24) * mm});
            skLineSegment(sketch, "E2611", {"start": v(1.55, 152.24) * mm, "end": v(1.36, 152.24) * mm});
            skLineSegment(sketch, "E2612", {"start": v(1.36, 152.24) * mm, "end": v(0.5, 152.16) * mm});
            skLineSegment(sketch, "E2613", {"start": v(0.5, 152.16) * mm, "end": v(-0.46, 152.15) * mm});
            skLineSegment(sketch, "E2614", {"start": v(-0.46, 152.15) * mm, "end": v(-0.69, 152.17) * mm});
            skLineSegment(sketch, "E2615", {"start": v(-0.69, 152.17) * mm, "end": v(-0.88, 152.2) * mm});
            skLineSegment(sketch, "E2616", {"start": v(-0.88, 152.2) * mm, "end": v(-1.44, 152.32) * mm});
            skLineSegment(sketch, "E2617", {"start": v(-1.44, 152.32) * mm, "end": v(-1.83, 152.49) * mm});
            skLineSegment(sketch, "E2618", {"start": v(-1.83, 152.49) * mm, "end": v(-1.86, 152.64) * mm});
            skLineSegment(sketch, "E2619", {"start": v(-1.86, 152.64) * mm, "end": v(-1.6, 152.71) * mm});
            skLineSegment(sketch, "E2620", {"start": v(-1.6, 152.71) * mm, "end": v(-1.5, 152.71) * mm});
            skLineSegment(sketch, "E2621", {"start": v(-1.5, 152.71) * mm, "end": v(-1.42, 152.72) * mm});
            skLineSegment(sketch, "E2622", {"start": v(-1.42, 152.72) * mm, "end": v(-0.9, 152.85) * mm});
            skLineSegment(sketch, "E2623", {"start": v(-0.9, 152.85) * mm, "end": v(-0.34, 152.96) * mm});
            skLineSegment(sketch, "E2624", {"start": v(-0.34, 152.96) * mm, "end": v(-0.15, 152.96) * mm});
            skLineSegment(sketch, "E2625", {"start": v(-0.15, 152.96) * mm, "end": v(0.02, 152.96) * mm});
            skLineSegment(sketch, "E2626", {"start": v(0.02, 152.96) * mm, "end": v(1.82, 152.87) * mm});
            skLineSegment(sketch, "E2627", {"start": v(1.82, 152.87) * mm, "end": v(2, 152.85) * mm});
            skLineSegment(sketch, "E2628", {"start": v(2, 152.85) * mm, "end": v(2.07, 152.84) * mm});
            skLineSegment(sketch, "E2629", {"start": v(2.07, 152.84) * mm, "end": v(2.8, 152.75) * mm});
            skLineSegment(sketch, "E2630", {"start": v(2.8, 152.75) * mm, "end": v(2.86, 152.73) * mm});
            skLineSegment(sketch, "E2631", {"start": v(2.86, 152.73) * mm, "end": v(2.92, 152.72) * mm});
            skLineSegment(sketch, "E2632", {"start": v(2.92, 152.72) * mm, "end": v(3.47, 152.55) * mm});
            skLineSegment(sketch, "E2633", {"start": v(3.47, 152.55) * mm, "end": v(3.52, 152.53) * mm});
            skLineSegment(sketch, "E2634", {"start": v(3.52, 152.53) * mm, "end": v(3.59, 152.5) * mm});
            skLineSegment(sketch, "E2635", {"start": v(3.59, 152.5) * mm, "end": v(4.03, 152.34) * mm});
            skLineSegment(sketch, "E2636", {"start": v(4.03, 152.34) * mm, "end": v(4.08, 152.33) * mm});
            skLineSegment(sketch, "E2637", {"start": v(4.08, 152.33) * mm, "end": v(4.12, 152.31) * mm});
            skLineSegment(sketch, "E2638", {"start": v(4.12, 152.31) * mm, "end": v(4.36, 152.23) * mm});
            skLineSegment(sketch, "E2639", {"start": v(4.36, 152.23) * mm, "end": v(4.4, 152.22) * mm});
            skLineSegment(sketch, "E2640", {"start": v(4.4, 152.22) * mm, "end": v(4.41, 152.22) * mm});
            skLineSegment(sketch, "E2641", {"start": v(4.41, 152.22) * mm, "end": v(4.57, 152.16) * mm});
            skLineSegment(sketch, "E2642", {"start": v(4.57, 152.16) * mm, "end": v(4.59, 152.15) * mm});
            skLineSegment(sketch, "E2643", {"start": v(4.59, 152.15) * mm, "end": v(4.64, 152.36) * mm});
            skLineSegment(sketch, "E2644", {"start": v(4.64, 152.36) * mm, "end": v(4.98, 153.78) * mm});
            skLineSegment(sketch, "E2645", {"start": v(4.98, 153.78) * mm, "end": v(5.38, 155.36) * mm});
            skLineSegment(sketch, "E2646", {"start": v(5.38, 155.36) * mm, "end": v(5.45, 155.65) * mm});
            skLineSegment(sketch, "E2647", {"start": v(5.45, 155.65) * mm, "end": v(5.52, 155.9) * mm});
            skLineSegment(sketch, "E2648", {"start": v(5.52, 155.9) * mm, "end": v(5.66, 156.65) * mm});
            skLineSegment(sketch, "E2649", {"start": v(5.66, 156.65) * mm, "end": v(5.87, 157.93) * mm});
            skLineSegment(sketch, "E2650", {"start": v(5.87, 157.93) * mm, "end": v(6.05, 159.26) * mm});
            skLineSegment(sketch, "E2651", {"start": v(6.05, 159.26) * mm, "end": v(6.15, 160.14) * mm});
            skLineSegment(sketch, "E2652", {"start": v(6.15, 160.14) * mm, "end": v(6.19, 160.43) * mm});
            skLineSegment(sketch, "E2653", {"start": v(6.19, 160.43) * mm, "end": v(6.26, 160.41) * mm});
            skLineSegment(sketch, "E2654", {"start": v(6.26, 160.41) * mm, "end": v(6.65, 160.3) * mm});
            skLineSegment(sketch, "E2655", {"start": v(6.65, 160.3) * mm, "end": v(7.62, 160.05) * mm});
            skLineSegment(sketch, "E2656", {"start": v(7.62, 160.05) * mm, "end": v(9.15, 159.73) * mm});
            skLineSegment(sketch, "E2657", {"start": v(9.15, 159.73) * mm, "end": v(10.76, 159.45) * mm});
            skLineSegment(sketch, "E2658", {"start": v(10.76, 159.45) * mm, "end": v(11.3, 159.37) * mm});
            skLineSegment(sketch, "E2659", {"start": v(11.3, 159.37) * mm, "end": v(11.84, 159.29) * mm});
            skLineSegment(sketch, "E2660", {"start": v(11.84, 159.29) * mm, "end": v(13.48, 159.14) * mm});
            skLineSegment(sketch, "E2661", {"start": v(13.48, 159.14) * mm, "end": v(15.36, 159.08) * mm});
            skLineSegment(sketch, "E2662", {"start": v(15.36, 159.08) * mm, "end": v(16.77, 159.14) * mm});
            skLineSegment(sketch, "E2663", {"start": v(16.77, 159.14) * mm, "end": v(17.4, 159.22) * mm});
            skLineSegment(sketch, "E2664", {"start": v(17.4, 159.22) * mm, "end": v(17.52, 159.27) * mm});
            skLineSegment(sketch, "E2665", {"start": v(17.52, 159.27) * mm, "end": v(17.62, 159.3) * mm});
            skLineSegment(sketch, "E2666", {"start": v(17.62, 159.3) * mm, "end": v(17.94, 159.44) * mm});
            skLineSegment(sketch, "E2667", {"start": v(17.94, 159.44) * mm, "end": v(18.45, 159.73) * mm});
            skLineSegment(sketch, "E2668", {"start": v(18.45, 159.73) * mm, "end": v(18.88, 160.08) * mm});
            skLineSegment(sketch, "E2669", {"start": v(18.88, 160.08) * mm, "end": v(19.08, 160.36) * mm});
            skLineSegment(sketch, "E2670", {"start": v(19.08, 160.36) * mm, "end": v(19.1, 160.46) * mm});
            skLineSegment(sketch, "E2671", {"start": v(19.1, 160.46) * mm, "end": v(19.12, 160.66) * mm});
            skLineSegment(sketch, "E2672", {"start": v(19.12, 160.66) * mm, "end": v(18.94, 161.3) * mm});
            skLineSegment(sketch, "E2673", {"start": v(18.94, 161.3) * mm, "end": v(18.39, 162.42) * mm});
            skLineSegment(sketch, "E2674", {"start": v(18.39, 162.42) * mm, "end": v(17.6, 163.63) * mm});
            skLineSegment(sketch, "E2675", {"start": v(17.6, 163.63) * mm, "end": v(16.95, 164.48) * mm});
            skLineSegment(sketch, "E2676", {"start": v(16.95, 164.48) * mm, "end": v(16.72, 164.75) * mm});
            skLineSegment(sketch, "E2677", {"start": v(16.72, 164.75) * mm, "end": v(16.56, 164.94) * mm});
            skLineSegment(sketch, "E2678", {"start": v(16.56, 164.94) * mm, "end": v(15.92, 165.87) * mm});
            skLineSegment(sketch, "E2679", {"start": v(15.92, 165.87) * mm, "end": v(15.52, 166.65) * mm});
            skLineSegment(sketch, "E2680", {"start": v(15.52, 166.65) * mm, "end": v(15.48, 166.76) * mm});
            skLineSegment(sketch, "E2681", {"start": v(15.48, 166.76) * mm, "end": v(15.47, 166.78) * mm});
            skLineSegment(sketch, "E2682", {"start": v(15.47, 166.78) * mm, "end": v(15.44, 166.95) * mm});
            skLineSegment(sketch, "E2683", {"start": v(15.44, 166.95) * mm, "end": v(15.43, 166.96) * mm});
            skLineSegment(sketch, "E2684", {"start": v(15.43, 166.96) * mm, "end": v(15.43, 167.08) * mm});
            skLineSegment(sketch, "E2685", {"start": v(15.43, 167.08) * mm, "end": v(15.35, 167.53) * mm});
            skLineSegment(sketch, "E2686", {"start": v(15.35, 167.53) * mm, "end": v(15, 167.79) * mm});
            skLineSegment(sketch, "E2687", {"start": v(15, 167.79) * mm, "end": v(14.87, 167.8) * mm});
            skLineSegment(sketch, "E2688", {"start": v(14.87, 167.8) * mm, "end": v(14.84, 167.8) * mm});
            skLineSegment(sketch, "E2689", {"start": v(14.84, 167.8) * mm, "end": v(14.61, 167.76) * mm});
            skLineSegment(sketch, "E2690", {"start": v(14.61, 167.76) * mm, "end": v(14.6, 167.75) * mm});
            skLineSegment(sketch, "E2691", {"start": v(14.6, 167.75) * mm, "end": v(14.54, 167.75) * mm});
            skLineSegment(sketch, "E2692", {"start": v(14.54, 167.75) * mm, "end": v(14.4, 167.87) * mm});
            skLineSegment(sketch, "E2693", {"start": v(14.4, 167.87) * mm, "end": v(14.39, 167.9) * mm});
            skLineSegment(sketch, "E2694", {"start": v(14.39, 167.9) * mm, "end": v(14.38, 167.92) * mm});
            skLineSegment(sketch, "E2695", {"start": v(14.38, 167.92) * mm, "end": v(14.35, 167.98) * mm});
            skLineSegment(sketch, "E2696", {"start": v(14.35, 167.98) * mm, "end": v(14.35, 168) * mm});
            skLineSegment(sketch, "E2697", {"start": v(14.35, 168) * mm, "end": v(14.35, 168.03) * mm});
            skLineSegment(sketch, "E2698", {"start": v(14.35, 168.03) * mm, "end": v(14.35, 168.03) * mm});
            skLineSegment(sketch, "E2699", {"start": v(14.35, 168.03) * mm, "end": v(14.34, 168.05) * mm});
            skLineSegment(sketch, "E2700", {"start": v(14.34, 168.05) * mm, "end": v(14.33, 168.09) * mm});
            skLineSegment(sketch, "E2701", {"start": v(14.33, 168.09) * mm, "end": v(14.16, 168.25) * mm});
            skLineSegment(sketch, "E2702", {"start": v(14.16, 168.25) * mm, "end": v(14.14, 168.25) * mm});
            skLineSegment(sketch, "E2703", {"start": v(14.14, 168.25) * mm, "end": v(14.13, 168.26) * mm});
            skLineSegment(sketch, "E2704", {"start": v(14.13, 168.26) * mm, "end": v(14, 168.3) * mm});
            skLineSegment(sketch, "E2705", {"start": v(14, 168.3) * mm, "end": v(13.99, 168.3) * mm});
            skLineSegment(sketch, "E2706", {"start": v(13.99, 168.3) * mm, "end": v(13.96, 168.31) * mm});
            skLineSegment(sketch, "E2707", {"start": v(13.96, 168.31) * mm, "end": v(13.76, 168.57) * mm});
            skLineSegment(sketch, "E2708", {"start": v(13.76, 168.57) * mm, "end": v(13.74, 168.62) * mm});
            skLineSegment(sketch, "E2709", {"start": v(13.74, 168.62) * mm, "end": v(13.73, 168.67) * mm});
            skLineSegment(sketch, "E2710", {"start": v(13.73, 168.67) * mm, "end": v(13.63, 168.95) * mm});
            skLineSegment(sketch, "E2711", {"start": v(13.63, 168.95) * mm, "end": v(13.62, 168.98) * mm});
            skLineSegment(sketch, "E2712", {"start": v(13.62, 168.98) * mm, "end": v(13.62, 169.01) * mm});
            skLineSegment(sketch, "E2713", {"start": v(13.62, 169.01) * mm, "end": v(13.61, 169.03) * mm});
            skLineSegment(sketch, "E2714", {"start": v(13.61, 169.03) * mm, "end": v(13.61, 169.03) * mm});
            skLineSegment(sketch, "E2715", {"start": v(13.61, 169.03) * mm, "end": v(13.6, 169.08) * mm});
            skLineSegment(sketch, "E2716", {"start": v(13.6, 169.08) * mm, "end": v(13.51, 169.25) * mm});
            skLineSegment(sketch, "E2717", {"start": v(13.51, 169.25) * mm, "end": v(13.36, 169.43) * mm});
            skLineSegment(sketch, "E2718", {"start": v(13.36, 169.43) * mm, "end": v(13.31, 169.48) * mm});
            skLineSegment(sketch, "E2719", {"start": v(13.31, 169.48) * mm, "end": v(13.29, 169.49) * mm});
            skLineSegment(sketch, "E2720", {"start": v(13.29, 169.49) * mm, "end": v(13.29, 169.49) * mm});
            skLineSegment(sketch, "E2721", {"start": v(13.29, 169.49) * mm, "end": v(13.26, 169.53) * mm});
            skLineSegment(sketch, "E2722", {"start": v(13.26, 169.53) * mm, "end": v(12.99, 170.08) * mm});
            skLineSegment(sketch, "E2723", {"start": v(12.99, 170.08) * mm, "end": v(12.96, 170.15) * mm});
            skLineSegment(sketch, "E2724", {"start": v(12.96, 170.15) * mm, "end": v(12.89, 170.32) * mm});
            skLineSegment(sketch, "E2725", {"start": v(12.89, 170.32) * mm, "end": v(12.66, 170.99) * mm});
            skLineSegment(sketch, "E2726", {"start": v(12.66, 170.99) * mm, "end": v(12.54, 171.45) * mm});
            skLineSegment(sketch, "E2727", {"start": v(12.54, 171.45) * mm, "end": v(12.52, 171.51) * mm});
            skLineSegment(sketch, "E2728", {"start": v(12.52, 171.51) * mm, "end": v(12.5, 171.56) * mm});
            skLineSegment(sketch, "E2729", {"start": v(12.5, 171.56) * mm, "end": v(12.19, 171.83) * mm});
            skLineSegment(sketch, "E2730", {"start": v(12.19, 171.83) * mm, "end": v(12.16, 171.84) * mm});
            skLineSegment(sketch, "E2731", {"start": v(12.16, 171.84) * mm, "end": v(12.15, 171.85) * mm});
            skLineSegment(sketch, "E2732", {"start": v(12.15, 171.85) * mm, "end": v(11.99, 171.86) * mm});
            skLineSegment(sketch, "E2733", {"start": v(11.99, 171.86) * mm, "end": v(11.94, 171.86) * mm});
            skLineSegment(sketch, "E2734", {"start": v(11.94, 171.86) * mm, "end": v(11.87, 171.87) * mm});
            skLineSegment(sketch, "E2735", {"start": v(11.87, 171.87) * mm, "end": v(11.6, 171.93) * mm});
            skLineSegment(sketch, "E2736", {"start": v(11.6, 171.93) * mm, "end": v(11.56, 171.99) * mm});
            skLineSegment(sketch, "E2737", {"start": v(11.56, 171.99) * mm, "end": v(11.58, 172) * mm});
            skLineSegment(sketch, "E2738", {"start": v(11.58, 172) * mm, "end": v(11.98, 172) * mm});
            skLineSegment(sketch, "E2739", {"start": v(11.98, 172) * mm, "end": v(12.03, 172) * mm});
            skLineSegment(sketch, "E2740", {"start": v(12.03, 172) * mm, "end": v(12.02, 172.03) * mm});
            skLineSegment(sketch, "E2741", {"start": v(12.02, 172.03) * mm, "end": v(11.9, 172.33) * mm});
            skLineSegment(sketch, "E2742", {"start": v(11.9, 172.33) * mm, "end": v(11.88, 172.36) * mm});
            skLineSegment(sketch, "E2743", {"start": v(11.88, 172.36) * mm, "end": v(11.85, 172.43) * mm});
            skLineSegment(sketch, "E2744", {"start": v(11.85, 172.43) * mm, "end": v(11.66, 172.63) * mm});
            skLineSegment(sketch, "E2745", {"start": v(11.66, 172.63) * mm, "end": v(11.45, 172.7) * mm});
            skLineSegment(sketch, "E2746", {"start": v(11.45, 172.7) * mm, "end": v(11.41, 172.7) * mm});
            skLineSegment(sketch, "E2747", {"start": v(11.41, 172.7) * mm, "end": v(11.36, 172.71) * mm});
            skLineSegment(sketch, "E2748", {"start": v(11.36, 172.71) * mm, "end": v(11.16, 172.73) * mm});
            skLineSegment(sketch, "E2749", {"start": v(11.16, 172.73) * mm, "end": v(10.78, 172.73) * mm});
            skLineSegment(sketch, "E2750", {"start": v(10.78, 172.73) * mm, "end": v(10.4, 172.68) * mm});
            skLineSegment(sketch, "E2751", {"start": v(10.4, 172.68) * mm, "end": v(10.21, 172.62) * mm});
            skLineSegment(sketch, "E2752", {"start": v(10.21, 172.62) * mm, "end": v(10.19, 172.58) * mm});
            skLineSegment(sketch, "E2753", {"start": v(10.19, 172.58) * mm, "end": v(10.17, 172.55) * mm});
            skLineSegment(sketch, "E2754", {"start": v(10.17, 172.55) * mm, "end": v(10.17, 172.53) * mm});
            skLineSegment(sketch, "E2755", {"start": v(10.17, 172.53) * mm, "end": v(10.18, 172.54) * mm});
            skLineSegment(sketch, "E2756", {"start": v(10.18, 172.54) * mm, "end": v(10.31, 172.58) * mm});
            skLineSegment(sketch, "E2757", {"start": v(10.31, 172.58) * mm, "end": v(10.35, 172.58) * mm});
            skLineSegment(sketch, "E2758", {"start": v(10.35, 172.58) * mm, "end": v(10.4, 172.58) * mm});
            skLineSegment(sketch, "E2759", {"start": v(10.4, 172.58) * mm, "end": v(10.56, 172.5) * mm});
            skLineSegment(sketch, "E2760", {"start": v(10.56, 172.5) * mm, "end": v(10.65, 172.3) * mm});
            skLineSegment(sketch, "E2761", {"start": v(10.65, 172.3) * mm, "end": v(10.66, 172.24) * mm});
            skLineSegment(sketch, "E2762", {"start": v(10.66, 172.24) * mm, "end": v(10.67, 172.19) * mm});
            skLineSegment(sketch, "E2763", {"start": v(10.67, 172.19) * mm, "end": v(10.67, 171.97) * mm});
            skLineSegment(sketch, "E2764", {"start": v(10.67, 171.97) * mm, "end": v(10.63, 171.86) * mm});
            skLineSegment(sketch, "E2765", {"start": v(10.63, 171.86) * mm, "end": v(10.78, 171.87) * mm});
            skLineSegment(sketch, "E2766", {"start": v(10.78, 171.87) * mm, "end": v(10.96, 171.76) * mm});
            skLineSegment(sketch, "E2767", {"start": v(10.96, 171.76) * mm, "end": v(10.98, 171.71) * mm});
            skLineSegment(sketch, "E2768", {"start": v(10.98, 171.71) * mm, "end": v(10.99, 171.66) * mm});
            skLineSegment(sketch, "E2769", {"start": v(10.99, 171.66) * mm, "end": v(10.98, 171.4) * mm});
            skLineSegment(sketch, "E2770", {"start": v(10.98, 171.4) * mm, "end": v(10.95, 171.23) * mm});
            skLineSegment(sketch, "E2771", {"start": v(10.95, 171.23) * mm, "end": v(11.03, 171.27) * mm});
            skLineSegment(sketch, "E2772", {"start": v(11.03, 171.27) * mm, "end": v(11.2, 171.22) * mm});
            skLineSegment(sketch, "E2773", {"start": v(11.2, 171.22) * mm, "end": v(11.23, 171.18) * mm});
            skLineSegment(sketch, "E2774", {"start": v(11.23, 171.18) * mm, "end": v(11.24, 171.17) * mm});
            skLineSegment(sketch, "E2775", {"start": v(11.24, 171.17) * mm, "end": v(11.3, 171.08) * mm});
            skLineSegment(sketch, "E2776", {"start": v(11.3, 171.08) * mm, "end": v(11.3, 171.07) * mm});
            skLineSegment(sketch, "E2777", {"start": v(11.3, 171.07) * mm, "end": v(11.3, 171.05) * mm});
            skLineSegment(sketch, "E2778", {"start": v(11.3, 171.05) * mm, "end": v(11.28, 170.8) * mm});
            skLineSegment(sketch, "E2779", {"start": v(11.28, 170.8) * mm, "end": v(11.27, 170.76) * mm});
            skLineSegment(sketch, "E2780", {"start": v(11.27, 170.76) * mm, "end": v(11.26, 170.75) * mm});
            skLineSegment(sketch, "E2781", {"start": v(11.26, 170.75) * mm, "end": v(11.22, 170.6) * mm});
            skLineSegment(sketch, "E2782", {"start": v(11.22, 170.6) * mm, "end": v(11.22, 170.58) * mm});
            skLineSegment(sketch, "E2783", {"start": v(11.22, 170.58) * mm, "end": v(11.21, 170.57) * mm});
            skLineSegment(sketch, "E2784", {"start": v(11.21, 170.57) * mm, "end": v(11.1, 170.47) * mm});
            skLineSegment(sketch, "E2785", {"start": v(11.1, 170.47) * mm, "end": v(11.1, 170.46) * mm});
            skLineSegment(sketch, "E2786", {"start": v(11.1, 170.46) * mm, "end": v(11.1, 170.45) * mm});
            skLineSegment(sketch, "E2787", {"start": v(11.1, 170.45) * mm, "end": v(11.08, 170.3) * mm});
            skLineSegment(sketch, "E2788", {"start": v(11.08, 170.3) * mm, "end": v(11.08, 170.27) * mm});
            skLineSegment(sketch, "E2789", {"start": v(11.08, 170.27) * mm, "end": v(11.07, 170.25) * mm});
            skLineSegment(sketch, "E2790", {"start": v(11.07, 170.25) * mm, "end": v(10.94, 169.94) * mm});
            skLineSegment(sketch, "E2791", {"start": v(10.94, 169.94) * mm, "end": v(10.92, 169.91) * mm});
            skLineSegment(sketch, "E2792", {"start": v(10.92, 169.91) * mm, "end": v(10.9, 169.9) * mm});
            skLineSegment(sketch, "E2793", {"start": v(10.9, 169.9) * mm, "end": v(10.8, 169.84) * mm});
            skLineSegment(sketch, "E2794", {"start": v(10.8, 169.84) * mm, "end": v(10.76, 169.84) * mm});
            skLineSegment(sketch, "E2795", {"start": v(10.76, 169.84) * mm, "end": v(10.72, 169.84) * mm});
            skLineSegment(sketch, "E2796", {"start": v(10.72, 169.84) * mm, "end": v(10.62, 169.91) * mm});
            skLineSegment(sketch, "E2797", {"start": v(10.62, 169.91) * mm, "end": v(10.58, 169.98) * mm});
            skLineSegment(sketch, "E2798", {"start": v(10.58, 169.98) * mm, "end": v(10.45, 169.81) * mm});
            skLineSegment(sketch, "E2799", {"start": v(10.45, 169.81) * mm, "end": v(10.21, 169.62) * mm});
            skLineSegment(sketch, "E2800", {"start": v(10.21, 169.62) * mm, "end": v(10.17, 169.61) * mm});
            skLineSegment(sketch, "E2801", {"start": v(10.17, 169.61) * mm, "end": v(10.13, 169.6) * mm});
            skLineSegment(sketch, "E2802", {"start": v(10.13, 169.6) * mm, "end": v(9.99, 169.68) * mm});
            skLineSegment(sketch, "E2803", {"start": v(9.99, 169.68) * mm, "end": v(9.92, 169.82) * mm});
            skLineSegment(sketch, "E2804", {"start": v(9.92, 169.82) * mm, "end": v(9.9, 169.84) * mm});
            skLineSegment(sketch, "E2805", {"start": v(9.9, 169.84) * mm, "end": v(9.9, 169.87) * mm});
            skLineSegment(sketch, "E2806", {"start": v(9.9, 169.87) * mm, "end": v(9.84, 170.33) * mm});
            skLineSegment(sketch, "E2807", {"start": v(9.84, 170.33) * mm, "end": v(9.74, 170.93) * mm});
            skLineSegment(sketch, "E2808", {"start": v(9.74, 170.93) * mm, "end": v(9.72, 171.02) * mm});
            skLineSegment(sketch, "E2809", {"start": v(9.72, 171.02) * mm, "end": v(9.72, 171.04) * mm});
            skLineSegment(sketch, "E2810", {"start": v(9.72, 171.04) * mm, "end": v(9.72, 171.29) * mm});
            skLineSegment(sketch, "E2811", {"start": v(9.72, 171.29) * mm, "end": v(9.74, 171.36) * mm});
            skLineSegment(sketch, "E2812", {"start": v(9.74, 171.36) * mm, "end": v(9.74, 171.37) * mm});
            skLineSegment(sketch, "E2813", {"start": v(9.74, 171.37) * mm, "end": v(9.75, 171.39) * mm});
            skLineSegment(sketch, "E2814", {"start": v(9.75, 171.39) * mm, "end": v(9.79, 171.57) * mm});
            skLineSegment(sketch, "E2815", {"start": v(9.79, 171.57) * mm, "end": v(9.8, 171.59) * mm});
            skLineSegment(sketch, "E2816", {"start": v(9.8, 171.59) * mm, "end": v(9.8, 171.64) * mm});
            skLineSegment(sketch, "E2817", {"start": v(9.8, 171.64) * mm, "end": v(9.85, 171.88) * mm});
            skLineSegment(sketch, "E2818", {"start": v(9.85, 171.88) * mm, "end": v(9.84, 172.02) * mm});
            skLineSegment(sketch, "E2819", {"start": v(9.84, 172.02) * mm, "end": v(9.84, 172.02) * mm});
            skLineSegment(sketch, "E2820", {"start": v(9.84, 172.02) * mm, "end": v(9.83, 172) * mm});
            skLineSegment(sketch, "E2821", {"start": v(9.83, 172) * mm, "end": v(9.7, 171.73) * mm});
            skLineSegment(sketch, "E2822", {"start": v(9.7, 171.73) * mm, "end": v(9.54, 171.3) * mm});
            skLineSegment(sketch, "E2823", {"start": v(9.54, 171.3) * mm, "end": v(9.54, 171.2) * mm});
            skLineSegment(sketch, "E2824", {"start": v(9.54, 171.2) * mm, "end": v(9.54, 171.12) * mm});
            skLineSegment(sketch, "E2825", {"start": v(9.54, 171.12) * mm, "end": v(9.54, 170.86) * mm});
            skLineSegment(sketch, "E2826", {"start": v(9.54, 170.86) * mm, "end": v(9.52, 170.57) * mm});
            skLineSegment(sketch, "E2827", {"start": v(9.52, 170.57) * mm, "end": v(9.52, 170.56) * mm});
            skLineSegment(sketch, "E2828", {"start": v(9.52, 170.56) * mm, "end": v(9.47, 170.58) * mm});
            skLineSegment(sketch, "E2829", {"start": v(9.47, 170.58) * mm, "end": v(9.47, 170.58) * mm});
            skLineSegment(sketch, "E2830", {"start": v(9.47, 170.58) * mm, "end": v(9.45, 170.61) * mm});
            skLineSegment(sketch, "E2831", {"start": v(9.45, 170.61) * mm, "end": v(9.26, 170.88) * mm});
            skLineSegment(sketch, "E2832", {"start": v(9.26, 170.88) * mm, "end": v(9.24, 170.9) * mm});
            skLineSegment(sketch, "E2833", {"start": v(9.24, 170.9) * mm, "end": v(9.2, 170.95) * mm});
            skLineSegment(sketch, "E2834", {"start": v(9.2, 170.95) * mm, "end": v(8.86, 171.16) * mm});
            skLineSegment(sketch, "E2835", {"start": v(8.86, 171.16) * mm, "end": v(8.5, 171.17) * mm});
            skLineSegment(sketch, "E2836", {"start": v(8.5, 171.17) * mm, "end": v(8.43, 171.12) * mm});
            skLineSegment(sketch, "E2837", {"start": v(8.43, 171.12) * mm, "end": v(8.4, 171.1) * mm});
            skLineSegment(sketch, "E2838", {"start": v(8.4, 171.1) * mm, "end": v(8.43, 170.9) * mm});
            skLineSegment(sketch, "E2839", {"start": v(8.43, 170.9) * mm, "end": v(8.64, 170.63) * mm});
            skLineSegment(sketch, "E2840", {"start": v(8.64, 170.63) * mm, "end": v(8.68, 170.56) * mm});
            skLineSegment(sketch, "E2841", {"start": v(8.68, 170.56) * mm, "end": v(8.71, 170.5) * mm});
            skLineSegment(sketch, "E2842", {"start": v(8.71, 170.5) * mm, "end": v(9.05, 169.75) * mm});
            skLineSegment(sketch, "E2843", {"start": v(9.05, 169.75) * mm, "end": v(9.08, 169.67) * mm});
            skLineSegment(sketch, "E2844", {"start": v(9.08, 169.67) * mm, "end": v(9.12, 169.59) * mm});
            skLineSegment(sketch, "E2845", {"start": v(9.12, 169.59) * mm, "end": v(9.26, 169.3) * mm});
            skLineSegment(sketch, "E2846", {"start": v(9.26, 169.3) * mm, "end": v(9.43, 169.06) * mm});
            skLineSegment(sketch, "E2847", {"start": v(9.43, 169.06) * mm, "end": v(9.5, 169) * mm});
            skLineSegment(sketch, "E2848", {"start": v(9.5, 169) * mm, "end": v(9.55, 168.95) * mm});
            skLineSegment(sketch, "E2849", {"start": v(9.55, 168.95) * mm, "end": v(10.03, 168.61) * mm});
            skLineSegment(sketch, "E2850", {"start": v(10.03, 168.61) * mm, "end": v(10.57, 168.3) * mm});
            skLineSegment(sketch, "E2851", {"start": v(10.57, 168.3) * mm, "end": v(10.66, 168.25) * mm});
            skLineSegment(sketch, "E2852", {"start": v(10.66, 168.25) * mm, "end": v(10.75, 168.21) * mm});
            skLineSegment(sketch, "E2853", {"start": v(10.75, 168.21) * mm, "end": v(11.23, 167.95) * mm});
            skLineSegment(sketch, "E2854", {"start": v(11.23, 167.95) * mm, "end": v(11.65, 167.66) * mm});
            skLineSegment(sketch, "E2855", {"start": v(11.65, 167.66) * mm, "end": v(11.7, 167.61) * mm});
            skLineSegment(sketch, "E2856", {"start": v(11.7, 167.61) * mm, "end": v(11.72, 167.6) * mm});
            skLineSegment(sketch, "E2857", {"start": v(11.72, 167.6) * mm, "end": v(11.86, 167.45) * mm});
            skLineSegment(sketch, "E2858", {"start": v(11.86, 167.45) * mm, "end": v(11.88, 167.42) * mm});
            skLineSegment(sketch, "E2859", {"start": v(11.88, 167.42) * mm, "end": v(11.9, 167.4) * mm});
            skLineSegment(sketch, "E2860", {"start": v(11.9, 167.4) * mm, "end": v(12.02, 167.22) * mm});
            skLineSegment(sketch, "E2861", {"start": v(12.02, 167.22) * mm, "end": v(12.03, 167.2) * mm});
            skLineSegment(sketch, "E2862", {"start": v(12.03, 167.2) * mm, "end": v(12.03, 167.2) * mm});
            skLineSegment(sketch, "E2863", {"start": v(12.03, 167.2) * mm, "end": v(12.17, 167.13) * mm});
            skLineSegment(sketch, "E2864", {"start": v(12.17, 167.13) * mm, "end": v(12.18, 167.12) * mm});
            skLineSegment(sketch, "E2865", {"start": v(12.18, 167.12) * mm, "end": v(12.19, 167.12) * mm});
            skLineSegment(sketch, "E2866", {"start": v(12.19, 167.12) * mm, "end": v(12.25, 167.1) * mm});
            skLineSegment(sketch, "E2867", {"start": v(12.25, 167.1) * mm, "end": v(12.27, 167.1) * mm});
            skLineSegment(sketch, "E2868", {"start": v(12.27, 167.1) * mm, "end": v(12.41, 167.1) * mm});
            skLineSegment(sketch, "E2869", {"start": v(12.41, 167.1) * mm, "end": v(12.65, 167.1) * mm});
            skLineSegment(sketch, "E2870", {"start": v(12.65, 167.1) * mm, "end": v(12.73, 167.1) * mm});
            skLineSegment(sketch, "E2871", {"start": v(12.73, 167.1) * mm, "end": v(12.78, 167.1) * mm});
            skLineSegment(sketch, "E2872", {"start": v(12.78, 167.1) * mm, "end": v(12.93, 167.09) * mm});
            skLineSegment(sketch, "E2873", {"start": v(12.93, 167.09) * mm, "end": v(12.94, 167.08) * mm});
            skLineSegment(sketch, "E2874", {"start": v(12.94, 167.08) * mm, "end": v(12.97, 167.07) * mm});
            skLineSegment(sketch, "E2875", {"start": v(12.97, 167.07) * mm, "end": v(13.03, 166.95) * mm});
            skLineSegment(sketch, "E2876", {"start": v(13.03, 166.95) * mm, "end": v(13, 166.83) * mm});
            skLineSegment(sketch, "E2877", {"start": v(13, 166.83) * mm, "end": v(12.98, 166.82) * mm});
            skLineSegment(sketch, "E2878", {"start": v(12.98, 166.82) * mm, "end": v(12.97, 166.8) * mm});
            skLineSegment(sketch, "E2879", {"start": v(12.97, 166.8) * mm, "end": v(12.79, 166.64) * mm});
            skLineSegment(sketch, "E2880", {"start": v(12.79, 166.64) * mm, "end": v(12.76, 166.63) * mm});
            skLineSegment(sketch, "E2881", {"start": v(12.76, 166.63) * mm, "end": v(12.74, 166.62) * mm});
            skLineSegment(sketch, "E2882", {"start": v(12.74, 166.62) * mm, "end": v(12.6, 166.55) * mm});
            skLineSegment(sketch, "E2883", {"start": v(12.6, 166.55) * mm, "end": v(12.6, 166.55) * mm});
            skLineSegment(sketch, "E2884", {"start": v(12.6, 166.55) * mm, "end": v(12.57, 166.54) * mm});
            skLineSegment(sketch, "E2885", {"start": v(12.57, 166.54) * mm, "end": v(12.38, 166.49) * mm});
            skLineSegment(sketch, "E2886", {"start": v(12.38, 166.49) * mm, "end": v(12.36, 166.48) * mm});
            skLineSegment(sketch, "E2887", {"start": v(12.36, 166.48) * mm, "end": v(12.02, 166.48) * mm});
            skLineSegment(sketch, "E2888", {"start": v(12.02, 166.48) * mm, "end": v(11.94, 166.5) * mm});
            skLineSegment(sketch, "E2889", {"start": v(11.94, 166.5) * mm, "end": v(11.91, 166.5) * mm});
            skLineSegment(sketch, "E2890", {"start": v(11.91, 166.5) * mm, "end": v(11.72, 166.55) * mm});
            skLineSegment(sketch, "E2891", {"start": v(11.72, 166.55) * mm, "end": v(11.7, 166.55) * mm});
            skLineSegment(sketch, "E2892", {"start": v(11.7, 166.55) * mm, "end": v(11.68, 166.56) * mm});
            skLineSegment(sketch, "E2893", {"start": v(11.68, 166.56) * mm, "end": v(11.68, 166.57) * mm});
            skLineSegment(sketch, "E2894", {"start": v(11.68, 166.57) * mm, "end": v(11.67, 166.57) * mm});
            skLineSegment(sketch, "E2895", {"start": v(11.67, 166.57) * mm, "end": v(11.62, 166.59) * mm});
            skLineSegment(sketch, "E2896", {"start": v(11.62, 166.59) * mm, "end": v(11.6, 166.59) * mm});
            skLineSegment(sketch, "E2897", {"start": v(11.6, 166.59) * mm, "end": v(11.58, 166.6) * mm});
            skLineSegment(sketch, "E2898", {"start": v(11.58, 166.6) * mm, "end": v(11.53, 166.64) * mm});
            skLineSegment(sketch, "E2899", {"start": v(11.53, 166.64) * mm, "end": v(11.33, 166.81) * mm});
            skLineSegment(sketch, "E2900", {"start": v(11.33, 166.81) * mm, "end": v(11.21, 166.94) * mm});
            skLineSegment(sketch, "E2901", {"start": v(11.21, 166.94) * mm, "end": v(11.21, 166.95) * mm});
            skLineSegment(sketch, "E2902", {"start": v(11.21, 166.95) * mm, "end": v(11.19, 167) * mm});
            skLineSegment(sketch, "E2903", {"start": v(11.19, 167) * mm, "end": v(11.17, 167.01) * mm});
            skLineSegment(sketch, "E2904", {"start": v(11.17, 167.01) * mm, "end": v(11.01, 167.06) * mm});
            skLineSegment(sketch, "E2905", {"start": v(11.01, 167.06) * mm, "end": v(11, 167.05) * mm});
            skLineSegment(sketch, "E2906", {"start": v(11, 167.05) * mm, "end": v(10.96, 167.04) * mm});
            skLineSegment(sketch, "E2907", {"start": v(10.96, 167.04) * mm, "end": v(10.79, 166.94) * mm});
            skLineSegment(sketch, "E2908", {"start": v(10.79, 166.94) * mm, "end": v(10.7, 166.81) * mm});
            skLineSegment(sketch, "E2909", {"start": v(10.7, 166.81) * mm, "end": v(10.71, 166.79) * mm});
            skLineSegment(sketch, "E2910", {"start": v(10.71, 166.79) * mm, "end": v(10.74, 166.73) * mm});
            skLineSegment(sketch, "E2911", {"start": v(10.74, 166.73) * mm, "end": v(10.74, 166.7) * mm});
            skLineSegment(sketch, "E2912", {"start": v(10.74, 166.7) * mm, "end": v(10.77, 166.66) * mm});
            skLineSegment(sketch, "E2913", {"start": v(10.77, 166.66) * mm, "end": v(10.86, 166.3) * mm});
            skLineSegment(sketch, "E2914", {"start": v(10.86, 166.3) * mm, "end": v(10.85, 165.84) * mm});
            skLineSegment(sketch, "E2915", {"start": v(10.85, 165.84) * mm, "end": v(10.85, 165.76) * mm});
            skLineSegment(sketch, "E2916", {"start": v(10.85, 165.76) * mm, "end": v(10.84, 165.69) * mm});
            skLineSegment(sketch, "E2917", {"start": v(10.84, 165.69) * mm, "end": v(10.86, 165.47) * mm});
            skLineSegment(sketch, "E2918", {"start": v(10.86, 165.47) * mm, "end": v(10.92, 165.23) * mm});
            skLineSegment(sketch, "E2919", {"start": v(10.92, 165.23) * mm, "end": v(11.05, 165.15) * mm});
            skLineSegment(sketch, "E2920", {"start": v(11.05, 165.15) * mm, "end": v(11.21, 165.29) * mm});
            skLineSegment(sketch, "E2921", {"start": v(11.21, 165.29) * mm, "end": v(11.25, 165.35) * mm});
            skLineSegment(sketch, "E2922", {"start": v(11.25, 165.35) * mm, "end": v(11.27, 165.39) * mm});
            skLineSegment(sketch, "E2923", {"start": v(11.27, 165.39) * mm, "end": v(11.47, 165.42) * mm});
            skLineSegment(sketch, "E2924", {"start": v(11.47, 165.42) * mm, "end": v(11.74, 165.22) * mm});
            skLineSegment(sketch, "E2925", {"start": v(11.74, 165.22) * mm, "end": v(11.91, 164.92) * mm});
            skLineSegment(sketch, "E2926", {"start": v(11.91, 164.92) * mm, "end": v(11.88, 164.7) * mm});
            skLineSegment(sketch, "E2927", {"start": v(11.88, 164.7) * mm, "end": v(11.84, 164.68) * mm});
            skLineSegment(sketch, "E2928", {"start": v(11.84, 164.68) * mm, "end": v(11.79, 164.65) * mm});
            skLineSegment(sketch, "E2929", {"start": v(11.79, 164.65) * mm, "end": v(11.6, 164.6) * mm});
            skLineSegment(sketch, "E2930", {"start": v(11.6, 164.6) * mm, "end": v(11.38, 164.56) * mm});
            skLineSegment(sketch, "E2931", {"start": v(11.38, 164.56) * mm, "end": v(11.26, 164.51) * mm});
            skLineSegment(sketch, "E2932", {"start": v(11.26, 164.51) * mm, "end": v(11.28, 164.38) * mm});
            skLineSegment(sketch, "E2933", {"start": v(11.28, 164.38) * mm, "end": v(11.3, 164.34) * mm});
            skLineSegment(sketch, "E2934", {"start": v(11.3, 164.34) * mm, "end": v(11.35, 164.25) * mm});
            skLineSegment(sketch, "E2935", {"start": v(11.35, 164.25) * mm, "end": v(11.72, 164.05) * mm});
            skLineSegment(sketch, "E2936", {"start": v(11.72, 164.05) * mm, "end": v(12.22, 163.83) * mm});
            skLineSegment(sketch, "E2937", {"start": v(12.22, 163.83) * mm, "end": v(12.34, 163.73) * mm});
            skLineSegment(sketch, "E2938", {"start": v(12.34, 163.73) * mm, "end": v(12.35, 163.71) * mm});
            skLineSegment(sketch, "E2939", {"start": v(12.35, 163.71) * mm, "end": v(12.36, 163.7) * mm});
            skLineSegment(sketch, "E2940", {"start": v(12.36, 163.7) * mm, "end": v(12.46, 163.67) * mm});
            skLineSegment(sketch, "E2941", {"start": v(12.46, 163.67) * mm, "end": v(12.47, 163.67) * mm});
            skLineSegment(sketch, "E2942", {"start": v(12.47, 163.67) * mm, "end": v(12.64, 163.65) * mm});
            skLineSegment(sketch, "E2943", {"start": v(12.64, 163.65) * mm, "end": v(12.66, 163.64) * mm});
            skLineSegment(sketch, "E2944", {"start": v(12.66, 163.64) * mm, "end": v(12.72, 163.63) * mm});
            skLineSegment(sketch, "E2945", {"start": v(12.72, 163.63) * mm, "end": v(12.73, 163.63) * mm});
            skLineSegment(sketch, "E2946", {"start": v(12.73, 163.63) * mm, "end": v(12.8, 163.63) * mm});
            skLineSegment(sketch, "E2947", {"start": v(12.8, 163.63) * mm, "end": v(12.98, 163.64) * mm});
            skLineSegment(sketch, "E2948", {"start": v(12.98, 163.64) * mm, "end": v(13, 163.64) * mm});
            skLineSegment(sketch, "E2949", {"start": v(13, 163.64) * mm, "end": v(13.07, 163.65) * mm});
            skLineSegment(sketch, "E2950", {"start": v(13.07, 163.65) * mm, "end": v(13.5, 163.62) * mm});
            skLineSegment(sketch, "E2951", {"start": v(13.5, 163.62) * mm, "end": v(13.52, 163.6) * mm});
            skLineSegment(sketch, "E2952", {"start": v(13.52, 163.6) * mm, "end": v(13.52, 163.6) * mm});
            skLineSegment(sketch, "E2953", {"start": v(13.52, 163.6) * mm, "end": v(13.48, 163.43) * mm});
            skLineSegment(sketch, "E2954", {"start": v(13.48, 163.43) * mm, "end": v(13.45, 163.4) * mm});
            skLineSegment(sketch, "E2955", {"start": v(13.45, 163.4) * mm, "end": v(13.4, 163.38) * mm});
            skLineSegment(sketch, "E2956", {"start": v(13.4, 163.38) * mm, "end": v(13, 163.2) * mm});
            skLineSegment(sketch, "E2957", {"start": v(13, 163.2) * mm, "end": v(12.97, 163.2) * mm});
            skLineSegment(sketch, "E2958", {"start": v(12.97, 163.2) * mm, "end": v(13.01, 163.12) * mm});
            skLineSegment(sketch, "E2959", {"start": v(13.01, 163.12) * mm, "end": v(13.34, 162.5) * mm});
            skLineSegment(sketch, "E2960", {"start": v(13.34, 162.5) * mm, "end": v(13.36, 162.44) * mm});
            skLineSegment(sketch, "E2961", {"start": v(13.36, 162.44) * mm, "end": v(13.38, 162.41) * mm});
            skLineSegment(sketch, "E2962", {"start": v(13.38, 162.41) * mm, "end": v(13.54, 162.15) * mm});
            skLineSegment(sketch, "E2963", {"start": v(13.54, 162.15) * mm, "end": v(13.56, 162.12) * mm});
            skLineSegment(sketch, "E2964", {"start": v(13.56, 162.12) * mm, "end": v(13.6, 162.04) * mm});
            skLineSegment(sketch, "E2965", {"start": v(13.6, 162.04) * mm, "end": v(13.8, 161.83) * mm});
            skLineSegment(sketch, "E2966", {"start": v(13.8, 161.83) * mm, "end": v(14.13, 161.53) * mm});
            skLineSegment(sketch, "E2967", {"start": v(14.13, 161.53) * mm, "end": v(14.62, 161.16) * mm});
            skLineSegment(sketch, "E2968", {"start": v(14.62, 161.16) * mm, "end": v(15.15, 160.78) * mm});
            skLineSegment(sketch, "E2969", {"start": v(15.15, 160.78) * mm, "end": v(15.32, 160.66) * mm});
            skLineSegment(sketch, "E2970", {"start": v(15.32, 160.66) * mm, "end": v(15.24, 160.63) * mm});
            skLineSegment(sketch, "E2971", {"start": v(15.24, 160.63) * mm, "end": v(14.69, 160.85) * mm});
            skLineSegment(sketch, "E2972", {"start": v(14.69, 160.85) * mm, "end": v(13.95, 161.25) * mm});
            skLineSegment(sketch, "E2973", {"start": v(13.95, 161.25) * mm, "end": v(13.45, 161.6) * mm});
            skLineSegment(sketch, "E2974", {"start": v(13.45, 161.6) * mm, "end": v(13.31, 161.74) * mm});
            skLineSegment(sketch, "E2975", {"start": v(13.31, 161.74) * mm, "end": v(13.3, 161.75) * mm});
            skLineSegment(sketch, "E2976", {"start": v(13.3, 161.75) * mm, "end": v(13.21, 161.85) * mm});
            skLineSegment(sketch, "E2977", {"start": v(13.21, 161.85) * mm, "end": v(13.2, 161.86) * mm});
            skLineSegment(sketch, "E2978", {"start": v(13.2, 161.86) * mm, "end": v(13.17, 161.9) * mm});
            skLineSegment(sketch, "E2979", {"start": v(13.17, 161.9) * mm, "end": v(12.9, 162.37) * mm});
            skLineSegment(sketch, "E2980", {"start": v(12.9, 162.37) * mm, "end": v(12.89, 162.42) * mm});
            skLineSegment(sketch, "E2981", {"start": v(12.89, 162.42) * mm, "end": v(12.88, 162.45) * mm});
            skLineSegment(sketch, "E2982", {"start": v(12.88, 162.45) * mm, "end": v(12.82, 162.65) * mm});
            skLineSegment(sketch, "E2983", {"start": v(12.82, 162.65) * mm, "end": v(12.81, 162.66) * mm});
            skLineSegment(sketch, "E2984", {"start": v(12.81, 162.66) * mm, "end": v(12.8, 162.7) * mm});
            skLineSegment(sketch, "E2985", {"start": v(12.8, 162.7) * mm, "end": v(12.63, 162.9) * mm});
            skLineSegment(sketch, "E2986", {"start": v(12.63, 162.9) * mm, "end": v(12.6, 162.92) * mm});
            skLineSegment(sketch, "E2987", {"start": v(12.6, 162.92) * mm, "end": v(12.53, 162.95) * mm});
            skLineSegment(sketch, "E2988", {"start": v(12.53, 162.95) * mm, "end": v(12.27, 162.92) * mm});
            skLineSegment(sketch, "E2989", {"start": v(12.27, 162.92) * mm, "end": v(12.1, 162.56) * mm});
            skLineSegment(sketch, "E2990", {"start": v(12.1, 162.56) * mm, "end": v(12.09, 162.44) * mm});
            skLineSegment(sketch, "E2991", {"start": v(12.09, 162.44) * mm, "end": v(12.08, 162.4) * mm});
            skLineSegment(sketch, "E2992", {"start": v(12.08, 162.4) * mm, "end": v(12.07, 162.08) * mm});
            skLineSegment(sketch, "E2993", {"start": v(12.07, 162.08) * mm, "end": v(12.07, 161.97) * mm});
            skLineSegment(sketch, "E2994", {"start": v(12.07, 161.97) * mm, "end": v(12.07, 161.8) * mm});
            skLineSegment(sketch, "E2995", {"start": v(12.07, 161.8) * mm, "end": v(12.07, 161.77) * mm});
            skLineSegment(sketch, "E2996", {"start": v(12.07, 161.77) * mm, "end": v(12, 161.71) * mm});
            skLineSegment(sketch, "E2997", {"start": v(12, 161.71) * mm, "end": v(11.87, 161.8) * mm});
            skLineSegment(sketch, "E2998", {"start": v(11.87, 161.8) * mm, "end": v(11.84, 161.84) * mm});
            skLineSegment(sketch, "E2999", {"start": v(11.84, 161.84) * mm, "end": v(11.8, 161.9) * mm});
            skLineSegment(sketch, "E3000", {"start": v(11.8, 161.9) * mm, "end": v(11.52, 162.53) * mm});
            skLineSegment(sketch, "E3001", {"start": v(11.52, 162.53) * mm, "end": v(11.51, 162.61) * mm});
            skLineSegment(sketch, "E3002", {"start": v(11.51, 162.61) * mm, "end": v(11.51, 162.73) * mm});
            skLineSegment(sketch, "E3003", {"start": v(11.51, 162.73) * mm, "end": v(11.51, 162.83) * mm});
            skLineSegment(sketch, "E3004", {"start": v(11.51, 162.83) * mm, "end": v(11.62, 163.22) * mm});
            skLineSegment(sketch, "E3005", {"start": v(11.62, 163.22) * mm, "end": v(11.78, 163.48) * mm});
            skLineSegment(sketch, "E3006", {"start": v(11.78, 163.48) * mm, "end": v(11.82, 163.52) * mm});
            skLineSegment(sketch, "E3007", {"start": v(11.82, 163.52) * mm, "end": v(11.73, 163.57) * mm});
            skLineSegment(sketch, "E3008", {"start": v(11.73, 163.57) * mm, "end": v(11.45, 163.76) * mm});
            skLineSegment(sketch, "E3009", {"start": v(11.45, 163.76) * mm, "end": v(11.16, 164.06) * mm});
            skLineSegment(sketch, "E3010", {"start": v(11.16, 164.06) * mm, "end": v(11.08, 164.16) * mm});
            skLineSegment(sketch, "E3011", {"start": v(11.08, 164.16) * mm, "end": v(10.96, 164.3) * mm});
            skLineSegment(sketch, "E3012", {"start": v(10.96, 164.3) * mm, "end": v(10.28, 164.74) * mm});
            skLineSegment(sketch, "E3013", {"start": v(10.28, 164.74) * mm, "end": v(9.56, 164.9) * mm});
            skLineSegment(sketch, "E3014", {"start": v(9.56, 164.9) * mm, "end": v(9.43, 164.9) * mm});
            skLineSegment(sketch, "E3015", {"start": v(9.43, 164.9) * mm, "end": v(9.27, 164.88) * mm});
            skLineSegment(sketch, "E3016", {"start": v(9.27, 164.88) * mm, "end": v(8.78, 164.99) * mm});
            skLineSegment(sketch, "E3017", {"start": v(8.78, 164.99) * mm, "end": v(8.29, 165.28) * mm});
            skLineSegment(sketch, "E3018", {"start": v(8.29, 165.28) * mm, "end": v(7.9, 165.68) * mm});
            skLineSegment(sketch, "E3019", {"start": v(7.9, 165.68) * mm, "end": v(7.69, 165.98) * mm});
            skLineSegment(sketch, "E3020", {"start": v(7.69, 165.98) * mm, "end": v(7.62, 166.08) * mm});
            skLineSegment(sketch, "E3021", {"start": v(7.62, 166.08) * mm, "end": v(7.58, 166.13) * mm});
            skLineSegment(sketch, "E3022", {"start": v(7.58, 166.13) * mm, "end": v(7.38, 166.27) * mm});
            skLineSegment(sketch, "E3023", {"start": v(7.38, 166.27) * mm, "end": v(6.93, 166.48) * mm});
            skLineSegment(sketch, "E3024", {"start": v(6.93, 166.48) * mm, "end": v(6.36, 166.64) * mm});
            skLineSegment(sketch, "E3025", {"start": v(6.36, 166.64) * mm, "end": v(5.89, 166.7) * mm});
            skLineSegment(sketch, "E3026", {"start": v(5.89, 166.7) * mm, "end": v(5.73, 166.68) * mm});
            skLineSegment(sketch, "E3027", {"start": v(5.73, 166.68) * mm, "end": v(5.57, 166.68) * mm});
            skLineSegment(sketch, "E3028", {"start": v(5.57, 166.68) * mm, "end": v(4.97, 166.65) * mm});
            skLineSegment(sketch, "E3029", {"start": v(4.97, 166.65) * mm, "end": v(4.62, 166.6) * mm});
            skLineSegment(sketch, "E3030", {"start": v(4.62, 166.6) * mm, "end": v(4.59, 166.59) * mm});
            skLineSegment(sketch, "E3031", {"start": v(4.59, 166.59) * mm, "end": v(4.5, 166.6) * mm});
            skLineSegment(sketch, "E3032", {"start": v(4.5, 166.6) * mm, "end": v(4.48, 166.6) * mm});
            skLineSegment(sketch, "E3033", {"start": v(4.48, 166.6) * mm, "end": v(4.47, 166.58) * mm});
            skLineSegment(sketch, "E3034", {"start": v(4.47, 166.58) * mm, "end": v(4.47, 166.46) * mm});
            skLineSegment(sketch, "E3035", {"start": v(4.47, 166.46) * mm, "end": v(4.53, 166.22) * mm});
            skLineSegment(sketch, "E3036", {"start": v(4.53, 166.22) * mm, "end": v(4.67, 165.92) * mm});
            skLineSegment(sketch, "E3037", {"start": v(4.67, 165.92) * mm, "end": v(4.73, 165.82) * mm});
            skLineSegment(sketch, "E3038", {"start": v(4.73, 165.82) * mm, "end": v(4.75, 165.76) * mm});
            skLineSegment(sketch, "E3039", {"start": v(4.75, 165.76) * mm, "end": v(4.9, 165.59) * mm});
            skLineSegment(sketch, "E3040", {"start": v(4.9, 165.59) * mm, "end": v(5.15, 165.36) * mm});
            skLineSegment(sketch, "E3041", {"start": v(5.15, 165.36) * mm, "end": v(5.35, 165.05) * mm});
            skLineSegment(sketch, "E3042", {"start": v(5.35, 165.05) * mm, "end": v(5.42, 164.7) * mm});
            skLineSegment(sketch, "E3043", {"start": v(5.42, 164.7) * mm, "end": v(5.4, 164.58) * mm});
            skLineSegment(sketch, "E3044", {"start": v(5.4, 164.58) * mm, "end": v(5.4, 164.4) * mm});
            skLineSegment(sketch, "E3045", {"start": v(5.4, 164.4) * mm, "end": v(5.26, 163.56) * mm});
            skLineSegment(sketch, "E3046", {"start": v(5.26, 163.56) * mm, "end": v(5.36, 162.8) * mm});
            skLineSegment(sketch, "E3047", {"start": v(5.36, 162.8) * mm, "end": v(5.47, 162.65) * mm});
            skLineSegment(sketch, "E3048", {"start": v(5.47, 162.65) * mm, "end": v(5.48, 162.64) * mm});
            skLineSegment(sketch, "E3049", {"start": v(5.48, 162.64) * mm, "end": v(5.54, 162.55) * mm});
            skLineSegment(sketch, "E3050", {"start": v(5.54, 162.55) * mm, "end": v(5.54, 162.54) * mm});
            skLineSegment(sketch, "E3051", {"start": v(5.54, 162.54) * mm, "end": v(5.59, 162.46) * mm});
            skLineSegment(sketch, "E3052", {"start": v(5.59, 162.46) * mm, "end": v(5.85, 161.8) * mm});
            skLineSegment(sketch, "E3053", {"start": v(5.85, 161.8) * mm, "end": v(5.98, 161) * mm});
            skLineSegment(sketch, "E3054", {"start": v(5.98, 161) * mm, "end": v(5.95, 160.85) * mm});
            skLineSegment(sketch, "E3055", {"start": v(5.95, 160.85) * mm, "end": v(5.88, 160.47) * mm});
            skLineSegment(sketch, "E3056", {"start": v(5.88, 160.47) * mm, "end": v(5.66, 159.34) * mm});
            skLineSegment(sketch, "E3057", {"start": v(5.66, 159.34) * mm, "end": v(5.28, 157.68) * mm});
            skLineSegment(sketch, "E3058", {"start": v(5.28, 157.68) * mm, "end": v(4.82, 156.12) * mm});
            skLineSegment(sketch, "E3059", {"start": v(4.82, 156.12) * mm, "end": v(4.47, 155.2) * mm});
            skLineSegment(sketch, "E3060", {"start": v(4.47, 155.2) * mm, "end": v(4.3, 154.92) * mm});
            skLineSegment(sketch, "E3061", {"start": v(4.3, 154.92) * mm, "end": v(4.27, 154.86) * mm});
            skLineSegment(sketch, "E3062", {"start": v(4.27, 154.86) * mm, "end": v(4.12, 154.72) * mm});
            skLineSegment(sketch, "E3063", {"start": v(4.12, 154.72) * mm, "end": v(4.08, 154.78) * mm});
            skLineSegment(sketch, "E3064", {"start": v(4.08, 154.78) * mm, "end": v(4, 155.44) * mm});
            skLineSegment(sketch, "E3065", {"start": v(4, 155.44) * mm, "end": v(3.72, 157.2) * mm});
            skLineSegment(sketch, "E3066", {"start": v(3.72, 157.2) * mm, "end": v(3.08, 159.72) * mm});
            skLineSegment(sketch, "E3067", {"start": v(3.08, 159.72) * mm, "end": v(2.3, 161.95) * mm});
            skLineSegment(sketch, "E3068", {"start": v(2.3, 161.95) * mm, "end": v(1.97, 162.66) * mm});
            skLineSegment(sketch, "E3069", {"start": v(1.97, 162.66) * mm, "end": v(1.72, 163.2) * mm});
            skLineSegment(sketch, "E3070", {"start": v(1.72, 163.2) * mm, "end": v(0.28, 165.84) * mm});
            skLineSegment(sketch, "E3071", {"start": v(0.28, 165.84) * mm, "end": v(-1.4, 168.26) * mm});
            skLineSegment(sketch, "E3072", {"start": v(-1.4, 168.26) * mm, "end": v(-1.78, 168.7) * mm});
            skLineSegment(sketch, "E3073", {"start": v(-1.78, 168.7) * mm, "end": v(-2.02, 168.98) * mm});
            skLineSegment(sketch, "E3074", {"start": v(-2.02, 168.98) * mm, "end": v(-2.76, 169.85) * mm});
            skLineSegment(sketch, "E3075", {"start": v(-2.76, 169.85) * mm, "end": v(-3.5, 170.7) * mm});
            skLineSegment(sketch, "E3076", {"start": v(-3.5, 170.7) * mm, "end": v(-3.97, 171.18) * mm});
            skLineSegment(sketch, "E3077", {"start": v(-3.97, 171.18) * mm, "end": v(-4.17, 171.29) * mm});
            skLineSegment(sketch, "E3078", {"start": v(-4.17, 171.29) * mm, "end": v(-4.18, 171.28) * mm});
            skLineSegment(sketch, "E3079", {"start": v(-4.18, 171.28) * mm, "end": v(-4.21, 171.25) * mm});
            skLineSegment(sketch, "E3080", {"start": v(-4.21, 171.25) * mm, "end": v(-4.2, 171) * mm});
            skLineSegment(sketch, "E3081", {"start": v(-4.2, 171) * mm, "end": v(-4.23, 170.45) * mm});
            skLineSegment(sketch, "E3082", {"start": v(-4.23, 170.45) * mm, "end": v(-4.27, 170.27) * mm});
            skLineSegment(sketch, "E3083", {"start": v(-4.27, 170.27) * mm, "end": v(-4.31, 170.1) * mm});
            skLineSegment(sketch, "E3084", {"start": v(-4.31, 170.1) * mm, "end": v(-4.72, 169.54) * mm});
            skLineSegment(sketch, "E3085", {"start": v(-4.72, 169.54) * mm, "end": v(-5.1, 169.27) * mm});
            skLineSegment(sketch, "E3086", {"start": v(-5.1, 169.27) * mm, "end": v(-5.13, 169.24) * mm});
            skLineSegment(sketch, "E3087", {"start": v(-5.13, 169.24) * mm, "end": v(-4.9, 169.12) * mm});
            skLineSegment(sketch, "E3088", {"start": v(-4.9, 169.12) * mm, "end": v(-4.3, 168.98) * mm});
            skLineSegment(sketch, "E3089", {"start": v(-4.3, 168.98) * mm, "end": v(-4.16, 168.93) * mm});
            skLineSegment(sketch, "E3090", {"start": v(-4.16, 168.93) * mm, "end": v(-4.07, 168.9) * mm});
            skLineSegment(sketch, "E3091", {"start": v(-4.07, 168.9) * mm, "end": v(-3.8, 168.75) * mm});
            skLineSegment(sketch, "E3092", {"start": v(-3.8, 168.75) * mm, "end": v(-3.57, 168.6) * mm});
            skLineSegment(sketch, "E3093", {"start": v(-3.57, 168.6) * mm, "end": v(-3.55, 168.49) * mm});
            skLineSegment(sketch, "E3094", {"start": v(-3.55, 168.49) * mm, "end": v(-3.7, 168.48) * mm});
            skLineSegment(sketch, "E3095", {"start": v(-3.7, 168.48) * mm, "end": v(-3.76, 168.49) * mm});
            skLineSegment(sketch, "E3096", {"start": v(-3.76, 168.49) * mm, "end": v(-3.9, 168.5) * mm});
            skLineSegment(sketch, "E3097", {"start": v(-3.9, 168.5) * mm, "end": v(-4.36, 168.55) * mm});
            skLineSegment(sketch, "E3098", {"start": v(-4.36, 168.55) * mm, "end": v(-5, 168.58) * mm});
            skLineSegment(sketch, "E3099", {"start": v(-5, 168.58) * mm, "end": v(-5.5, 168.57) * mm});
            skLineSegment(sketch, "E3100", {"start": v(-5.5, 168.57) * mm, "end": v(-5.66, 168.5) * mm});
            skLineSegment(sketch, "E3101", {"start": v(-5.66, 168.5) * mm, "end": v(-5.64, 168.48) * mm});
            skLineSegment(sketch, "E3102", {"start": v(-5.64, 168.48) * mm, "end": v(-5.45, 168.4) * mm});
            skLineSegment(sketch, "E3103", {"start": v(-5.45, 168.4) * mm, "end": v(-5.02, 168.22) * mm});
            skLineSegment(sketch, "E3104", {"start": v(-5.02, 168.22) * mm, "end": v(-4.48, 167.98) * mm});
            skLineSegment(sketch, "E3105", {"start": v(-4.48, 167.98) * mm, "end": v(-4.06, 167.74) * mm});
            skLineSegment(sketch, "E3106", {"start": v(-4.06, 167.74) * mm, "end": v(-3.92, 167.65) * mm});
            skLineSegment(sketch, "E3107", {"start": v(-3.92, 167.65) * mm, "end": v(-3.84, 167.6) * mm});
            skLineSegment(sketch, "E3108", {"start": v(-3.84, 167.6) * mm, "end": v(-3.59, 167.4) * mm});
            skLineSegment(sketch, "E3109", {"start": v(-3.59, 167.4) * mm, "end": v(-3.34, 167.13) * mm});
            skLineSegment(sketch, "E3110", {"start": v(-3.34, 167.13) * mm, "end": v(-3.29, 166.96) * mm});
            skLineSegment(sketch, "E3111", {"start": v(-3.29, 166.96) * mm, "end": v(-3.47, 166.93) * mm});
            skLineSegment(sketch, "E3112", {"start": v(-3.47, 166.93) * mm, "end": v(-3.52, 166.94) * mm});
            skLineSegment(sketch, "E3113", {"start": v(-3.52, 166.94) * mm, "end": v(-3.78, 167) * mm});
            skLineSegment(sketch, "E3114", {"start": v(-3.78, 167) * mm, "end": v(-6.44, 167.5) * mm});
            skLineSegment(sketch, "E3115", {"start": v(-6.44, 167.5) * mm, "end": v(-6.72, 167.54) * mm});
            skLineSegment(sketch, "E3116", {"start": v(-6.72, 167.54) * mm, "end": v(-6.95, 167.56) * mm});
            skLineSegment(sketch, "E3117", {"start": v(-6.95, 167.56) * mm, "end": v(-7.66, 167.52) * mm});
            skLineSegment(sketch, "E3118", {"start": v(-7.66, 167.52) * mm, "end": v(-8.44, 167.35) * mm});
            skLineSegment(sketch, "E3119", {"start": v(-8.44, 167.35) * mm, "end": v(-8.93, 167.13) * mm});
            skLineSegment(sketch, "E3120", {"start": v(-8.93, 167.13) * mm, "end": v(-8.98, 166.98) * mm});
            skLineSegment(sketch, "E3121", {"start": v(-8.98, 166.98) * mm, "end": v(-8.98, 166.98) * mm});
            skLineSegment(sketch, "E3122", {"start": v(-8.98, 166.98) * mm, "end": v(-8.94, 166.96) * mm});
            skLineSegment(sketch, "E3123", {"start": v(-8.94, 166.96) * mm, "end": v(-8.76, 166.9) * mm});
            skLineSegment(sketch, "E3124", {"start": v(-8.76, 166.9) * mm, "end": v(-8.36, 166.76) * mm});
            skLineSegment(sketch, "E3125", {"start": v(-8.36, 166.76) * mm, "end": v(-7.84, 166.45) * mm});
            skLineSegment(sketch, "E3126", {"start": v(-7.84, 166.45) * mm, "end": v(-7.36, 166.04) * mm});
            skLineSegment(sketch, "E3127", {"start": v(-7.36, 166.04) * mm, "end": v(-7.22, 165.9) * mm});
            skLineSegment(sketch, "E3128", {"start": v(-7.22, 165.9) * mm, "end": v(-7.25, 165.87) * mm});
            skLineSegment(sketch, "E3129", {"start": v(-7.25, 165.87) * mm, "end": v(-7.53, 165.9) * mm});
            skLineSegment(sketch, "E3130", {"start": v(-7.53, 165.9) * mm, "end": v(-8.07, 166.12) * mm});
            skLineSegment(sketch, "E3131", {"start": v(-8.07, 166.12) * mm, "end": v(-8.23, 166.2) * mm});
            skLineSegment(sketch, "E3132", {"start": v(-8.23, 166.2) * mm, "end": v(-8.37, 166.28) * mm});
            skLineSegment(sketch, "E3133", {"start": v(-8.37, 166.28) * mm, "end": v(-8.8, 166.46) * mm});
            skLineSegment(sketch, "E3134", {"start": v(-8.8, 166.46) * mm, "end": v(-9.14, 166.52) * mm});
            skLineSegment(sketch, "E3135", {"start": v(-9.14, 166.52) * mm, "end": v(-9.27, 166.47) * mm});
            skLineSegment(sketch, "E3136", {"start": v(-9.27, 166.47) * mm, "end": v(-9.25, 166.39) * mm});
            skLineSegment(sketch, "E3137", {"start": v(-9.25, 166.39) * mm, "end": v(-9.23, 166.37) * mm});
            skLineSegment(sketch, "E3138", {"start": v(-9.23, 166.37) * mm, "end": v(-9.18, 166.35) * mm});
            skLineSegment(sketch, "E3139", {"start": v(-9.18, 166.35) * mm, "end": v(-8.77, 166.13) * mm});
            skLineSegment(sketch, "E3140", {"start": v(-8.77, 166.13) * mm, "end": v(-8.32, 165.85) * mm});
            skLineSegment(sketch, "E3141", {"start": v(-8.32, 165.85) * mm, "end": v(-8.25, 165.8) * mm});
            skLineSegment(sketch, "E3142", {"start": v(-8.25, 165.8) * mm, "end": v(-8.11, 165.67) * mm});
            skLineSegment(sketch, "E3143", {"start": v(-8.11, 165.67) * mm, "end": v(-7.72, 165.27) * mm});
            skLineSegment(sketch, "E3144", {"start": v(-7.72, 165.27) * mm, "end": v(-7.36, 164.8) * mm});
            skLineSegment(sketch, "E3145", {"start": v(-7.36, 164.8) * mm, "end": v(-7.16, 164.47) * mm});
            skLineSegment(sketch, "E3146", {"start": v(-7.16, 164.47) * mm, "end": v(-7.1, 164.35) * mm});
            skLineSegment(sketch, "E3147", {"start": v(-7.1, 164.35) * mm, "end": v(-7.07, 164.3) * mm});
            skLineSegment(sketch, "E3148", {"start": v(-7.07, 164.3) * mm, "end": v(-6.84, 163.84) * mm});
            skLineSegment(sketch, "E3149", {"start": v(-6.84, 163.84) * mm, "end": v(-6.6, 163.26) * mm});
            skLineSegment(sketch, "E3150", {"start": v(-6.6, 163.26) * mm, "end": v(-6.57, 163.16) * mm});
            skLineSegment(sketch, "E3151", {"start": v(-6.57, 163.16) * mm, "end": v(-6.53, 163.04) * mm});
            skLineSegment(sketch, "E3152", {"start": v(-6.53, 163.04) * mm, "end": v(-6.44, 162.7) * mm});
            skLineSegment(sketch, "E3153", {"start": v(-6.44, 162.7) * mm, "end": v(-6.32, 162.2) * mm});
            skLineSegment(sketch, "E3154", {"start": v(-6.32, 162.2) * mm, "end": v(-6.25, 161.85) * mm});
            skLineSegment(sketch, "E3155", {"start": v(-6.25, 161.85) * mm, "end": v(-6.27, 161.76) * mm});
            skLineSegment(sketch, "E3156", {"start": v(-6.27, 161.76) * mm, "end": v(-6.32, 161.8) * mm});
            skLineSegment(sketch, "E3157", {"start": v(-6.32, 161.8) * mm, "end": v(-6.43, 161.96) * mm});
            skLineSegment(sketch, "E3158", {"start": v(-6.43, 161.96) * mm, "end": v(-6.67, 162.33) * mm});
            skLineSegment(sketch, "E3159", {"start": v(-6.67, 162.33) * mm, "end": v(-6.98, 162.82) * mm});
            skLineSegment(sketch, "E3160", {"start": v(-6.98, 162.82) * mm, "end": v(-7.33, 163.36) * mm});
            skLineSegment(sketch, "E3161", {"start": v(-7.33, 163.36) * mm, "end": v(-7.68, 163.89) * mm});
            skLineSegment(sketch, "E3162", {"start": v(-7.68, 163.89) * mm, "end": v(-8.03, 164.34) * mm});
            skLineSegment(sketch, "E3163", {"start": v(-8.03, 164.34) * mm, "end": v(-8.33, 164.65) * mm});
            skLineSegment(sketch, "E3164", {"start": v(-8.33, 164.65) * mm, "end": v(-8.51, 164.76) * mm});
            skLineSegment(sketch, "E3165", {"start": v(-8.51, 164.76) * mm, "end": v(-8.57, 164.75) * mm});
            skLineSegment(sketch, "E3166", {"start": v(-8.57, 164.75) * mm, "end": v(-8.6, 164.75) * mm});
            skLineSegment(sketch, "E3167", {"start": v(-8.6, 164.75) * mm, "end": v(-8.68, 164.57) * mm});
            skLineSegment(sketch, "E3168", {"start": v(-8.68, 164.57) * mm, "end": v(-8.67, 164.18) * mm});
            skLineSegment(sketch, "E3169", {"start": v(-8.67, 164.18) * mm, "end": v(-8.56, 163.73) * mm});
            skLineSegment(sketch, "E3170", {"start": v(-8.56, 163.73) * mm, "end": v(-8.46, 163.44) * mm});
            skLineSegment(sketch, "E3171", {"start": v(-8.46, 163.44) * mm, "end": v(-8.4, 163.35) * mm});
            skLineSegment(sketch, "E3172", {"start": v(-8.4, 163.35) * mm, "end": v(-8.34, 163.23) * mm});
            skLineSegment(sketch, "E3173", {"start": v(-8.34, 163.23) * mm, "end": v(-8.06, 162.9) * mm});
            skLineSegment(sketch, "E3174", {"start": v(-8.06, 162.9) * mm, "end": v(-7.52, 162.33) * mm});
            skLineSegment(sketch, "E3175", {"start": v(-7.52, 162.33) * mm, "end": v(-6.96, 161.76) * mm});
            skLineSegment(sketch, "E3176", {"start": v(-6.96, 161.76) * mm, "end": v(-6.64, 161.44) * mm});
            skLineSegment(sketch, "E3177", {"start": v(-6.64, 161.44) * mm, "end": v(-6.54, 161.32) * mm});
            skLineSegment(sketch, "E3178", {"start": v(-6.54, 161.32) * mm, "end": v(-6.24, 160.96) * mm});
            skLineSegment(sketch, "E3179", {"start": v(-6.24, 160.96) * mm, "end": v(-5.07, 159.1) * mm});
            skLineSegment(sketch, "E3180", {"start": v(-5.07, 159.1) * mm, "end": v(-4.09, 157.2) * mm});
            skLineSegment(sketch, "E3181", {"start": v(-4.09, 157.2) * mm, "end": v(-3.87, 156.84) * mm});
            skLineSegment(sketch, "E3182", {"start": v(-3.87, 156.84) * mm, "end": v(-3.84, 156.78) * mm});
            skLineSegment(sketch, "E3183", {"start": v(-3.84, 156.78) * mm, "end": v(-3.62, 156.2) * mm});
            skLineSegment(sketch, "E3184", {"start": v(-3.62, 156.2) * mm, "end": v(-3.6, 156.15) * mm});
            skLineSegment(sketch, "E3185", {"start": v(-3.6, 156.15) * mm, "end": v(-3.6, 156.12) * mm});
            skLineSegment(sketch, "E3186", {"start": v(-3.6, 156.12) * mm, "end": v(-3.48, 155.8) * mm});
            skLineSegment(sketch, "E3187", {"start": v(-3.48, 155.8) * mm, "end": v(-3.46, 155.78) * mm});
            skLineSegment(sketch, "E3188", {"start": v(-3.46, 155.78) * mm, "end": v(-3.45, 155.75) * mm});
            skLineSegment(sketch, "E3189", {"start": v(-3.45, 155.75) * mm, "end": v(-3.24, 155.5) * mm});
            skLineSegment(sketch, "E3190", {"start": v(-3.24, 155.5) * mm, "end": v(-3.2, 155.48) * mm});
            skLineSegment(sketch, "E3191", {"start": v(-3.2, 155.48) * mm, "end": v(-3.2, 155.48) * mm});
            skLineSegment(sketch, "E3192", {"start": v(-3.2, 155.48) * mm, "end": v(-3.13, 155.42) * mm});
            skLineSegment(sketch, "E3193", {"start": v(-3.13, 155.42) * mm, "end": v(-3.12, 155.42) * mm});
            skLineSegment(sketch, "E3194", {"start": v(-3.12, 155.42) * mm, "end": v(-3.1, 155.41) * mm});
            skLineSegment(sketch, "E3195", {"start": v(-3.1, 155.41) * mm, "end": v(-3, 155.37) * mm});
            skLineSegment(sketch, "E3196", {"start": v(-3, 155.37) * mm, "end": v(-2.99, 155.37) * mm});
            skLineSegment(sketch, "E3197", {"start": v(-2.99, 155.37) * mm, "end": v(-2.95, 155.35) * mm});
            skLineSegment(sketch, "E3198", {"start": v(-2.95, 155.35) * mm, "end": v(-2.61, 155.17) * mm});
            skLineSegment(sketch, "E3199", {"start": v(-2.61, 155.17) * mm, "end": v(-2.58, 155.13) * mm});
            skLineSegment(sketch, "E3200", {"start": v(-2.58, 155.13) * mm, "end": v(-2.56, 155.12) * mm});
            skLineSegment(sketch, "E3201", {"start": v(-2.56, 155.12) * mm, "end": v(-2.45, 154.99) * mm});
            skLineSegment(sketch, "E3202", {"start": v(-2.45, 154.99) * mm, "end": v(-2.36, 154.88) * mm});
            skLineSegment(sketch, "E3203", {"start": v(-2.36, 154.88) * mm, "end": v(-2.36, 154.87) * mm});
            skLineSegment(sketch, "E3204", {"start": v(-2.36, 154.87) * mm, "end": v(-2.3, 154.82) * mm});
            skLineSegment(sketch, "E3205", {"start": v(-2.3, 154.82) * mm, "end": v(-2.3, 154.8) * mm});
            skLineSegment(sketch, "E3206", {"start": v(-2.3, 154.8) * mm, "end": v(-2.2, 154.72) * mm});
            skLineSegment(sketch, "E3207", {"start": v(-2.2, 154.72) * mm, "end": v(-1.77, 154.44) * mm});
            skLineSegment(sketch, "E3208", {"start": v(-1.77, 154.44) * mm, "end": v(-1.25, 154.28) * mm});
            skLineSegment(sketch, "E3209", {"start": v(-1.25, 154.28) * mm, "end": v(-1.1, 154.24) * mm});
            skLineSegment(sketch, "E3210", {"start": v(-1.1, 154.24) * mm, "end": v(-1.06, 154.23) * mm});
            skLineSegment(sketch, "E3211", {"start": v(-1.06, 154.23) * mm, "end": v(-0.5, 154.05) * mm});
            skLineSegment(sketch, "E3212", {"start": v(-0.5, 154.05) * mm, "end": v(-0.46, 154.03) * mm});
            skLineSegment(sketch, "E3213", {"start": v(-0.46, 154.03) * mm, "end": v(-0.35, 153.99) * mm});
            skLineSegment(sketch, "E3214", {"start": v(-0.35, 153.99) * mm, "end": v(-0.03, 153.7) * mm});
            skLineSegment(sketch, "E3215", {"start": v(-0.03, 153.7) * mm, "end": v(-0.04, 153.46) * mm});
            skLineSegment(sketch, "E3216", {"start": v(-0.04, 153.46) * mm, "end": v(-0.06, 153.46) * mm});
            skLineSegment(sketch, "E3217", {"start": v(-0.06, 153.46) * mm, "end": v(-0.07, 153.45) * mm});
            skLineSegment(sketch, "E3218", {"start": v(-0.07, 153.45) * mm, "end": v(-0.24, 153.45) * mm});
            skLineSegment(sketch, "E3219", {"start": v(-0.24, 153.45) * mm, "end": v(-0.27, 153.46) * mm});
            skLineSegment(sketch, "E3220", {"start": v(-0.27, 153.46) * mm, "end": v(-0.39, 153.48) * mm});
            skLineSegment(sketch, "E3221", {"start": v(-0.39, 153.48) * mm, "end": v(-1.1, 153.57) * mm});
            skLineSegment(sketch, "E3222", {"start": v(-1.1, 153.57) * mm, "end": v(-2.08, 153.58) * mm});
            skLineSegment(sketch, "E3223", {"start": v(-2.08, 153.58) * mm, "end": v(-2.32, 153.56) * mm});
            skLineSegment(sketch, "E3224", {"start": v(-2.32, 153.56) * mm, "end": v(-2.4, 153.56) * mm});
            skLineSegment(sketch, "E3225", {"start": v(-2.4, 153.56) * mm, "end": v(-3.4, 153.43) * mm});
            skLineSegment(sketch, "E3226", {"start": v(-3.4, 153.43) * mm, "end": v(-3.5, 153.42) * mm});
            skLineSegment(sketch, "E3227", {"start": v(-3.5, 153.42) * mm, "end": v(-3.57, 153.4) * mm});
            skLineSegment(sketch, "E3228", {"start": v(-3.57, 153.4) * mm, "end": v(-4.11, 153.29) * mm});
            skLineSegment(sketch, "E3229", {"start": v(-4.11, 153.29) * mm, "end": v(-4.16, 153.28) * mm});
            skLineSegment(sketch, "E3230", {"start": v(-4.16, 153.28) * mm, "end": v(-4.23, 153.27) * mm});
            skLineSegment(sketch, "E3231", {"start": v(-4.23, 153.27) * mm, "end": v(-4.77, 153.23) * mm});
            skLineSegment(sketch, "E3232", {"start": v(-4.77, 153.23) * mm, "end": v(-4.82, 153.23) * mm});
            skLineSegment(sketch, "E3233", {"start": v(-4.82, 153.23) * mm, "end": v(-4.83, 153.24) * mm});
            skLineSegment(sketch, "E3234", {"start": v(-4.83, 153.24) * mm, "end": v(-5, 153.25) * mm});
            skLineSegment(sketch, "E3235", {"start": v(-5, 153.25) * mm, "end": v(-5.68, 153.47) * mm});
            skLineSegment(sketch, "E3236", {"start": v(-5.68, 153.47) * mm, "end": v(-6.28, 153.86) * mm});
            skLineSegment(sketch, "E3237", {"start": v(-6.28, 153.86) * mm, "end": v(-6.4, 153.97) * mm});
            skLineSegment(sketch, "E3238", {"start": v(-6.4, 153.97) * mm, "end": v(-6.42, 153.99) * mm});
            skLineSegment(sketch, "E3239", {"start": v(-6.42, 153.99) * mm, "end": v(-6.6, 154.15) * mm});
            skLineSegment(sketch, "E3240", {"start": v(-6.6, 154.15) * mm, "end": v(-6.62, 154.17) * mm});
            skLineSegment(sketch, "E3241", {"start": v(-6.62, 154.17) * mm, "end": v(-6.68, 154.22) * mm});
            skLineSegment(sketch, "E3242", {"start": v(-6.68, 154.22) * mm, "end": v(-6.83, 154.42) * mm});
            skLineSegment(sketch, "E3243", {"start": v(-6.83, 154.42) * mm, "end": v(-6.6, 154.41) * mm});
            skLineSegment(sketch, "E3244", {"start": v(-6.6, 154.41) * mm, "end": v(-6.09, 154.25) * mm});
            skLineSegment(sketch, "E3245", {"start": v(-6.09, 154.25) * mm, "end": v(-5.6, 154.1) * mm});
            skLineSegment(sketch, "E3246", {"start": v(-5.6, 154.1) * mm, "end": v(-5.43, 154.05) * mm});
            skLineSegment(sketch, "E3247", {"start": v(-5.43, 154.05) * mm, "end": v(-5.38, 154.04) * mm});
            skLineSegment(sketch, "E3248", {"start": v(-5.38, 154.04) * mm, "end": v(-4.87, 153.96) * mm});
            skLineSegment(sketch, "E3249", {"start": v(-4.87, 153.96) * mm, "end": v(-4.7, 153.96) * mm});
            skLineSegment(sketch, "E3250", {"start": v(-4.7, 153.96) * mm, "end": v(-4.06, 153.96) * mm});
            skLineSegment(sketch, "E3251", {"start": v(-4.06, 153.96) * mm, "end": v(-4.02, 153.97) * mm});
            skLineSegment(sketch, "E3252", {"start": v(-4.02, 153.97) * mm, "end": v(-3.78, 153.97) * mm});
            skLineSegment(sketch, "E3253", {"start": v(-3.78, 153.97) * mm, "end": v(-3.14, 154.05) * mm});
            skLineSegment(sketch, "E3254", {"start": v(-3.14, 154.05) * mm, "end": v(-3.06, 154.05) * mm});
            skLineSegment(sketch, "E3255", {"start": v(-3.06, 154.05) * mm, "end": v(-2.85, 154.05) * mm});
            skLineSegment(sketch, "E3256", {"start": v(-2.85, 154.05) * mm, "end": v(-2.8, 154.06) * mm});
            skLineSegment(sketch, "E3257", {"start": v(-2.8, 154.06) * mm, "end": v(-2.55, 154.07) * mm});
            skLineSegment(sketch, "E3258", {"start": v(-2.55, 154.07) * mm, "end": v(-2.47, 154.07) * mm});
            skLineSegment(sketch, "E3259", {"start": v(-2.47, 154.07) * mm, "end": v(-2.42, 154.07) * mm});
            skLineSegment(sketch, "E3260", {"start": v(-2.42, 154.07) * mm, "end": v(-2.25, 154.1) * mm});
            skLineSegment(sketch, "E3261", {"start": v(-2.25, 154.1) * mm, "end": v(-2.25, 154.17) * mm});
            skLineSegment(sketch, "E3262", {"start": v(-2.25, 154.17) * mm, "end": v(-2.26, 154.19) * mm});
            skLineSegment(sketch, "E3263", {"start": v(-2.26, 154.19) * mm, "end": v(-2.27, 154.2) * mm});
            skLineSegment(sketch, "E3264", {"start": v(-2.27, 154.2) * mm, "end": v(-2.55, 154.37) * mm});
            skLineSegment(sketch, "E3265", {"start": v(-2.55, 154.37) * mm, "end": v(-2.58, 154.38) * mm});
            skLineSegment(sketch, "E3266", {"start": v(-2.58, 154.38) * mm, "end": v(-2.6, 154.4) * mm});
            skLineSegment(sketch, "E3267", {"start": v(-2.6, 154.4) * mm, "end": v(-2.84, 154.52) * mm});
            skLineSegment(sketch, "E3268", {"start": v(-2.84, 154.52) * mm, "end": v(-2.86, 154.53) * mm});
            skLineSegment(sketch, "E3269", {"start": v(-2.86, 154.53) * mm, "end": v(-2.9, 154.54) * mm});
            skLineSegment(sketch, "E3270", {"start": v(-2.9, 154.54) * mm, "end": v(-3.2, 154.66) * mm});
            skLineSegment(sketch, "E3271", {"start": v(-3.2, 154.66) * mm, "end": v(-3.24, 154.67) * mm});
            skLineSegment(sketch, "E3272", {"start": v(-3.24, 154.67) * mm, "end": v(-3.3, 154.7) * mm});
            skLineSegment(sketch, "E3273", {"start": v(-3.3, 154.7) * mm, "end": v(-3.95, 154.86) * mm});
            skLineSegment(sketch, "E3274", {"start": v(-3.95, 154.86) * mm, "end": v(-4.03, 154.88) * mm});
            skLineSegment(sketch, "E3275", {"start": v(-4.03, 154.88) * mm, "end": v(-4.09, 154.88) * mm});
            skLineSegment(sketch, "E3276", {"start": v(-4.09, 154.88) * mm, "end": v(-4.23, 154.92) * mm});
            skLineSegment(sketch, "E3277", {"start": v(-4.23, 154.92) * mm, "end": v(-4.27, 154.92) * mm});
            skLineSegment(sketch, "E3278", {"start": v(-4.27, 154.92) * mm, "end": v(-4.46, 154.96) * mm});
            skLineSegment(sketch, "E3279", {"start": v(-4.46, 154.96) * mm, "end": v(-5.3, 155.23) * mm});
            skLineSegment(sketch, "E3280", {"start": v(-5.3, 155.23) * mm, "end": v(-6.03, 155.77) * mm});
            skLineSegment(sketch, "E3281", {"start": v(-6.03, 155.77) * mm, "end": v(-6.16, 155.95) * mm});
            skLineSegment(sketch, "E3282", {"start": v(-6.16, 155.95) * mm, "end": v(-6.18, 155.97) * mm});
            skLineSegment(sketch, "E3283", {"start": v(-6.18, 155.97) * mm, "end": v(-6.19, 156.08) * mm});
            skLineSegment(sketch, "E3284", {"start": v(-6.19, 156.08) * mm, "end": v(-5.95, 156.06) * mm});
            skLineSegment(sketch, "E3285", {"start": v(-5.95, 156.06) * mm, "end": v(-5.56, 155.96) * mm});
            skLineSegment(sketch, "E3286", {"start": v(-5.56, 155.96) * mm, "end": v(-5.24, 155.88) * mm});
            skLineSegment(sketch, "E3287", {"start": v(-5.24, 155.88) * mm, "end": v(-5.13, 155.87) * mm});
            skLineSegment(sketch, "E3288", {"start": v(-5.13, 155.87) * mm, "end": v(-5.12, 155.87) * mm});
            skLineSegment(sketch, "E3289", {"start": v(-5.12, 155.87) * mm, "end": v(-5.04, 155.86) * mm});
            skLineSegment(sketch, "E3290", {"start": v(-5.04, 155.86) * mm, "end": v(-5, 155.86) * mm});
            skLineSegment(sketch, "E3291", {"start": v(-5, 155.86) * mm, "end": v(-4.92, 155.86) * mm});
            skLineSegment(sketch, "E3292", {"start": v(-4.92, 155.86) * mm, "end": v(-4.66, 155.92) * mm});
            skLineSegment(sketch, "E3293", {"start": v(-4.66, 155.92) * mm, "end": v(-4.66, 156.13) * mm});
            skLineSegment(sketch, "E3294", {"start": v(-4.66, 156.13) * mm, "end": v(-4.7, 156.17) * mm});
            skLineSegment(sketch, "E3295", {"start": v(-4.7, 156.17) * mm, "end": v(-4.88, 156.45) * mm});
            skLineSegment(sketch, "E3296", {"start": v(-4.88, 156.45) * mm, "end": v(-5.56, 157.22) * mm});
            skLineSegment(sketch, "E3297", {"start": v(-5.56, 157.22) * mm, "end": v(-6.58, 158.16) * mm});
            skLineSegment(sketch, "E3298", {"start": v(-6.58, 158.16) * mm, "end": v(-7.81, 159.25) * mm});
            skLineSegment(sketch, "E3299", {"start": v(-7.81, 159.25) * mm, "end": v(-8.96, 160.36) * mm});
            skLineSegment(sketch, "E3300", {"start": v(-8.96, 160.36) * mm, "end": v(-9.32, 160.75) * mm});
            skLineSegment(sketch, "E3301", {"start": v(-9.32, 160.75) * mm, "end": v(-9.46, 160.9) * mm});
            skLineSegment(sketch, "E3302", {"start": v(-9.46, 160.9) * mm, "end": v(-10.23, 161.76) * mm});
            skLineSegment(sketch, "E3303", {"start": v(-10.23, 161.76) * mm, "end": v(-10.84, 162.64) * mm});
            skLineSegment(sketch, "E3304", {"start": v(-10.84, 162.64) * mm, "end": v(-10.9, 162.8) * mm});
            skLineSegment(sketch, "E3305", {"start": v(-10.9, 162.8) * mm, "end": v(-10.92, 162.87) * mm});
            skLineSegment(sketch, "E3306", {"start": v(-10.92, 162.87) * mm, "end": v(-11.09, 163.52) * mm});
            skLineSegment(sketch, "E3307", {"start": v(-11.09, 163.52) * mm, "end": v(-11.1, 163.59) * mm});
            skLineSegment(sketch, "E3308", {"start": v(-11.1, 163.59) * mm, "end": v(-11.12, 163.7) * mm});
            skLineSegment(sketch, "E3309", {"start": v(-11.12, 163.7) * mm, "end": v(-11.17, 164.27) * mm});
            skLineSegment(sketch, "E3310", {"start": v(-11.17, 164.27) * mm, "end": v(-11.15, 164.77) * mm});
            skLineSegment(sketch, "E3311", {"start": v(-11.15, 164.77) * mm, "end": v(-11.14, 164.85) * mm});
            skLineSegment(sketch, "E3312", {"start": v(-11.14, 164.85) * mm, "end": v(-11.1, 165.04) * mm});
            skLineSegment(sketch, "E3313", {"start": v(-11.1, 165.04) * mm, "end": v(-10.92, 165.6) * mm});
            skLineSegment(sketch, "E3314", {"start": v(-10.92, 165.6) * mm, "end": v(-10.67, 166.15) * mm});
            skLineSegment(sketch, "E3315", {"start": v(-10.67, 166.15) * mm, "end": v(-10.5, 166.48) * mm});
            skLineSegment(sketch, "E3316", {"start": v(-10.5, 166.48) * mm, "end": v(-10.53, 166.59) * mm});
            skLineSegment(sketch, "E3317", {"start": v(-10.53, 166.59) * mm, "end": v(-10.54, 166.59) * mm});
            skLineSegment(sketch, "E3318", {"start": v(-10.54, 166.59) * mm, "end": v(-10.72, 166.56) * mm});
            skLineSegment(sketch, "E3319", {"start": v(-10.72, 166.56) * mm, "end": v(-10.75, 166.55) * mm});
            skLineSegment(sketch, "E3320", {"start": v(-10.75, 166.55) * mm, "end": v(-10.79, 166.53) * mm});
            skLineSegment(sketch, "E3321", {"start": v(-10.79, 166.53) * mm, "end": v(-11.05, 166.33) * mm});
            skLineSegment(sketch, "E3322", {"start": v(-11.05, 166.33) * mm, "end": v(-11.38, 166.01) * mm});
            skLineSegment(sketch, "E3323", {"start": v(-11.38, 166.01) * mm, "end": v(-11.45, 165.93) * mm});
            skLineSegment(sketch, "E3324", {"start": v(-11.45, 165.93) * mm, "end": v(-11.47, 165.9) * mm});
            skLineSegment(sketch, "E3325", {"start": v(-11.47, 165.9) * mm, "end": v(-11.66, 165.66) * mm});
            skLineSegment(sketch, "E3326", {"start": v(-11.66, 165.66) * mm, "end": v(-11.69, 165.62) * mm});
            skLineSegment(sketch, "E3327", {"start": v(-11.69, 165.62) * mm, "end": v(-11.72, 165.58) * mm});
            skLineSegment(sketch, "E3328", {"start": v(-11.72, 165.58) * mm, "end": v(-11.95, 165) * mm});
            skLineSegment(sketch, "E3329", {"start": v(-11.95, 165) * mm, "end": v(-11.96, 164.9) * mm});
            skLineSegment(sketch, "E3330", {"start": v(-11.96, 164.9) * mm, "end": v(-11.98, 164.8) * mm});
            skLineSegment(sketch, "E3331", {"start": v(-11.98, 164.8) * mm, "end": v(-12.02, 163.73) * mm});
            skLineSegment(sketch, "E3332", {"start": v(-12.02, 163.73) * mm, "end": v(-12, 163.63) * mm});
            skLineSegment(sketch, "E3333", {"start": v(-12, 163.63) * mm, "end": v(-12, 163.35) * mm});
            skLineSegment(sketch, "E3334", {"start": v(-12, 163.35) * mm, "end": v(-11.92, 162.63) * mm});
            skLineSegment(sketch, "E3335", {"start": v(-11.92, 162.63) * mm, "end": v(-11.9, 162.53) * mm});
            skLineSegment(sketch, "E3336", {"start": v(-11.9, 162.53) * mm, "end": v(-11.83, 162.17) * mm});
            skLineSegment(sketch, "E3337", {"start": v(-11.83, 162.17) * mm, "end": v(-11.6, 161.1) * mm});
            skLineSegment(sketch, "E3338", {"start": v(-11.6, 161.1) * mm, "end": v(-11.29, 159.98) * mm});
            skLineSegment(sketch, "E3339", {"start": v(-11.29, 159.98) * mm, "end": v(-10.86, 158.88) * mm});
            skLineSegment(sketch, "E3340", {"start": v(-10.86, 158.88) * mm, "end": v(-10.4, 157.84) * mm});
            skLineSegment(sketch, "E3341", {"start": v(-10.4, 157.84) * mm, "end": v(-10.23, 157.5) * mm});
            skLineSegment(sketch, "E3342", {"start": v(-10.23, 157.5) * mm, "end": v(-10.04, 157.1) * mm});
            skLineSegment(sketch, "E3343", {"start": v(-10.04, 157.1) * mm, "end": v(-9.4, 155.93) * mm});
            skLineSegment(sketch, "E3344", {"start": v(-9.4, 155.93) * mm, "end": v(-8.42, 154.34) * mm});
            skLineSegment(sketch, "E3345", {"start": v(-8.42, 154.34) * mm, "end": v(-7.47, 152.96) * mm});
            skLineSegment(sketch, "E3346", {"start": v(-7.47, 152.96) * mm, "end": v(-6.91, 152.25) * mm});
            skLineSegment(sketch, "E3347", {"start": v(-6.91, 152.25) * mm, "end": v(-6.71, 152.04) * mm});
            skLineSegment(sketch, "E3348", {"start": v(-6.71, 152.04) * mm, "end": v(-6.69, 152.01) * mm});
            skLineSegment(sketch, "E3349", {"start": v(-6.69, 152.01) * mm, "end": v(-6.45, 151.77) * mm});
            skLineSegment(sketch, "E3350", {"start": v(-6.45, 151.77) * mm, "end": v(-6.43, 151.75) * mm});
            skLineSegment(sketch, "E3351", {"start": v(-6.43, 151.75) * mm, "end": v(-6.4, 151.73) * mm});
            skLineSegment(sketch, "E3352", {"start": v(-6.4, 151.73) * mm, "end": v(-6.23, 151.57) * mm});
            skLineSegment(sketch, "E3353", {"start": v(-6.23, 151.57) * mm, "end": v(-6.2, 151.56) * mm});
            skLineSegment(sketch, "E3354", {"start": v(-6.2, 151.56) * mm, "end": v(-6.15, 151.51) * mm});
            skLineSegment(sketch, "E3355", {"start": v(-6.15, 151.51) * mm, "end": v(-5.3, 151.05) * mm});
            skLineSegment(sketch, "E3356", {"start": v(-5.3, 151.05) * mm, "end": v(-5.2, 151) * mm});
            skLineSegment(sketch, "E3357", {"start": v(-5.2, 151) * mm, "end": v(-5.1, 150.96) * mm});
            skLineSegment(sketch, "E3358", {"start": v(-5.1, 150.96) * mm, "end": v(-3.86, 150.47) * mm});
            skLineSegment(sketch, "E3359", {"start": v(-3.86, 150.47) * mm, "end": v(-3.71, 150.41) * mm});
            skLineSegment(sketch, "E3360", {"start": v(-3.71, 150.41) * mm, "end": v(-3.6, 150.37) * mm});
            skLineSegment(sketch, "E3361", {"start": v(-3.6, 150.37) * mm, "end": v(-3.25, 150.25) * mm});
            skLineSegment(sketch, "E3362", {"start": v(-3.25, 150.25) * mm, "end": v(-2.68, 150.04) * mm});
            skLineSegment(sketch, "E3363", {"start": v(-2.68, 150.04) * mm, "end": v(-2.08, 149.82) * mm});
            skLineSegment(sketch, "E3364", {"start": v(-2.08, 149.82) * mm, "end": v(-1.47, 149.59) * mm});
            skLineSegment(sketch, "E3365", {"start": v(-1.47, 149.59) * mm, "end": v(-0.93, 149.38) * mm});
            skLineSegment(sketch, "E3366", {"start": v(-0.93, 149.38) * mm, "end": v(-0.5, 149.2) * mm});
            skLineSegment(sketch, "E3367", {"start": v(-0.5, 149.2) * mm, "end": v(-0.22, 149.09) * mm});
            skLineSegment(sketch, "E3368", {"start": v(-0.22, 149.09) * mm, "end": v(-0.15, 149.04) * mm});
            skLineSegment(sketch, "E3369", {"start": v(-0.15, 149.04) * mm, "end": v(-0.33, 149.04) * mm});
            skLineSegment(sketch, "E3370", {"start": v(-0.33, 149.04) * mm, "end": v(-0.85, 149.13) * mm});
            skLineSegment(sketch, "E3371", {"start": v(-0.85, 149.13) * mm, "end": v(-1.99, 149.35) * mm});
            skLineSegment(sketch, "E3372", {"start": v(-1.99, 149.35) * mm, "end": v(-3.16, 149.59) * mm});
            skLineSegment(sketch, "E3373", {"start": v(-3.16, 149.59) * mm, "end": v(-3.8, 149.72) * mm});
            skLineSegment(sketch, "E3374", {"start": v(-3.8, 149.72) * mm, "end": v(-3.98, 149.76) * mm});
            skLineSegment(sketch, "E3375", {"start": v(-3.98, 149.76) * mm, "end": v(-4.22, 149.81) * mm});
            skLineSegment(sketch, "E3376", {"start": v(-4.22, 149.81) * mm, "end": v(-5.34, 150.14) * mm});
            skLineSegment(sketch, "E3377", {"start": v(-5.34, 150.14) * mm, "end": v(-6.13, 150.47) * mm});
            skLineSegment(sketch, "E3378", {"start": v(-6.13, 150.47) * mm, "end": v(-6.2, 150.52) * mm});
            skLineSegment(sketch, "E3379", {"start": v(-6.2, 150.52) * mm, "end": v(-6.26, 150.55) * mm});
            skLineSegment(sketch, "E3380", {"start": v(-6.26, 150.55) * mm, "end": v(-6.64, 150.86) * mm});
            skLineSegment(sketch, "E3381", {"start": v(-6.64, 150.86) * mm, "end": v(-6.67, 150.9) * mm});
            skLineSegment(sketch, "E3382", {"start": v(-6.67, 150.9) * mm, "end": v(-6.73, 150.95) * mm});
            skLineSegment(sketch, "E3383", {"start": v(-6.73, 150.95) * mm, "end": v(-6.73, 150.95) * mm});
            skLineSegment(sketch, "E3384", {"start": v(-6.73, 150.95) * mm, "end": v(-6.77, 150.97) * mm});
            skLineSegment(sketch, "E3385", {"start": v(-6.77, 150.97) * mm, "end": v(-6.78, 151) * mm});
            skLineSegment(sketch, "E3386", {"start": v(-6.78, 151) * mm, "end": v(-6.92, 151.15) * mm});
            skLineSegment(sketch, "E3387", {"start": v(-6.92, 151.15) * mm, "end": v(-6.93, 151.16) * mm});
            skLineSegment(sketch, "E3388", {"start": v(-6.93, 151.16) * mm, "end": v(-6.97, 151.22) * mm});
            skLineSegment(sketch, "E3389", {"start": v(-6.97, 151.22) * mm, "end": v(-6.98, 151.23) * mm});
            skLineSegment(sketch, "E3390", {"start": v(-6.98, 151.23) * mm, "end": v(-7, 151.25) * mm});
            skLineSegment(sketch, "E3391", {"start": v(-7, 151.25) * mm, "end": v(-7, 151.25) * mm});
            skLineSegment(sketch, "E3392", {"start": v(-7, 151.25) * mm, "end": v(-7.04, 151.18) * mm});
            skLineSegment(sketch, "E3393", {"start": v(-7.04, 151.18) * mm, "end": v(-7.04, 151.16) * mm});
            skLineSegment(sketch, "E3394", {"start": v(-7.04, 151.16) * mm, "end": v(-7.04, 151.14) * mm});
            skLineSegment(sketch, "E3395", {"start": v(-7.04, 151.14) * mm, "end": v(-7.06, 151) * mm});
            skLineSegment(sketch, "E3396", {"start": v(-7.06, 151) * mm, "end": v(-7.15, 150.6) * mm});
            skLineSegment(sketch, "E3397", {"start": v(-7.15, 150.6) * mm, "end": v(-7.17, 150.48) * mm});
            skLineSegment(sketch, "E3398", {"start": v(-7.17, 150.48) * mm, "end": v(-7.18, 150.44) * mm});
            skLineSegment(sketch, "E3399", {"start": v(-7.18, 150.44) * mm, "end": v(-7.26, 150.05) * mm});
            skLineSegment(sketch, "E3400", {"start": v(-7.26, 150.05) * mm, "end": v(-7.26, 150.01) * mm});
            skLineSegment(sketch, "E3401", {"start": v(-7.26, 150.01) * mm, "end": v(-7.34, 149.76) * mm});
            skLineSegment(sketch, "E3402", {"start": v(-7.34, 149.76) * mm, "end": v(-7.9, 148.44) * mm});
            skLineSegment(sketch, "E3403", {"start": v(-7.9, 148.44) * mm, "end": v(-8.83, 147.03) * mm});
            skLineSegment(sketch, "E3404", {"start": v(-8.83, 147.03) * mm, "end": v(-9.09, 146.72) * mm});
            skLineSegment(sketch, "E3405", {"start": v(-9.09, 146.72) * mm, "end": v(-9.07, 146.83) * mm});
            skLineSegment(sketch, "E3406", {"start": v(-9.07, 146.83) * mm, "end": v(-9.2, 147.19) * mm});
            skLineSegment(sketch, "E3407", {"start": v(-9.2, 147.19) * mm, "end": v(-9.64, 147.15) * mm});
            skLineSegment(sketch, "E3408", {"start": v(-9.64, 147.15) * mm, "end": v(-9.74, 147.08) * mm});
            skLineSegment(sketch, "E3409", {"start": v(-9.74, 147.08) * mm, "end": v(-10.04, 146.88) * mm});
            skLineSegment(sketch, "E3410", {"start": v(-10.04, 146.88) * mm, "end": v(-10.94, 146.31) * mm});
            skLineSegment(sketch, "E3411", {"start": v(-10.94, 146.31) * mm, "end": v(-11.99, 145.8) * mm});
            skLineSegment(sketch, "E3412", {"start": v(-11.99, 145.8) * mm, "end": v(-12.98, 145.52) * mm});
            skLineSegment(sketch, "E3413", {"start": v(-12.98, 145.52) * mm, "end": v(-13.75, 145.45) * mm});
            skLineSegment(sketch, "E3414", {"start": v(-13.75, 145.45) * mm, "end": v(-14.01, 145.47) * mm});
            skLineSegment(sketch, "E3415", {"start": v(-14.01, 145.47) * mm, "end": v(-14.2, 145.48) * mm});
            skLineSegment(sketch, "E3416", {"start": v(-14.2, 145.48) * mm, "end": v(-14.74, 145.6) * mm});
            skLineSegment(sketch, "E3417", {"start": v(-14.74, 145.6) * mm, "end": v(-15.28, 145.8) * mm});
            skLineSegment(sketch, "E3418", {"start": v(-15.28, 145.8) * mm, "end": v(-15.63, 145.96) * mm});
            skLineSegment(sketch, "E3419", {"start": v(-15.63, 145.96) * mm, "end": v(-15.77, 145.97) * mm});
            skLineSegment(sketch, "E3420", {"start": v(-15.77, 145.97) * mm, "end": v(-15.78, 145.95) * mm});
            skLineSegment(sketch, "E3421", {"start": v(-15.78, 145.95) * mm, "end": v(-15.79, 145.94) * mm});
            skLineSegment(sketch, "E3422", {"start": v(-15.79, 145.94) * mm, "end": v(-15.8, 145.7) * mm});
            skLineSegment(sketch, "E3423", {"start": v(-15.8, 145.7) * mm, "end": v(-15.8, 145.68) * mm});
            skLineSegment(sketch, "E3424", {"start": v(-15.8, 145.68) * mm, "end": v(-15.8, 145.59) * mm});
            skLineSegment(sketch, "E3425", {"start": v(-15.8, 145.59) * mm, "end": v(-15.44, 144.97) * mm});
            skLineSegment(sketch, "E3426", {"start": v(-15.44, 144.97) * mm, "end": v(-14.77, 144.4) * mm});
            skLineSegment(sketch, "E3427", {"start": v(-14.77, 144.4) * mm, "end": v(-14.6, 144.32) * mm});
            skLineSegment(sketch, "E3428", {"start": v(-14.6, 144.32) * mm, "end": v(-14.47, 144.27) * mm});
            skLineSegment(sketch, "E3429", {"start": v(-14.47, 144.27) * mm, "end": v(-13.79, 144.07) * mm});
            skLineSegment(sketch, "E3430", {"start": v(-13.79, 144.07) * mm, "end": v(-13.03, 144) * mm});
            skLineSegment(sketch, "E3431", {"start": v(-13.03, 144) * mm, "end": v(-12.86, 144) * mm});
            skLineSegment(sketch, "E3432", {"start": v(-12.86, 144) * mm, "end": v(-13, 143.96) * mm});
            skLineSegment(sketch, "E3433", {"start": v(-13, 143.96) * mm, "end": v(-13.43, 143.85) * mm});
            skLineSegment(sketch, "E3434", {"start": v(-13.43, 143.85) * mm, "end": v(-13.93, 143.75) * mm});
            skLineSegment(sketch, "E3435", {"start": v(-13.93, 143.75) * mm, "end": v(-14.4, 143.66) * mm});
            skLineSegment(sketch, "E3436", {"start": v(-14.4, 143.66) * mm, "end": v(-14.9, 143.55) * mm});
            skLineSegment(sketch, "E3437", {"start": v(-14.9, 143.55) * mm, "end": v(-15.46, 143.4) * mm});
            skLineSegment(sketch, "E3438", {"start": v(-15.46, 143.4) * mm, "end": v(-16.15, 143.17) * mm});
            skLineSegment(sketch, "E3439", {"start": v(-16.15, 143.17) * mm, "end": v(-17, 142.83) * mm});
            skLineSegment(sketch, "E3440", {"start": v(-17, 142.83) * mm, "end": v(-17.8, 142.47) * mm});
            skLineSegment(sketch, "E3441", {"start": v(-17.8, 142.47) * mm, "end": v(-18.06, 142.35) * mm});
            skLineSegment(sketch, "E3442", {"start": v(-18.06, 142.35) * mm, "end": v(-18.19, 142.29) * mm});
            skLineSegment(sketch, "E3443", {"start": v(-18.19, 142.29) * mm, "end": v(-18.96, 141.87) * mm});
            skLineSegment(sketch, "E3444", {"start": v(-18.96, 141.87) * mm, "end": v(-19.7, 141.42) * mm});
            skLineSegment(sketch, "E3445", {"start": v(-19.7, 141.42) * mm, "end": v(-19.81, 141.34) * mm});
            skLineSegment(sketch, "E3446", {"start": v(-19.81, 141.34) * mm, "end": v(-20.16, 141.1) * mm});
            skLineSegment(sketch, "E3447", {"start": v(-20.16, 141.1) * mm, "end": v(-21.7, 139.61) * mm});
            skLineSegment(sketch, "E3448", {"start": v(-21.7, 139.61) * mm, "end": v(-22.9, 137.88) * mm});
            skLineSegment(sketch, "E3449", {"start": v(-22.9, 137.88) * mm, "end": v(-23.08, 137.5) * mm});
            skLineSegment(sketch, "E3450", {"start": v(-23.08, 137.5) * mm, "end": v(-23.25, 137.16) * mm});
            skLineSegment(sketch, "E3451", {"start": v(-23.25, 137.16) * mm, "end": v(-23.88, 135.57) * mm});
            skLineSegment(sketch, "E3452", {"start": v(-23.88, 135.57) * mm, "end": v(-24.24, 134.2) * mm});
            skLineSegment(sketch, "E3453", {"start": v(-24.24, 134.2) * mm, "end": v(-24.28, 133.97) * mm});
            skLineSegment(sketch, "E3454", {"start": v(-24.28, 133.97) * mm, "end": v(-24.3, 133.83) * mm});
            skLineSegment(sketch, "E3455", {"start": v(-24.3, 133.83) * mm, "end": v(-24.34, 133.4) * mm});
            skLineSegment(sketch, "E3456", {"start": v(-24.34, 133.4) * mm, "end": v(-24.38, 132.84) * mm});
            skLineSegment(sketch, "E3457", {"start": v(-24.38, 132.84) * mm, "end": v(-24.39, 132.4) * mm});
            skLineSegment(sketch, "E3458", {"start": v(-24.39, 132.4) * mm, "end": v(-24.39, 132.26) * mm});
            skLineSegment(sketch, "E3459", {"start": v(-24.39, 132.26) * mm, "end": v(-24.39, 132.21) * mm});
            skLineSegment(sketch, "E3460", {"start": v(1.21, 157.77) * mm, "end": v(1.16, 157.75) * mm});
            skLineSegment(sketch, "E3461", {"start": v(1.16, 157.75) * mm, "end": v(0.89, 157.82) * mm});
            skLineSegment(sketch, "E3462", {"start": v(0.89, 157.82) * mm, "end": v(0.7, 158.07) * mm});
            skLineSegment(sketch, "E3463", {"start": v(0.7, 158.07) * mm, "end": v(0.68, 158.14) * mm});
            skLineSegment(sketch, "E3464", {"start": v(0.68, 158.14) * mm, "end": v(0.66, 158.2) * mm});
            skLineSegment(sketch, "E3465", {"start": v(0.66, 158.2) * mm, "end": v(0.7, 158.51) * mm});
            skLineSegment(sketch, "E3466", {"start": v(0.7, 158.51) * mm, "end": v(0.9, 158.71) * mm});
            skLineSegment(sketch, "E3467", {"start": v(0.9, 158.71) * mm, "end": v(0.96, 158.72) * mm});
            skLineSegment(sketch, "E3468", {"start": v(0.96, 158.72) * mm, "end": v(1.02, 158.74) * mm});
            skLineSegment(sketch, "E3469", {"start": v(1.02, 158.74) * mm, "end": v(1.3, 158.67) * mm});
            skLineSegment(sketch, "E3470", {"start": v(1.3, 158.67) * mm, "end": v(1.5, 158.43) * mm});
            skLineSegment(sketch, "E3471", {"start": v(1.5, 158.43) * mm, "end": v(1.5, 158.37) * mm});
            skLineSegment(sketch, "E3472", {"start": v(1.5, 158.37) * mm, "end": v(1.53, 158.3) * mm});
            skLineSegment(sketch, "E3473", {"start": v(1.53, 158.3) * mm, "end": v(1.47, 157.98) * mm});
            skLineSegment(sketch, "E3474", {"start": v(1.47, 157.98) * mm, "end": v(1.27, 157.78) * mm});
            skLineSegment(sketch, "E3475", {"start": v(1.27, 157.78) * mm, "end": v(1.21, 157.77) * mm});
            skLineSegment(sketch, "E3476", {"start": v(2.4, 155.42) * mm, "end": v(2.42, 155.36) * mm});
            skLineSegment(sketch, "E3477", {"start": v(2.42, 155.36) * mm, "end": v(2.38, 155.06) * mm});
            skLineSegment(sketch, "E3478", {"start": v(2.38, 155.06) * mm, "end": v(2.19, 154.86) * mm});
            skLineSegment(sketch, "E3479", {"start": v(2.19, 154.86) * mm, "end": v(2.13, 154.84) * mm});
            skLineSegment(sketch, "E3480", {"start": v(2.13, 154.84) * mm, "end": v(2.08, 154.83) * mm});
            skLineSegment(sketch, "E3481", {"start": v(2.08, 154.83) * mm, "end": v(1.8, 154.91) * mm});
            skLineSegment(sketch, "E3482", {"start": v(1.8, 154.91) * mm, "end": v(1.6, 155.14) * mm});
            skLineSegment(sketch, "E3483", {"start": v(1.6, 155.14) * mm, "end": v(1.58, 155.2) * mm});
            skLineSegment(sketch, "E3484", {"start": v(1.58, 155.2) * mm, "end": v(1.56, 155.28) * mm});
            skLineSegment(sketch, "E3485", {"start": v(1.56, 155.28) * mm, "end": v(1.6, 155.6) * mm});
            skLineSegment(sketch, "E3486", {"start": v(1.6, 155.6) * mm, "end": v(1.8, 155.8) * mm});
            skLineSegment(sketch, "E3487", {"start": v(1.8, 155.8) * mm, "end": v(1.86, 155.81) * mm});
            skLineSegment(sketch, "E3488", {"start": v(1.86, 155.81) * mm, "end": v(1.92, 155.83) * mm});
            skLineSegment(sketch, "E3489", {"start": v(1.92, 155.83) * mm, "end": v(2.2, 155.75) * mm});
            skLineSegment(sketch, "E3490", {"start": v(2.2, 155.75) * mm, "end": v(2.38, 155.5) * mm});
            skLineSegment(sketch, "E3491", {"start": v(2.38, 155.5) * mm, "end": v(2.4, 155.42) * mm});
            skLineSegment(sketch, "E3492", {"start": v(-3.62, 164.65) * mm, "end": v(-3.6, 164.68) * mm});
            skLineSegment(sketch, "E3493", {"start": v(-3.6, 164.68) * mm, "end": v(-3.35, 164.84) * mm});
            skLineSegment(sketch, "E3494", {"start": v(-3.35, 164.84) * mm, "end": v(-2.82, 165.11) * mm});
            skLineSegment(sketch, "E3495", {"start": v(-2.82, 165.11) * mm, "end": v(-2.29, 165.34) * mm});
            skLineSegment(sketch, "E3496", {"start": v(-2.29, 165.34) * mm, "end": v(-2.04, 165.4) * mm});
            skLineSegment(sketch, "E3497", {"start": v(-2.04, 165.4) * mm, "end": v(-2.04, 165.39) * mm});
            skLineSegment(sketch, "E3498", {"start": v(-2.04, 165.39) * mm, "end": v(-2.02, 165.33) * mm});
            skLineSegment(sketch, "E3499", {"start": v(-2.02, 165.33) * mm, "end": v(-2.1, 165.12) * mm});
            skLineSegment(sketch, "E3500", {"start": v(-2.1, 165.12) * mm, "end": v(-2.34, 164.87) * mm});
            skLineSegment(sketch, "E3501", {"start": v(-2.34, 164.87) * mm, "end": v(-2.59, 164.64) * mm});
            skLineSegment(sketch, "E3502", {"start": v(-2.59, 164.64) * mm, "end": v(-2.66, 164.48) * mm});
            skLineSegment(sketch, "E3503", {"start": v(-2.66, 164.48) * mm, "end": v(-2.64, 164.45) * mm});
            skLineSegment(sketch, "E3504", {"start": v(-2.64, 164.45) * mm, "end": v(-2.63, 164.42) * mm});
            skLineSegment(sketch, "E3505", {"start": v(-2.63, 164.42) * mm, "end": v(-2.4, 164.23) * mm});
            skLineSegment(sketch, "E3506", {"start": v(-2.4, 164.23) * mm, "end": v(-1.86, 163.78) * mm});
            skLineSegment(sketch, "E3507", {"start": v(-1.86, 163.78) * mm, "end": v(-1.12, 163.13) * mm});
            skLineSegment(sketch, "E3508", {"start": v(-1.12, 163.13) * mm, "end": v(-0.48, 162.52) * mm});
            skLineSegment(sketch, "E3509", {"start": v(-0.48, 162.52) * mm, "end": v(-0.27, 162.3) * mm});
            skLineSegment(sketch, "E3510", {"start": v(-0.27, 162.3) * mm, "end": v(-0.11, 162.14) * mm});
            skLineSegment(sketch, "E3511", {"start": v(-0.11, 162.14) * mm, "end": v(0.35, 161.62) * mm});
            skLineSegment(sketch, "E3512", {"start": v(0.35, 161.62) * mm, "end": v(0.78, 161.08) * mm});
            skLineSegment(sketch, "E3513", {"start": v(0.78, 161.08) * mm, "end": v(1.05, 160.68) * mm});
            skLineSegment(sketch, "E3514", {"start": v(1.05, 160.68) * mm, "end": v(1.17, 160.48) * mm});
            skLineSegment(sketch, "E3515", {"start": v(1.17, 160.48) * mm, "end": v(1.21, 160.4) * mm});
            skLineSegment(sketch, "E3516", {"start": v(1.21, 160.4) * mm, "end": v(1.24, 160.35) * mm});
            skLineSegment(sketch, "E3517", {"start": v(1.24, 160.35) * mm, "end": v(1.36, 160.02) * mm});
            skLineSegment(sketch, "E3518", {"start": v(1.36, 160.02) * mm, "end": v(1.43, 159.8) * mm});
            skLineSegment(sketch, "E3519", {"start": v(1.43, 159.8) * mm, "end": v(1.37, 159.87) * mm});
            skLineSegment(sketch, "E3520", {"start": v(1.37, 159.87) * mm, "end": v(1.2, 160.1) * mm});
            skLineSegment(sketch, "E3521", {"start": v(1.2, 160.1) * mm, "end": v(1.02, 160.38) * mm});
            skLineSegment(sketch, "E3522", {"start": v(1.02, 160.38) * mm, "end": v(0.75, 160.73) * mm});
            skLineSegment(sketch, "E3523", {"start": v(0.75, 160.73) * mm, "end": v(0.38, 161.15) * mm});
            skLineSegment(sketch, "E3524", {"start": v(0.38, 161.15) * mm, "end": v(0.26, 161.28) * mm});
            skLineSegment(sketch, "E3525", {"start": v(0.26, 161.28) * mm, "end": v(-0.06, 161.61) * mm});
            skLineSegment(sketch, "E3526", {"start": v(-0.06, 161.61) * mm, "end": v(-1.07, 162.53) * mm});
            skLineSegment(sketch, "E3527", {"start": v(-1.07, 162.53) * mm, "end": v(-2.33, 163.57) * mm});
            skLineSegment(sketch, "E3528", {"start": v(-2.33, 163.57) * mm, "end": v(-3.28, 164.3) * mm});
            skLineSegment(sketch, "E3529", {"start": v(-3.28, 164.3) * mm, "end": v(-3.64, 164.6) * mm});
            skLineSegment(sketch, "E3530", {"start": v(-3.64, 164.6) * mm, "end": v(-3.62, 164.65) * mm});
            skLineSegment(sketch, "E3531", {"start": v(10.35, 171.2) * mm, "end": v(10.36, 171.26) * mm});
            skLineSegment(sketch, "E3532", {"start": v(10.36, 171.26) * mm, "end": v(10.42, 171.47) * mm});
            skLineSegment(sketch, "E3533", {"start": v(10.42, 171.47) * mm, "end": v(10.42, 171.59) * mm});
            skLineSegment(sketch, "E3534", {"start": v(10.42, 171.59) * mm, "end": v(10.38, 171.58) * mm});
            skLineSegment(sketch, "E3535", {"start": v(10.38, 171.58) * mm, "end": v(10.3, 171.47) * mm});
            skLineSegment(sketch, "E3536", {"start": v(10.3, 171.47) * mm, "end": v(10.29, 171.43) * mm});
            skLineSegment(sketch, "E3537", {"start": v(10.29, 171.43) * mm, "end": v(10.27, 171.4) * mm});
            skLineSegment(sketch, "E3538", {"start": v(10.27, 171.4) * mm, "end": v(10.22, 171.15) * mm});
            skLineSegment(sketch, "E3539", {"start": v(10.22, 171.15) * mm, "end": v(10.21, 171) * mm});
            skLineSegment(sketch, "E3540", {"start": v(10.21, 171) * mm, "end": v(10.21, 170.95) * mm});
            skLineSegment(sketch, "E3541", {"start": v(10.21, 170.95) * mm, "end": v(10.27, 170.98) * mm});
            skLineSegment(sketch, "E3542", {"start": v(10.27, 170.98) * mm, "end": v(10.34, 171.16) * mm});
            skLineSegment(sketch, "E3543", {"start": v(10.34, 171.16) * mm, "end": v(10.35, 171.2) * mm});
            skLineSegment(sketch, "E3544", {"start": v(-3.57, 178.02) * mm, "end": v(-3.49, 177.94) * mm});
            skLineSegment(sketch, "E3545", {"start": v(-3.49, 177.94) * mm, "end": v(-2.96, 177.67) * mm});
            skLineSegment(sketch, "E3546", {"start": v(-2.96, 177.67) * mm, "end": v(-2.45, 177.53) * mm});
            skLineSegment(sketch, "E3547", {"start": v(-2.45, 177.53) * mm, "end": v(-2.38, 177.52) * mm});
            skLineSegment(sketch, "E3548", {"start": v(-2.38, 177.52) * mm, "end": v(-2.31, 177.52) * mm});
            skLineSegment(sketch, "E3549", {"start": v(-2.31, 177.52) * mm, "end": v(-2.16, 177.51) * mm});
            skLineSegment(sketch, "E3550", {"start": v(-2.16, 177.51) * mm, "end": v(-2.11, 177.5) * mm});
            skLineSegment(sketch, "E3551", {"start": v(-2.11, 177.5) * mm, "end": v(-2.08, 177.5) * mm});
            skLineSegment(sketch, "E3552", {"start": v(-2.08, 177.5) * mm, "end": v(-1.81, 177.5) * mm});
            skLineSegment(sketch, "E3553", {"start": v(-1.81, 177.5) * mm, "end": v(-1.55, 177.44) * mm});
            skLineSegment(sketch, "E3554", {"start": v(-1.55, 177.44) * mm, "end": v(-1.52, 177.42) * mm});
            skLineSegment(sketch, "E3555", {"start": v(-1.52, 177.42) * mm, "end": v(-1.5, 177.38) * mm});
            skLineSegment(sketch, "E3556", {"start": v(-1.5, 177.38) * mm, "end": v(-1.63, 177.14) * mm});
            skLineSegment(sketch, "E3557", {"start": v(-1.63, 177.14) * mm, "end": v(-2.16, 177.03) * mm});
            skLineSegment(sketch, "E3558", {"start": v(-2.16, 177.03) * mm, "end": v(-2.32, 177.05) * mm});
            skLineSegment(sketch, "E3559", {"start": v(-2.32, 177.05) * mm, "end": v(-2.43, 177.07) * mm});
            skLineSegment(sketch, "E3560", {"start": v(-2.43, 177.07) * mm, "end": v(-2.94, 176.92) * mm});
            skLineSegment(sketch, "E3561", {"start": v(-2.94, 176.92) * mm, "end": v(-3.24, 176.41) * mm});
            skLineSegment(sketch, "E3562", {"start": v(-3.24, 176.41) * mm, "end": v(-3.25, 176.25) * mm});
            skLineSegment(sketch, "E3563", {"start": v(-3.25, 176.25) * mm, "end": v(-3.27, 176.04) * mm});
            skLineSegment(sketch, "E3564", {"start": v(-3.27, 176.04) * mm, "end": v(-3.13, 175.19) * mm});
            skLineSegment(sketch, "E3565", {"start": v(-3.13, 175.19) * mm, "end": v(-3, 174.54) * mm});
            skLineSegment(sketch, "E3566", {"start": v(-3, 174.54) * mm, "end": v(-3, 174.44) * mm});
            skLineSegment(sketch, "E3567", {"start": v(-3, 174.44) * mm, "end": v(-3.01, 174.36) * mm});
            skLineSegment(sketch, "E3568", {"start": v(-3.01, 174.36) * mm, "end": v(-3.16, 174.16) * mm});
            skLineSegment(sketch, "E3569", {"start": v(-3.16, 174.16) * mm, "end": v(-3.35, 174.1) * mm});
            skLineSegment(sketch, "E3570", {"start": v(-3.35, 174.1) * mm, "end": v(-3.38, 174.1) * mm});
            skLineSegment(sketch, "E3571", {"start": v(-3.38, 174.1) * mm, "end": v(-3.4, 174.1) * mm});
            skLineSegment(sketch, "E3572", {"start": v(-3.4, 174.1) * mm, "end": v(-3.6, 174.06) * mm});
            skLineSegment(sketch, "E3573", {"start": v(-3.6, 174.06) * mm, "end": v(-3.6, 174.05) * mm});
            skLineSegment(sketch, "E3574", {"start": v(-3.6, 174.05) * mm, "end": v(-3.63, 174.04) * mm});
            skLineSegment(sketch, "E3575", {"start": v(-3.63, 174.04) * mm, "end": v(-3.6, 173.81) * mm});
            skLineSegment(sketch, "E3576", {"start": v(-3.6, 173.81) * mm, "end": v(-3.37, 173.6) * mm});
            skLineSegment(sketch, "E3577", {"start": v(-3.37, 173.6) * mm, "end": v(-3.3, 173.57) * mm});
            skLineSegment(sketch, "E3578", {"start": v(-3.3, 173.57) * mm, "end": v(-3.27, 173.57) * mm});
            skLineSegment(sketch, "E3579", {"start": v(-3.27, 173.57) * mm, "end": v(-2.98, 173.54) * mm});
            skLineSegment(sketch, "E3580", {"start": v(-2.98, 173.54) * mm, "end": v(-2.95, 173.55) * mm});
            skLineSegment(sketch, "E3581", {"start": v(-2.95, 173.55) * mm, "end": v(-2.88, 173.55) * mm});
            skLineSegment(sketch, "E3582", {"start": v(-2.88, 173.55) * mm, "end": v(-2.67, 173.6) * mm});
            skLineSegment(sketch, "E3583", {"start": v(-2.67, 173.6) * mm, "end": v(-2.42, 173.66) * mm});
            skLineSegment(sketch, "E3584", {"start": v(-2.42, 173.66) * mm, "end": v(-2.34, 173.66) * mm});
            skLineSegment(sketch, "E3585", {"start": v(-2.34, 173.66) * mm, "end": v(-2.23, 173.66) * mm});
            skLineSegment(sketch, "E3586", {"start": v(-2.23, 173.66) * mm, "end": v(-1.94, 173.57) * mm});
            skLineSegment(sketch, "E3587", {"start": v(-1.94, 173.57) * mm, "end": v(-1.9, 173.55) * mm});
            skLineSegment(sketch, "E3588", {"start": v(-1.9, 173.55) * mm, "end": v(-1.83, 173.52) * mm});
            skLineSegment(sketch, "E3589", {"start": v(-1.83, 173.52) * mm, "end": v(-1.26, 173.14) * mm});
            skLineSegment(sketch, "E3590", {"start": v(-1.26, 173.14) * mm, "end": v(-1.22, 173.11) * mm});
            skLineSegment(sketch, "E3591", {"start": v(-1.22, 173.11) * mm, "end": v(-1.2, 173.06) * mm});
            skLineSegment(sketch, "E3592", {"start": v(-1.2, 173.06) * mm, "end": v(-1.07, 172.79) * mm});
            skLineSegment(sketch, "E3593", {"start": v(-1.07, 172.79) * mm, "end": v(-0.92, 172.59) * mm});
            skLineSegment(sketch, "E3594", {"start": v(-0.92, 172.59) * mm, "end": v(-0.9, 172.58) * mm});
            skLineSegment(sketch, "E3595", {"start": v(-0.9, 172.58) * mm, "end": v(-0.85, 172.57) * mm});
            skLineSegment(sketch, "E3596", {"start": v(-0.85, 172.57) * mm, "end": v(-0.63, 172.75) * mm});
            skLineSegment(sketch, "E3597", {"start": v(-0.63, 172.75) * mm, "end": v(-0.53, 172.99) * mm});
            skLineSegment(sketch, "E3598", {"start": v(-0.53, 172.99) * mm, "end": v(-0.55, 173) * mm});
            skLineSegment(sketch, "E3599", {"start": v(-0.55, 173) * mm, "end": v(-0.72, 173.02) * mm});
            skLineSegment(sketch, "E3600", {"start": v(-0.72, 173.02) * mm, "end": v(-0.99, 173.11) * mm});
            skLineSegment(sketch, "E3601", {"start": v(-0.99, 173.11) * mm, "end": v(-1.03, 173.15) * mm});
            skLineSegment(sketch, "E3602", {"start": v(-1.03, 173.15) * mm, "end": v(-1.04, 173.21) * mm});
            skLineSegment(sketch, "E3603", {"start": v(-1.04, 173.21) * mm, "end": v(-1.17, 173.81) * mm});
            skLineSegment(sketch, "E3604", {"start": v(-1.17, 173.81) * mm, "end": v(-1.19, 173.85) * mm});
            skLineSegment(sketch, "E3605", {"start": v(-1.19, 173.85) * mm, "end": v(-1.21, 173.92) * mm});
            skLineSegment(sketch, "E3606", {"start": v(-1.21, 173.92) * mm, "end": v(-1.43, 174.63) * mm});
            skLineSegment(sketch, "E3607", {"start": v(-1.43, 174.63) * mm, "end": v(-1.44, 174.7) * mm});
            skLineSegment(sketch, "E3608", {"start": v(-1.44, 174.7) * mm, "end": v(-1.44, 174.78) * mm});
            skLineSegment(sketch, "E3609", {"start": v(-1.44, 174.78) * mm, "end": v(-1.4, 175) * mm});
            skLineSegment(sketch, "E3610", {"start": v(-1.4, 175) * mm, "end": v(-1.22, 175.32) * mm});
            skLineSegment(sketch, "E3611", {"start": v(-1.22, 175.32) * mm, "end": v(-0.93, 175.55) * mm});
            skLineSegment(sketch, "E3612", {"start": v(-0.93, 175.55) * mm, "end": v(-0.63, 175.61) * mm});
            skLineSegment(sketch, "E3613", {"start": v(-0.63, 175.61) * mm, "end": v(-0.53, 175.6) * mm});
            skLineSegment(sketch, "E3614", {"start": v(-0.53, 175.6) * mm, "end": v(-0.47, 175.58) * mm});
            skLineSegment(sketch, "E3615", {"start": v(-0.47, 175.58) * mm, "end": v(-0.25, 175.34) * mm});
            skLineSegment(sketch, "E3616", {"start": v(-0.25, 175.34) * mm, "end": v(-0.14, 174.98) * mm});
            skLineSegment(sketch, "E3617", {"start": v(-0.14, 174.98) * mm, "end": v(-0.13, 174.9) * mm});
            skLineSegment(sketch, "E3618", {"start": v(-0.13, 174.9) * mm, "end": v(-0.14, 174.92) * mm});
            skLineSegment(sketch, "E3619", {"start": v(-0.14, 174.92) * mm, "end": v(-0.3, 175.05) * mm});
            skLineSegment(sketch, "E3620", {"start": v(-0.3, 175.05) * mm, "end": v(-0.32, 175.06) * mm});
            skLineSegment(sketch, "E3621", {"start": v(-0.32, 175.06) * mm, "end": v(-0.33, 175.06) * mm});
            skLineSegment(sketch, "E3622", {"start": v(-0.33, 175.06) * mm, "end": v(-0.56, 175.01) * mm});
            skLineSegment(sketch, "E3623", {"start": v(-0.56, 175.01) * mm, "end": v(-0.58, 174.99) * mm});
            skLineSegment(sketch, "E3624", {"start": v(-0.58, 174.99) * mm, "end": v(-0.59, 174.97) * mm});
            skLineSegment(sketch, "E3625", {"start": v(-0.59, 174.97) * mm, "end": v(-0.54, 174.88) * mm});
            skLineSegment(sketch, "E3626", {"start": v(-0.54, 174.88) * mm, "end": v(-0.43, 174.82) * mm});
            skLineSegment(sketch, "E3627", {"start": v(-0.43, 174.82) * mm, "end": v(-0.42, 174.8) * mm});
            skLineSegment(sketch, "E3628", {"start": v(-0.42, 174.8) * mm, "end": v(-0.4, 174.78) * mm});
            skLineSegment(sketch, "E3629", {"start": v(-0.4, 174.78) * mm, "end": v(-0.2, 174.5) * mm});
            skLineSegment(sketch, "E3630", {"start": v(-0.2, 174.5) * mm, "end": v(-0.18, 174.45) * mm});
            skLineSegment(sketch, "E3631", {"start": v(-0.18, 174.45) * mm, "end": v(-0.16, 174.42) * mm});
            skLineSegment(sketch, "E3632", {"start": v(-0.16, 174.42) * mm, "end": v(-0.04, 174.1) * mm});
            skLineSegment(sketch, "E3633", {"start": v(-0.04, 174.1) * mm, "end": v(-0.03, 174.07) * mm});
            skLineSegment(sketch, "E3634", {"start": v(-0.03, 174.07) * mm, "end": v(-0.03, 174.04) * mm});
            skLineSegment(sketch, "E3635", {"start": v(-0.03, 174.04) * mm, "end": v(0, 173.83) * mm});
            skLineSegment(sketch, "E3636", {"start": v(0, 173.83) * mm, "end": v(0, 173.8) * mm});
            skLineSegment(sketch, "E3637", {"start": v(0, 173.8) * mm, "end": v(0.02, 173.73) * mm});
            skLineSegment(sketch, "E3638", {"start": v(0.02, 173.73) * mm, "end": v(0.06, 173.5) * mm});
            skLineSegment(sketch, "E3639", {"start": v(0.06, 173.5) * mm, "end": v(0.12, 173.4) * mm});
            skLineSegment(sketch, "E3640", {"start": v(0.12, 173.4) * mm, "end": v(0.14, 173.39) * mm});
            skLineSegment(sketch, "E3641", {"start": v(0.14, 173.39) * mm, "end": v(0.15, 173.38) * mm});
            skLineSegment(sketch, "E3642", {"start": v(0.15, 173.38) * mm, "end": v(0.27, 173.3) * mm});
            skLineSegment(sketch, "E3643", {"start": v(0.27, 173.3) * mm, "end": v(0.5, 173.13) * mm});
            skLineSegment(sketch, "E3644", {"start": v(0.5, 173.13) * mm, "end": v(0.76, 172.98) * mm});
            skLineSegment(sketch, "E3645", {"start": v(0.76, 172.98) * mm, "end": v(0.91, 172.91) * mm});
            skLineSegment(sketch, "E3646", {"start": v(0.91, 172.91) * mm, "end": v(0.96, 172.92) * mm});
            skLineSegment(sketch, "E3647", {"start": v(0.96, 172.92) * mm, "end": v(1.01, 172.92) * mm});
            skLineSegment(sketch, "E3648", {"start": v(1.01, 172.92) * mm, "end": v(1.16, 173) * mm});
            skLineSegment(sketch, "E3649", {"start": v(1.16, 173) * mm, "end": v(1.15, 173.02) * mm});
            skLineSegment(sketch, "E3650", {"start": v(1.15, 173.02) * mm, "end": v(1, 173.34) * mm});
            skLineSegment(sketch, "E3651", {"start": v(1, 173.34) * mm, "end": v(0.93, 174.08) * mm});
            skLineSegment(sketch, "E3652", {"start": v(0.93, 174.08) * mm, "end": v(0.96, 174.3) * mm});
            skLineSegment(sketch, "E3653", {"start": v(0.96, 174.3) * mm, "end": v(0.98, 174.34) * mm});
            skLineSegment(sketch, "E3654", {"start": v(0.98, 174.34) * mm, "end": v(1.13, 174.84) * mm});
            skLineSegment(sketch, "E3655", {"start": v(1.13, 174.84) * mm, "end": v(1.15, 174.9) * mm});
            skLineSegment(sketch, "E3656", {"start": v(1.15, 174.9) * mm, "end": v(1.16, 174.92) * mm});
            skLineSegment(sketch, "E3657", {"start": v(1.16, 174.92) * mm, "end": v(1.48, 175) * mm});
            skLineSegment(sketch, "E3658", {"start": v(1.48, 175) * mm, "end": v(1.52, 175) * mm});
            skLineSegment(sketch, "E3659", {"start": v(1.52, 175) * mm, "end": v(1.66, 174.98) * mm});
            skLineSegment(sketch, "E3660", {"start": v(1.66, 174.98) * mm, "end": v(1.9, 174.9) * mm});
            skLineSegment(sketch, "E3661", {"start": v(1.9, 174.9) * mm, "end": v(1.95, 174.86) * mm});
            skLineSegment(sketch, "E3662", {"start": v(1.95, 174.86) * mm, "end": v(1.97, 174.85) * mm});
            skLineSegment(sketch, "E3663", {"start": v(1.97, 174.85) * mm, "end": v(2.15, 174.75) * mm});
            skLineSegment(sketch, "E3664", {"start": v(2.15, 174.75) * mm, "end": v(2.17, 174.74) * mm});
            skLineSegment(sketch, "E3665", {"start": v(2.17, 174.74) * mm, "end": v(2.2, 174.72) * mm});
            skLineSegment(sketch, "E3666", {"start": v(2.2, 174.72) * mm, "end": v(2.35, 174.55) * mm});
            skLineSegment(sketch, "E3667", {"start": v(2.35, 174.55) * mm, "end": v(2.35, 174.54) * mm});
            skLineSegment(sketch, "E3668", {"start": v(2.35, 174.54) * mm, "end": v(2.35, 174.53) * mm});
            skLineSegment(sketch, "E3669", {"start": v(2.35, 174.53) * mm, "end": v(2.3, 174.46) * mm});
            skLineSegment(sketch, "E3670", {"start": v(2.3, 174.46) * mm, "end": v(2.3, 174.45) * mm});
            skLineSegment(sketch, "E3671", {"start": v(2.3, 174.45) * mm, "end": v(2.3, 174.42) * mm});
            skLineSegment(sketch, "E3672", {"start": v(2.3, 174.42) * mm, "end": v(2.28, 174.34) * mm});
            skLineSegment(sketch, "E3673", {"start": v(2.28, 174.34) * mm, "end": v(2.28, 174.33) * mm});
            skLineSegment(sketch, "E3674", {"start": v(2.28, 174.33) * mm, "end": v(2.47, 174.18) * mm});
            skLineSegment(sketch, "E3675", {"start": v(2.47, 174.18) * mm, "end": v(2.5, 174.16) * mm});
            skLineSegment(sketch, "E3676", {"start": v(2.5, 174.16) * mm, "end": v(2.54, 174.1) * mm});
            skLineSegment(sketch, "E3677", {"start": v(2.54, 174.1) * mm, "end": v(2.55, 174.1) * mm});
            skLineSegment(sketch, "E3678", {"start": v(2.55, 174.1) * mm, "end": v(2.55, 174.1) * mm});
            skLineSegment(sketch, "E3679", {"start": v(2.55, 174.1) * mm, "end": v(2.6, 173.98) * mm});
            skLineSegment(sketch, "E3680", {"start": v(2.6, 173.98) * mm, "end": v(2.6, 173.97) * mm});
            skLineSegment(sketch, "E3681", {"start": v(2.6, 173.97) * mm, "end": v(2.6, 173.95) * mm});
            skLineSegment(sketch, "E3682", {"start": v(2.6, 173.95) * mm, "end": v(2.75, 173.79) * mm});
            skLineSegment(sketch, "E3683", {"start": v(2.75, 173.79) * mm, "end": v(2.8, 173.76) * mm});
            skLineSegment(sketch, "E3684", {"start": v(2.8, 173.76) * mm, "end": v(2.83, 173.75) * mm});
            skLineSegment(sketch, "E3685", {"start": v(2.83, 173.75) * mm, "end": v(3.13, 173.68) * mm});
            skLineSegment(sketch, "E3686", {"start": v(3.13, 173.68) * mm, "end": v(3.6, 173.64) * mm});
            skLineSegment(sketch, "E3687", {"start": v(3.6, 173.64) * mm, "end": v(3.76, 173.64) * mm});
            skLineSegment(sketch, "E3688", {"start": v(3.76, 173.64) * mm, "end": v(3.89, 173.64) * mm});
            skLineSegment(sketch, "E3689", {"start": v(3.89, 173.64) * mm, "end": v(3.96, 173.64) * mm});
            skLineSegment(sketch, "E3690", {"start": v(3.96, 173.64) * mm, "end": v(4.2, 173.61) * mm});
            skLineSegment(sketch, "E3691", {"start": v(4.2, 173.61) * mm, "end": v(4.44, 173.53) * mm});
            skLineSegment(sketch, "E3692", {"start": v(4.44, 173.53) * mm, "end": v(4.46, 173.5) * mm});
            skLineSegment(sketch, "E3693", {"start": v(4.46, 173.5) * mm, "end": v(4.49, 173.48) * mm});
            skLineSegment(sketch, "E3694", {"start": v(4.49, 173.48) * mm, "end": v(4.53, 173.17) * mm});
            skLineSegment(sketch, "E3695", {"start": v(4.53, 173.17) * mm, "end": v(4.5, 172.64) * mm});
            skLineSegment(sketch, "E3696", {"start": v(4.5, 172.64) * mm, "end": v(4.5, 172.5) * mm});
            skLineSegment(sketch, "E3697", {"start": v(4.5, 172.5) * mm, "end": v(4.5, 172.36) * mm});
            skLineSegment(sketch, "E3698", {"start": v(4.5, 172.36) * mm, "end": v(4.48, 171.96) * mm});
            skLineSegment(sketch, "E3699", {"start": v(4.48, 171.96) * mm, "end": v(4.44, 171.76) * mm});
            skLineSegment(sketch, "E3700", {"start": v(4.44, 171.76) * mm, "end": v(4.43, 171.73) * mm});
            skLineSegment(sketch, "E3701", {"start": v(4.43, 171.73) * mm, "end": v(4.43, 171.7) * mm});
            skLineSegment(sketch, "E3702", {"start": v(4.43, 171.7) * mm, "end": v(4.22, 171.51) * mm});
            skLineSegment(sketch, "E3703", {"start": v(4.22, 171.51) * mm, "end": v(4.15, 171.51) * mm});
            skLineSegment(sketch, "E3704", {"start": v(4.15, 171.51) * mm, "end": v(4.1, 171.52) * mm});
            skLineSegment(sketch, "E3705", {"start": v(4.1, 171.52) * mm, "end": v(3.84, 171.53) * mm});
            skLineSegment(sketch, "E3706", {"start": v(3.84, 171.53) * mm, "end": v(3.82, 171.52) * mm});
            skLineSegment(sketch, "E3707", {"start": v(3.82, 171.52) * mm, "end": v(3.8, 171.52) * mm});
            skLineSegment(sketch, "E3708", {"start": v(3.8, 171.52) * mm, "end": v(3.69, 171.4) * mm});
            skLineSegment(sketch, "E3709", {"start": v(3.69, 171.4) * mm, "end": v(3.61, 171.18) * mm});
            skLineSegment(sketch, "E3710", {"start": v(3.61, 171.18) * mm, "end": v(3.6, 171.14) * mm});
            skLineSegment(sketch, "E3711", {"start": v(3.6, 171.14) * mm, "end": v(3.6, 171.12) * mm});
            skLineSegment(sketch, "E3712", {"start": v(3.6, 171.12) * mm, "end": v(3.5, 170.9) * mm});
            skLineSegment(sketch, "E3713", {"start": v(3.5, 170.9) * mm, "end": v(3.48, 170.89) * mm});
            skLineSegment(sketch, "E3714", {"start": v(3.48, 170.89) * mm, "end": v(3.46, 170.88) * mm});
            skLineSegment(sketch, "E3715", {"start": v(3.46, 170.88) * mm, "end": v(3.34, 170.8) * mm});
            skLineSegment(sketch, "E3716", {"start": v(3.34, 170.8) * mm, "end": v(3.33, 170.78) * mm});
            skLineSegment(sketch, "E3717", {"start": v(3.33, 170.78) * mm, "end": v(3.31, 170.76) * mm});
            skLineSegment(sketch, "E3718", {"start": v(3.31, 170.76) * mm, "end": v(3.2, 170.48) * mm});
            skLineSegment(sketch, "E3719", {"start": v(3.2, 170.48) * mm, "end": v(3.2, 170.44) * mm});
            skLineSegment(sketch, "E3720", {"start": v(3.2, 170.44) * mm, "end": v(3.2, 170.4) * mm});
            skLineSegment(sketch, "E3721", {"start": v(3.2, 170.4) * mm, "end": v(3.12, 170.21) * mm});
            skLineSegment(sketch, "E3722", {"start": v(3.12, 170.21) * mm, "end": v(3, 170.07) * mm});
            skLineSegment(sketch, "E3723", {"start": v(3, 170.07) * mm, "end": v(3, 170.05) * mm});
            skLineSegment(sketch, "E3724", {"start": v(3, 170.05) * mm, "end": v(2.96, 170) * mm});
            skLineSegment(sketch, "E3725", {"start": v(2.96, 170) * mm, "end": v(2.85, 169.59) * mm});
            skLineSegment(sketch, "E3726", {"start": v(2.85, 169.59) * mm, "end": v(2.85, 169.45) * mm});
            skLineSegment(sketch, "E3727", {"start": v(2.85, 169.45) * mm, "end": v(2.85, 169.32) * mm});
            skLineSegment(sketch, "E3728", {"start": v(2.85, 169.32) * mm, "end": v(2.64, 168.97) * mm});
            skLineSegment(sketch, "E3729", {"start": v(2.64, 168.97) * mm, "end": v(2.6, 168.94) * mm});
            skLineSegment(sketch, "E3730", {"start": v(2.6, 168.94) * mm, "end": v(2.54, 168.9) * mm});
            skLineSegment(sketch, "E3731", {"start": v(2.54, 168.9) * mm, "end": v(2.15, 168.83) * mm});
            skLineSegment(sketch, "E3732", {"start": v(2.15, 168.83) * mm, "end": v(1.69, 168.95) * mm});
            skLineSegment(sketch, "E3733", {"start": v(1.69, 168.95) * mm, "end": v(1.6, 169) * mm});
            skLineSegment(sketch, "E3734", {"start": v(1.6, 169) * mm, "end": v(1.56, 169.02) * mm});
            skLineSegment(sketch, "E3735", {"start": v(1.56, 169.02) * mm, "end": v(1.18, 169.28) * mm});
            skLineSegment(sketch, "E3736", {"start": v(1.18, 169.28) * mm, "end": v(1.14, 169.3) * mm});
            skLineSegment(sketch, "E3737", {"start": v(1.14, 169.3) * mm, "end": v(1.13, 169.3) * mm});
            skLineSegment(sketch, "E3738", {"start": v(1.13, 169.3) * mm, "end": v(1.06, 169.33) * mm});
            skLineSegment(sketch, "E3739", {"start": v(1.06, 169.33) * mm, "end": v(1.05, 169.32) * mm});
            skLineSegment(sketch, "E3740", {"start": v(1.05, 169.32) * mm, "end": v(1.1, 169.23) * mm});
            skLineSegment(sketch, "E3741", {"start": v(1.1, 169.23) * mm, "end": v(1.26, 169.03) * mm});
            skLineSegment(sketch, "E3742", {"start": v(1.26, 169.03) * mm, "end": v(1.3, 168.98) * mm});
            skLineSegment(sketch, "E3743", {"start": v(1.3, 168.98) * mm, "end": v(1.33, 168.95) * mm});
            skLineSegment(sketch, "E3744", {"start": v(1.33, 168.95) * mm, "end": v(1.58, 168.73) * mm});
            skLineSegment(sketch, "E3745", {"start": v(1.58, 168.73) * mm, "end": v(1.6, 168.71) * mm});
            skLineSegment(sketch, "E3746", {"start": v(1.6, 168.71) * mm, "end": v(1.75, 168.62) * mm});
            skLineSegment(sketch, "E3747", {"start": v(1.75, 168.62) * mm, "end": v(2.25, 168.4) * mm});
            skLineSegment(sketch, "E3748", {"start": v(2.25, 168.4) * mm, "end": v(2.8, 168.3) * mm});
            skLineSegment(sketch, "E3749", {"start": v(2.8, 168.3) * mm, "end": v(3.2, 168.42) * mm});
            skLineSegment(sketch, "E3750", {"start": v(3.2, 168.42) * mm, "end": v(3.4, 168.65) * mm});
            skLineSegment(sketch, "E3751", {"start": v(3.4, 168.65) * mm, "end": v(3.42, 168.74) * mm});
            skLineSegment(sketch, "E3752", {"start": v(3.42, 168.74) * mm, "end": v(3.45, 168.83) * mm});
            skLineSegment(sketch, "E3753", {"start": v(3.45, 168.83) * mm, "end": v(3.78, 169.33) * mm});
            skLineSegment(sketch, "E3754", {"start": v(3.78, 169.33) * mm, "end": v(4.33, 170.01) * mm});
            skLineSegment(sketch, "E3755", {"start": v(4.33, 170.01) * mm, "end": v(4.46, 170.2) * mm});
            skLineSegment(sketch, "E3756", {"start": v(4.46, 170.2) * mm, "end": v(4.58, 170.38) * mm});
            skLineSegment(sketch, "E3757", {"start": v(4.58, 170.38) * mm, "end": v(5.13, 171.02) * mm});
            skLineSegment(sketch, "E3758", {"start": v(5.13, 171.02) * mm, "end": v(5.6, 171.7) * mm});
            skLineSegment(sketch, "E3759", {"start": v(5.6, 171.7) * mm, "end": v(5.68, 171.93) * mm});
            skLineSegment(sketch, "E3760", {"start": v(5.68, 171.93) * mm, "end": v(5.73, 172.03) * mm});
            skLineSegment(sketch, "E3761", {"start": v(5.73, 172.03) * mm, "end": v(5.86, 172.7) * mm});
            skLineSegment(sketch, "E3762", {"start": v(5.86, 172.7) * mm, "end": v(5.93, 173.41) * mm});
            skLineSegment(sketch, "E3763", {"start": v(5.93, 173.41) * mm, "end": v(5.95, 173.55) * mm});
            skLineSegment(sketch, "E3764", {"start": v(5.95, 173.55) * mm, "end": v(5.86, 173.58) * mm});
            skLineSegment(sketch, "E3765", {"start": v(5.86, 173.58) * mm, "end": v(5.34, 173.8) * mm});
            skLineSegment(sketch, "E3766", {"start": v(5.34, 173.8) * mm, "end": v(4.8, 174.15) * mm});
            skLineSegment(sketch, "E3767", {"start": v(4.8, 174.15) * mm, "end": v(4.69, 174.24) * mm});
            skLineSegment(sketch, "E3768", {"start": v(4.69, 174.24) * mm, "end": v(4.63, 174.28) * mm});
            skLineSegment(sketch, "E3769", {"start": v(4.63, 174.28) * mm, "end": v(4.1, 174.8) * mm});
            skLineSegment(sketch, "E3770", {"start": v(4.1, 174.8) * mm, "end": v(4.06, 174.86) * mm});
            skLineSegment(sketch, "E3771", {"start": v(4.06, 174.86) * mm, "end": v(3.96, 174.97) * mm});
            skLineSegment(sketch, "E3772", {"start": v(3.96, 174.97) * mm, "end": v(3.71, 175.34) * mm});
            skLineSegment(sketch, "E3773", {"start": v(3.71, 175.34) * mm, "end": v(3.49, 175.72) * mm});
            skLineSegment(sketch, "E3774", {"start": v(3.49, 175.72) * mm, "end": v(3.23, 176.1) * mm});
            skLineSegment(sketch, "E3775", {"start": v(3.23, 176.1) * mm, "end": v(2.93, 176.47) * mm});
            skLineSegment(sketch, "E3776", {"start": v(2.93, 176.47) * mm, "end": v(2.83, 176.58) * mm});
            skLineSegment(sketch, "E3777", {"start": v(2.83, 176.58) * mm, "end": v(2.82, 176.59) * mm});
            skLineSegment(sketch, "E3778", {"start": v(2.82, 176.59) * mm, "end": v(2.75, 176.67) * mm});
            skLineSegment(sketch, "E3779", {"start": v(2.75, 176.67) * mm, "end": v(2.74, 176.68) * mm});
            skLineSegment(sketch, "E3780", {"start": v(2.74, 176.68) * mm, "end": v(2.72, 176.7) * mm});
            skLineSegment(sketch, "E3781", {"start": v(2.72, 176.7) * mm, "end": v(2.56, 176.84) * mm});
            skLineSegment(sketch, "E3782", {"start": v(2.56, 176.84) * mm, "end": v(2.55, 176.85) * mm});
            skLineSegment(sketch, "E3783", {"start": v(2.55, 176.85) * mm, "end": v(2.53, 176.88) * mm});
            skLineSegment(sketch, "E3784", {"start": v(2.53, 176.88) * mm, "end": v(2.47, 176.93) * mm});
            skLineSegment(sketch, "E3785", {"start": v(2.47, 176.93) * mm, "end": v(2.25, 177.08) * mm});
            skLineSegment(sketch, "E3786", {"start": v(2.25, 177.08) * mm, "end": v(2.09, 177.17) * mm});
            skLineSegment(sketch, "E3787", {"start": v(2.09, 177.17) * mm, "end": v(2.06, 177.19) * mm});
            skLineSegment(sketch, "E3788", {"start": v(2.06, 177.19) * mm, "end": v(2.05, 177.2) * mm});
            skLineSegment(sketch, "E3789", {"start": v(2.05, 177.2) * mm, "end": v(2, 177.24) * mm});
            skLineSegment(sketch, "E3790", {"start": v(2, 177.24) * mm, "end": v(2.2, 177.23) * mm});
            skLineSegment(sketch, "E3791", {"start": v(2.2, 177.23) * mm, "end": v(2.26, 177.2) * mm});
            skLineSegment(sketch, "E3792", {"start": v(2.26, 177.2) * mm, "end": v(2.33, 177.18) * mm});
            skLineSegment(sketch, "E3793", {"start": v(2.33, 177.18) * mm, "end": v(2.74, 176.95) * mm});
            skLineSegment(sketch, "E3794", {"start": v(2.74, 176.95) * mm, "end": v(3.3, 176.56) * mm});
            skLineSegment(sketch, "E3795", {"start": v(3.3, 176.56) * mm, "end": v(3.42, 176.45) * mm});
            skLineSegment(sketch, "E3796", {"start": v(3.42, 176.45) * mm, "end": v(3.5, 176.38) * mm});
            skLineSegment(sketch, "E3797", {"start": v(3.5, 176.38) * mm, "end": v(4.15, 175.7) * mm});
            skLineSegment(sketch, "E3798", {"start": v(4.15, 175.7) * mm, "end": v(4.2, 175.64) * mm});
            skLineSegment(sketch, "E3799", {"start": v(4.2, 175.64) * mm, "end": v(4.3, 175.52) * mm});
            skLineSegment(sketch, "E3800", {"start": v(4.3, 175.52) * mm, "end": v(5.1, 174.44) * mm});
            skLineSegment(sketch, "E3801", {"start": v(5.1, 174.44) * mm, "end": v(5.2, 174.34) * mm});
            skLineSegment(sketch, "E3802", {"start": v(5.2, 174.34) * mm, "end": v(5.22, 174.31) * mm});
            skLineSegment(sketch, "E3803", {"start": v(5.22, 174.31) * mm, "end": v(5.48, 174.08) * mm});
            skLineSegment(sketch, "E3804", {"start": v(5.48, 174.08) * mm, "end": v(5.52, 174.05) * mm});
            skLineSegment(sketch, "E3805", {"start": v(5.52, 174.05) * mm, "end": v(5.54, 174.04) * mm});
            skLineSegment(sketch, "E3806", {"start": v(5.54, 174.04) * mm, "end": v(5.79, 173.87) * mm});
            skLineSegment(sketch, "E3807", {"start": v(5.79, 173.87) * mm, "end": v(5.8, 173.85) * mm});
            skLineSegment(sketch, "E3808", {"start": v(5.8, 173.85) * mm, "end": v(5.85, 173.83) * mm});
            skLineSegment(sketch, "E3809", {"start": v(5.85, 173.83) * mm, "end": v(6.17, 173.67) * mm});
            skLineSegment(sketch, "E3810", {"start": v(6.17, 173.67) * mm, "end": v(6.19, 173.66) * mm});
            skLineSegment(sketch, "E3811", {"start": v(6.19, 173.66) * mm, "end": v(6.37, 173.59) * mm});
            skLineSegment(sketch, "E3812", {"start": v(6.37, 173.59) * mm, "end": v(6.93, 173.42) * mm});
            skLineSegment(sketch, "E3813", {"start": v(6.93, 173.42) * mm, "end": v(7.6, 173.32) * mm});
            skLineSegment(sketch, "E3814", {"start": v(7.6, 173.32) * mm, "end": v(8.16, 173.31) * mm});
            skLineSegment(sketch, "E3815", {"start": v(8.16, 173.31) * mm, "end": v(8.46, 173.35) * mm});
            skLineSegment(sketch, "E3816", {"start": v(8.46, 173.35) * mm, "end": v(8.56, 173.38) * mm});
            skLineSegment(sketch, "E3817", {"start": v(8.56, 173.38) * mm, "end": v(8.7, 173.42) * mm});
            skLineSegment(sketch, "E3818", {"start": v(8.7, 173.42) * mm, "end": v(9.1, 173.61) * mm});
            skLineSegment(sketch, "E3819", {"start": v(9.1, 173.61) * mm, "end": v(9.25, 173.81) * mm});
            skLineSegment(sketch, "E3820", {"start": v(9.25, 173.81) * mm, "end": v(9.24, 173.85) * mm});
            skLineSegment(sketch, "E3821", {"start": v(9.24, 173.85) * mm, "end": v(9.25, 173.84) * mm});
            skLineSegment(sketch, "E3822", {"start": v(9.25, 173.84) * mm, "end": v(9.38, 173.73) * mm});
            skLineSegment(sketch, "E3823", {"start": v(9.38, 173.73) * mm, "end": v(9.4, 173.71) * mm});
            skLineSegment(sketch, "E3824", {"start": v(9.4, 173.71) * mm, "end": v(9.42, 173.7) * mm});
            skLineSegment(sketch, "E3825", {"start": v(9.42, 173.7) * mm, "end": v(9.61, 173.5) * mm});
            skLineSegment(sketch, "E3826", {"start": v(9.61, 173.5) * mm, "end": v(9.63, 173.49) * mm});
            skLineSegment(sketch, "E3827", {"start": v(9.63, 173.49) * mm, "end": v(9.65, 173.49) * mm});
            skLineSegment(sketch, "E3828", {"start": v(9.65, 173.49) * mm, "end": v(9.72, 173.45) * mm});
            skLineSegment(sketch, "E3829", {"start": v(9.72, 173.45) * mm, "end": v(9.72, 173.45) * mm});
            skLineSegment(sketch, "E3830", {"start": v(9.72, 173.45) * mm, "end": v(9.76, 173.43) * mm});
            skLineSegment(sketch, "E3831", {"start": v(9.76, 173.43) * mm, "end": v(10, 173.4) * mm});
            skLineSegment(sketch, "E3832", {"start": v(10, 173.4) * mm, "end": v(10.01, 173.39) * mm});
            skLineSegment(sketch, "E3833", {"start": v(10.01, 173.39) * mm, "end": v(10.02, 173.38) * mm});
            skLineSegment(sketch, "E3834", {"start": v(10.02, 173.38) * mm, "end": v(9.97, 173.21) * mm});
            skLineSegment(sketch, "E3835", {"start": v(9.97, 173.21) * mm, "end": v(9.95, 173.2) * mm});
            skLineSegment(sketch, "E3836", {"start": v(9.95, 173.2) * mm, "end": v(10, 173.08) * mm});
            skLineSegment(sketch, "E3837", {"start": v(10, 173.08) * mm, "end": v(10.01, 173.06) * mm});
            skLineSegment(sketch, "E3838", {"start": v(10.01, 173.06) * mm, "end": v(10.03, 173.03) * mm});
            skLineSegment(sketch, "E3839", {"start": v(10.03, 173.03) * mm, "end": v(10.25, 172.95) * mm});
            skLineSegment(sketch, "E3840", {"start": v(10.25, 172.95) * mm, "end": v(10.45, 172.92) * mm});
            skLineSegment(sketch, "E3841", {"start": v(10.45, 172.92) * mm, "end": v(10.67, 172.91) * mm});
            skLineSegment(sketch, "E3842", {"start": v(10.67, 172.91) * mm, "end": v(10.88, 172.96) * mm});
            skLineSegment(sketch, "E3843", {"start": v(10.88, 172.96) * mm, "end": v(10.88, 172.98) * mm});
            skLineSegment(sketch, "E3844", {"start": v(10.88, 172.98) * mm, "end": v(10.86, 173.07) * mm});
            skLineSegment(sketch, "E3845", {"start": v(10.86, 173.07) * mm, "end": v(10.76, 173.28) * mm});
            skLineSegment(sketch, "E3846", {"start": v(10.76, 173.28) * mm, "end": v(10.6, 173.55) * mm});
            skLineSegment(sketch, "E3847", {"start": v(10.6, 173.55) * mm, "end": v(10.53, 173.64) * mm});
            skLineSegment(sketch, "E3848", {"start": v(10.53, 173.64) * mm, "end": v(10.51, 173.68) * mm});
            skLineSegment(sketch, "E3849", {"start": v(10.51, 173.68) * mm, "end": v(10.34, 173.83) * mm});
            skLineSegment(sketch, "E3850", {"start": v(10.34, 173.83) * mm, "end": v(9.96, 174.12) * mm});
            skLineSegment(sketch, "E3851", {"start": v(9.96, 174.12) * mm, "end": v(9.56, 174.41) * mm});
            skLineSegment(sketch, "E3852", {"start": v(9.56, 174.41) * mm, "end": v(9.35, 174.57) * mm});
            skLineSegment(sketch, "E3853", {"start": v(9.35, 174.57) * mm, "end": v(9.3, 174.6) * mm});
            skLineSegment(sketch, "E3854", {"start": v(9.3, 174.6) * mm, "end": v(9.26, 174.64) * mm});
            skLineSegment(sketch, "E3855", {"start": v(9.26, 174.64) * mm, "end": v(9.06, 174.63) * mm});
            skLineSegment(sketch, "E3856", {"start": v(9.06, 174.63) * mm, "end": v(8.97, 174.45) * mm});
            skLineSegment(sketch, "E3857", {"start": v(8.97, 174.45) * mm, "end": v(8.98, 174.4) * mm});
            skLineSegment(sketch, "E3858", {"start": v(8.98, 174.4) * mm, "end": v(8.98, 174.31) * mm});
            skLineSegment(sketch, "E3859", {"start": v(8.98, 174.31) * mm, "end": v(9.08, 174.09) * mm});
            skLineSegment(sketch, "E3860", {"start": v(9.08, 174.09) * mm, "end": v(9.1, 174.06) * mm});
            skLineSegment(sketch, "E3861", {"start": v(9.1, 174.06) * mm, "end": v(9.05, 174.1) * mm});
            skLineSegment(sketch, "E3862", {"start": v(9.05, 174.1) * mm, "end": v(8.74, 174.26) * mm});
            skLineSegment(sketch, "E3863", {"start": v(8.74, 174.26) * mm, "end": v(8.33, 174.38) * mm});
            skLineSegment(sketch, "E3864", {"start": v(8.33, 174.38) * mm, "end": v(8.25, 174.4) * mm});
            skLineSegment(sketch, "E3865", {"start": v(8.25, 174.4) * mm, "end": v(8.12, 174.42) * mm});
            skLineSegment(sketch, "E3866", {"start": v(8.12, 174.42) * mm, "end": v(7.75, 174.51) * mm});
            skLineSegment(sketch, "E3867", {"start": v(7.75, 174.51) * mm, "end": v(7.43, 174.64) * mm});
            skLineSegment(sketch, "E3868", {"start": v(7.43, 174.64) * mm, "end": v(7.19, 174.8) * mm});
            skLineSegment(sketch, "E3869", {"start": v(7.19, 174.8) * mm, "end": v(6.99, 174.96) * mm});
            skLineSegment(sketch, "E3870", {"start": v(6.99, 174.96) * mm, "end": v(6.92, 175.02) * mm});
            skLineSegment(sketch, "E3871", {"start": v(6.92, 175.02) * mm, "end": v(6.9, 175.03) * mm});
            skLineSegment(sketch, "E3872", {"start": v(6.9, 175.03) * mm, "end": v(6.85, 175.12) * mm});
            skLineSegment(sketch, "E3873", {"start": v(6.85, 175.12) * mm, "end": v(7, 175.37) * mm});
            skLineSegment(sketch, "E3874", {"start": v(7, 175.37) * mm, "end": v(7.36, 175.95) * mm});
            skLineSegment(sketch, "E3875", {"start": v(7.36, 175.95) * mm, "end": v(7.86, 176.66) * mm});
            skLineSegment(sketch, "E3876", {"start": v(7.86, 176.66) * mm, "end": v(8.23, 177.13) * mm});
            skLineSegment(sketch, "E3877", {"start": v(8.23, 177.13) * mm, "end": v(8.37, 177.27) * mm});
            skLineSegment(sketch, "E3878", {"start": v(8.37, 177.27) * mm, "end": v(8.53, 177.43) * mm});
            skLineSegment(sketch, "E3879", {"start": v(8.53, 177.43) * mm, "end": v(9.26, 178.1) * mm});
            skLineSegment(sketch, "E3880", {"start": v(9.26, 178.1) * mm, "end": v(9.74, 178.65) * mm});
            skLineSegment(sketch, "E3881", {"start": v(9.74, 178.65) * mm, "end": v(9.76, 178.75) * mm});
            skLineSegment(sketch, "E3882", {"start": v(9.76, 178.75) * mm, "end": v(9.8, 178.85) * mm});
            skLineSegment(sketch, "E3883", {"start": v(9.8, 178.85) * mm, "end": v(9.69, 179.37) * mm});
            skLineSegment(sketch, "E3884", {"start": v(9.69, 179.37) * mm, "end": v(9.2, 180.43) * mm});
            skLineSegment(sketch, "E3885", {"start": v(9.2, 180.43) * mm, "end": v(8.2, 181.69) * mm});
            skLineSegment(sketch, "E3886", {"start": v(8.2, 181.69) * mm, "end": v(7.05, 182.63) * mm});
            skLineSegment(sketch, "E3887", {"start": v(7.05, 182.63) * mm, "end": v(6.62, 182.86) * mm});
            skLineSegment(sketch, "E3888", {"start": v(6.62, 182.86) * mm, "end": v(6.2, 183.1) * mm});
            skLineSegment(sketch, "E3889", {"start": v(6.2, 183.1) * mm, "end": v(4.86, 183.67) * mm});
            skLineSegment(sketch, "E3890", {"start": v(4.86, 183.67) * mm, "end": v(3.39, 184.07) * mm});
            skLineSegment(sketch, "E3891", {"start": v(3.39, 184.07) * mm, "end": v(2.27, 184.17) * mm});
            skLineSegment(sketch, "E3892", {"start": v(2.27, 184.17) * mm, "end": v(1.71, 184.14) * mm});
            skLineSegment(sketch, "E3893", {"start": v(1.71, 184.14) * mm, "end": v(1.55, 184.1) * mm});
            skLineSegment(sketch, "E3894", {"start": v(1.55, 184.1) * mm, "end": v(1.38, 184.05) * mm});
            skLineSegment(sketch, "E3895", {"start": v(1.38, 184.05) * mm, "end": v(0.91, 183.73) * mm});
            skLineSegment(sketch, "E3896", {"start": v(0.91, 183.73) * mm, "end": v(0.76, 183.3) * mm});
            skLineSegment(sketch, "E3897", {"start": v(0.76, 183.3) * mm, "end": v(0.76, 183.2) * mm});
            skLineSegment(sketch, "E3898", {"start": v(0.76, 183.2) * mm, "end": v(0.75, 183.1) * mm});
            skLineSegment(sketch, "E3899", {"start": v(0.75, 183.1) * mm, "end": v(0.69, 182.35) * mm});
            skLineSegment(sketch, "E3900", {"start": v(0.69, 182.35) * mm, "end": v(0.56, 181.45) * mm});
            skLineSegment(sketch, "E3901", {"start": v(0.56, 181.45) * mm, "end": v(0.52, 181.28) * mm});
            skLineSegment(sketch, "E3902", {"start": v(0.52, 181.28) * mm, "end": v(0.48, 181.1) * mm});
            skLineSegment(sketch, "E3903", {"start": v(0.48, 181.1) * mm, "end": v(0.34, 180.52) * mm});
            skLineSegment(sketch, "E3904", {"start": v(0.34, 180.52) * mm, "end": v(0.28, 180.23) * mm});
            skLineSegment(sketch, "E3905", {"start": v(0.28, 180.23) * mm, "end": v(0.28, 180.13) * mm});
            skLineSegment(sketch, "E3906", {"start": v(0.28, 180.13) * mm, "end": v(0.28, 180.1) * mm});
            skLineSegment(sketch, "E3907", {"start": v(0.28, 180.1) * mm, "end": v(0.47, 179.76) * mm});
            skLineSegment(sketch, "E3908", {"start": v(0.47, 179.76) * mm, "end": v(0.5, 179.72) * mm});
            skLineSegment(sketch, "E3909", {"start": v(0.5, 179.72) * mm, "end": v(0.54, 179.68) * mm});
            skLineSegment(sketch, "E3910", {"start": v(0.54, 179.68) * mm, "end": v(1.02, 179.27) * mm});
            skLineSegment(sketch, "E3911", {"start": v(1.02, 179.27) * mm, "end": v(1.07, 179.22) * mm});
            skLineSegment(sketch, "E3912", {"start": v(1.07, 179.22) * mm, "end": v(1.16, 179.15) * mm});
            skLineSegment(sketch, "E3913", {"start": v(1.16, 179.15) * mm, "end": v(1.66, 178.73) * mm});
            skLineSegment(sketch, "E3914", {"start": v(1.66, 178.73) * mm, "end": v(2.1, 178.27) * mm});
            skLineSegment(sketch, "E3915", {"start": v(2.1, 178.27) * mm, "end": v(2.16, 178.17) * mm});
            skLineSegment(sketch, "E3916", {"start": v(2.16, 178.17) * mm, "end": v(2.19, 178.13) * mm});
            skLineSegment(sketch, "E3917", {"start": v(2.19, 178.13) * mm, "end": v(2.25, 177.98) * mm});
            skLineSegment(sketch, "E3918", {"start": v(2.25, 177.98) * mm, "end": v(2.17, 177.94) * mm});
            skLineSegment(sketch, "E3919", {"start": v(2.17, 177.94) * mm, "end": v(1.99, 178) * mm});
            skLineSegment(sketch, "E3920", {"start": v(1.99, 178) * mm, "end": v(1.84, 178.09) * mm});
            skLineSegment(sketch, "E3921", {"start": v(1.84, 178.09) * mm, "end": v(1.8, 178.12) * mm});
            skLineSegment(sketch, "E3922", {"start": v(1.8, 178.12) * mm, "end": v(1.73, 178.16) * mm});
            skLineSegment(sketch, "E3923", {"start": v(1.73, 178.16) * mm, "end": v(1.07, 178.57) * mm});
            skLineSegment(sketch, "E3924", {"start": v(1.07, 178.57) * mm, "end": v(0.18, 179.03) * mm});
            skLineSegment(sketch, "E3925", {"start": v(0.18, 179.03) * mm, "end": v(0, 179.1) * mm});
            skLineSegment(sketch, "E3926", {"start": v(0, 179.1) * mm, "end": v(-0.06, 179.12) * mm});
            skLineSegment(sketch, "E3927", {"start": v(-0.06, 179.12) * mm, "end": v(-0.7, 179.34) * mm});
            skLineSegment(sketch, "E3928", {"start": v(-0.7, 179.34) * mm, "end": v(-0.76, 179.36) * mm});
            skLineSegment(sketch, "E3929", {"start": v(-0.76, 179.36) * mm, "end": v(-0.99, 179.44) * mm});
            skLineSegment(sketch, "E3930", {"start": v(-0.99, 179.44) * mm, "end": v(-1.7, 179.6) * mm});
            skLineSegment(sketch, "E3931", {"start": v(-1.7, 179.6) * mm, "end": v(-2.48, 179.63) * mm});
            skLineSegment(sketch, "E3932", {"start": v(-2.48, 179.63) * mm, "end": v(-3.12, 179.48) * mm});
            skLineSegment(sketch, "E3933", {"start": v(-3.12, 179.48) * mm, "end": v(-3.54, 179.27) * mm});
            skLineSegment(sketch, "E3934", {"start": v(-3.54, 179.27) * mm, "end": v(-3.66, 179.18) * mm});
            skLineSegment(sketch, "E3935", {"start": v(-3.66, 179.18) * mm, "end": v(-3.77, 179.09) * mm});
            skLineSegment(sketch, "E3936", {"start": v(-3.77, 179.09) * mm, "end": v(-3.9, 178.57) * mm});
            skLineSegment(sketch, "E3937", {"start": v(-3.9, 178.57) * mm, "end": v(-3.65, 178.1) * mm});
            skLineSegment(sketch, "E3938", {"start": v(-3.65, 178.1) * mm, "end": v(-3.57, 178.02) * mm});
            skSolve(sketch);
        }
        {
            var Q0;
            Q0=makeQuery(id+"F0.imprint","IMPRINT",FACE,{"disambiguationData":[TD([[makeQuery(id+"F0.imprint","IMPRINT",EDGE,{"derivedFrom":sQuery(id+"F0.wireOp",EDGE,"E0")}),-1.0]])]});
            extrude(context, id + "F2", {"entities" : qUnion([Q0]), "oppositeDirection" : true, "depth" : 2 * mm, "offsetDistance" : 25 * mm});
        }
        {
            var Q0;
            Q0=makeQuery(id+"F1.imprint","IMPRINT",FACE,{"disambiguationData":[TD([[makeQuery(id+"F1.imprint","IMPRINT",EDGE,{"derivedFrom":sQuery(id+"F1.wireOp",EDGE,"E480")}),1.0]])]});
            var Q1;
            Q1=makeQuery(id+"F1.imprint","IMPRINT",FACE,{"disambiguationData":[TD([[makeQuery(id+"F1.imprint","IMPRINT",EDGE,{"derivedFrom":sQuery(id+"F1.wireOp",EDGE,"E585")}),1.0]])]});
            var Q2;
            Q2=makeQuery(id+"F1.imprint","IMPRINT",FACE,{"disambiguationData":[TD([[makeQuery(id+"F1.imprint","IMPRINT",EDGE,{"derivedFrom":sQuery(id+"F1.wireOp",EDGE,"E691")}),1.0]])]});
            var Q3;
            Q3=makeQuery(id+"F1.imprint","IMPRINT",FACE,{"disambiguationData":[TD([[makeQuery(id+"F1.imprint","IMPRINT",EDGE,{"derivedFrom":sQuery(id+"F1.wireOp",EDGE,"E296")}),1.0]])]});
            var Q4;
            Q4=makeQuery(id+"F1.imprint","IMPRINT",FACE,{"disambiguationData":[TD([[makeQuery(id+"F1.imprint","IMPRINT",EDGE,{"derivedFrom":sQuery(id+"F1.wireOp",EDGE,"E178")}),1.0]])]});
            var Q5;
            Q5=makeQuery(id+"F1.imprint","IMPRINT",FACE,{"disambiguationData":[TD([[makeQuery(id+"F1.imprint","IMPRINT",EDGE,{"derivedFrom":sQuery(id+"F1.wireOp",EDGE,"E233")}),1.0]])]});
            var Q6;
            Q6=makeQuery(id+"F1.imprint","IMPRINT",FACE,{"disambiguationData":[TD([[makeQuery(id+"F1.imprint","IMPRINT",EDGE,{"derivedFrom":sQuery(id+"F1.wireOp",EDGE,"E249")}),1.0]])]});
            var Q7;
            Q7=makeQuery(id+"F1.imprint","IMPRINT",FACE,{"disambiguationData":[TD([[makeQuery(id+"F1.imprint","IMPRINT",EDGE,{"derivedFrom":sQuery(id+"F1.wireOp",EDGE,"E350")}),1.0]])]});
            var Q8;
            Q8=makeQuery(id+"F1.imprint","IMPRINT",FACE,{"disambiguationData":[TD([[makeQuery(id+"F1.imprint","IMPRINT",EDGE,{"derivedFrom":sQuery(id+"F1.wireOp",EDGE,"E725")}),1.0]])]});
            var Q9;
            Q9=makeQuery(id+"F1.imprint","IMPRINT",FACE,{"disambiguationData":[TD([[makeQuery(id+"F1.imprint","IMPRINT",EDGE,{"derivedFrom":sQuery(id+"F1.wireOp",EDGE,"E937")}),1.0]])]});
            var Q10;
            Q10=makeQuery(id+"F1.imprint","IMPRINT",FACE,{"disambiguationData":[TD([[makeQuery(id+"F1.imprint","IMPRINT",EDGE,{"derivedFrom":sQuery(id+"F1.wireOp",EDGE,"E953")}),1.0]])]});
            var Q11;
            Q11=makeQuery(id+"F1.imprint","IMPRINT",FACE,{"disambiguationData":[TD([[makeQuery(id+"F1.imprint","IMPRINT",EDGE,{"derivedFrom":sQuery(id+"F1.wireOp",EDGE,"E897")}),1.0]])]});
            var Q12;
            Q12=makeQuery(id+"F1.imprint","IMPRINT",FACE,{"disambiguationData":[TD([[makeQuery(id+"F1.imprint","IMPRINT",EDGE,{"derivedFrom":sQuery(id+"F1.wireOp",EDGE,"E746")}),1.0]])]});
            var Q13;
            Q13=makeQuery(id+"F1.imprint","IMPRINT",FACE,{"disambiguationData":[TD([[makeQuery(id+"F1.imprint","IMPRINT",EDGE,{"derivedFrom":sQuery(id+"F1.wireOp",EDGE,"E793")}),1.0]])]});
            var Q14;
            Q14=makeQuery(id+"F1.imprint","IMPRINT",FACE,{"disambiguationData":[TD([[makeQuery(id+"F1.imprint","IMPRINT",EDGE,{"derivedFrom":sQuery(id+"F1.wireOp",EDGE,"E998")}),-1.0]])]});
            var Q15;
            Q15=makeQuery(id+"F1.imprint","IMPRINT",FACE,{"disambiguationData":[TD([[makeQuery(id+"F1.imprint","IMPRINT",EDGE,{"derivedFrom":sQuery(id+"F1.wireOp",EDGE,"E8")}),1.0]])]});
            var Q16;
            Q16=makeQuery(id+"F1.imprint","IMPRINT",FACE,{"disambiguationData":[TD([[makeQuery(id+"F1.imprint","IMPRINT",EDGE,{"derivedFrom":sQuery(id+"F1.wireOp",EDGE,"E20")}),1.0]])]});
            var Q17;
            Q17=makeQuery(id+"F1.imprint","IMPRINT",FACE,{"disambiguationData":[TD([[makeQuery(id+"F1.imprint","IMPRINT",EDGE,{"derivedFrom":sQuery(id+"F1.wireOp",EDGE,"E32")}),1.0]])]});
            var Q18;
            Q18=makeQuery(id+"F1.imprint","IMPRINT",FACE,{"disambiguationData":[TD([[makeQuery(id+"F1.imprint","IMPRINT",EDGE,{"derivedFrom":sQuery(id+"F1.wireOp",EDGE,"E76")}),1.0]])]});
            var Q19;
            Q19=makeQuery(id+"F1.imprint","IMPRINT",FACE,{"disambiguationData":[TD([[makeQuery(id+"F1.imprint","IMPRINT",EDGE,{"derivedFrom":sQuery(id+"F1.wireOp",EDGE,"E44")}),1.0]])]});
            var Q20;
            Q20=makeQuery(id+"F1.imprint","IMPRINT",FACE,{"disambiguationData":[TD([[makeQuery(id+"F1.imprint","IMPRINT",EDGE,{"derivedFrom":sQuery(id+"F1.wireOp",EDGE,"E89")}),1.0]])]});
            var Q21;
            Q21=makeQuery(id+"F1.imprint","IMPRINT",FACE,{"disambiguationData":[TD([[makeQuery(id+"F1.imprint","IMPRINT",EDGE,{"derivedFrom":sQuery(id+"F1.wireOp",EDGE,"E106")}),1.0]])]});
            var Q22;
            Q22=makeQuery(id+"F1.imprint","IMPRINT",FACE,{"disambiguationData":[TD([[makeQuery(id+"F1.imprint","IMPRINT",EDGE,{"derivedFrom":sQuery(id+"F1.wireOp",EDGE,"E100")}),1.0]])]});
            var Q23;
            Q23=makeQuery(id+"F1.imprint","IMPRINT",FACE,{"disambiguationData":[TD([[makeQuery(id+"F1.imprint","IMPRINT",EDGE,{"derivedFrom":sQuery(id+"F1.wireOp",EDGE,"E118")}),1.0]])]});
            var Q24;
            Q24=makeQuery(id+"F1.imprint","IMPRINT",FACE,{"disambiguationData":[TD([[makeQuery(id+"F1.imprint","IMPRINT",EDGE,{"derivedFrom":sQuery(id+"F1.wireOp",EDGE,"E122")}),1.0]])]});
            var Q25;
            Q25=makeQuery(id+"F1.imprint","IMPRINT",FACE,{"disambiguationData":[TD([[makeQuery(id+"F1.imprint","IMPRINT",EDGE,{"derivedFrom":sQuery(id+"F1.wireOp",EDGE,"E132")}),1.0]])]});
            var Q26;
            Q26=makeQuery(id+"F1.imprint","IMPRINT",FACE,{"disambiguationData":[TD([[makeQuery(id+"F1.imprint","IMPRINT",EDGE,{"derivedFrom":sQuery(id+"F1.wireOp",EDGE,"E2088")}),1.0]])]});
            var Q27;
            Q27=makeQuery(id+"F1.imprint","IMPRINT",FACE,{"disambiguationData":[TD([[makeQuery(id+"F1.imprint","IMPRINT",EDGE,{"derivedFrom":sQuery(id+"F1.wireOp",EDGE,"E1118")}),-1.0]])]});
            var Q28;
            Q28=makeQuery(id+"F1.imprint","IMPRINT",FACE,{"disambiguationData":[TD([[makeQuery(id+"F1.imprint","IMPRINT",EDGE,{"derivedFrom":sQuery(id+"F1.wireOp",EDGE,"E1126")}),-1.0]])]});
            var Q29;
            Q29=makeQuery(id+"F1.imprint","IMPRINT",FACE,{"disambiguationData":[TD([[makeQuery(id+"F1.imprint","IMPRINT",EDGE,{"derivedFrom":sQuery(id+"F1.wireOp",EDGE,"E1408")}),1.0]])]});
            var Q30;
            Q30=makeQuery(id+"F1.imprint","IMPRINT",FACE,{"disambiguationData":[TD([[makeQuery(id+"F1.imprint","IMPRINT",EDGE,{"derivedFrom":sQuery(id+"F1.wireOp",EDGE,"E1808")}),1.0]])]});
            var Q31;
            Q31=makeQuery(id+"F1.imprint","IMPRINT",FACE,{"disambiguationData":[TD([[makeQuery(id+"F1.imprint","IMPRINT",EDGE,{"derivedFrom":sQuery(id+"F1.wireOp",EDGE,"E1891")}),1.0]])]});
            var Q32;
            Q32=makeQuery(id+"F1.imprint","IMPRINT",FACE,{"disambiguationData":[TD([[makeQuery(id+"F1.imprint","IMPRINT",EDGE,{"derivedFrom":sQuery(id+"F1.wireOp",EDGE,"E1214")}),1.0]])]});
            var Q33;
            Q33=makeQuery(id+"F1.imprint","IMPRINT",FACE,{"disambiguationData":[TD([[makeQuery(id+"F1.imprint","IMPRINT",EDGE,{"derivedFrom":sQuery(id+"F1.wireOp",EDGE,"E2363")}),1.0]])]});
            var Q34;
            Q34=makeQuery(id+"F1.imprint","IMPRINT",FACE,{"disambiguationData":[TD([[makeQuery(id+"F1.imprint","IMPRINT",EDGE,{"derivedFrom":sQuery(id+"F1.wireOp",EDGE,"E1153")}),1.0]])]});
            var Q35;
            Q35=makeQuery(id+"F1.imprint","IMPRINT",FACE,{"disambiguationData":[TD([[makeQuery(id+"F1.imprint","IMPRINT",EDGE,{"derivedFrom":sQuery(id+"F1.wireOp",EDGE,"E1351")}),1.0]])]});
            var Q36;
            Q36=makeQuery(id+"F1.imprint","IMPRINT",FACE,{"disambiguationData":[TD([[makeQuery(id+"F1.imprint","IMPRINT",EDGE,{"derivedFrom":sQuery(id+"F1.wireOp",EDGE,"E1684")}),1.0]])]});
            var Q37;
            Q37=makeQuery(id+"F1.imprint","IMPRINT",FACE,{"disambiguationData":[TD([[makeQuery(id+"F1.imprint","IMPRINT",EDGE,{"derivedFrom":sQuery(id+"F1.wireOp",EDGE,"E1138")}),1.0]])]});
            var Q38;
            Q38=makeQuery(id+"F1.imprint","IMPRINT",FACE,{"disambiguationData":[TD([[makeQuery(id+"F1.imprint","IMPRINT",EDGE,{"derivedFrom":sQuery(id+"F1.wireOp",EDGE,"E1202")}),1.0]])]});
            var Q39;
            Q39=makeQuery(id+"F1.imprint","IMPRINT",FACE,{"disambiguationData":[TD([[makeQuery(id+"F1.imprint","IMPRINT",EDGE,{"derivedFrom":sQuery(id+"F1.wireOp",EDGE,"E1188")}),1.0]])]});
            var Q40;
            Q40=makeQuery(id+"F1.imprint","IMPRINT",FACE,{"disambiguationData":[TD([[makeQuery(id+"F1.imprint","IMPRINT",EDGE,{"derivedFrom":sQuery(id+"F1.wireOp",EDGE,"E3544")}),1.0]])]});
            var Q41;
            Q41=makeQuery(id+"F1.imprint","IMPRINT",FACE,{"disambiguationData":[TD([[makeQuery(id+"F1.imprint","IMPRINT",EDGE,{"derivedFrom":sQuery(id+"F1.wireOp",EDGE,"E1778")}),1.0]])]});
            var Q42;
            Q42=makeQuery(id+"F1.imprint","IMPRINT",FACE,{"disambiguationData":[TD([[makeQuery(id+"F1.imprint","IMPRINT",EDGE,{"derivedFrom":sQuery(id+"F1.wireOp",EDGE,"E1792")}),1.0]])]});
            var Q43;
            Q43=makeQuery(id+"F1.imprint","IMPRINT",FACE,{"disambiguationData":[TD([[makeQuery(id+"F1.imprint","IMPRINT",EDGE,{"derivedFrom":sQuery(id+"F1.wireOp",EDGE,"E1706")}),1.0]])]});
            extrude(context, id + "F3", {"entities" : qUnion([Q0, Q1, Q2, Q3, Q4, Q5, Q6, Q7, Q8, Q9, Q10, Q11, Q12, Q13, Q14, Q15, Q16, Q17, Q18, Q19, Q20, Q21, Q22, Q23, Q24, Q25, Q26, Q27, Q28, Q29, Q30, Q31, Q32, Q33, Q34, Q35, Q36, Q37, Q38, Q39, Q40, Q41, Q42, Q43]), "operationType" : NewBodyOperationType.REMOVE, "endBound" : BoundingType.THROUGH_ALL, "oppositeDirection" : true, "depth" : 25 * mm, "offsetDistance" : 25 * mm});
        }
    });
